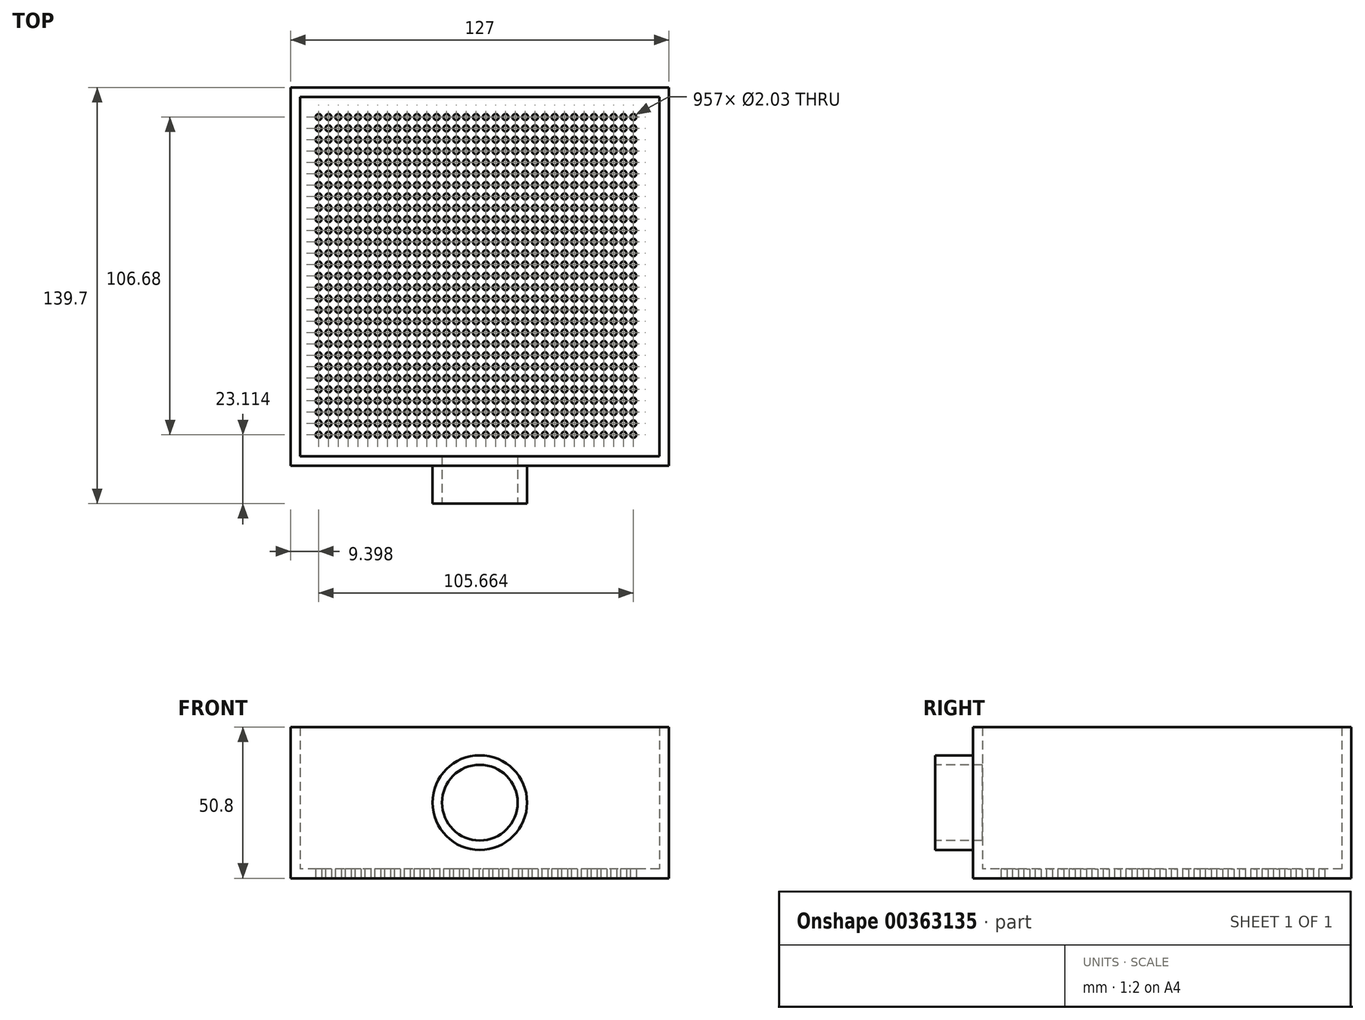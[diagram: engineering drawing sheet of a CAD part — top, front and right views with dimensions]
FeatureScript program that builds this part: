
annotation { "Feature Type Name" : "Feature", "Feature Type Description" : "" }
export const myFeature = defineFeature(function(context is Context, id is Id, definition is map)
    precondition{}
    {
        {
            var Q0;
            Q0=qCreatedBy(makeId("Top.planeOp"),FACE);
            var sketch = newSketch(context, id + "F0", { "sketchPlane" : qUnion([Q0])});
            skLineSegment(sketch, "E0.bottom", {"start": v(0, 0) * mm, "end": v(-127, 0) * mm});
            skLineSegment(sketch, "E0.top", {"start": v(0, -127) * mm, "end": v(-127, -127) * mm});
            skLineSegment(sketch, "E0.left", {"start": v(0, 0) * mm, "end": v(0, -127) * mm});
            skLineSegment(sketch, "E0.right", {"start": v(-127, 0) * mm, "end": v(-127, -127) * mm});
            skSolve(sketch);
        }
        {
            var Q0;
            Q0 = qSketchRegion(id + "F0", true);
            extrude(context, id + "F1", {"entities" : qUnion([Q0]), "depth" : 50.8 * mm});
        }
        {
            var Q0;
            Q0=makeQuery(id+"F1.opExtrude","CAP_FACE",FACE,{"disambiguationData":[OSD([sQuery(id+"F0.wireOp",EDGE,"E0.bottom"),sQuery(id+"F0.wireOp",EDGE,"E0.top"),sQuery(id+"F0.wireOp",EDGE,"E0.left"),sQuery(id+"F0.wireOp",EDGE,"E0.right")])],"isStart":false});
            shell(context, id + "F2", {"entities" : qUnion([Q0]), "thickness" : 3.17 * mm});
        }
        {
            var Q0;
            Q0=makeQuery(id+"F1.opExtrude","SWEPT_FACE",FACE,{"disambiguationData":[OSD([sQuery(id+"F0.wireOp",EDGE,"E0.top")])]});
            var sketch = newSketch(context, id + "F3", { "sketchPlane" : qUnion([Q0])});
            skCircle(sketch, "E1", {"center": v(-63.5, 25.4) * mm, "radius": 15.88 * mm});
            skSolve(sketch);
        }
        {
            var Q0;
            Q0=makeQuery(id+"F3.imprint","IMPRINT",FACE,{"disambiguationData":[TD([[makeQuery(id+"F3.imprint","IMPRINT",EDGE,{"derivedFrom":sQuery(id+"F3.wireOp",EDGE,"E1")}),1.0]])]});
            extrude(context, id + "F4", {"entities" : qUnion([Q0]), "operationType" : NewBodyOperationType.ADD, "depth" : 50.8 * mm});
        }
        {
            var Q0;
            Q0=makeQuery(id+"F4.opExtrude","CAP_FACE",FACE,{"disambiguationData":[OSD([sQuery(id+"F3.wireOp",EDGE,"E1")])],"isStart":false});
            var sketch = newSketch(context, id + "F5", { "sketchPlane" : qUnion([Q0])});
            skCircle(sketch, "E2", {"center": v(-63.5, 25.4) * mm, "radius": 12.7 * mm});
            skSolve(sketch);
        }
        {
            var Q0;
            Q0=sQuery(id+"F5.wireOp",VERTEX,"E2.center");
            var Q1;
            Q1=makeQuery(id+"F1.opExtrude","SWEPT_BODY",BODY,{"disambiguationData":[OSD([sQuery(id+"F0.wireOp",EDGE,"E0.bottom"),sQuery(id+"F0.wireOp",EDGE,"E0.top"),sQuery(id+"F0.wireOp",EDGE,"E0.left"),sQuery(id+"F0.wireOp",EDGE,"E0.right")])]});
            hole(context, id + "F6", {"style" : HoleStyle.SIMPLE, "endStyle" : HoleEndStyle.BLIND, "holeDiameter" : 25.4 * mm, "holeDepth" : 76.2 * mm, "isTappedThrough" : true, "tappedDepth" : 12.7 * mm, "tapClearance" : 3, "locations" : qUnion([Q0]), "scope" : qUnion([Q1])});
        }
        {
            var Q0;
            Q0=makeQuery(id+"F1.opExtrude","CAP_FACE",FACE,{"disambiguationData":[OSD([sQuery(id+"F0.wireOp",EDGE,"E0.bottom"),sQuery(id+"F0.wireOp",EDGE,"E0.top"),sQuery(id+"F0.wireOp",EDGE,"E0.left"),sQuery(id+"F0.wireOp",EDGE,"E0.right")])],"isStart":true});
            var sketch = newSketch(context, id + "F7", { "sketchPlane" : qUnion([Q0])});
            skLineSegment(sketch, "E3.0", {"start": v(-121.92, 5.08) * mm, "end": v(-121.92, 121.92) * mm});
            skLineSegment(sketch, "E3.1", {"start": v(-5.08, 5.08) * mm, "end": v(-121.92, 5.08) * mm});
            skLineSegment(sketch, "E3.2", {"start": v(-5.08, 5.08) * mm, "end": v(-5.08, 121.92) * mm});
            skLineSegment(sketch, "E3.3", {"start": v(-5.08, 121.92) * mm, "end": v(-121.92, 121.92) * mm});
            skCircle(sketch, "E4", {"center": v(-120.9, 6.1) * mm, "radius": 1.02 * mm});
            skCircle(sketch, "E5.0.1.0", {"center": v(-120.9, 9.9) * mm, "radius": 1.02 * mm});
            skCircle(sketch, "E5.0.2.0", {"center": v(-120.9, 13.72) * mm, "radius": 1.02 * mm});
            skCircle(sketch, "E5.0.3.0", {"center": v(-120.9, 17.53) * mm, "radius": 1.02 * mm});
            skCircle(sketch, "E5.0.4.0", {"center": v(-120.9, 21.34) * mm, "radius": 1.02 * mm});
            skCircle(sketch, "E5.0.5.0", {"center": v(-120.9, 25.15) * mm, "radius": 1.02 * mm});
            skCircle(sketch, "E5.0.6.0", {"center": v(-120.9, 28.96) * mm, "radius": 1.02 * mm});
            skCircle(sketch, "E5.0.7.0", {"center": v(-120.9, 32.77) * mm, "radius": 1.02 * mm});
            skCircle(sketch, "E5.0.8.0", {"center": v(-120.9, 36.58) * mm, "radius": 1.02 * mm});
            skCircle(sketch, "E5.0.9.0", {"center": v(-120.9, 40.39) * mm, "radius": 1.02 * mm});
            skCircle(sketch, "E5.0.10.0", {"center": v(-120.9, 44.2) * mm, "radius": 1.02 * mm});
            skCircle(sketch, "E5.0.11.0", {"center": v(-120.9, 48) * mm, "radius": 1.02 * mm});
            skCircle(sketch, "E5.0.12.0", {"center": v(-120.9, 51.82) * mm, "radius": 1.02 * mm});
            skCircle(sketch, "E5.0.13.0", {"center": v(-120.9, 55.63) * mm, "radius": 1.02 * mm});
            skCircle(sketch, "E5.0.14.0", {"center": v(-120.9, 59.44) * mm, "radius": 1.02 * mm});
            skCircle(sketch, "E5.0.15.0", {"center": v(-120.9, 63.25) * mm, "radius": 1.02 * mm});
            skCircle(sketch, "E5.0.16.0", {"center": v(-120.9, 67.06) * mm, "radius": 1.02 * mm});
            skCircle(sketch, "E5.0.17.0", {"center": v(-120.9, 70.87) * mm, "radius": 1.02 * mm});
            skCircle(sketch, "E5.0.18.0", {"center": v(-120.9, 74.68) * mm, "radius": 1.02 * mm});
            skCircle(sketch, "E5.0.19.0", {"center": v(-120.9, 78.49) * mm, "radius": 1.02 * mm});
            skCircle(sketch, "E5.0.20.0", {"center": v(-120.9, 82.3) * mm, "radius": 1.02 * mm});
            skCircle(sketch, "E5.0.21.0", {"center": v(-120.9, 86.1) * mm, "radius": 1.02 * mm});
            skCircle(sketch, "E5.0.22.0", {"center": v(-120.9, 89.92) * mm, "radius": 1.02 * mm});
            skCircle(sketch, "E5.0.23.0", {"center": v(-120.9, 93.73) * mm, "radius": 1.02 * mm});
            skCircle(sketch, "E5.0.24.0", {"center": v(-120.9, 97.54) * mm, "radius": 1.02 * mm});
            skCircle(sketch, "E5.0.25.0", {"center": v(-120.9, 101.35) * mm, "radius": 1.02 * mm});
            skCircle(sketch, "E5.0.26.0", {"center": v(-120.9, 105.16) * mm, "radius": 1.02 * mm});
            skCircle(sketch, "E5.0.27.0", {"center": v(-120.9, 108.97) * mm, "radius": 1.02 * mm});
            skCircle(sketch, "E5.0.28.0", {"center": v(-120.9, 112.78) * mm, "radius": 1.02 * mm});
            skCircle(sketch, "E5.0.29.0", {"center": v(-120.9, 116.59) * mm, "radius": 1.02 * mm});
            skCircle(sketch, "E5.0.30.0", {"center": v(-120.9, 120.4) * mm, "radius": 1.02 * mm});
            skCircle(sketch, "E5.1.0.0", {"center": v(-117.6, 6.1) * mm, "radius": 1.02 * mm});
            skCircle(sketch, "E5.1.1.0", {"center": v(-117.6, 9.9) * mm, "radius": 1.02 * mm});
            skCircle(sketch, "E5.1.2.0", {"center": v(-117.6, 13.72) * mm, "radius": 1.02 * mm});
            skCircle(sketch, "E5.1.3.0", {"center": v(-117.6, 17.53) * mm, "radius": 1.02 * mm});
            skCircle(sketch, "E5.1.4.0", {"center": v(-117.6, 21.34) * mm, "radius": 1.02 * mm});
            skCircle(sketch, "E5.1.5.0", {"center": v(-117.6, 25.15) * mm, "radius": 1.02 * mm});
            skCircle(sketch, "E5.1.6.0", {"center": v(-117.6, 28.96) * mm, "radius": 1.02 * mm});
            skCircle(sketch, "E5.1.7.0", {"center": v(-117.6, 32.77) * mm, "radius": 1.02 * mm});
            skCircle(sketch, "E5.1.8.0", {"center": v(-117.6, 36.58) * mm, "radius": 1.02 * mm});
            skCircle(sketch, "E5.1.9.0", {"center": v(-117.6, 40.39) * mm, "radius": 1.02 * mm});
            skCircle(sketch, "E5.1.10.0", {"center": v(-117.6, 44.2) * mm, "radius": 1.02 * mm});
            skCircle(sketch, "E5.1.11.0", {"center": v(-117.6, 48) * mm, "radius": 1.02 * mm});
            skCircle(sketch, "E5.1.12.0", {"center": v(-117.6, 51.82) * mm, "radius": 1.02 * mm});
            skCircle(sketch, "E5.1.13.0", {"center": v(-117.6, 55.63) * mm, "radius": 1.02 * mm});
            skCircle(sketch, "E5.1.14.0", {"center": v(-117.6, 59.44) * mm, "radius": 1.02 * mm});
            skCircle(sketch, "E5.1.15.0", {"center": v(-117.6, 63.25) * mm, "radius": 1.02 * mm});
            skCircle(sketch, "E5.1.16.0", {"center": v(-117.6, 67.06) * mm, "radius": 1.02 * mm});
            skCircle(sketch, "E5.1.17.0", {"center": v(-117.6, 70.87) * mm, "radius": 1.02 * mm});
            skCircle(sketch, "E5.1.18.0", {"center": v(-117.6, 74.68) * mm, "radius": 1.02 * mm});
            skCircle(sketch, "E5.1.19.0", {"center": v(-117.6, 78.49) * mm, "radius": 1.02 * mm});
            skCircle(sketch, "E5.1.20.0", {"center": v(-117.6, 82.3) * mm, "radius": 1.02 * mm});
            skCircle(sketch, "E5.1.21.0", {"center": v(-117.6, 86.1) * mm, "radius": 1.02 * mm});
            skCircle(sketch, "E5.1.22.0", {"center": v(-117.6, 89.92) * mm, "radius": 1.02 * mm});
            skCircle(sketch, "E5.1.23.0", {"center": v(-117.6, 93.73) * mm, "radius": 1.02 * mm});
            skCircle(sketch, "E5.1.24.0", {"center": v(-117.6, 97.54) * mm, "radius": 1.02 * mm});
            skCircle(sketch, "E5.1.25.0", {"center": v(-117.6, 101.35) * mm, "radius": 1.02 * mm});
            skCircle(sketch, "E5.1.26.0", {"center": v(-117.6, 105.16) * mm, "radius": 1.02 * mm});
            skCircle(sketch, "E5.1.27.0", {"center": v(-117.6, 108.97) * mm, "radius": 1.02 * mm});
            skCircle(sketch, "E5.1.28.0", {"center": v(-117.6, 112.78) * mm, "radius": 1.02 * mm});
            skCircle(sketch, "E5.1.29.0", {"center": v(-117.6, 116.59) * mm, "radius": 1.02 * mm});
            skCircle(sketch, "E5.1.30.0", {"center": v(-117.6, 120.4) * mm, "radius": 1.02 * mm});
            skCircle(sketch, "E5.2.0.0", {"center": v(-114.3, 6.1) * mm, "radius": 1.02 * mm});
            skCircle(sketch, "E5.2.1.0", {"center": v(-114.3, 9.9) * mm, "radius": 1.02 * mm});
            skCircle(sketch, "E5.2.2.0", {"center": v(-114.3, 13.72) * mm, "radius": 1.02 * mm});
            skCircle(sketch, "E5.2.3.0", {"center": v(-114.3, 17.53) * mm, "radius": 1.02 * mm});
            skCircle(sketch, "E5.2.4.0", {"center": v(-114.3, 21.34) * mm, "radius": 1.02 * mm});
            skCircle(sketch, "E5.2.5.0", {"center": v(-114.3, 25.15) * mm, "radius": 1.02 * mm});
            skCircle(sketch, "E5.2.6.0", {"center": v(-114.3, 28.96) * mm, "radius": 1.02 * mm});
            skCircle(sketch, "E5.2.7.0", {"center": v(-114.3, 32.77) * mm, "radius": 1.02 * mm});
            skCircle(sketch, "E5.2.8.0", {"center": v(-114.3, 36.58) * mm, "radius": 1.02 * mm});
            skCircle(sketch, "E5.2.9.0", {"center": v(-114.3, 40.39) * mm, "radius": 1.02 * mm});
            skCircle(sketch, "E5.2.10.0", {"center": v(-114.3, 44.2) * mm, "radius": 1.02 * mm});
            skCircle(sketch, "E5.2.11.0", {"center": v(-114.3, 48) * mm, "radius": 1.02 * mm});
            skCircle(sketch, "E5.2.12.0", {"center": v(-114.3, 51.82) * mm, "radius": 1.02 * mm});
            skCircle(sketch, "E5.2.13.0", {"center": v(-114.3, 55.63) * mm, "radius": 1.02 * mm});
            skCircle(sketch, "E5.2.14.0", {"center": v(-114.3, 59.44) * mm, "radius": 1.02 * mm});
            skCircle(sketch, "E5.2.15.0", {"center": v(-114.3, 63.25) * mm, "radius": 1.02 * mm});
            skCircle(sketch, "E5.2.16.0", {"center": v(-114.3, 67.06) * mm, "radius": 1.02 * mm});
            skCircle(sketch, "E5.2.17.0", {"center": v(-114.3, 70.87) * mm, "radius": 1.02 * mm});
            skCircle(sketch, "E5.2.18.0", {"center": v(-114.3, 74.68) * mm, "radius": 1.02 * mm});
            skCircle(sketch, "E5.2.19.0", {"center": v(-114.3, 78.49) * mm, "radius": 1.02 * mm});
            skCircle(sketch, "E5.2.20.0", {"center": v(-114.3, 82.3) * mm, "radius": 1.02 * mm});
            skCircle(sketch, "E5.2.21.0", {"center": v(-114.3, 86.1) * mm, "radius": 1.02 * mm});
            skCircle(sketch, "E5.2.22.0", {"center": v(-114.3, 89.92) * mm, "radius": 1.02 * mm});
            skCircle(sketch, "E5.2.23.0", {"center": v(-114.3, 93.73) * mm, "radius": 1.02 * mm});
            skCircle(sketch, "E5.2.24.0", {"center": v(-114.3, 97.54) * mm, "radius": 1.02 * mm});
            skCircle(sketch, "E5.2.25.0", {"center": v(-114.3, 101.35) * mm, "radius": 1.02 * mm});
            skCircle(sketch, "E5.2.26.0", {"center": v(-114.3, 105.16) * mm, "radius": 1.02 * mm});
            skCircle(sketch, "E5.2.27.0", {"center": v(-114.3, 108.97) * mm, "radius": 1.02 * mm});
            skCircle(sketch, "E5.2.28.0", {"center": v(-114.3, 112.78) * mm, "radius": 1.02 * mm});
            skCircle(sketch, "E5.2.29.0", {"center": v(-114.3, 116.59) * mm, "radius": 1.02 * mm});
            skCircle(sketch, "E5.2.30.0", {"center": v(-114.3, 120.4) * mm, "radius": 1.02 * mm});
            skCircle(sketch, "E5.3.0.0", {"center": v(-111, 6.1) * mm, "radius": 1.02 * mm});
            skCircle(sketch, "E5.3.1.0", {"center": v(-111, 9.9) * mm, "radius": 1.02 * mm});
            skCircle(sketch, "E5.3.2.0", {"center": v(-111, 13.72) * mm, "radius": 1.02 * mm});
            skCircle(sketch, "E5.3.3.0", {"center": v(-111, 17.53) * mm, "radius": 1.02 * mm});
            skCircle(sketch, "E5.3.4.0", {"center": v(-111, 21.34) * mm, "radius": 1.02 * mm});
            skCircle(sketch, "E5.3.5.0", {"center": v(-111, 25.15) * mm, "radius": 1.02 * mm});
            skCircle(sketch, "E5.3.6.0", {"center": v(-111, 28.96) * mm, "radius": 1.02 * mm});
            skCircle(sketch, "E5.3.7.0", {"center": v(-111, 32.77) * mm, "radius": 1.02 * mm});
            skCircle(sketch, "E5.3.8.0", {"center": v(-111, 36.58) * mm, "radius": 1.02 * mm});
            skCircle(sketch, "E5.3.9.0", {"center": v(-111, 40.39) * mm, "radius": 1.02 * mm});
            skCircle(sketch, "E5.3.10.0", {"center": v(-111, 44.2) * mm, "radius": 1.02 * mm});
            skCircle(sketch, "E5.3.11.0", {"center": v(-111, 48) * mm, "radius": 1.02 * mm});
            skCircle(sketch, "E5.3.12.0", {"center": v(-111, 51.82) * mm, "radius": 1.02 * mm});
            skCircle(sketch, "E5.3.13.0", {"center": v(-111, 55.63) * mm, "radius": 1.02 * mm});
            skCircle(sketch, "E5.3.14.0", {"center": v(-111, 59.44) * mm, "radius": 1.02 * mm});
            skCircle(sketch, "E5.3.15.0", {"center": v(-111, 63.25) * mm, "radius": 1.02 * mm});
            skCircle(sketch, "E5.3.16.0", {"center": v(-111, 67.06) * mm, "radius": 1.02 * mm});
            skCircle(sketch, "E5.3.17.0", {"center": v(-111, 70.87) * mm, "radius": 1.02 * mm});
            skCircle(sketch, "E5.3.18.0", {"center": v(-111, 74.68) * mm, "radius": 1.02 * mm});
            skCircle(sketch, "E5.3.19.0", {"center": v(-111, 78.49) * mm, "radius": 1.02 * mm});
            skCircle(sketch, "E5.3.20.0", {"center": v(-111, 82.3) * mm, "radius": 1.02 * mm});
            skCircle(sketch, "E5.3.21.0", {"center": v(-111, 86.1) * mm, "radius": 1.02 * mm});
            skCircle(sketch, "E5.3.22.0", {"center": v(-111, 89.92) * mm, "radius": 1.02 * mm});
            skCircle(sketch, "E5.3.23.0", {"center": v(-111, 93.73) * mm, "radius": 1.02 * mm});
            skCircle(sketch, "E5.3.24.0", {"center": v(-111, 97.54) * mm, "radius": 1.02 * mm});
            skCircle(sketch, "E5.3.25.0", {"center": v(-111, 101.35) * mm, "radius": 1.02 * mm});
            skCircle(sketch, "E5.3.26.0", {"center": v(-111, 105.16) * mm, "radius": 1.02 * mm});
            skCircle(sketch, "E5.3.27.0", {"center": v(-111, 108.97) * mm, "radius": 1.02 * mm});
            skCircle(sketch, "E5.3.28.0", {"center": v(-111, 112.78) * mm, "radius": 1.02 * mm});
            skCircle(sketch, "E5.3.29.0", {"center": v(-111, 116.59) * mm, "radius": 1.02 * mm});
            skCircle(sketch, "E5.3.30.0", {"center": v(-111, 120.4) * mm, "radius": 1.02 * mm});
            skCircle(sketch, "E5.4.0.0", {"center": v(-107.7, 6.1) * mm, "radius": 1.02 * mm});
            skCircle(sketch, "E5.4.1.0", {"center": v(-107.7, 9.9) * mm, "radius": 1.02 * mm});
            skCircle(sketch, "E5.4.2.0", {"center": v(-107.7, 13.72) * mm, "radius": 1.02 * mm});
            skCircle(sketch, "E5.4.3.0", {"center": v(-107.7, 17.53) * mm, "radius": 1.02 * mm});
            skCircle(sketch, "E5.4.4.0", {"center": v(-107.7, 21.34) * mm, "radius": 1.02 * mm});
            skCircle(sketch, "E5.4.5.0", {"center": v(-107.7, 25.15) * mm, "radius": 1.02 * mm});
            skCircle(sketch, "E5.4.6.0", {"center": v(-107.7, 28.96) * mm, "radius": 1.02 * mm});
            skCircle(sketch, "E5.4.7.0", {"center": v(-107.7, 32.77) * mm, "radius": 1.02 * mm});
            skCircle(sketch, "E5.4.8.0", {"center": v(-107.7, 36.58) * mm, "radius": 1.02 * mm});
            skCircle(sketch, "E5.4.9.0", {"center": v(-107.7, 40.39) * mm, "radius": 1.02 * mm});
            skCircle(sketch, "E5.4.10.0", {"center": v(-107.7, 44.2) * mm, "radius": 1.02 * mm});
            skCircle(sketch, "E5.4.11.0", {"center": v(-107.7, 48) * mm, "radius": 1.02 * mm});
            skCircle(sketch, "E5.4.12.0", {"center": v(-107.7, 51.82) * mm, "radius": 1.02 * mm});
            skCircle(sketch, "E5.4.13.0", {"center": v(-107.7, 55.63) * mm, "radius": 1.02 * mm});
            skCircle(sketch, "E5.4.14.0", {"center": v(-107.7, 59.44) * mm, "radius": 1.02 * mm});
            skCircle(sketch, "E5.4.15.0", {"center": v(-107.7, 63.25) * mm, "radius": 1.02 * mm});
            skCircle(sketch, "E5.4.16.0", {"center": v(-107.7, 67.06) * mm, "radius": 1.02 * mm});
            skCircle(sketch, "E5.4.17.0", {"center": v(-107.7, 70.87) * mm, "radius": 1.02 * mm});
            skCircle(sketch, "E5.4.18.0", {"center": v(-107.7, 74.68) * mm, "radius": 1.02 * mm});
            skCircle(sketch, "E5.4.19.0", {"center": v(-107.7, 78.49) * mm, "radius": 1.02 * mm});
            skCircle(sketch, "E5.4.20.0", {"center": v(-107.7, 82.3) * mm, "radius": 1.02 * mm});
            skCircle(sketch, "E5.4.21.0", {"center": v(-107.7, 86.1) * mm, "radius": 1.02 * mm});
            skCircle(sketch, "E5.4.22.0", {"center": v(-107.7, 89.92) * mm, "radius": 1.02 * mm});
            skCircle(sketch, "E5.4.23.0", {"center": v(-107.7, 93.73) * mm, "radius": 1.02 * mm});
            skCircle(sketch, "E5.4.24.0", {"center": v(-107.7, 97.54) * mm, "radius": 1.02 * mm});
            skCircle(sketch, "E5.4.25.0", {"center": v(-107.7, 101.35) * mm, "radius": 1.02 * mm});
            skCircle(sketch, "E5.4.26.0", {"center": v(-107.7, 105.16) * mm, "radius": 1.02 * mm});
            skCircle(sketch, "E5.4.27.0", {"center": v(-107.7, 108.97) * mm, "radius": 1.02 * mm});
            skCircle(sketch, "E5.4.28.0", {"center": v(-107.7, 112.78) * mm, "radius": 1.02 * mm});
            skCircle(sketch, "E5.4.29.0", {"center": v(-107.7, 116.59) * mm, "radius": 1.02 * mm});
            skCircle(sketch, "E5.4.30.0", {"center": v(-107.7, 120.4) * mm, "radius": 1.02 * mm});
            skCircle(sketch, "E5.5.0.0", {"center": v(-104.4, 6.1) * mm, "radius": 1.02 * mm});
            skCircle(sketch, "E5.5.1.0", {"center": v(-104.4, 9.9) * mm, "radius": 1.02 * mm});
            skCircle(sketch, "E5.5.2.0", {"center": v(-104.4, 13.72) * mm, "radius": 1.02 * mm});
            skCircle(sketch, "E5.5.3.0", {"center": v(-104.4, 17.53) * mm, "radius": 1.02 * mm});
            skCircle(sketch, "E5.5.4.0", {"center": v(-104.4, 21.34) * mm, "radius": 1.02 * mm});
            skCircle(sketch, "E5.5.5.0", {"center": v(-104.4, 25.15) * mm, "radius": 1.02 * mm});
            skCircle(sketch, "E5.5.6.0", {"center": v(-104.4, 28.96) * mm, "radius": 1.02 * mm});
            skCircle(sketch, "E5.5.7.0", {"center": v(-104.4, 32.77) * mm, "radius": 1.02 * mm});
            skCircle(sketch, "E5.5.8.0", {"center": v(-104.4, 36.58) * mm, "radius": 1.02 * mm});
            skCircle(sketch, "E5.5.9.0", {"center": v(-104.4, 40.39) * mm, "radius": 1.02 * mm});
            skCircle(sketch, "E5.5.10.0", {"center": v(-104.4, 44.2) * mm, "radius": 1.02 * mm});
            skCircle(sketch, "E5.5.11.0", {"center": v(-104.4, 48) * mm, "radius": 1.02 * mm});
            skCircle(sketch, "E5.5.12.0", {"center": v(-104.4, 51.82) * mm, "radius": 1.02 * mm});
            skCircle(sketch, "E5.5.13.0", {"center": v(-104.4, 55.63) * mm, "radius": 1.02 * mm});
            skCircle(sketch, "E5.5.14.0", {"center": v(-104.4, 59.44) * mm, "radius": 1.02 * mm});
            skCircle(sketch, "E5.5.15.0", {"center": v(-104.4, 63.25) * mm, "radius": 1.02 * mm});
            skCircle(sketch, "E5.5.16.0", {"center": v(-104.4, 67.06) * mm, "radius": 1.02 * mm});
            skCircle(sketch, "E5.5.17.0", {"center": v(-104.4, 70.87) * mm, "radius": 1.02 * mm});
            skCircle(sketch, "E5.5.18.0", {"center": v(-104.4, 74.68) * mm, "radius": 1.02 * mm});
            skCircle(sketch, "E5.5.19.0", {"center": v(-104.4, 78.49) * mm, "radius": 1.02 * mm});
            skCircle(sketch, "E5.5.20.0", {"center": v(-104.4, 82.3) * mm, "radius": 1.02 * mm});
            skCircle(sketch, "E5.5.21.0", {"center": v(-104.4, 86.1) * mm, "radius": 1.02 * mm});
            skCircle(sketch, "E5.5.22.0", {"center": v(-104.4, 89.92) * mm, "radius": 1.02 * mm});
            skCircle(sketch, "E5.5.23.0", {"center": v(-104.4, 93.73) * mm, "radius": 1.02 * mm});
            skCircle(sketch, "E5.5.24.0", {"center": v(-104.4, 97.54) * mm, "radius": 1.02 * mm});
            skCircle(sketch, "E5.5.25.0", {"center": v(-104.4, 101.35) * mm, "radius": 1.02 * mm});
            skCircle(sketch, "E5.5.26.0", {"center": v(-104.4, 105.16) * mm, "radius": 1.02 * mm});
            skCircle(sketch, "E5.5.27.0", {"center": v(-104.4, 108.97) * mm, "radius": 1.02 * mm});
            skCircle(sketch, "E5.5.28.0", {"center": v(-104.4, 112.78) * mm, "radius": 1.02 * mm});
            skCircle(sketch, "E5.5.29.0", {"center": v(-104.4, 116.59) * mm, "radius": 1.02 * mm});
            skCircle(sketch, "E5.5.30.0", {"center": v(-104.4, 120.4) * mm, "radius": 1.02 * mm});
            skCircle(sketch, "E5.6.0.0", {"center": v(-101.1, 6.1) * mm, "radius": 1.02 * mm});
            skCircle(sketch, "E5.6.1.0", {"center": v(-101.1, 9.9) * mm, "radius": 1.02 * mm});
            skCircle(sketch, "E5.6.2.0", {"center": v(-101.1, 13.72) * mm, "radius": 1.02 * mm});
            skCircle(sketch, "E5.6.3.0", {"center": v(-101.1, 17.53) * mm, "radius": 1.02 * mm});
            skCircle(sketch, "E5.6.4.0", {"center": v(-101.1, 21.34) * mm, "radius": 1.02 * mm});
            skCircle(sketch, "E5.6.5.0", {"center": v(-101.1, 25.15) * mm, "radius": 1.02 * mm});
            skCircle(sketch, "E5.6.6.0", {"center": v(-101.1, 28.96) * mm, "radius": 1.02 * mm});
            skCircle(sketch, "E5.6.7.0", {"center": v(-101.1, 32.77) * mm, "radius": 1.02 * mm});
            skCircle(sketch, "E5.6.8.0", {"center": v(-101.1, 36.58) * mm, "radius": 1.02 * mm});
            skCircle(sketch, "E5.6.9.0", {"center": v(-101.1, 40.39) * mm, "radius": 1.02 * mm});
            skCircle(sketch, "E5.6.10.0", {"center": v(-101.1, 44.2) * mm, "radius": 1.02 * mm});
            skCircle(sketch, "E5.6.11.0", {"center": v(-101.1, 48) * mm, "radius": 1.02 * mm});
            skCircle(sketch, "E5.6.12.0", {"center": v(-101.1, 51.82) * mm, "radius": 1.02 * mm});
            skCircle(sketch, "E5.6.13.0", {"center": v(-101.1, 55.63) * mm, "radius": 1.02 * mm});
            skCircle(sketch, "E5.6.14.0", {"center": v(-101.1, 59.44) * mm, "radius": 1.02 * mm});
            skCircle(sketch, "E5.6.15.0", {"center": v(-101.1, 63.25) * mm, "radius": 1.02 * mm});
            skCircle(sketch, "E5.6.16.0", {"center": v(-101.1, 67.06) * mm, "radius": 1.02 * mm});
            skCircle(sketch, "E5.6.17.0", {"center": v(-101.1, 70.87) * mm, "radius": 1.02 * mm});
            skCircle(sketch, "E5.6.18.0", {"center": v(-101.1, 74.68) * mm, "radius": 1.02 * mm});
            skCircle(sketch, "E5.6.19.0", {"center": v(-101.1, 78.49) * mm, "radius": 1.02 * mm});
            skCircle(sketch, "E5.6.20.0", {"center": v(-101.1, 82.3) * mm, "radius": 1.02 * mm});
            skCircle(sketch, "E5.6.21.0", {"center": v(-101.1, 86.1) * mm, "radius": 1.02 * mm});
            skCircle(sketch, "E5.6.22.0", {"center": v(-101.1, 89.92) * mm, "radius": 1.02 * mm});
            skCircle(sketch, "E5.6.23.0", {"center": v(-101.1, 93.73) * mm, "radius": 1.02 * mm});
            skCircle(sketch, "E5.6.24.0", {"center": v(-101.1, 97.54) * mm, "radius": 1.02 * mm});
            skCircle(sketch, "E5.6.25.0", {"center": v(-101.1, 101.35) * mm, "radius": 1.02 * mm});
            skCircle(sketch, "E5.6.26.0", {"center": v(-101.1, 105.16) * mm, "radius": 1.02 * mm});
            skCircle(sketch, "E5.6.27.0", {"center": v(-101.1, 108.97) * mm, "radius": 1.02 * mm});
            skCircle(sketch, "E5.6.28.0", {"center": v(-101.1, 112.78) * mm, "radius": 1.02 * mm});
            skCircle(sketch, "E5.6.29.0", {"center": v(-101.1, 116.59) * mm, "radius": 1.02 * mm});
            skCircle(sketch, "E5.6.30.0", {"center": v(-101.1, 120.4) * mm, "radius": 1.02 * mm});
            skCircle(sketch, "E5.7.0.0", {"center": v(-97.79, 6.1) * mm, "radius": 1.02 * mm});
            skCircle(sketch, "E5.7.1.0", {"center": v(-97.79, 9.9) * mm, "radius": 1.02 * mm});
            skCircle(sketch, "E5.7.2.0", {"center": v(-97.79, 13.72) * mm, "radius": 1.02 * mm});
            skCircle(sketch, "E5.7.3.0", {"center": v(-97.79, 17.53) * mm, "radius": 1.02 * mm});
            skCircle(sketch, "E5.7.4.0", {"center": v(-97.79, 21.34) * mm, "radius": 1.02 * mm});
            skCircle(sketch, "E5.7.5.0", {"center": v(-97.79, 25.15) * mm, "radius": 1.02 * mm});
            skCircle(sketch, "E5.7.6.0", {"center": v(-97.79, 28.96) * mm, "radius": 1.02 * mm});
            skCircle(sketch, "E5.7.7.0", {"center": v(-97.79, 32.77) * mm, "radius": 1.02 * mm});
            skCircle(sketch, "E5.7.8.0", {"center": v(-97.79, 36.58) * mm, "radius": 1.02 * mm});
            skCircle(sketch, "E5.7.9.0", {"center": v(-97.79, 40.39) * mm, "radius": 1.02 * mm});
            skCircle(sketch, "E5.7.10.0", {"center": v(-97.79, 44.2) * mm, "radius": 1.02 * mm});
            skCircle(sketch, "E5.7.11.0", {"center": v(-97.79, 48) * mm, "radius": 1.02 * mm});
            skCircle(sketch, "E5.7.12.0", {"center": v(-97.79, 51.82) * mm, "radius": 1.02 * mm});
            skCircle(sketch, "E5.7.13.0", {"center": v(-97.79, 55.63) * mm, "radius": 1.02 * mm});
            skCircle(sketch, "E5.7.14.0", {"center": v(-97.79, 59.44) * mm, "radius": 1.02 * mm});
            skCircle(sketch, "E5.7.15.0", {"center": v(-97.79, 63.25) * mm, "radius": 1.02 * mm});
            skCircle(sketch, "E5.7.16.0", {"center": v(-97.79, 67.06) * mm, "radius": 1.02 * mm});
            skCircle(sketch, "E5.7.17.0", {"center": v(-97.79, 70.87) * mm, "radius": 1.02 * mm});
            skCircle(sketch, "E5.7.18.0", {"center": v(-97.79, 74.68) * mm, "radius": 1.02 * mm});
            skCircle(sketch, "E5.7.19.0", {"center": v(-97.79, 78.49) * mm, "radius": 1.02 * mm});
            skCircle(sketch, "E5.7.20.0", {"center": v(-97.79, 82.3) * mm, "radius": 1.02 * mm});
            skCircle(sketch, "E5.7.21.0", {"center": v(-97.79, 86.1) * mm, "radius": 1.02 * mm});
            skCircle(sketch, "E5.7.22.0", {"center": v(-97.79, 89.92) * mm, "radius": 1.02 * mm});
            skCircle(sketch, "E5.7.23.0", {"center": v(-97.79, 93.73) * mm, "radius": 1.02 * mm});
            skCircle(sketch, "E5.7.24.0", {"center": v(-97.79, 97.54) * mm, "radius": 1.02 * mm});
            skCircle(sketch, "E5.7.25.0", {"center": v(-97.79, 101.35) * mm, "radius": 1.02 * mm});
            skCircle(sketch, "E5.7.26.0", {"center": v(-97.79, 105.16) * mm, "radius": 1.02 * mm});
            skCircle(sketch, "E5.7.27.0", {"center": v(-97.79, 108.97) * mm, "radius": 1.02 * mm});
            skCircle(sketch, "E5.7.28.0", {"center": v(-97.79, 112.78) * mm, "radius": 1.02 * mm});
            skCircle(sketch, "E5.7.29.0", {"center": v(-97.79, 116.59) * mm, "radius": 1.02 * mm});
            skCircle(sketch, "E5.7.30.0", {"center": v(-97.79, 120.4) * mm, "radius": 1.02 * mm});
            skCircle(sketch, "E5.8.0.0", {"center": v(-94.49, 6.1) * mm, "radius": 1.02 * mm});
            skCircle(sketch, "E5.8.1.0", {"center": v(-94.49, 9.9) * mm, "radius": 1.02 * mm});
            skCircle(sketch, "E5.8.2.0", {"center": v(-94.49, 13.72) * mm, "radius": 1.02 * mm});
            skCircle(sketch, "E5.8.3.0", {"center": v(-94.49, 17.53) * mm, "radius": 1.02 * mm});
            skCircle(sketch, "E5.8.4.0", {"center": v(-94.49, 21.34) * mm, "radius": 1.02 * mm});
            skCircle(sketch, "E5.8.5.0", {"center": v(-94.49, 25.15) * mm, "radius": 1.02 * mm});
            skCircle(sketch, "E5.8.6.0", {"center": v(-94.49, 28.96) * mm, "radius": 1.02 * mm});
            skCircle(sketch, "E5.8.7.0", {"center": v(-94.49, 32.77) * mm, "radius": 1.02 * mm});
            skCircle(sketch, "E5.8.8.0", {"center": v(-94.49, 36.58) * mm, "radius": 1.02 * mm});
            skCircle(sketch, "E5.8.9.0", {"center": v(-94.49, 40.39) * mm, "radius": 1.02 * mm});
            skCircle(sketch, "E5.8.10.0", {"center": v(-94.49, 44.2) * mm, "radius": 1.02 * mm});
            skCircle(sketch, "E5.8.11.0", {"center": v(-94.49, 48) * mm, "radius": 1.02 * mm});
            skCircle(sketch, "E5.8.12.0", {"center": v(-94.49, 51.82) * mm, "radius": 1.02 * mm});
            skCircle(sketch, "E5.8.13.0", {"center": v(-94.49, 55.63) * mm, "radius": 1.02 * mm});
            skCircle(sketch, "E5.8.14.0", {"center": v(-94.49, 59.44) * mm, "radius": 1.02 * mm});
            skCircle(sketch, "E5.8.15.0", {"center": v(-94.49, 63.25) * mm, "radius": 1.02 * mm});
            skCircle(sketch, "E5.8.16.0", {"center": v(-94.49, 67.06) * mm, "radius": 1.02 * mm});
            skCircle(sketch, "E5.8.17.0", {"center": v(-94.49, 70.87) * mm, "radius": 1.02 * mm});
            skCircle(sketch, "E5.8.18.0", {"center": v(-94.49, 74.68) * mm, "radius": 1.02 * mm});
            skCircle(sketch, "E5.8.19.0", {"center": v(-94.49, 78.49) * mm, "radius": 1.02 * mm});
            skCircle(sketch, "E5.8.20.0", {"center": v(-94.49, 82.3) * mm, "radius": 1.02 * mm});
            skCircle(sketch, "E5.8.21.0", {"center": v(-94.49, 86.1) * mm, "radius": 1.02 * mm});
            skCircle(sketch, "E5.8.22.0", {"center": v(-94.49, 89.92) * mm, "radius": 1.02 * mm});
            skCircle(sketch, "E5.8.23.0", {"center": v(-94.49, 93.73) * mm, "radius": 1.02 * mm});
            skCircle(sketch, "E5.8.24.0", {"center": v(-94.49, 97.54) * mm, "radius": 1.02 * mm});
            skCircle(sketch, "E5.8.25.0", {"center": v(-94.49, 101.35) * mm, "radius": 1.02 * mm});
            skCircle(sketch, "E5.8.26.0", {"center": v(-94.49, 105.16) * mm, "radius": 1.02 * mm});
            skCircle(sketch, "E5.8.27.0", {"center": v(-94.49, 108.97) * mm, "radius": 1.02 * mm});
            skCircle(sketch, "E5.8.28.0", {"center": v(-94.49, 112.78) * mm, "radius": 1.02 * mm});
            skCircle(sketch, "E5.8.29.0", {"center": v(-94.49, 116.59) * mm, "radius": 1.02 * mm});
            skCircle(sketch, "E5.8.30.0", {"center": v(-94.49, 120.4) * mm, "radius": 1.02 * mm});
            skCircle(sketch, "E5.9.0.0", {"center": v(-91.19, 6.1) * mm, "radius": 1.02 * mm});
            skCircle(sketch, "E5.9.1.0", {"center": v(-91.19, 9.9) * mm, "radius": 1.02 * mm});
            skCircle(sketch, "E5.9.2.0", {"center": v(-91.19, 13.72) * mm, "radius": 1.02 * mm});
            skCircle(sketch, "E5.9.3.0", {"center": v(-91.19, 17.53) * mm, "radius": 1.02 * mm});
            skCircle(sketch, "E5.9.4.0", {"center": v(-91.19, 21.34) * mm, "radius": 1.02 * mm});
            skCircle(sketch, "E5.9.5.0", {"center": v(-91.19, 25.15) * mm, "radius": 1.02 * mm});
            skCircle(sketch, "E5.9.6.0", {"center": v(-91.19, 28.96) * mm, "radius": 1.02 * mm});
            skCircle(sketch, "E5.9.7.0", {"center": v(-91.19, 32.77) * mm, "radius": 1.02 * mm});
            skCircle(sketch, "E5.9.8.0", {"center": v(-91.19, 36.58) * mm, "radius": 1.02 * mm});
            skCircle(sketch, "E5.9.9.0", {"center": v(-91.19, 40.39) * mm, "radius": 1.02 * mm});
            skCircle(sketch, "E5.9.10.0", {"center": v(-91.19, 44.2) * mm, "radius": 1.02 * mm});
            skCircle(sketch, "E5.9.11.0", {"center": v(-91.19, 48) * mm, "radius": 1.02 * mm});
            skCircle(sketch, "E5.9.12.0", {"center": v(-91.19, 51.82) * mm, "radius": 1.02 * mm});
            skCircle(sketch, "E5.9.13.0", {"center": v(-91.19, 55.63) * mm, "radius": 1.02 * mm});
            skCircle(sketch, "E5.9.14.0", {"center": v(-91.19, 59.44) * mm, "radius": 1.02 * mm});
            skCircle(sketch, "E5.9.15.0", {"center": v(-91.19, 63.25) * mm, "radius": 1.02 * mm});
            skCircle(sketch, "E5.9.16.0", {"center": v(-91.19, 67.06) * mm, "radius": 1.02 * mm});
            skCircle(sketch, "E5.9.17.0", {"center": v(-91.19, 70.87) * mm, "radius": 1.02 * mm});
            skCircle(sketch, "E5.9.18.0", {"center": v(-91.19, 74.68) * mm, "radius": 1.02 * mm});
            skCircle(sketch, "E5.9.19.0", {"center": v(-91.19, 78.49) * mm, "radius": 1.02 * mm});
            skCircle(sketch, "E5.9.20.0", {"center": v(-91.19, 82.3) * mm, "radius": 1.02 * mm});
            skCircle(sketch, "E5.9.21.0", {"center": v(-91.19, 86.1) * mm, "radius": 1.02 * mm});
            skCircle(sketch, "E5.9.22.0", {"center": v(-91.19, 89.92) * mm, "radius": 1.02 * mm});
            skCircle(sketch, "E5.9.23.0", {"center": v(-91.19, 93.73) * mm, "radius": 1.02 * mm});
            skCircle(sketch, "E5.9.24.0", {"center": v(-91.19, 97.54) * mm, "radius": 1.02 * mm});
            skCircle(sketch, "E5.9.25.0", {"center": v(-91.19, 101.35) * mm, "radius": 1.02 * mm});
            skCircle(sketch, "E5.9.26.0", {"center": v(-91.19, 105.16) * mm, "radius": 1.02 * mm});
            skCircle(sketch, "E5.9.27.0", {"center": v(-91.19, 108.97) * mm, "radius": 1.02 * mm});
            skCircle(sketch, "E5.9.28.0", {"center": v(-91.19, 112.78) * mm, "radius": 1.02 * mm});
            skCircle(sketch, "E5.9.29.0", {"center": v(-91.19, 116.59) * mm, "radius": 1.02 * mm});
            skCircle(sketch, "E5.9.30.0", {"center": v(-91.19, 120.4) * mm, "radius": 1.02 * mm});
            skCircle(sketch, "E5.10.0.0", {"center": v(-87.88, 6.1) * mm, "radius": 1.02 * mm});
            skCircle(sketch, "E5.10.1.0", {"center": v(-87.88, 9.9) * mm, "radius": 1.02 * mm});
            skCircle(sketch, "E5.10.2.0", {"center": v(-87.88, 13.72) * mm, "radius": 1.02 * mm});
            skCircle(sketch, "E5.10.3.0", {"center": v(-87.88, 17.53) * mm, "radius": 1.02 * mm});
            skCircle(sketch, "E5.10.4.0", {"center": v(-87.88, 21.34) * mm, "radius": 1.02 * mm});
            skCircle(sketch, "E5.10.5.0", {"center": v(-87.88, 25.15) * mm, "radius": 1.02 * mm});
            skCircle(sketch, "E5.10.6.0", {"center": v(-87.88, 28.96) * mm, "radius": 1.02 * mm});
            skCircle(sketch, "E5.10.7.0", {"center": v(-87.88, 32.77) * mm, "radius": 1.02 * mm});
            skCircle(sketch, "E5.10.8.0", {"center": v(-87.88, 36.58) * mm, "radius": 1.02 * mm});
            skCircle(sketch, "E5.10.9.0", {"center": v(-87.88, 40.39) * mm, "radius": 1.02 * mm});
            skCircle(sketch, "E5.10.10.0", {"center": v(-87.88, 44.2) * mm, "radius": 1.02 * mm});
            skCircle(sketch, "E5.10.11.0", {"center": v(-87.88, 48) * mm, "radius": 1.02 * mm});
            skCircle(sketch, "E5.10.12.0", {"center": v(-87.88, 51.82) * mm, "radius": 1.02 * mm});
            skCircle(sketch, "E5.10.13.0", {"center": v(-87.88, 55.63) * mm, "radius": 1.02 * mm});
            skCircle(sketch, "E5.10.14.0", {"center": v(-87.88, 59.44) * mm, "radius": 1.02 * mm});
            skCircle(sketch, "E5.10.15.0", {"center": v(-87.88, 63.25) * mm, "radius": 1.02 * mm});
            skCircle(sketch, "E5.10.16.0", {"center": v(-87.88, 67.06) * mm, "radius": 1.02 * mm});
            skCircle(sketch, "E5.10.17.0", {"center": v(-87.88, 70.87) * mm, "radius": 1.02 * mm});
            skCircle(sketch, "E5.10.18.0", {"center": v(-87.88, 74.68) * mm, "radius": 1.02 * mm});
            skCircle(sketch, "E5.10.19.0", {"center": v(-87.88, 78.49) * mm, "radius": 1.02 * mm});
            skCircle(sketch, "E5.10.20.0", {"center": v(-87.88, 82.3) * mm, "radius": 1.02 * mm});
            skCircle(sketch, "E5.10.21.0", {"center": v(-87.88, 86.1) * mm, "radius": 1.02 * mm});
            skCircle(sketch, "E5.10.22.0", {"center": v(-87.88, 89.92) * mm, "radius": 1.02 * mm});
            skCircle(sketch, "E5.10.23.0", {"center": v(-87.88, 93.73) * mm, "radius": 1.02 * mm});
            skCircle(sketch, "E5.10.24.0", {"center": v(-87.88, 97.54) * mm, "radius": 1.02 * mm});
            skCircle(sketch, "E5.10.25.0", {"center": v(-87.88, 101.35) * mm, "radius": 1.02 * mm});
            skCircle(sketch, "E5.10.26.0", {"center": v(-87.88, 105.16) * mm, "radius": 1.02 * mm});
            skCircle(sketch, "E5.10.27.0", {"center": v(-87.88, 108.97) * mm, "radius": 1.02 * mm});
            skCircle(sketch, "E5.10.28.0", {"center": v(-87.88, 112.78) * mm, "radius": 1.02 * mm});
            skCircle(sketch, "E5.10.29.0", {"center": v(-87.88, 116.59) * mm, "radius": 1.02 * mm});
            skCircle(sketch, "E5.10.30.0", {"center": v(-87.88, 120.4) * mm, "radius": 1.02 * mm});
            skCircle(sketch, "E5.11.0.0", {"center": v(-84.58, 6.1) * mm, "radius": 1.02 * mm});
            skCircle(sketch, "E5.11.1.0", {"center": v(-84.58, 9.9) * mm, "radius": 1.02 * mm});
            skCircle(sketch, "E5.11.2.0", {"center": v(-84.58, 13.72) * mm, "radius": 1.02 * mm});
            skCircle(sketch, "E5.11.3.0", {"center": v(-84.58, 17.53) * mm, "radius": 1.02 * mm});
            skCircle(sketch, "E5.11.4.0", {"center": v(-84.58, 21.34) * mm, "radius": 1.02 * mm});
            skCircle(sketch, "E5.11.5.0", {"center": v(-84.58, 25.15) * mm, "radius": 1.02 * mm});
            skCircle(sketch, "E5.11.6.0", {"center": v(-84.58, 28.96) * mm, "radius": 1.02 * mm});
            skCircle(sketch, "E5.11.7.0", {"center": v(-84.58, 32.77) * mm, "radius": 1.02 * mm});
            skCircle(sketch, "E5.11.8.0", {"center": v(-84.58, 36.58) * mm, "radius": 1.02 * mm});
            skCircle(sketch, "E5.11.9.0", {"center": v(-84.58, 40.39) * mm, "radius": 1.02 * mm});
            skCircle(sketch, "E5.11.10.0", {"center": v(-84.58, 44.2) * mm, "radius": 1.02 * mm});
            skCircle(sketch, "E5.11.11.0", {"center": v(-84.58, 48) * mm, "radius": 1.02 * mm});
            skCircle(sketch, "E5.11.12.0", {"center": v(-84.58, 51.82) * mm, "radius": 1.02 * mm});
            skCircle(sketch, "E5.11.13.0", {"center": v(-84.58, 55.63) * mm, "radius": 1.02 * mm});
            skCircle(sketch, "E5.11.14.0", {"center": v(-84.58, 59.44) * mm, "radius": 1.02 * mm});
            skCircle(sketch, "E5.11.15.0", {"center": v(-84.58, 63.25) * mm, "radius": 1.02 * mm});
            skCircle(sketch, "E5.11.16.0", {"center": v(-84.58, 67.06) * mm, "radius": 1.02 * mm});
            skCircle(sketch, "E5.11.17.0", {"center": v(-84.58, 70.87) * mm, "radius": 1.02 * mm});
            skCircle(sketch, "E5.11.18.0", {"center": v(-84.58, 74.68) * mm, "radius": 1.02 * mm});
            skCircle(sketch, "E5.11.19.0", {"center": v(-84.58, 78.49) * mm, "radius": 1.02 * mm});
            skCircle(sketch, "E5.11.20.0", {"center": v(-84.58, 82.3) * mm, "radius": 1.02 * mm});
            skCircle(sketch, "E5.11.21.0", {"center": v(-84.58, 86.1) * mm, "radius": 1.02 * mm});
            skCircle(sketch, "E5.11.22.0", {"center": v(-84.58, 89.92) * mm, "radius": 1.02 * mm});
            skCircle(sketch, "E5.11.23.0", {"center": v(-84.58, 93.73) * mm, "radius": 1.02 * mm});
            skCircle(sketch, "E5.11.24.0", {"center": v(-84.58, 97.54) * mm, "radius": 1.02 * mm});
            skCircle(sketch, "E5.11.25.0", {"center": v(-84.58, 101.35) * mm, "radius": 1.02 * mm});
            skCircle(sketch, "E5.11.26.0", {"center": v(-84.58, 105.16) * mm, "radius": 1.02 * mm});
            skCircle(sketch, "E5.11.27.0", {"center": v(-84.58, 108.97) * mm, "radius": 1.02 * mm});
            skCircle(sketch, "E5.11.28.0", {"center": v(-84.58, 112.78) * mm, "radius": 1.02 * mm});
            skCircle(sketch, "E5.11.29.0", {"center": v(-84.58, 116.59) * mm, "radius": 1.02 * mm});
            skCircle(sketch, "E5.11.30.0", {"center": v(-84.58, 120.4) * mm, "radius": 1.02 * mm});
            skCircle(sketch, "E5.12.0.0", {"center": v(-81.28, 6.1) * mm, "radius": 1.02 * mm});
            skCircle(sketch, "E5.12.1.0", {"center": v(-81.28, 9.9) * mm, "radius": 1.02 * mm});
            skCircle(sketch, "E5.12.2.0", {"center": v(-81.28, 13.72) * mm, "radius": 1.02 * mm});
            skCircle(sketch, "E5.12.3.0", {"center": v(-81.28, 17.53) * mm, "radius": 1.02 * mm});
            skCircle(sketch, "E5.12.4.0", {"center": v(-81.28, 21.34) * mm, "radius": 1.02 * mm});
            skCircle(sketch, "E5.12.5.0", {"center": v(-81.28, 25.15) * mm, "radius": 1.02 * mm});
            skCircle(sketch, "E5.12.6.0", {"center": v(-81.28, 28.96) * mm, "radius": 1.02 * mm});
            skCircle(sketch, "E5.12.7.0", {"center": v(-81.28, 32.77) * mm, "radius": 1.02 * mm});
            skCircle(sketch, "E5.12.8.0", {"center": v(-81.28, 36.58) * mm, "radius": 1.02 * mm});
            skCircle(sketch, "E5.12.9.0", {"center": v(-81.28, 40.39) * mm, "radius": 1.02 * mm});
            skCircle(sketch, "E5.12.10.0", {"center": v(-81.28, 44.2) * mm, "radius": 1.02 * mm});
            skCircle(sketch, "E5.12.11.0", {"center": v(-81.28, 48) * mm, "radius": 1.02 * mm});
            skCircle(sketch, "E5.12.12.0", {"center": v(-81.28, 51.82) * mm, "radius": 1.02 * mm});
            skCircle(sketch, "E5.12.13.0", {"center": v(-81.28, 55.63) * mm, "radius": 1.02 * mm});
            skCircle(sketch, "E5.12.14.0", {"center": v(-81.28, 59.44) * mm, "radius": 1.02 * mm});
            skCircle(sketch, "E5.12.15.0", {"center": v(-81.28, 63.25) * mm, "radius": 1.02 * mm});
            skCircle(sketch, "E5.12.16.0", {"center": v(-81.28, 67.06) * mm, "radius": 1.02 * mm});
            skCircle(sketch, "E5.12.17.0", {"center": v(-81.28, 70.87) * mm, "radius": 1.02 * mm});
            skCircle(sketch, "E5.12.18.0", {"center": v(-81.28, 74.68) * mm, "radius": 1.02 * mm});
            skCircle(sketch, "E5.12.19.0", {"center": v(-81.28, 78.49) * mm, "radius": 1.02 * mm});
            skCircle(sketch, "E5.12.20.0", {"center": v(-81.28, 82.3) * mm, "radius": 1.02 * mm});
            skCircle(sketch, "E5.12.21.0", {"center": v(-81.28, 86.1) * mm, "radius": 1.02 * mm});
            skCircle(sketch, "E5.12.22.0", {"center": v(-81.28, 89.92) * mm, "radius": 1.02 * mm});
            skCircle(sketch, "E5.12.23.0", {"center": v(-81.28, 93.73) * mm, "radius": 1.02 * mm});
            skCircle(sketch, "E5.12.24.0", {"center": v(-81.28, 97.54) * mm, "radius": 1.02 * mm});
            skCircle(sketch, "E5.12.25.0", {"center": v(-81.28, 101.35) * mm, "radius": 1.02 * mm});
            skCircle(sketch, "E5.12.26.0", {"center": v(-81.28, 105.16) * mm, "radius": 1.02 * mm});
            skCircle(sketch, "E5.12.27.0", {"center": v(-81.28, 108.97) * mm, "radius": 1.02 * mm});
            skCircle(sketch, "E5.12.28.0", {"center": v(-81.28, 112.78) * mm, "radius": 1.02 * mm});
            skCircle(sketch, "E5.12.29.0", {"center": v(-81.28, 116.59) * mm, "radius": 1.02 * mm});
            skCircle(sketch, "E5.12.30.0", {"center": v(-81.28, 120.4) * mm, "radius": 1.02 * mm});
            skCircle(sketch, "E5.13.0.0", {"center": v(-77.98, 6.1) * mm, "radius": 1.02 * mm});
            skCircle(sketch, "E5.13.1.0", {"center": v(-77.98, 9.9) * mm, "radius": 1.02 * mm});
            skCircle(sketch, "E5.13.2.0", {"center": v(-77.98, 13.72) * mm, "radius": 1.02 * mm});
            skCircle(sketch, "E5.13.3.0", {"center": v(-77.98, 17.53) * mm, "radius": 1.02 * mm});
            skCircle(sketch, "E5.13.4.0", {"center": v(-77.98, 21.34) * mm, "radius": 1.02 * mm});
            skCircle(sketch, "E5.13.5.0", {"center": v(-77.98, 25.15) * mm, "radius": 1.02 * mm});
            skCircle(sketch, "E5.13.6.0", {"center": v(-77.98, 28.96) * mm, "radius": 1.02 * mm});
            skCircle(sketch, "E5.13.7.0", {"center": v(-77.98, 32.77) * mm, "radius": 1.02 * mm});
            skCircle(sketch, "E5.13.8.0", {"center": v(-77.98, 36.58) * mm, "radius": 1.02 * mm});
            skCircle(sketch, "E5.13.9.0", {"center": v(-77.98, 40.39) * mm, "radius": 1.02 * mm});
            skCircle(sketch, "E5.13.10.0", {"center": v(-77.98, 44.2) * mm, "radius": 1.02 * mm});
            skCircle(sketch, "E5.13.11.0", {"center": v(-77.98, 48) * mm, "radius": 1.02 * mm});
            skCircle(sketch, "E5.13.12.0", {"center": v(-77.98, 51.82) * mm, "radius": 1.02 * mm});
            skCircle(sketch, "E5.13.13.0", {"center": v(-77.98, 55.63) * mm, "radius": 1.02 * mm});
            skCircle(sketch, "E5.13.14.0", {"center": v(-77.98, 59.44) * mm, "radius": 1.02 * mm});
            skCircle(sketch, "E5.13.15.0", {"center": v(-77.98, 63.25) * mm, "radius": 1.02 * mm});
            skCircle(sketch, "E5.13.16.0", {"center": v(-77.98, 67.06) * mm, "radius": 1.02 * mm});
            skCircle(sketch, "E5.13.17.0", {"center": v(-77.98, 70.87) * mm, "radius": 1.02 * mm});
            skCircle(sketch, "E5.13.18.0", {"center": v(-77.98, 74.68) * mm, "radius": 1.02 * mm});
            skCircle(sketch, "E5.13.19.0", {"center": v(-77.98, 78.49) * mm, "radius": 1.02 * mm});
            skCircle(sketch, "E5.13.20.0", {"center": v(-77.98, 82.3) * mm, "radius": 1.02 * mm});
            skCircle(sketch, "E5.13.21.0", {"center": v(-77.98, 86.1) * mm, "radius": 1.02 * mm});
            skCircle(sketch, "E5.13.22.0", {"center": v(-77.98, 89.92) * mm, "radius": 1.02 * mm});
            skCircle(sketch, "E5.13.23.0", {"center": v(-77.98, 93.73) * mm, "radius": 1.02 * mm});
            skCircle(sketch, "E5.13.24.0", {"center": v(-77.98, 97.54) * mm, "radius": 1.02 * mm});
            skCircle(sketch, "E5.13.25.0", {"center": v(-77.98, 101.35) * mm, "radius": 1.02 * mm});
            skCircle(sketch, "E5.13.26.0", {"center": v(-77.98, 105.16) * mm, "radius": 1.02 * mm});
            skCircle(sketch, "E5.13.27.0", {"center": v(-77.98, 108.97) * mm, "radius": 1.02 * mm});
            skCircle(sketch, "E5.13.28.0", {"center": v(-77.98, 112.78) * mm, "radius": 1.02 * mm});
            skCircle(sketch, "E5.13.29.0", {"center": v(-77.98, 116.59) * mm, "radius": 1.02 * mm});
            skCircle(sketch, "E5.13.30.0", {"center": v(-77.98, 120.4) * mm, "radius": 1.02 * mm});
            skCircle(sketch, "E5.14.0.0", {"center": v(-74.68, 6.1) * mm, "radius": 1.02 * mm});
            skCircle(sketch, "E5.14.1.0", {"center": v(-74.68, 9.9) * mm, "radius": 1.02 * mm});
            skCircle(sketch, "E5.14.2.0", {"center": v(-74.68, 13.72) * mm, "radius": 1.02 * mm});
            skCircle(sketch, "E5.14.3.0", {"center": v(-74.68, 17.53) * mm, "radius": 1.02 * mm});
            skCircle(sketch, "E5.14.4.0", {"center": v(-74.68, 21.34) * mm, "radius": 1.02 * mm});
            skCircle(sketch, "E5.14.5.0", {"center": v(-74.68, 25.15) * mm, "radius": 1.02 * mm});
            skCircle(sketch, "E5.14.6.0", {"center": v(-74.68, 28.96) * mm, "radius": 1.02 * mm});
            skCircle(sketch, "E5.14.7.0", {"center": v(-74.68, 32.77) * mm, "radius": 1.02 * mm});
            skCircle(sketch, "E5.14.8.0", {"center": v(-74.68, 36.58) * mm, "radius": 1.02 * mm});
            skCircle(sketch, "E5.14.9.0", {"center": v(-74.68, 40.39) * mm, "radius": 1.02 * mm});
            skCircle(sketch, "E5.14.10.0", {"center": v(-74.68, 44.2) * mm, "radius": 1.02 * mm});
            skCircle(sketch, "E5.14.11.0", {"center": v(-74.68, 48) * mm, "radius": 1.02 * mm});
            skCircle(sketch, "E5.14.12.0", {"center": v(-74.68, 51.82) * mm, "radius": 1.02 * mm});
            skCircle(sketch, "E5.14.13.0", {"center": v(-74.68, 55.63) * mm, "radius": 1.02 * mm});
            skCircle(sketch, "E5.14.14.0", {"center": v(-74.68, 59.44) * mm, "radius": 1.02 * mm});
            skCircle(sketch, "E5.14.15.0", {"center": v(-74.68, 63.25) * mm, "radius": 1.02 * mm});
            skCircle(sketch, "E5.14.16.0", {"center": v(-74.68, 67.06) * mm, "radius": 1.02 * mm});
            skCircle(sketch, "E5.14.17.0", {"center": v(-74.68, 70.87) * mm, "radius": 1.02 * mm});
            skCircle(sketch, "E5.14.18.0", {"center": v(-74.68, 74.68) * mm, "radius": 1.02 * mm});
            skCircle(sketch, "E5.14.19.0", {"center": v(-74.68, 78.49) * mm, "radius": 1.02 * mm});
            skCircle(sketch, "E5.14.20.0", {"center": v(-74.68, 82.3) * mm, "radius": 1.02 * mm});
            skCircle(sketch, "E5.14.21.0", {"center": v(-74.68, 86.1) * mm, "radius": 1.02 * mm});
            skCircle(sketch, "E5.14.22.0", {"center": v(-74.68, 89.92) * mm, "radius": 1.02 * mm});
            skCircle(sketch, "E5.14.23.0", {"center": v(-74.68, 93.73) * mm, "radius": 1.02 * mm});
            skCircle(sketch, "E5.14.24.0", {"center": v(-74.68, 97.54) * mm, "radius": 1.02 * mm});
            skCircle(sketch, "E5.14.25.0", {"center": v(-74.68, 101.35) * mm, "radius": 1.02 * mm});
            skCircle(sketch, "E5.14.26.0", {"center": v(-74.68, 105.16) * mm, "radius": 1.02 * mm});
            skCircle(sketch, "E5.14.27.0", {"center": v(-74.68, 108.97) * mm, "radius": 1.02 * mm});
            skCircle(sketch, "E5.14.28.0", {"center": v(-74.68, 112.78) * mm, "radius": 1.02 * mm});
            skCircle(sketch, "E5.14.29.0", {"center": v(-74.68, 116.59) * mm, "radius": 1.02 * mm});
            skCircle(sketch, "E5.14.30.0", {"center": v(-74.68, 120.4) * mm, "radius": 1.02 * mm});
            skCircle(sketch, "E5.15.0.0", {"center": v(-71.37, 6.1) * mm, "radius": 1.02 * mm});
            skCircle(sketch, "E5.15.1.0", {"center": v(-71.37, 9.9) * mm, "radius": 1.02 * mm});
            skCircle(sketch, "E5.15.2.0", {"center": v(-71.37, 13.72) * mm, "radius": 1.02 * mm});
            skCircle(sketch, "E5.15.3.0", {"center": v(-71.37, 17.53) * mm, "radius": 1.02 * mm});
            skCircle(sketch, "E5.15.4.0", {"center": v(-71.37, 21.34) * mm, "radius": 1.02 * mm});
            skCircle(sketch, "E5.15.5.0", {"center": v(-71.37, 25.15) * mm, "radius": 1.02 * mm});
            skCircle(sketch, "E5.15.6.0", {"center": v(-71.37, 28.96) * mm, "radius": 1.02 * mm});
            skCircle(sketch, "E5.15.7.0", {"center": v(-71.37, 32.77) * mm, "radius": 1.02 * mm});
            skCircle(sketch, "E5.15.8.0", {"center": v(-71.37, 36.58) * mm, "radius": 1.02 * mm});
            skCircle(sketch, "E5.15.9.0", {"center": v(-71.37, 40.39) * mm, "radius": 1.02 * mm});
            skCircle(sketch, "E5.15.10.0", {"center": v(-71.37, 44.2) * mm, "radius": 1.02 * mm});
            skCircle(sketch, "E5.15.11.0", {"center": v(-71.37, 48) * mm, "radius": 1.02 * mm});
            skCircle(sketch, "E5.15.12.0", {"center": v(-71.37, 51.82) * mm, "radius": 1.02 * mm});
            skCircle(sketch, "E5.15.13.0", {"center": v(-71.37, 55.63) * mm, "radius": 1.02 * mm});
            skCircle(sketch, "E5.15.14.0", {"center": v(-71.37, 59.44) * mm, "radius": 1.02 * mm});
            skCircle(sketch, "E5.15.15.0", {"center": v(-71.37, 63.25) * mm, "radius": 1.02 * mm});
            skCircle(sketch, "E5.15.16.0", {"center": v(-71.37, 67.06) * mm, "radius": 1.02 * mm});
            skCircle(sketch, "E5.15.17.0", {"center": v(-71.37, 70.87) * mm, "radius": 1.02 * mm});
            skCircle(sketch, "E5.15.18.0", {"center": v(-71.37, 74.68) * mm, "radius": 1.02 * mm});
            skCircle(sketch, "E5.15.19.0", {"center": v(-71.37, 78.49) * mm, "radius": 1.02 * mm});
            skCircle(sketch, "E5.15.20.0", {"center": v(-71.37, 82.3) * mm, "radius": 1.02 * mm});
            skCircle(sketch, "E5.15.21.0", {"center": v(-71.37, 86.1) * mm, "radius": 1.02 * mm});
            skCircle(sketch, "E5.15.22.0", {"center": v(-71.37, 89.92) * mm, "radius": 1.02 * mm});
            skCircle(sketch, "E5.15.23.0", {"center": v(-71.37, 93.73) * mm, "radius": 1.02 * mm});
            skCircle(sketch, "E5.15.24.0", {"center": v(-71.37, 97.54) * mm, "radius": 1.02 * mm});
            skCircle(sketch, "E5.15.25.0", {"center": v(-71.37, 101.35) * mm, "radius": 1.02 * mm});
            skCircle(sketch, "E5.15.26.0", {"center": v(-71.37, 105.16) * mm, "radius": 1.02 * mm});
            skCircle(sketch, "E5.15.27.0", {"center": v(-71.37, 108.97) * mm, "radius": 1.02 * mm});
            skCircle(sketch, "E5.15.28.0", {"center": v(-71.37, 112.78) * mm, "radius": 1.02 * mm});
            skCircle(sketch, "E5.15.29.0", {"center": v(-71.37, 116.59) * mm, "radius": 1.02 * mm});
            skCircle(sketch, "E5.15.30.0", {"center": v(-71.37, 120.4) * mm, "radius": 1.02 * mm});
            skCircle(sketch, "E5.16.0.0", {"center": v(-68.07, 6.1) * mm, "radius": 1.02 * mm});
            skCircle(sketch, "E5.16.1.0", {"center": v(-68.07, 9.9) * mm, "radius": 1.02 * mm});
            skCircle(sketch, "E5.16.2.0", {"center": v(-68.07, 13.72) * mm, "radius": 1.02 * mm});
            skCircle(sketch, "E5.16.3.0", {"center": v(-68.07, 17.53) * mm, "radius": 1.02 * mm});
            skCircle(sketch, "E5.16.4.0", {"center": v(-68.07, 21.34) * mm, "radius": 1.02 * mm});
            skCircle(sketch, "E5.16.5.0", {"center": v(-68.07, 25.15) * mm, "radius": 1.02 * mm});
            skCircle(sketch, "E5.16.6.0", {"center": v(-68.07, 28.96) * mm, "radius": 1.02 * mm});
            skCircle(sketch, "E5.16.7.0", {"center": v(-68.07, 32.77) * mm, "radius": 1.02 * mm});
            skCircle(sketch, "E5.16.8.0", {"center": v(-68.07, 36.58) * mm, "radius": 1.02 * mm});
            skCircle(sketch, "E5.16.9.0", {"center": v(-68.07, 40.39) * mm, "radius": 1.02 * mm});
            skCircle(sketch, "E5.16.10.0", {"center": v(-68.07, 44.2) * mm, "radius": 1.02 * mm});
            skCircle(sketch, "E5.16.11.0", {"center": v(-68.07, 48) * mm, "radius": 1.02 * mm});
            skCircle(sketch, "E5.16.12.0", {"center": v(-68.07, 51.82) * mm, "radius": 1.02 * mm});
            skCircle(sketch, "E5.16.13.0", {"center": v(-68.07, 55.63) * mm, "radius": 1.02 * mm});
            skCircle(sketch, "E5.16.14.0", {"center": v(-68.07, 59.44) * mm, "radius": 1.02 * mm});
            skCircle(sketch, "E5.16.15.0", {"center": v(-68.07, 63.25) * mm, "radius": 1.02 * mm});
            skCircle(sketch, "E5.16.16.0", {"center": v(-68.07, 67.06) * mm, "radius": 1.02 * mm});
            skCircle(sketch, "E5.16.17.0", {"center": v(-68.07, 70.87) * mm, "radius": 1.02 * mm});
            skCircle(sketch, "E5.16.18.0", {"center": v(-68.07, 74.68) * mm, "radius": 1.02 * mm});
            skCircle(sketch, "E5.16.19.0", {"center": v(-68.07, 78.49) * mm, "radius": 1.02 * mm});
            skCircle(sketch, "E5.16.20.0", {"center": v(-68.07, 82.3) * mm, "radius": 1.02 * mm});
            skCircle(sketch, "E5.16.21.0", {"center": v(-68.07, 86.1) * mm, "radius": 1.02 * mm});
            skCircle(sketch, "E5.16.22.0", {"center": v(-68.07, 89.92) * mm, "radius": 1.02 * mm});
            skCircle(sketch, "E5.16.23.0", {"center": v(-68.07, 93.73) * mm, "radius": 1.02 * mm});
            skCircle(sketch, "E5.16.24.0", {"center": v(-68.07, 97.54) * mm, "radius": 1.02 * mm});
            skCircle(sketch, "E5.16.25.0", {"center": v(-68.07, 101.35) * mm, "radius": 1.02 * mm});
            skCircle(sketch, "E5.16.26.0", {"center": v(-68.07, 105.16) * mm, "radius": 1.02 * mm});
            skCircle(sketch, "E5.16.27.0", {"center": v(-68.07, 108.97) * mm, "radius": 1.02 * mm});
            skCircle(sketch, "E5.16.28.0", {"center": v(-68.07, 112.78) * mm, "radius": 1.02 * mm});
            skCircle(sketch, "E5.16.29.0", {"center": v(-68.07, 116.59) * mm, "radius": 1.02 * mm});
            skCircle(sketch, "E5.16.30.0", {"center": v(-68.07, 120.4) * mm, "radius": 1.02 * mm});
            skCircle(sketch, "E5.17.0.0", {"center": v(-64.77, 6.1) * mm, "radius": 1.02 * mm});
            skCircle(sketch, "E5.17.1.0", {"center": v(-64.77, 9.9) * mm, "radius": 1.02 * mm});
            skCircle(sketch, "E5.17.2.0", {"center": v(-64.77, 13.72) * mm, "radius": 1.02 * mm});
            skCircle(sketch, "E5.17.3.0", {"center": v(-64.77, 17.53) * mm, "radius": 1.02 * mm});
            skCircle(sketch, "E5.17.4.0", {"center": v(-64.77, 21.34) * mm, "radius": 1.02 * mm});
            skCircle(sketch, "E5.17.5.0", {"center": v(-64.77, 25.15) * mm, "radius": 1.02 * mm});
            skCircle(sketch, "E5.17.6.0", {"center": v(-64.77, 28.96) * mm, "radius": 1.02 * mm});
            skCircle(sketch, "E5.17.7.0", {"center": v(-64.77, 32.77) * mm, "radius": 1.02 * mm});
            skCircle(sketch, "E5.17.8.0", {"center": v(-64.77, 36.58) * mm, "radius": 1.02 * mm});
            skCircle(sketch, "E5.17.9.0", {"center": v(-64.77, 40.39) * mm, "radius": 1.02 * mm});
            skCircle(sketch, "E5.17.10.0", {"center": v(-64.77, 44.2) * mm, "radius": 1.02 * mm});
            skCircle(sketch, "E5.17.11.0", {"center": v(-64.77, 48) * mm, "radius": 1.02 * mm});
            skCircle(sketch, "E5.17.12.0", {"center": v(-64.77, 51.82) * mm, "radius": 1.02 * mm});
            skCircle(sketch, "E5.17.13.0", {"center": v(-64.77, 55.63) * mm, "radius": 1.02 * mm});
            skCircle(sketch, "E5.17.14.0", {"center": v(-64.77, 59.44) * mm, "radius": 1.02 * mm});
            skCircle(sketch, "E5.17.15.0", {"center": v(-64.77, 63.25) * mm, "radius": 1.02 * mm});
            skCircle(sketch, "E5.17.16.0", {"center": v(-64.77, 67.06) * mm, "radius": 1.02 * mm});
            skCircle(sketch, "E5.17.17.0", {"center": v(-64.77, 70.87) * mm, "radius": 1.02 * mm});
            skCircle(sketch, "E5.17.18.0", {"center": v(-64.77, 74.68) * mm, "radius": 1.02 * mm});
            skCircle(sketch, "E5.17.19.0", {"center": v(-64.77, 78.49) * mm, "radius": 1.02 * mm});
            skCircle(sketch, "E5.17.20.0", {"center": v(-64.77, 82.3) * mm, "radius": 1.02 * mm});
            skCircle(sketch, "E5.17.21.0", {"center": v(-64.77, 86.1) * mm, "radius": 1.02 * mm});
            skCircle(sketch, "E5.17.22.0", {"center": v(-64.77, 89.92) * mm, "radius": 1.02 * mm});
            skCircle(sketch, "E5.17.23.0", {"center": v(-64.77, 93.73) * mm, "radius": 1.02 * mm});
            skCircle(sketch, "E5.17.24.0", {"center": v(-64.77, 97.54) * mm, "radius": 1.02 * mm});
            skCircle(sketch, "E5.17.25.0", {"center": v(-64.77, 101.35) * mm, "radius": 1.02 * mm});
            skCircle(sketch, "E5.17.26.0", {"center": v(-64.77, 105.16) * mm, "radius": 1.02 * mm});
            skCircle(sketch, "E5.17.27.0", {"center": v(-64.77, 108.97) * mm, "radius": 1.02 * mm});
            skCircle(sketch, "E5.17.28.0", {"center": v(-64.77, 112.78) * mm, "radius": 1.02 * mm});
            skCircle(sketch, "E5.17.29.0", {"center": v(-64.77, 116.59) * mm, "radius": 1.02 * mm});
            skCircle(sketch, "E5.17.30.0", {"center": v(-64.77, 120.4) * mm, "radius": 1.02 * mm});
            skCircle(sketch, "E5.18.0.0", {"center": v(-61.47, 6.1) * mm, "radius": 1.02 * mm});
            skCircle(sketch, "E5.18.1.0", {"center": v(-61.47, 9.9) * mm, "radius": 1.02 * mm});
            skCircle(sketch, "E5.18.2.0", {"center": v(-61.47, 13.72) * mm, "radius": 1.02 * mm});
            skCircle(sketch, "E5.18.3.0", {"center": v(-61.47, 17.53) * mm, "radius": 1.02 * mm});
            skCircle(sketch, "E5.18.4.0", {"center": v(-61.47, 21.34) * mm, "radius": 1.02 * mm});
            skCircle(sketch, "E5.18.5.0", {"center": v(-61.47, 25.15) * mm, "radius": 1.02 * mm});
            skCircle(sketch, "E5.18.6.0", {"center": v(-61.47, 28.96) * mm, "radius": 1.02 * mm});
            skCircle(sketch, "E5.18.7.0", {"center": v(-61.47, 32.77) * mm, "radius": 1.02 * mm});
            skCircle(sketch, "E5.18.8.0", {"center": v(-61.47, 36.58) * mm, "radius": 1.02 * mm});
            skCircle(sketch, "E5.18.9.0", {"center": v(-61.47, 40.39) * mm, "radius": 1.02 * mm});
            skCircle(sketch, "E5.18.10.0", {"center": v(-61.47, 44.2) * mm, "radius": 1.02 * mm});
            skCircle(sketch, "E5.18.11.0", {"center": v(-61.47, 48) * mm, "radius": 1.02 * mm});
            skCircle(sketch, "E5.18.12.0", {"center": v(-61.47, 51.82) * mm, "radius": 1.02 * mm});
            skCircle(sketch, "E5.18.13.0", {"center": v(-61.47, 55.63) * mm, "radius": 1.02 * mm});
            skCircle(sketch, "E5.18.14.0", {"center": v(-61.47, 59.44) * mm, "radius": 1.02 * mm});
            skCircle(sketch, "E5.18.15.0", {"center": v(-61.47, 63.25) * mm, "radius": 1.02 * mm});
            skCircle(sketch, "E5.18.16.0", {"center": v(-61.47, 67.06) * mm, "radius": 1.02 * mm});
            skCircle(sketch, "E5.18.17.0", {"center": v(-61.47, 70.87) * mm, "radius": 1.02 * mm});
            skCircle(sketch, "E5.18.18.0", {"center": v(-61.47, 74.68) * mm, "radius": 1.02 * mm});
            skCircle(sketch, "E5.18.19.0", {"center": v(-61.47, 78.49) * mm, "radius": 1.02 * mm});
            skCircle(sketch, "E5.18.20.0", {"center": v(-61.47, 82.3) * mm, "radius": 1.02 * mm});
            skCircle(sketch, "E5.18.21.0", {"center": v(-61.47, 86.1) * mm, "radius": 1.02 * mm});
            skCircle(sketch, "E5.18.22.0", {"center": v(-61.47, 89.92) * mm, "radius": 1.02 * mm});
            skCircle(sketch, "E5.18.23.0", {"center": v(-61.47, 93.73) * mm, "radius": 1.02 * mm});
            skCircle(sketch, "E5.18.24.0", {"center": v(-61.47, 97.54) * mm, "radius": 1.02 * mm});
            skCircle(sketch, "E5.18.25.0", {"center": v(-61.47, 101.35) * mm, "radius": 1.02 * mm});
            skCircle(sketch, "E5.18.26.0", {"center": v(-61.47, 105.16) * mm, "radius": 1.02 * mm});
            skCircle(sketch, "E5.18.27.0", {"center": v(-61.47, 108.97) * mm, "radius": 1.02 * mm});
            skCircle(sketch, "E5.18.28.0", {"center": v(-61.47, 112.78) * mm, "radius": 1.02 * mm});
            skCircle(sketch, "E5.18.29.0", {"center": v(-61.47, 116.59) * mm, "radius": 1.02 * mm});
            skCircle(sketch, "E5.18.30.0", {"center": v(-61.47, 120.4) * mm, "radius": 1.02 * mm});
            skCircle(sketch, "E5.19.0.0", {"center": v(-58.17, 6.1) * mm, "radius": 1.02 * mm});
            skCircle(sketch, "E5.19.1.0", {"center": v(-58.17, 9.9) * mm, "radius": 1.02 * mm});
            skCircle(sketch, "E5.19.2.0", {"center": v(-58.17, 13.72) * mm, "radius": 1.02 * mm});
            skCircle(sketch, "E5.19.3.0", {"center": v(-58.17, 17.53) * mm, "radius": 1.02 * mm});
            skCircle(sketch, "E5.19.4.0", {"center": v(-58.17, 21.34) * mm, "radius": 1.02 * mm});
            skCircle(sketch, "E5.19.5.0", {"center": v(-58.17, 25.15) * mm, "radius": 1.02 * mm});
            skCircle(sketch, "E5.19.6.0", {"center": v(-58.17, 28.96) * mm, "radius": 1.02 * mm});
            skCircle(sketch, "E5.19.7.0", {"center": v(-58.17, 32.77) * mm, "radius": 1.02 * mm});
            skCircle(sketch, "E5.19.8.0", {"center": v(-58.17, 36.58) * mm, "radius": 1.02 * mm});
            skCircle(sketch, "E5.19.9.0", {"center": v(-58.17, 40.39) * mm, "radius": 1.02 * mm});
            skCircle(sketch, "E5.19.10.0", {"center": v(-58.17, 44.2) * mm, "radius": 1.02 * mm});
            skCircle(sketch, "E5.19.11.0", {"center": v(-58.17, 48) * mm, "radius": 1.02 * mm});
            skCircle(sketch, "E5.19.12.0", {"center": v(-58.17, 51.82) * mm, "radius": 1.02 * mm});
            skCircle(sketch, "E5.19.13.0", {"center": v(-58.17, 55.63) * mm, "radius": 1.02 * mm});
            skCircle(sketch, "E5.19.14.0", {"center": v(-58.17, 59.44) * mm, "radius": 1.02 * mm});
            skCircle(sketch, "E5.19.15.0", {"center": v(-58.17, 63.25) * mm, "radius": 1.02 * mm});
            skCircle(sketch, "E5.19.16.0", {"center": v(-58.17, 67.06) * mm, "radius": 1.02 * mm});
            skCircle(sketch, "E5.19.17.0", {"center": v(-58.17, 70.87) * mm, "radius": 1.02 * mm});
            skCircle(sketch, "E5.19.18.0", {"center": v(-58.17, 74.68) * mm, "radius": 1.02 * mm});
            skCircle(sketch, "E5.19.19.0", {"center": v(-58.17, 78.49) * mm, "radius": 1.02 * mm});
            skCircle(sketch, "E5.19.20.0", {"center": v(-58.17, 82.3) * mm, "radius": 1.02 * mm});
            skCircle(sketch, "E5.19.21.0", {"center": v(-58.17, 86.1) * mm, "radius": 1.02 * mm});
            skCircle(sketch, "E5.19.22.0", {"center": v(-58.17, 89.92) * mm, "radius": 1.02 * mm});
            skCircle(sketch, "E5.19.23.0", {"center": v(-58.17, 93.73) * mm, "radius": 1.02 * mm});
            skCircle(sketch, "E5.19.24.0", {"center": v(-58.17, 97.54) * mm, "radius": 1.02 * mm});
            skCircle(sketch, "E5.19.25.0", {"center": v(-58.17, 101.35) * mm, "radius": 1.02 * mm});
            skCircle(sketch, "E5.19.26.0", {"center": v(-58.17, 105.16) * mm, "radius": 1.02 * mm});
            skCircle(sketch, "E5.19.27.0", {"center": v(-58.17, 108.97) * mm, "radius": 1.02 * mm});
            skCircle(sketch, "E5.19.28.0", {"center": v(-58.17, 112.78) * mm, "radius": 1.02 * mm});
            skCircle(sketch, "E5.19.29.0", {"center": v(-58.17, 116.59) * mm, "radius": 1.02 * mm});
            skCircle(sketch, "E5.19.30.0", {"center": v(-58.17, 120.4) * mm, "radius": 1.02 * mm});
            skCircle(sketch, "E5.20.0.0", {"center": v(-54.86, 6.1) * mm, "radius": 1.02 * mm});
            skCircle(sketch, "E5.20.1.0", {"center": v(-54.86, 9.9) * mm, "radius": 1.02 * mm});
            skCircle(sketch, "E5.20.2.0", {"center": v(-54.86, 13.72) * mm, "radius": 1.02 * mm});
            skCircle(sketch, "E5.20.3.0", {"center": v(-54.86, 17.53) * mm, "radius": 1.02 * mm});
            skCircle(sketch, "E5.20.4.0", {"center": v(-54.86, 21.34) * mm, "radius": 1.02 * mm});
            skCircle(sketch, "E5.20.5.0", {"center": v(-54.86, 25.15) * mm, "radius": 1.02 * mm});
            skCircle(sketch, "E5.20.6.0", {"center": v(-54.86, 28.96) * mm, "radius": 1.02 * mm});
            skCircle(sketch, "E5.20.7.0", {"center": v(-54.86, 32.77) * mm, "radius": 1.02 * mm});
            skCircle(sketch, "E5.20.8.0", {"center": v(-54.86, 36.58) * mm, "radius": 1.02 * mm});
            skCircle(sketch, "E5.20.9.0", {"center": v(-54.86, 40.39) * mm, "radius": 1.02 * mm});
            skCircle(sketch, "E5.20.10.0", {"center": v(-54.86, 44.2) * mm, "radius": 1.02 * mm});
            skCircle(sketch, "E5.20.11.0", {"center": v(-54.86, 48) * mm, "radius": 1.02 * mm});
            skCircle(sketch, "E5.20.12.0", {"center": v(-54.86, 51.82) * mm, "radius": 1.02 * mm});
            skCircle(sketch, "E5.20.13.0", {"center": v(-54.86, 55.63) * mm, "radius": 1.02 * mm});
            skCircle(sketch, "E5.20.14.0", {"center": v(-54.86, 59.44) * mm, "radius": 1.02 * mm});
            skCircle(sketch, "E5.20.15.0", {"center": v(-54.86, 63.25) * mm, "radius": 1.02 * mm});
            skCircle(sketch, "E5.20.16.0", {"center": v(-54.86, 67.06) * mm, "radius": 1.02 * mm});
            skCircle(sketch, "E5.20.17.0", {"center": v(-54.86, 70.87) * mm, "radius": 1.02 * mm});
            skCircle(sketch, "E5.20.18.0", {"center": v(-54.86, 74.68) * mm, "radius": 1.02 * mm});
            skCircle(sketch, "E5.20.19.0", {"center": v(-54.86, 78.49) * mm, "radius": 1.02 * mm});
            skCircle(sketch, "E5.20.20.0", {"center": v(-54.86, 82.3) * mm, "radius": 1.02 * mm});
            skCircle(sketch, "E5.20.21.0", {"center": v(-54.86, 86.1) * mm, "radius": 1.02 * mm});
            skCircle(sketch, "E5.20.22.0", {"center": v(-54.86, 89.92) * mm, "radius": 1.02 * mm});
            skCircle(sketch, "E5.20.23.0", {"center": v(-54.86, 93.73) * mm, "radius": 1.02 * mm});
            skCircle(sketch, "E5.20.24.0", {"center": v(-54.86, 97.54) * mm, "radius": 1.02 * mm});
            skCircle(sketch, "E5.20.25.0", {"center": v(-54.86, 101.35) * mm, "radius": 1.02 * mm});
            skCircle(sketch, "E5.20.26.0", {"center": v(-54.86, 105.16) * mm, "radius": 1.02 * mm});
            skCircle(sketch, "E5.20.27.0", {"center": v(-54.86, 108.97) * mm, "radius": 1.02 * mm});
            skCircle(sketch, "E5.20.28.0", {"center": v(-54.86, 112.78) * mm, "radius": 1.02 * mm});
            skCircle(sketch, "E5.20.29.0", {"center": v(-54.86, 116.59) * mm, "radius": 1.02 * mm});
            skCircle(sketch, "E5.20.30.0", {"center": v(-54.86, 120.4) * mm, "radius": 1.02 * mm});
            skCircle(sketch, "E5.21.0.0", {"center": v(-51.56, 6.1) * mm, "radius": 1.02 * mm});
            skCircle(sketch, "E5.21.1.0", {"center": v(-51.56, 9.9) * mm, "radius": 1.02 * mm});
            skCircle(sketch, "E5.21.2.0", {"center": v(-51.56, 13.72) * mm, "radius": 1.02 * mm});
            skCircle(sketch, "E5.21.3.0", {"center": v(-51.56, 17.53) * mm, "radius": 1.02 * mm});
            skCircle(sketch, "E5.21.4.0", {"center": v(-51.56, 21.34) * mm, "radius": 1.02 * mm});
            skCircle(sketch, "E5.21.5.0", {"center": v(-51.56, 25.15) * mm, "radius": 1.02 * mm});
            skCircle(sketch, "E5.21.6.0", {"center": v(-51.56, 28.96) * mm, "radius": 1.02 * mm});
            skCircle(sketch, "E5.21.7.0", {"center": v(-51.56, 32.77) * mm, "radius": 1.02 * mm});
            skCircle(sketch, "E5.21.8.0", {"center": v(-51.56, 36.58) * mm, "radius": 1.02 * mm});
            skCircle(sketch, "E5.21.9.0", {"center": v(-51.56, 40.39) * mm, "radius": 1.02 * mm});
            skCircle(sketch, "E5.21.10.0", {"center": v(-51.56, 44.2) * mm, "radius": 1.02 * mm});
            skCircle(sketch, "E5.21.11.0", {"center": v(-51.56, 48) * mm, "radius": 1.02 * mm});
            skCircle(sketch, "E5.21.12.0", {"center": v(-51.56, 51.82) * mm, "radius": 1.02 * mm});
            skCircle(sketch, "E5.21.13.0", {"center": v(-51.56, 55.63) * mm, "radius": 1.02 * mm});
            skCircle(sketch, "E5.21.14.0", {"center": v(-51.56, 59.44) * mm, "radius": 1.02 * mm});
            skCircle(sketch, "E5.21.15.0", {"center": v(-51.56, 63.25) * mm, "radius": 1.02 * mm});
            skCircle(sketch, "E5.21.16.0", {"center": v(-51.56, 67.06) * mm, "radius": 1.02 * mm});
            skCircle(sketch, "E5.21.17.0", {"center": v(-51.56, 70.87) * mm, "radius": 1.02 * mm});
            skCircle(sketch, "E5.21.18.0", {"center": v(-51.56, 74.68) * mm, "radius": 1.02 * mm});
            skCircle(sketch, "E5.21.19.0", {"center": v(-51.56, 78.49) * mm, "radius": 1.02 * mm});
            skCircle(sketch, "E5.21.20.0", {"center": v(-51.56, 82.3) * mm, "radius": 1.02 * mm});
            skCircle(sketch, "E5.21.21.0", {"center": v(-51.56, 86.1) * mm, "radius": 1.02 * mm});
            skCircle(sketch, "E5.21.22.0", {"center": v(-51.56, 89.92) * mm, "radius": 1.02 * mm});
            skCircle(sketch, "E5.21.23.0", {"center": v(-51.56, 93.73) * mm, "radius": 1.02 * mm});
            skCircle(sketch, "E5.21.24.0", {"center": v(-51.56, 97.54) * mm, "radius": 1.02 * mm});
            skCircle(sketch, "E5.21.25.0", {"center": v(-51.56, 101.35) * mm, "radius": 1.02 * mm});
            skCircle(sketch, "E5.21.26.0", {"center": v(-51.56, 105.16) * mm, "radius": 1.02 * mm});
            skCircle(sketch, "E5.21.27.0", {"center": v(-51.56, 108.97) * mm, "radius": 1.02 * mm});
            skCircle(sketch, "E5.21.28.0", {"center": v(-51.56, 112.78) * mm, "radius": 1.02 * mm});
            skCircle(sketch, "E5.21.29.0", {"center": v(-51.56, 116.59) * mm, "radius": 1.02 * mm});
            skCircle(sketch, "E5.21.30.0", {"center": v(-51.56, 120.4) * mm, "radius": 1.02 * mm});
            skCircle(sketch, "E5.22.0.0", {"center": v(-48.26, 6.1) * mm, "radius": 1.02 * mm});
            skCircle(sketch, "E5.22.1.0", {"center": v(-48.26, 9.9) * mm, "radius": 1.02 * mm});
            skCircle(sketch, "E5.22.2.0", {"center": v(-48.26, 13.72) * mm, "radius": 1.02 * mm});
            skCircle(sketch, "E5.22.3.0", {"center": v(-48.26, 17.53) * mm, "radius": 1.02 * mm});
            skCircle(sketch, "E5.22.4.0", {"center": v(-48.26, 21.34) * mm, "radius": 1.02 * mm});
            skCircle(sketch, "E5.22.5.0", {"center": v(-48.26, 25.15) * mm, "radius": 1.02 * mm});
            skCircle(sketch, "E5.22.6.0", {"center": v(-48.26, 28.96) * mm, "radius": 1.02 * mm});
            skCircle(sketch, "E5.22.7.0", {"center": v(-48.26, 32.77) * mm, "radius": 1.02 * mm});
            skCircle(sketch, "E5.22.8.0", {"center": v(-48.26, 36.58) * mm, "radius": 1.02 * mm});
            skCircle(sketch, "E5.22.9.0", {"center": v(-48.26, 40.39) * mm, "radius": 1.02 * mm});
            skCircle(sketch, "E5.22.10.0", {"center": v(-48.26, 44.2) * mm, "radius": 1.02 * mm});
            skCircle(sketch, "E5.22.11.0", {"center": v(-48.26, 48) * mm, "radius": 1.02 * mm});
            skCircle(sketch, "E5.22.12.0", {"center": v(-48.26, 51.82) * mm, "radius": 1.02 * mm});
            skCircle(sketch, "E5.22.13.0", {"center": v(-48.26, 55.63) * mm, "radius": 1.02 * mm});
            skCircle(sketch, "E5.22.14.0", {"center": v(-48.26, 59.44) * mm, "radius": 1.02 * mm});
            skCircle(sketch, "E5.22.15.0", {"center": v(-48.26, 63.25) * mm, "radius": 1.02 * mm});
            skCircle(sketch, "E5.22.16.0", {"center": v(-48.26, 67.06) * mm, "radius": 1.02 * mm});
            skCircle(sketch, "E5.22.17.0", {"center": v(-48.26, 70.87) * mm, "radius": 1.02 * mm});
            skCircle(sketch, "E5.22.18.0", {"center": v(-48.26, 74.68) * mm, "radius": 1.02 * mm});
            skCircle(sketch, "E5.22.19.0", {"center": v(-48.26, 78.49) * mm, "radius": 1.02 * mm});
            skCircle(sketch, "E5.22.20.0", {"center": v(-48.26, 82.3) * mm, "radius": 1.02 * mm});
            skCircle(sketch, "E5.22.21.0", {"center": v(-48.26, 86.1) * mm, "radius": 1.02 * mm});
            skCircle(sketch, "E5.22.22.0", {"center": v(-48.26, 89.92) * mm, "radius": 1.02 * mm});
            skCircle(sketch, "E5.22.23.0", {"center": v(-48.26, 93.73) * mm, "radius": 1.02 * mm});
            skCircle(sketch, "E5.22.24.0", {"center": v(-48.26, 97.54) * mm, "radius": 1.02 * mm});
            skCircle(sketch, "E5.22.25.0", {"center": v(-48.26, 101.35) * mm, "radius": 1.02 * mm});
            skCircle(sketch, "E5.22.26.0", {"center": v(-48.26, 105.16) * mm, "radius": 1.02 * mm});
            skCircle(sketch, "E5.22.27.0", {"center": v(-48.26, 108.97) * mm, "radius": 1.02 * mm});
            skCircle(sketch, "E5.22.28.0", {"center": v(-48.26, 112.78) * mm, "radius": 1.02 * mm});
            skCircle(sketch, "E5.22.29.0", {"center": v(-48.26, 116.59) * mm, "radius": 1.02 * mm});
            skCircle(sketch, "E5.22.30.0", {"center": v(-48.26, 120.4) * mm, "radius": 1.02 * mm});
            skCircle(sketch, "E5.23.0.0", {"center": v(-44.96, 6.1) * mm, "radius": 1.02 * mm});
            skCircle(sketch, "E5.23.1.0", {"center": v(-44.96, 9.9) * mm, "radius": 1.02 * mm});
            skCircle(sketch, "E5.23.2.0", {"center": v(-44.96, 13.72) * mm, "radius": 1.02 * mm});
            skCircle(sketch, "E5.23.3.0", {"center": v(-44.96, 17.53) * mm, "radius": 1.02 * mm});
            skCircle(sketch, "E5.23.4.0", {"center": v(-44.96, 21.34) * mm, "radius": 1.02 * mm});
            skCircle(sketch, "E5.23.5.0", {"center": v(-44.96, 25.15) * mm, "radius": 1.02 * mm});
            skCircle(sketch, "E5.23.6.0", {"center": v(-44.96, 28.96) * mm, "radius": 1.02 * mm});
            skCircle(sketch, "E5.23.7.0", {"center": v(-44.96, 32.77) * mm, "radius": 1.02 * mm});
            skCircle(sketch, "E5.23.8.0", {"center": v(-44.96, 36.58) * mm, "radius": 1.02 * mm});
            skCircle(sketch, "E5.23.9.0", {"center": v(-44.96, 40.39) * mm, "radius": 1.02 * mm});
            skCircle(sketch, "E5.23.10.0", {"center": v(-44.96, 44.2) * mm, "radius": 1.02 * mm});
            skCircle(sketch, "E5.23.11.0", {"center": v(-44.96, 48) * mm, "radius": 1.02 * mm});
            skCircle(sketch, "E5.23.12.0", {"center": v(-44.96, 51.82) * mm, "radius": 1.02 * mm});
            skCircle(sketch, "E5.23.13.0", {"center": v(-44.96, 55.63) * mm, "radius": 1.02 * mm});
            skCircle(sketch, "E5.23.14.0", {"center": v(-44.96, 59.44) * mm, "radius": 1.02 * mm});
            skCircle(sketch, "E5.23.15.0", {"center": v(-44.96, 63.25) * mm, "radius": 1.02 * mm});
            skCircle(sketch, "E5.23.16.0", {"center": v(-44.96, 67.06) * mm, "radius": 1.02 * mm});
            skCircle(sketch, "E5.23.17.0", {"center": v(-44.96, 70.87) * mm, "radius": 1.02 * mm});
            skCircle(sketch, "E5.23.18.0", {"center": v(-44.96, 74.68) * mm, "radius": 1.02 * mm});
            skCircle(sketch, "E5.23.19.0", {"center": v(-44.96, 78.49) * mm, "radius": 1.02 * mm});
            skCircle(sketch, "E5.23.20.0", {"center": v(-44.96, 82.3) * mm, "radius": 1.02 * mm});
            skCircle(sketch, "E5.23.21.0", {"center": v(-44.96, 86.1) * mm, "radius": 1.02 * mm});
            skCircle(sketch, "E5.23.22.0", {"center": v(-44.96, 89.92) * mm, "radius": 1.02 * mm});
            skCircle(sketch, "E5.23.23.0", {"center": v(-44.96, 93.73) * mm, "radius": 1.02 * mm});
            skCircle(sketch, "E5.23.24.0", {"center": v(-44.96, 97.54) * mm, "radius": 1.02 * mm});
            skCircle(sketch, "E5.23.25.0", {"center": v(-44.96, 101.35) * mm, "radius": 1.02 * mm});
            skCircle(sketch, "E5.23.26.0", {"center": v(-44.96, 105.16) * mm, "radius": 1.02 * mm});
            skCircle(sketch, "E5.23.27.0", {"center": v(-44.96, 108.97) * mm, "radius": 1.02 * mm});
            skCircle(sketch, "E5.23.28.0", {"center": v(-44.96, 112.78) * mm, "radius": 1.02 * mm});
            skCircle(sketch, "E5.23.29.0", {"center": v(-44.96, 116.59) * mm, "radius": 1.02 * mm});
            skCircle(sketch, "E5.23.30.0", {"center": v(-44.96, 120.4) * mm, "radius": 1.02 * mm});
            skCircle(sketch, "E5.24.0.0", {"center": v(-41.66, 6.1) * mm, "radius": 1.02 * mm});
            skCircle(sketch, "E5.24.1.0", {"center": v(-41.66, 9.9) * mm, "radius": 1.02 * mm});
            skCircle(sketch, "E5.24.2.0", {"center": v(-41.66, 13.72) * mm, "radius": 1.02 * mm});
            skCircle(sketch, "E5.24.3.0", {"center": v(-41.66, 17.53) * mm, "radius": 1.02 * mm});
            skCircle(sketch, "E5.24.4.0", {"center": v(-41.66, 21.34) * mm, "radius": 1.02 * mm});
            skCircle(sketch, "E5.24.5.0", {"center": v(-41.66, 25.15) * mm, "radius": 1.02 * mm});
            skCircle(sketch, "E5.24.6.0", {"center": v(-41.66, 28.96) * mm, "radius": 1.02 * mm});
            skCircle(sketch, "E5.24.7.0", {"center": v(-41.66, 32.77) * mm, "radius": 1.02 * mm});
            skCircle(sketch, "E5.24.8.0", {"center": v(-41.66, 36.58) * mm, "radius": 1.02 * mm});
            skCircle(sketch, "E5.24.9.0", {"center": v(-41.66, 40.39) * mm, "radius": 1.02 * mm});
            skCircle(sketch, "E5.24.10.0", {"center": v(-41.66, 44.2) * mm, "radius": 1.02 * mm});
            skCircle(sketch, "E5.24.11.0", {"center": v(-41.66, 48) * mm, "radius": 1.02 * mm});
            skCircle(sketch, "E5.24.12.0", {"center": v(-41.66, 51.82) * mm, "radius": 1.02 * mm});
            skCircle(sketch, "E5.24.13.0", {"center": v(-41.66, 55.63) * mm, "radius": 1.02 * mm});
            skCircle(sketch, "E5.24.14.0", {"center": v(-41.66, 59.44) * mm, "radius": 1.02 * mm});
            skCircle(sketch, "E5.24.15.0", {"center": v(-41.66, 63.25) * mm, "radius": 1.02 * mm});
            skCircle(sketch, "E5.24.16.0", {"center": v(-41.66, 67.06) * mm, "radius": 1.02 * mm});
            skCircle(sketch, "E5.24.17.0", {"center": v(-41.66, 70.87) * mm, "radius": 1.02 * mm});
            skCircle(sketch, "E5.24.18.0", {"center": v(-41.66, 74.68) * mm, "radius": 1.02 * mm});
            skCircle(sketch, "E5.24.19.0", {"center": v(-41.66, 78.49) * mm, "radius": 1.02 * mm});
            skCircle(sketch, "E5.24.20.0", {"center": v(-41.66, 82.3) * mm, "radius": 1.02 * mm});
            skCircle(sketch, "E5.24.21.0", {"center": v(-41.66, 86.1) * mm, "radius": 1.02 * mm});
            skCircle(sketch, "E5.24.22.0", {"center": v(-41.66, 89.92) * mm, "radius": 1.02 * mm});
            skCircle(sketch, "E5.24.23.0", {"center": v(-41.66, 93.73) * mm, "radius": 1.02 * mm});
            skCircle(sketch, "E5.24.24.0", {"center": v(-41.66, 97.54) * mm, "radius": 1.02 * mm});
            skCircle(sketch, "E5.24.25.0", {"center": v(-41.66, 101.35) * mm, "radius": 1.02 * mm});
            skCircle(sketch, "E5.24.26.0", {"center": v(-41.66, 105.16) * mm, "radius": 1.02 * mm});
            skCircle(sketch, "E5.24.27.0", {"center": v(-41.66, 108.97) * mm, "radius": 1.02 * mm});
            skCircle(sketch, "E5.24.28.0", {"center": v(-41.66, 112.78) * mm, "radius": 1.02 * mm});
            skCircle(sketch, "E5.24.29.0", {"center": v(-41.66, 116.59) * mm, "radius": 1.02 * mm});
            skCircle(sketch, "E5.24.30.0", {"center": v(-41.66, 120.4) * mm, "radius": 1.02 * mm});
            skCircle(sketch, "E5.25.0.0", {"center": v(-38.35, 6.1) * mm, "radius": 1.02 * mm});
            skCircle(sketch, "E5.25.1.0", {"center": v(-38.35, 9.9) * mm, "radius": 1.02 * mm});
            skCircle(sketch, "E5.25.2.0", {"center": v(-38.35, 13.72) * mm, "radius": 1.02 * mm});
            skCircle(sketch, "E5.25.3.0", {"center": v(-38.35, 17.53) * mm, "radius": 1.02 * mm});
            skCircle(sketch, "E5.25.4.0", {"center": v(-38.35, 21.34) * mm, "radius": 1.02 * mm});
            skCircle(sketch, "E5.25.5.0", {"center": v(-38.35, 25.15) * mm, "radius": 1.02 * mm});
            skCircle(sketch, "E5.25.6.0", {"center": v(-38.35, 28.96) * mm, "radius": 1.02 * mm});
            skCircle(sketch, "E5.25.7.0", {"center": v(-38.35, 32.77) * mm, "radius": 1.02 * mm});
            skCircle(sketch, "E5.25.8.0", {"center": v(-38.35, 36.58) * mm, "radius": 1.02 * mm});
            skCircle(sketch, "E5.25.9.0", {"center": v(-38.35, 40.39) * mm, "radius": 1.02 * mm});
            skCircle(sketch, "E5.25.10.0", {"center": v(-38.35, 44.2) * mm, "radius": 1.02 * mm});
            skCircle(sketch, "E5.25.11.0", {"center": v(-38.35, 48) * mm, "radius": 1.02 * mm});
            skCircle(sketch, "E5.25.12.0", {"center": v(-38.35, 51.82) * mm, "radius": 1.02 * mm});
            skCircle(sketch, "E5.25.13.0", {"center": v(-38.35, 55.63) * mm, "radius": 1.02 * mm});
            skCircle(sketch, "E5.25.14.0", {"center": v(-38.35, 59.44) * mm, "radius": 1.02 * mm});
            skCircle(sketch, "E5.25.15.0", {"center": v(-38.35, 63.25) * mm, "radius": 1.02 * mm});
            skCircle(sketch, "E5.25.16.0", {"center": v(-38.35, 67.06) * mm, "radius": 1.02 * mm});
            skCircle(sketch, "E5.25.17.0", {"center": v(-38.35, 70.87) * mm, "radius": 1.02 * mm});
            skCircle(sketch, "E5.25.18.0", {"center": v(-38.35, 74.68) * mm, "radius": 1.02 * mm});
            skCircle(sketch, "E5.25.19.0", {"center": v(-38.35, 78.49) * mm, "radius": 1.02 * mm});
            skCircle(sketch, "E5.25.20.0", {"center": v(-38.35, 82.3) * mm, "radius": 1.02 * mm});
            skCircle(sketch, "E5.25.21.0", {"center": v(-38.35, 86.1) * mm, "radius": 1.02 * mm});
            skCircle(sketch, "E5.25.22.0", {"center": v(-38.35, 89.92) * mm, "radius": 1.02 * mm});
            skCircle(sketch, "E5.25.23.0", {"center": v(-38.35, 93.73) * mm, "radius": 1.02 * mm});
            skCircle(sketch, "E5.25.24.0", {"center": v(-38.35, 97.54) * mm, "radius": 1.02 * mm});
            skCircle(sketch, "E5.25.25.0", {"center": v(-38.35, 101.35) * mm, "radius": 1.02 * mm});
            skCircle(sketch, "E5.25.26.0", {"center": v(-38.35, 105.16) * mm, "radius": 1.02 * mm});
            skCircle(sketch, "E5.25.27.0", {"center": v(-38.35, 108.97) * mm, "radius": 1.02 * mm});
            skCircle(sketch, "E5.25.28.0", {"center": v(-38.35, 112.78) * mm, "radius": 1.02 * mm});
            skCircle(sketch, "E5.25.29.0", {"center": v(-38.35, 116.59) * mm, "radius": 1.02 * mm});
            skCircle(sketch, "E5.25.30.0", {"center": v(-38.35, 120.4) * mm, "radius": 1.02 * mm});
            skCircle(sketch, "E5.26.0.0", {"center": v(-35.05, 6.1) * mm, "radius": 1.02 * mm});
            skCircle(sketch, "E5.26.1.0", {"center": v(-35.05, 9.9) * mm, "radius": 1.02 * mm});
            skCircle(sketch, "E5.26.2.0", {"center": v(-35.05, 13.72) * mm, "radius": 1.02 * mm});
            skCircle(sketch, "E5.26.3.0", {"center": v(-35.05, 17.53) * mm, "radius": 1.02 * mm});
            skCircle(sketch, "E5.26.4.0", {"center": v(-35.05, 21.34) * mm, "radius": 1.02 * mm});
            skCircle(sketch, "E5.26.5.0", {"center": v(-35.05, 25.15) * mm, "radius": 1.02 * mm});
            skCircle(sketch, "E5.26.6.0", {"center": v(-35.05, 28.96) * mm, "radius": 1.02 * mm});
            skCircle(sketch, "E5.26.7.0", {"center": v(-35.05, 32.77) * mm, "radius": 1.02 * mm});
            skCircle(sketch, "E5.26.8.0", {"center": v(-35.05, 36.58) * mm, "radius": 1.02 * mm});
            skCircle(sketch, "E5.26.9.0", {"center": v(-35.05, 40.39) * mm, "radius": 1.02 * mm});
            skCircle(sketch, "E5.26.10.0", {"center": v(-35.05, 44.2) * mm, "radius": 1.02 * mm});
            skCircle(sketch, "E5.26.11.0", {"center": v(-35.05, 48) * mm, "radius": 1.02 * mm});
            skCircle(sketch, "E5.26.12.0", {"center": v(-35.05, 51.82) * mm, "radius": 1.02 * mm});
            skCircle(sketch, "E5.26.13.0", {"center": v(-35.05, 55.63) * mm, "radius": 1.02 * mm});
            skCircle(sketch, "E5.26.14.0", {"center": v(-35.05, 59.44) * mm, "radius": 1.02 * mm});
            skCircle(sketch, "E5.26.15.0", {"center": v(-35.05, 63.25) * mm, "radius": 1.02 * mm});
            skCircle(sketch, "E5.26.16.0", {"center": v(-35.05, 67.06) * mm, "radius": 1.02 * mm});
            skCircle(sketch, "E5.26.17.0", {"center": v(-35.05, 70.87) * mm, "radius": 1.02 * mm});
            skCircle(sketch, "E5.26.18.0", {"center": v(-35.05, 74.68) * mm, "radius": 1.02 * mm});
            skCircle(sketch, "E5.26.19.0", {"center": v(-35.05, 78.49) * mm, "radius": 1.02 * mm});
            skCircle(sketch, "E5.26.20.0", {"center": v(-35.05, 82.3) * mm, "radius": 1.02 * mm});
            skCircle(sketch, "E5.26.21.0", {"center": v(-35.05, 86.1) * mm, "radius": 1.02 * mm});
            skCircle(sketch, "E5.26.22.0", {"center": v(-35.05, 89.92) * mm, "radius": 1.02 * mm});
            skCircle(sketch, "E5.26.23.0", {"center": v(-35.05, 93.73) * mm, "radius": 1.02 * mm});
            skCircle(sketch, "E5.26.24.0", {"center": v(-35.05, 97.54) * mm, "radius": 1.02 * mm});
            skCircle(sketch, "E5.26.25.0", {"center": v(-35.05, 101.35) * mm, "radius": 1.02 * mm});
            skCircle(sketch, "E5.26.26.0", {"center": v(-35.05, 105.16) * mm, "radius": 1.02 * mm});
            skCircle(sketch, "E5.26.27.0", {"center": v(-35.05, 108.97) * mm, "radius": 1.02 * mm});
            skCircle(sketch, "E5.26.28.0", {"center": v(-35.05, 112.78) * mm, "radius": 1.02 * mm});
            skCircle(sketch, "E5.26.29.0", {"center": v(-35.05, 116.59) * mm, "radius": 1.02 * mm});
            skCircle(sketch, "E5.26.30.0", {"center": v(-35.05, 120.4) * mm, "radius": 1.02 * mm});
            skCircle(sketch, "E5.27.0.0", {"center": v(-31.75, 6.1) * mm, "radius": 1.02 * mm});
            skCircle(sketch, "E5.27.1.0", {"center": v(-31.75, 9.9) * mm, "radius": 1.02 * mm});
            skCircle(sketch, "E5.27.2.0", {"center": v(-31.75, 13.72) * mm, "radius": 1.02 * mm});
            skCircle(sketch, "E5.27.3.0", {"center": v(-31.75, 17.53) * mm, "radius": 1.02 * mm});
            skCircle(sketch, "E5.27.4.0", {"center": v(-31.75, 21.34) * mm, "radius": 1.02 * mm});
            skCircle(sketch, "E5.27.5.0", {"center": v(-31.75, 25.15) * mm, "radius": 1.02 * mm});
            skCircle(sketch, "E5.27.6.0", {"center": v(-31.75, 28.96) * mm, "radius": 1.02 * mm});
            skCircle(sketch, "E5.27.7.0", {"center": v(-31.75, 32.77) * mm, "radius": 1.02 * mm});
            skCircle(sketch, "E5.27.8.0", {"center": v(-31.75, 36.58) * mm, "radius": 1.02 * mm});
            skCircle(sketch, "E5.27.9.0", {"center": v(-31.75, 40.39) * mm, "radius": 1.02 * mm});
            skCircle(sketch, "E5.27.10.0", {"center": v(-31.75, 44.2) * mm, "radius": 1.02 * mm});
            skCircle(sketch, "E5.27.11.0", {"center": v(-31.75, 48) * mm, "radius": 1.02 * mm});
            skCircle(sketch, "E5.27.12.0", {"center": v(-31.75, 51.82) * mm, "radius": 1.02 * mm});
            skCircle(sketch, "E5.27.13.0", {"center": v(-31.75, 55.63) * mm, "radius": 1.02 * mm});
            skCircle(sketch, "E5.27.14.0", {"center": v(-31.75, 59.44) * mm, "radius": 1.02 * mm});
            skCircle(sketch, "E5.27.15.0", {"center": v(-31.75, 63.25) * mm, "radius": 1.02 * mm});
            skCircle(sketch, "E5.27.16.0", {"center": v(-31.75, 67.06) * mm, "radius": 1.02 * mm});
            skCircle(sketch, "E5.27.17.0", {"center": v(-31.75, 70.87) * mm, "radius": 1.02 * mm});
            skCircle(sketch, "E5.27.18.0", {"center": v(-31.75, 74.68) * mm, "radius": 1.02 * mm});
            skCircle(sketch, "E5.27.19.0", {"center": v(-31.75, 78.49) * mm, "radius": 1.02 * mm});
            skCircle(sketch, "E5.27.20.0", {"center": v(-31.75, 82.3) * mm, "radius": 1.02 * mm});
            skCircle(sketch, "E5.27.21.0", {"center": v(-31.75, 86.1) * mm, "radius": 1.02 * mm});
            skCircle(sketch, "E5.27.22.0", {"center": v(-31.75, 89.92) * mm, "radius": 1.02 * mm});
            skCircle(sketch, "E5.27.23.0", {"center": v(-31.75, 93.73) * mm, "radius": 1.02 * mm});
            skCircle(sketch, "E5.27.24.0", {"center": v(-31.75, 97.54) * mm, "radius": 1.02 * mm});
            skCircle(sketch, "E5.27.25.0", {"center": v(-31.75, 101.35) * mm, "radius": 1.02 * mm});
            skCircle(sketch, "E5.27.26.0", {"center": v(-31.75, 105.16) * mm, "radius": 1.02 * mm});
            skCircle(sketch, "E5.27.27.0", {"center": v(-31.75, 108.97) * mm, "radius": 1.02 * mm});
            skCircle(sketch, "E5.27.28.0", {"center": v(-31.75, 112.78) * mm, "radius": 1.02 * mm});
            skCircle(sketch, "E5.27.29.0", {"center": v(-31.75, 116.59) * mm, "radius": 1.02 * mm});
            skCircle(sketch, "E5.27.30.0", {"center": v(-31.75, 120.4) * mm, "radius": 1.02 * mm});
            skCircle(sketch, "E5.28.0.0", {"center": v(-28.45, 6.1) * mm, "radius": 1.02 * mm});
            skCircle(sketch, "E5.28.1.0", {"center": v(-28.45, 9.9) * mm, "radius": 1.02 * mm});
            skCircle(sketch, "E5.28.2.0", {"center": v(-28.45, 13.72) * mm, "radius": 1.02 * mm});
            skCircle(sketch, "E5.28.3.0", {"center": v(-28.45, 17.53) * mm, "radius": 1.02 * mm});
            skCircle(sketch, "E5.28.4.0", {"center": v(-28.45, 21.34) * mm, "radius": 1.02 * mm});
            skCircle(sketch, "E5.28.5.0", {"center": v(-28.45, 25.15) * mm, "radius": 1.02 * mm});
            skCircle(sketch, "E5.28.6.0", {"center": v(-28.45, 28.96) * mm, "radius": 1.02 * mm});
            skCircle(sketch, "E5.28.7.0", {"center": v(-28.45, 32.77) * mm, "radius": 1.02 * mm});
            skCircle(sketch, "E5.28.8.0", {"center": v(-28.45, 36.58) * mm, "radius": 1.02 * mm});
            skCircle(sketch, "E5.28.9.0", {"center": v(-28.45, 40.39) * mm, "radius": 1.02 * mm});
            skCircle(sketch, "E5.28.10.0", {"center": v(-28.45, 44.2) * mm, "radius": 1.02 * mm});
            skCircle(sketch, "E5.28.11.0", {"center": v(-28.45, 48) * mm, "radius": 1.02 * mm});
            skCircle(sketch, "E5.28.12.0", {"center": v(-28.45, 51.82) * mm, "radius": 1.02 * mm});
            skCircle(sketch, "E5.28.13.0", {"center": v(-28.45, 55.63) * mm, "radius": 1.02 * mm});
            skCircle(sketch, "E5.28.14.0", {"center": v(-28.45, 59.44) * mm, "radius": 1.02 * mm});
            skCircle(sketch, "E5.28.15.0", {"center": v(-28.45, 63.25) * mm, "radius": 1.02 * mm});
            skCircle(sketch, "E5.28.16.0", {"center": v(-28.45, 67.06) * mm, "radius": 1.02 * mm});
            skCircle(sketch, "E5.28.17.0", {"center": v(-28.45, 70.87) * mm, "radius": 1.02 * mm});
            skCircle(sketch, "E5.28.18.0", {"center": v(-28.45, 74.68) * mm, "radius": 1.02 * mm});
            skCircle(sketch, "E5.28.19.0", {"center": v(-28.45, 78.49) * mm, "radius": 1.02 * mm});
            skCircle(sketch, "E5.28.20.0", {"center": v(-28.45, 82.3) * mm, "radius": 1.02 * mm});
            skCircle(sketch, "E5.28.21.0", {"center": v(-28.45, 86.1) * mm, "radius": 1.02 * mm});
            skCircle(sketch, "E5.28.22.0", {"center": v(-28.45, 89.92) * mm, "radius": 1.02 * mm});
            skCircle(sketch, "E5.28.23.0", {"center": v(-28.45, 93.73) * mm, "radius": 1.02 * mm});
            skCircle(sketch, "E5.28.24.0", {"center": v(-28.45, 97.54) * mm, "radius": 1.02 * mm});
            skCircle(sketch, "E5.28.25.0", {"center": v(-28.45, 101.35) * mm, "radius": 1.02 * mm});
            skCircle(sketch, "E5.28.26.0", {"center": v(-28.45, 105.16) * mm, "radius": 1.02 * mm});
            skCircle(sketch, "E5.28.27.0", {"center": v(-28.45, 108.97) * mm, "radius": 1.02 * mm});
            skCircle(sketch, "E5.28.28.0", {"center": v(-28.45, 112.78) * mm, "radius": 1.02 * mm});
            skCircle(sketch, "E5.28.29.0", {"center": v(-28.45, 116.59) * mm, "radius": 1.02 * mm});
            skCircle(sketch, "E5.28.30.0", {"center": v(-28.45, 120.4) * mm, "radius": 1.02 * mm});
            skCircle(sketch, "E5.29.0.0", {"center": v(-25.15, 6.1) * mm, "radius": 1.02 * mm});
            skCircle(sketch, "E5.29.1.0", {"center": v(-25.15, 9.9) * mm, "radius": 1.02 * mm});
            skCircle(sketch, "E5.29.2.0", {"center": v(-25.15, 13.72) * mm, "radius": 1.02 * mm});
            skCircle(sketch, "E5.29.3.0", {"center": v(-25.15, 17.53) * mm, "radius": 1.02 * mm});
            skCircle(sketch, "E5.29.4.0", {"center": v(-25.15, 21.34) * mm, "radius": 1.02 * mm});
            skCircle(sketch, "E5.29.5.0", {"center": v(-25.15, 25.15) * mm, "radius": 1.02 * mm});
            skCircle(sketch, "E5.29.6.0", {"center": v(-25.15, 28.96) * mm, "radius": 1.02 * mm});
            skCircle(sketch, "E5.29.7.0", {"center": v(-25.15, 32.77) * mm, "radius": 1.02 * mm});
            skCircle(sketch, "E5.29.8.0", {"center": v(-25.15, 36.58) * mm, "radius": 1.02 * mm});
            skCircle(sketch, "E5.29.9.0", {"center": v(-25.15, 40.39) * mm, "radius": 1.02 * mm});
            skCircle(sketch, "E5.29.10.0", {"center": v(-25.15, 44.2) * mm, "radius": 1.02 * mm});
            skCircle(sketch, "E5.29.11.0", {"center": v(-25.15, 48) * mm, "radius": 1.02 * mm});
            skCircle(sketch, "E5.29.12.0", {"center": v(-25.15, 51.82) * mm, "radius": 1.02 * mm});
            skCircle(sketch, "E5.29.13.0", {"center": v(-25.15, 55.63) * mm, "radius": 1.02 * mm});
            skCircle(sketch, "E5.29.14.0", {"center": v(-25.15, 59.44) * mm, "radius": 1.02 * mm});
            skCircle(sketch, "E5.29.15.0", {"center": v(-25.15, 63.25) * mm, "radius": 1.02 * mm});
            skCircle(sketch, "E5.29.16.0", {"center": v(-25.15, 67.06) * mm, "radius": 1.02 * mm});
            skCircle(sketch, "E5.29.17.0", {"center": v(-25.15, 70.87) * mm, "radius": 1.02 * mm});
            skCircle(sketch, "E5.29.18.0", {"center": v(-25.15, 74.68) * mm, "radius": 1.02 * mm});
            skCircle(sketch, "E5.29.19.0", {"center": v(-25.15, 78.49) * mm, "radius": 1.02 * mm});
            skCircle(sketch, "E5.29.20.0", {"center": v(-25.15, 82.3) * mm, "radius": 1.02 * mm});
            skCircle(sketch, "E5.29.21.0", {"center": v(-25.15, 86.1) * mm, "radius": 1.02 * mm});
            skCircle(sketch, "E5.29.22.0", {"center": v(-25.15, 89.92) * mm, "radius": 1.02 * mm});
            skCircle(sketch, "E5.29.23.0", {"center": v(-25.15, 93.73) * mm, "radius": 1.02 * mm});
            skCircle(sketch, "E5.29.24.0", {"center": v(-25.15, 97.54) * mm, "radius": 1.02 * mm});
            skCircle(sketch, "E5.29.25.0", {"center": v(-25.15, 101.35) * mm, "radius": 1.02 * mm});
            skCircle(sketch, "E5.29.26.0", {"center": v(-25.15, 105.16) * mm, "radius": 1.02 * mm});
            skCircle(sketch, "E5.29.27.0", {"center": v(-25.15, 108.97) * mm, "radius": 1.02 * mm});
            skCircle(sketch, "E5.29.28.0", {"center": v(-25.15, 112.78) * mm, "radius": 1.02 * mm});
            skCircle(sketch, "E5.29.29.0", {"center": v(-25.15, 116.59) * mm, "radius": 1.02 * mm});
            skCircle(sketch, "E5.29.30.0", {"center": v(-25.15, 120.4) * mm, "radius": 1.02 * mm});
            skCircle(sketch, "E5.30.0.0", {"center": v(-21.84, 6.1) * mm, "radius": 1.02 * mm});
            skCircle(sketch, "E5.30.1.0", {"center": v(-21.84, 9.9) * mm, "radius": 1.02 * mm});
            skCircle(sketch, "E5.30.2.0", {"center": v(-21.84, 13.72) * mm, "radius": 1.02 * mm});
            skCircle(sketch, "E5.30.3.0", {"center": v(-21.84, 17.53) * mm, "radius": 1.02 * mm});
            skCircle(sketch, "E5.30.4.0", {"center": v(-21.84, 21.34) * mm, "radius": 1.02 * mm});
            skCircle(sketch, "E5.30.5.0", {"center": v(-21.84, 25.15) * mm, "radius": 1.02 * mm});
            skCircle(sketch, "E5.30.6.0", {"center": v(-21.84, 28.96) * mm, "radius": 1.02 * mm});
            skCircle(sketch, "E5.30.7.0", {"center": v(-21.84, 32.77) * mm, "radius": 1.02 * mm});
            skCircle(sketch, "E5.30.8.0", {"center": v(-21.84, 36.58) * mm, "radius": 1.02 * mm});
            skCircle(sketch, "E5.30.9.0", {"center": v(-21.84, 40.39) * mm, "radius": 1.02 * mm});
            skCircle(sketch, "E5.30.10.0", {"center": v(-21.84, 44.2) * mm, "radius": 1.02 * mm});
            skCircle(sketch, "E5.30.11.0", {"center": v(-21.84, 48) * mm, "radius": 1.02 * mm});
            skCircle(sketch, "E5.30.12.0", {"center": v(-21.84, 51.82) * mm, "radius": 1.02 * mm});
            skCircle(sketch, "E5.30.13.0", {"center": v(-21.84, 55.63) * mm, "radius": 1.02 * mm});
            skCircle(sketch, "E5.30.14.0", {"center": v(-21.84, 59.44) * mm, "radius": 1.02 * mm});
            skCircle(sketch, "E5.30.15.0", {"center": v(-21.84, 63.25) * mm, "radius": 1.02 * mm});
            skCircle(sketch, "E5.30.16.0", {"center": v(-21.84, 67.06) * mm, "radius": 1.02 * mm});
            skCircle(sketch, "E5.30.17.0", {"center": v(-21.84, 70.87) * mm, "radius": 1.02 * mm});
            skCircle(sketch, "E5.30.18.0", {"center": v(-21.84, 74.68) * mm, "radius": 1.02 * mm});
            skCircle(sketch, "E5.30.19.0", {"center": v(-21.84, 78.49) * mm, "radius": 1.02 * mm});
            skCircle(sketch, "E5.30.20.0", {"center": v(-21.84, 82.3) * mm, "radius": 1.02 * mm});
            skCircle(sketch, "E5.30.21.0", {"center": v(-21.84, 86.1) * mm, "radius": 1.02 * mm});
            skCircle(sketch, "E5.30.22.0", {"center": v(-21.84, 89.92) * mm, "radius": 1.02 * mm});
            skCircle(sketch, "E5.30.23.0", {"center": v(-21.84, 93.73) * mm, "radius": 1.02 * mm});
            skCircle(sketch, "E5.30.24.0", {"center": v(-21.84, 97.54) * mm, "radius": 1.02 * mm});
            skCircle(sketch, "E5.30.25.0", {"center": v(-21.84, 101.35) * mm, "radius": 1.02 * mm});
            skCircle(sketch, "E5.30.26.0", {"center": v(-21.84, 105.16) * mm, "radius": 1.02 * mm});
            skCircle(sketch, "E5.30.27.0", {"center": v(-21.84, 108.97) * mm, "radius": 1.02 * mm});
            skCircle(sketch, "E5.30.28.0", {"center": v(-21.84, 112.78) * mm, "radius": 1.02 * mm});
            skCircle(sketch, "E5.30.29.0", {"center": v(-21.84, 116.59) * mm, "radius": 1.02 * mm});
            skCircle(sketch, "E5.30.30.0", {"center": v(-21.84, 120.4) * mm, "radius": 1.02 * mm});
            skCircle(sketch, "E5.31.0.0", {"center": v(-18.54, 6.1) * mm, "radius": 1.02 * mm});
            skCircle(sketch, "E5.31.1.0", {"center": v(-18.54, 9.9) * mm, "radius": 1.02 * mm});
            skCircle(sketch, "E5.31.2.0", {"center": v(-18.54, 13.72) * mm, "radius": 1.02 * mm});
            skCircle(sketch, "E5.31.3.0", {"center": v(-18.54, 17.53) * mm, "radius": 1.02 * mm});
            skCircle(sketch, "E5.31.4.0", {"center": v(-18.54, 21.34) * mm, "radius": 1.02 * mm});
            skCircle(sketch, "E5.31.5.0", {"center": v(-18.54, 25.15) * mm, "radius": 1.02 * mm});
            skCircle(sketch, "E5.31.6.0", {"center": v(-18.54, 28.96) * mm, "radius": 1.02 * mm});
            skCircle(sketch, "E5.31.7.0", {"center": v(-18.54, 32.77) * mm, "radius": 1.02 * mm});
            skCircle(sketch, "E5.31.8.0", {"center": v(-18.54, 36.58) * mm, "radius": 1.02 * mm});
            skCircle(sketch, "E5.31.9.0", {"center": v(-18.54, 40.39) * mm, "radius": 1.02 * mm});
            skCircle(sketch, "E5.31.10.0", {"center": v(-18.54, 44.2) * mm, "radius": 1.02 * mm});
            skCircle(sketch, "E5.31.11.0", {"center": v(-18.54, 48) * mm, "radius": 1.02 * mm});
            skCircle(sketch, "E5.31.12.0", {"center": v(-18.54, 51.82) * mm, "radius": 1.02 * mm});
            skCircle(sketch, "E5.31.13.0", {"center": v(-18.54, 55.63) * mm, "radius": 1.02 * mm});
            skCircle(sketch, "E5.31.14.0", {"center": v(-18.54, 59.44) * mm, "radius": 1.02 * mm});
            skCircle(sketch, "E5.31.15.0", {"center": v(-18.54, 63.25) * mm, "radius": 1.02 * mm});
            skCircle(sketch, "E5.31.16.0", {"center": v(-18.54, 67.06) * mm, "radius": 1.02 * mm});
            skCircle(sketch, "E5.31.17.0", {"center": v(-18.54, 70.87) * mm, "radius": 1.02 * mm});
            skCircle(sketch, "E5.31.18.0", {"center": v(-18.54, 74.68) * mm, "radius": 1.02 * mm});
            skCircle(sketch, "E5.31.19.0", {"center": v(-18.54, 78.49) * mm, "radius": 1.02 * mm});
            skCircle(sketch, "E5.31.20.0", {"center": v(-18.54, 82.3) * mm, "radius": 1.02 * mm});
            skCircle(sketch, "E5.31.21.0", {"center": v(-18.54, 86.1) * mm, "radius": 1.02 * mm});
            skCircle(sketch, "E5.31.22.0", {"center": v(-18.54, 89.92) * mm, "radius": 1.02 * mm});
            skCircle(sketch, "E5.31.23.0", {"center": v(-18.54, 93.73) * mm, "radius": 1.02 * mm});
            skCircle(sketch, "E5.31.24.0", {"center": v(-18.54, 97.54) * mm, "radius": 1.02 * mm});
            skCircle(sketch, "E5.31.25.0", {"center": v(-18.54, 101.35) * mm, "radius": 1.02 * mm});
            skCircle(sketch, "E5.31.26.0", {"center": v(-18.54, 105.16) * mm, "radius": 1.02 * mm});
            skCircle(sketch, "E5.31.27.0", {"center": v(-18.54, 108.97) * mm, "radius": 1.02 * mm});
            skCircle(sketch, "E5.31.28.0", {"center": v(-18.54, 112.78) * mm, "radius": 1.02 * mm});
            skCircle(sketch, "E5.31.29.0", {"center": v(-18.54, 116.59) * mm, "radius": 1.02 * mm});
            skCircle(sketch, "E5.31.30.0", {"center": v(-18.54, 120.4) * mm, "radius": 1.02 * mm});
            skCircle(sketch, "E5.32.0.0", {"center": v(-15.24, 6.1) * mm, "radius": 1.02 * mm});
            skCircle(sketch, "E5.32.1.0", {"center": v(-15.24, 9.9) * mm, "radius": 1.02 * mm});
            skCircle(sketch, "E5.32.2.0", {"center": v(-15.24, 13.72) * mm, "radius": 1.02 * mm});
            skCircle(sketch, "E5.32.3.0", {"center": v(-15.24, 17.53) * mm, "radius": 1.02 * mm});
            skCircle(sketch, "E5.32.4.0", {"center": v(-15.24, 21.34) * mm, "radius": 1.02 * mm});
            skCircle(sketch, "E5.32.5.0", {"center": v(-15.24, 25.15) * mm, "radius": 1.02 * mm});
            skCircle(sketch, "E5.32.6.0", {"center": v(-15.24, 28.96) * mm, "radius": 1.02 * mm});
            skCircle(sketch, "E5.32.7.0", {"center": v(-15.24, 32.77) * mm, "radius": 1.02 * mm});
            skCircle(sketch, "E5.32.8.0", {"center": v(-15.24, 36.58) * mm, "radius": 1.02 * mm});
            skCircle(sketch, "E5.32.9.0", {"center": v(-15.24, 40.39) * mm, "radius": 1.02 * mm});
            skCircle(sketch, "E5.32.10.0", {"center": v(-15.24, 44.2) * mm, "radius": 1.02 * mm});
            skCircle(sketch, "E5.32.11.0", {"center": v(-15.24, 48) * mm, "radius": 1.02 * mm});
            skCircle(sketch, "E5.32.12.0", {"center": v(-15.24, 51.82) * mm, "radius": 1.02 * mm});
            skCircle(sketch, "E5.32.13.0", {"center": v(-15.24, 55.63) * mm, "radius": 1.02 * mm});
            skCircle(sketch, "E5.32.14.0", {"center": v(-15.24, 59.44) * mm, "radius": 1.02 * mm});
            skCircle(sketch, "E5.32.15.0", {"center": v(-15.24, 63.25) * mm, "radius": 1.02 * mm});
            skCircle(sketch, "E5.32.16.0", {"center": v(-15.24, 67.06) * mm, "radius": 1.02 * mm});
            skCircle(sketch, "E5.32.17.0", {"center": v(-15.24, 70.87) * mm, "radius": 1.02 * mm});
            skCircle(sketch, "E5.32.18.0", {"center": v(-15.24, 74.68) * mm, "radius": 1.02 * mm});
            skCircle(sketch, "E5.32.19.0", {"center": v(-15.24, 78.49) * mm, "radius": 1.02 * mm});
            skCircle(sketch, "E5.32.20.0", {"center": v(-15.24, 82.3) * mm, "radius": 1.02 * mm});
            skCircle(sketch, "E5.32.21.0", {"center": v(-15.24, 86.1) * mm, "radius": 1.02 * mm});
            skCircle(sketch, "E5.32.22.0", {"center": v(-15.24, 89.92) * mm, "radius": 1.02 * mm});
            skCircle(sketch, "E5.32.23.0", {"center": v(-15.24, 93.73) * mm, "radius": 1.02 * mm});
            skCircle(sketch, "E5.32.24.0", {"center": v(-15.24, 97.54) * mm, "radius": 1.02 * mm});
            skCircle(sketch, "E5.32.25.0", {"center": v(-15.24, 101.35) * mm, "radius": 1.02 * mm});
            skCircle(sketch, "E5.32.26.0", {"center": v(-15.24, 105.16) * mm, "radius": 1.02 * mm});
            skCircle(sketch, "E5.32.27.0", {"center": v(-15.24, 108.97) * mm, "radius": 1.02 * mm});
            skCircle(sketch, "E5.32.28.0", {"center": v(-15.24, 112.78) * mm, "radius": 1.02 * mm});
            skCircle(sketch, "E5.32.29.0", {"center": v(-15.24, 116.59) * mm, "radius": 1.02 * mm});
            skCircle(sketch, "E5.32.30.0", {"center": v(-15.24, 120.4) * mm, "radius": 1.02 * mm});
            skCircle(sketch, "E5.33.0.0", {"center": v(-11.94, 6.1) * mm, "radius": 1.02 * mm});
            skCircle(sketch, "E5.33.1.0", {"center": v(-11.94, 9.9) * mm, "radius": 1.02 * mm});
            skCircle(sketch, "E5.33.2.0", {"center": v(-11.94, 13.72) * mm, "radius": 1.02 * mm});
            skCircle(sketch, "E5.33.3.0", {"center": v(-11.94, 17.53) * mm, "radius": 1.02 * mm});
            skCircle(sketch, "E5.33.4.0", {"center": v(-11.94, 21.34) * mm, "radius": 1.02 * mm});
            skCircle(sketch, "E5.33.5.0", {"center": v(-11.94, 25.15) * mm, "radius": 1.02 * mm});
            skCircle(sketch, "E5.33.6.0", {"center": v(-11.94, 28.96) * mm, "radius": 1.02 * mm});
            skCircle(sketch, "E5.33.7.0", {"center": v(-11.94, 32.77) * mm, "radius": 1.02 * mm});
            skCircle(sketch, "E5.33.8.0", {"center": v(-11.94, 36.58) * mm, "radius": 1.02 * mm});
            skCircle(sketch, "E5.33.9.0", {"center": v(-11.94, 40.39) * mm, "radius": 1.02 * mm});
            skCircle(sketch, "E5.33.10.0", {"center": v(-11.94, 44.2) * mm, "radius": 1.02 * mm});
            skCircle(sketch, "E5.33.11.0", {"center": v(-11.94, 48) * mm, "radius": 1.02 * mm});
            skCircle(sketch, "E5.33.12.0", {"center": v(-11.94, 51.82) * mm, "radius": 1.02 * mm});
            skCircle(sketch, "E5.33.13.0", {"center": v(-11.94, 55.63) * mm, "radius": 1.02 * mm});
            skCircle(sketch, "E5.33.14.0", {"center": v(-11.94, 59.44) * mm, "radius": 1.02 * mm});
            skCircle(sketch, "E5.33.15.0", {"center": v(-11.94, 63.25) * mm, "radius": 1.02 * mm});
            skCircle(sketch, "E5.33.16.0", {"center": v(-11.94, 67.06) * mm, "radius": 1.02 * mm});
            skCircle(sketch, "E5.33.17.0", {"center": v(-11.94, 70.87) * mm, "radius": 1.02 * mm});
            skCircle(sketch, "E5.33.18.0", {"center": v(-11.94, 74.68) * mm, "radius": 1.02 * mm});
            skCircle(sketch, "E5.33.19.0", {"center": v(-11.94, 78.49) * mm, "radius": 1.02 * mm});
            skCircle(sketch, "E5.33.20.0", {"center": v(-11.94, 82.3) * mm, "radius": 1.02 * mm});
            skCircle(sketch, "E5.33.21.0", {"center": v(-11.94, 86.1) * mm, "radius": 1.02 * mm});
            skCircle(sketch, "E5.33.22.0", {"center": v(-11.94, 89.92) * mm, "radius": 1.02 * mm});
            skCircle(sketch, "E5.33.23.0", {"center": v(-11.94, 93.73) * mm, "radius": 1.02 * mm});
            skCircle(sketch, "E5.33.24.0", {"center": v(-11.94, 97.54) * mm, "radius": 1.02 * mm});
            skCircle(sketch, "E5.33.25.0", {"center": v(-11.94, 101.35) * mm, "radius": 1.02 * mm});
            skCircle(sketch, "E5.33.26.0", {"center": v(-11.94, 105.16) * mm, "radius": 1.02 * mm});
            skCircle(sketch, "E5.33.27.0", {"center": v(-11.94, 108.97) * mm, "radius": 1.02 * mm});
            skCircle(sketch, "E5.33.28.0", {"center": v(-11.94, 112.78) * mm, "radius": 1.02 * mm});
            skCircle(sketch, "E5.33.29.0", {"center": v(-11.94, 116.59) * mm, "radius": 1.02 * mm});
            skCircle(sketch, "E5.33.30.0", {"center": v(-11.94, 120.4) * mm, "radius": 1.02 * mm});
            skCircle(sketch, "E5.34.0.0", {"center": v(-8.64, 6.1) * mm, "radius": 1.02 * mm});
            skCircle(sketch, "E5.34.1.0", {"center": v(-8.64, 9.9) * mm, "radius": 1.02 * mm});
            skCircle(sketch, "E5.34.2.0", {"center": v(-8.64, 13.72) * mm, "radius": 1.02 * mm});
            skCircle(sketch, "E5.34.3.0", {"center": v(-8.64, 17.53) * mm, "radius": 1.02 * mm});
            skCircle(sketch, "E5.34.4.0", {"center": v(-8.64, 21.34) * mm, "radius": 1.02 * mm});
            skCircle(sketch, "E5.34.5.0", {"center": v(-8.64, 25.15) * mm, "radius": 1.02 * mm});
            skCircle(sketch, "E5.34.6.0", {"center": v(-8.64, 28.96) * mm, "radius": 1.02 * mm});
            skCircle(sketch, "E5.34.7.0", {"center": v(-8.64, 32.77) * mm, "radius": 1.02 * mm});
            skCircle(sketch, "E5.34.8.0", {"center": v(-8.64, 36.58) * mm, "radius": 1.02 * mm});
            skCircle(sketch, "E5.34.9.0", {"center": v(-8.64, 40.39) * mm, "radius": 1.02 * mm});
            skCircle(sketch, "E5.34.10.0", {"center": v(-8.64, 44.2) * mm, "radius": 1.02 * mm});
            skCircle(sketch, "E5.34.11.0", {"center": v(-8.64, 48) * mm, "radius": 1.02 * mm});
            skCircle(sketch, "E5.34.12.0", {"center": v(-8.64, 51.82) * mm, "radius": 1.02 * mm});
            skCircle(sketch, "E5.34.13.0", {"center": v(-8.64, 55.63) * mm, "radius": 1.02 * mm});
            skCircle(sketch, "E5.34.14.0", {"center": v(-8.64, 59.44) * mm, "radius": 1.02 * mm});
            skCircle(sketch, "E5.34.15.0", {"center": v(-8.64, 63.25) * mm, "radius": 1.02 * mm});
            skCircle(sketch, "E5.34.16.0", {"center": v(-8.64, 67.06) * mm, "radius": 1.02 * mm});
            skCircle(sketch, "E5.34.17.0", {"center": v(-8.64, 70.87) * mm, "radius": 1.02 * mm});
            skCircle(sketch, "E5.34.18.0", {"center": v(-8.64, 74.68) * mm, "radius": 1.02 * mm});
            skCircle(sketch, "E5.34.19.0", {"center": v(-8.64, 78.49) * mm, "radius": 1.02 * mm});
            skCircle(sketch, "E5.34.20.0", {"center": v(-8.64, 82.3) * mm, "radius": 1.02 * mm});
            skCircle(sketch, "E5.34.21.0", {"center": v(-8.64, 86.1) * mm, "radius": 1.02 * mm});
            skCircle(sketch, "E5.34.22.0", {"center": v(-8.64, 89.92) * mm, "radius": 1.02 * mm});
            skCircle(sketch, "E5.34.23.0", {"center": v(-8.64, 93.73) * mm, "radius": 1.02 * mm});
            skCircle(sketch, "E5.34.24.0", {"center": v(-8.64, 97.54) * mm, "radius": 1.02 * mm});
            skCircle(sketch, "E5.34.25.0", {"center": v(-8.64, 101.35) * mm, "radius": 1.02 * mm});
            skCircle(sketch, "E5.34.26.0", {"center": v(-8.64, 105.16) * mm, "radius": 1.02 * mm});
            skCircle(sketch, "E5.34.27.0", {"center": v(-8.64, 108.97) * mm, "radius": 1.02 * mm});
            skCircle(sketch, "E5.34.28.0", {"center": v(-8.64, 112.78) * mm, "radius": 1.02 * mm});
            skCircle(sketch, "E5.34.29.0", {"center": v(-8.64, 116.59) * mm, "radius": 1.02 * mm});
            skCircle(sketch, "E5.34.30.0", {"center": v(-8.64, 120.4) * mm, "radius": 1.02 * mm});
            skLineSegment(sketch, "E5.direction1", {"start": v(-120.9, 6.1) * mm, "end": v(-117.6, 6.1) * mm, "construction": true});
            skLineSegment(sketch, "E5.direction2", {"start": v(-120.9, 6.1) * mm, "end": v(-120.9, 9.9) * mm, "construction": true});
            skSolve(sketch);
        }
        {
            var Q0;
            Q0=makeQuery(id+"F7.imprint","IMPRINT",FACE,{"disambiguationData":[TD([[makeQuery(id+"F7.imprint","IMPRINT",EDGE,{"derivedFrom":sQuery(id+"F7.wireOp",EDGE,"E5.1.15.0")}),1.0]])]});
            var Q1;
            Q1=makeQuery(id+"F7.imprint","IMPRINT",FACE,{"disambiguationData":[TD([[makeQuery(id+"F7.imprint","IMPRINT",EDGE,{"derivedFrom":sQuery(id+"F7.wireOp",EDGE,"E5.23.21.0")}),1.0]])]});
            var Q2;
            Q2=makeQuery(id+"F7.imprint","IMPRINT",FACE,{"disambiguationData":[TD([[makeQuery(id+"F7.imprint","IMPRINT",EDGE,{"derivedFrom":sQuery(id+"F7.wireOp",EDGE,"E5.18.16.0")}),1.0]])]});
            var Q3;
            Q3=makeQuery(id+"F7.imprint","IMPRINT",FACE,{"disambiguationData":[TD([[makeQuery(id+"F7.imprint","IMPRINT",EDGE,{"derivedFrom":sQuery(id+"F7.wireOp",EDGE,"E5.26.26.0")}),1.0]])]});
            var Q4;
            Q4=makeQuery(id+"F7.imprint","IMPRINT",FACE,{"disambiguationData":[TD([[makeQuery(id+"F7.imprint","IMPRINT",EDGE,{"derivedFrom":sQuery(id+"F7.wireOp",EDGE,"E5.22.6.0")}),1.0]])]});
            var Q5;
            Q5=makeQuery(id+"F7.imprint","IMPRINT",FACE,{"disambiguationData":[TD([[makeQuery(id+"F7.imprint","IMPRINT",EDGE,{"derivedFrom":sQuery(id+"F7.wireOp",EDGE,"E5.31.15.0")}),1.0]])]});
            var Q6;
            Q6=makeQuery(id+"F7.imprint","IMPRINT",FACE,{"disambiguationData":[TD([[makeQuery(id+"F7.imprint","IMPRINT",EDGE,{"derivedFrom":sQuery(id+"F7.wireOp",EDGE,"E5.27.11.0")}),1.0]])]});
            var Q7;
            Q7=makeQuery(id+"F7.imprint","IMPRINT",FACE,{"disambiguationData":[TD([[makeQuery(id+"F7.imprint","IMPRINT",EDGE,{"derivedFrom":sQuery(id+"F7.wireOp",EDGE,"E5.10.10.0")}),1.0]])]});
            var Q8;
            Q8=makeQuery(id+"F7.imprint","IMPRINT",FACE,{"disambiguationData":[TD([[makeQuery(id+"F7.imprint","IMPRINT",EDGE,{"derivedFrom":sQuery(id+"F7.wireOp",EDGE,"E5.10.26.0")}),1.0]])]});
            var Q9;
            Q9=makeQuery(id+"F7.imprint","IMPRINT",FACE,{"disambiguationData":[TD([[makeQuery(id+"F7.imprint","IMPRINT",EDGE,{"derivedFrom":sQuery(id+"F7.wireOp",EDGE,"E5.5.5.0")}),1.0]])]});
            var Q10;
            Q10=makeQuery(id+"F7.imprint","IMPRINT",FACE,{"disambiguationData":[TD([[makeQuery(id+"F7.imprint","IMPRINT",EDGE,{"derivedFrom":sQuery(id+"F7.wireOp",EDGE,"E5.5.21.0")}),1.0]])]});
            var Q11;
            Q11=makeQuery(id+"F7.imprint","IMPRINT",FACE,{"disambiguationData":[TD([[makeQuery(id+"F7.imprint","IMPRINT",EDGE,{"derivedFrom":sQuery(id+"F7.wireOp",EDGE,"E5.1.1.0")}),1.0]])]});
            var Q12;
            Q12=makeQuery(id+"F7.imprint","IMPRINT",FACE,{"disambiguationData":[TD([[makeQuery(id+"F7.imprint","IMPRINT",EDGE,{"derivedFrom":sQuery(id+"F7.wireOp",EDGE,"E5.2.16.0")}),1.0]])]});
            var Q13;
            Q13=makeQuery(id+"F7.imprint","IMPRINT",FACE,{"disambiguationData":[TD([[makeQuery(id+"F7.imprint","IMPRINT",EDGE,{"derivedFrom":sQuery(id+"F7.wireOp",EDGE,"E5.27.26.0")}),1.0]])]});
            var Q14;
            Q14=makeQuery(id+"F7.imprint","IMPRINT",FACE,{"disambiguationData":[TD([[makeQuery(id+"F7.imprint","IMPRINT",EDGE,{"derivedFrom":sQuery(id+"F7.wireOp",EDGE,"E5.1.16.0")}),1.0]])]});
            var Q15;
            Q15=makeQuery(id+"F7.imprint","IMPRINT",FACE,{"disambiguationData":[TD([[makeQuery(id+"F7.imprint","IMPRINT",EDGE,{"derivedFrom":sQuery(id+"F7.wireOp",EDGE,"E5.18.1.0")}),1.0]])]});
            var Q16;
            Q16=makeQuery(id+"F7.imprint","IMPRINT",FACE,{"disambiguationData":[TD([[makeQuery(id+"F7.imprint","IMPRINT",EDGE,{"derivedFrom":sQuery(id+"F7.wireOp",EDGE,"E5.22.21.0")}),1.0]])]});
            var Q17;
            Q17=makeQuery(id+"F7.imprint","IMPRINT",FACE,{"disambiguationData":[TD([[makeQuery(id+"F7.imprint","IMPRINT",EDGE,{"derivedFrom":sQuery(id+"F7.wireOp",EDGE,"E5.22.5.0")}),1.0]])]});
            var Q18;
            Q18=makeQuery(id+"F7.imprint","IMPRINT",FACE,{"disambiguationData":[TD([[makeQuery(id+"F7.imprint","IMPRINT",EDGE,{"derivedFrom":sQuery(id+"F7.wireOp",EDGE,"E5.6.5.0")}),1.0]])]});
            var Q19;
            Q19=makeQuery(id+"F7.imprint","IMPRINT",FACE,{"disambiguationData":[TD([[makeQuery(id+"F7.imprint","IMPRINT",EDGE,{"derivedFrom":sQuery(id+"F7.wireOp",EDGE,"E5.6.21.0")}),1.0]])]});
            var Q20;
            Q20=makeQuery(id+"F7.imprint","IMPRINT",FACE,{"disambiguationData":[TD([[makeQuery(id+"F7.imprint","IMPRINT",EDGE,{"derivedFrom":sQuery(id+"F7.wireOp",EDGE,"E5.14.15.0")}),1.0]])]});
            var Q21;
            Q21=makeQuery(id+"F7.imprint","IMPRINT",FACE,{"disambiguationData":[TD([[makeQuery(id+"F7.imprint","IMPRINT",EDGE,{"derivedFrom":sQuery(id+"F7.wireOp",EDGE,"E5.31.16.0")}),1.0]])]});
            var Q22;
            Q22=makeQuery(id+"F7.imprint","IMPRINT",FACE,{"disambiguationData":[TD([[makeQuery(id+"F7.imprint","IMPRINT",EDGE,{"derivedFrom":sQuery(id+"F7.wireOp",EDGE,"E5.10.11.0")}),1.0]])]});
            var Q23;
            Q23=makeQuery(id+"F7.imprint","IMPRINT",FACE,{"disambiguationData":[TD([[makeQuery(id+"F7.imprint","IMPRINT",EDGE,{"derivedFrom":sQuery(id+"F7.wireOp",EDGE,"E5.9.26.0")}),1.0]])]});
            var Q24;
            Q24=makeQuery(id+"F7.imprint","IMPRINT",FACE,{"disambiguationData":[TD([[makeQuery(id+"F7.imprint","IMPRINT",EDGE,{"derivedFrom":sQuery(id+"F7.wireOp",EDGE,"E5.31.1.0")}),1.0]])]});
            var Q25;
            Q25=makeQuery(id+"F7.imprint","IMPRINT",FACE,{"disambiguationData":[TD([[makeQuery(id+"F7.imprint","IMPRINT",EDGE,{"derivedFrom":sQuery(id+"F7.wireOp",EDGE,"E5.30.16.0")}),1.0]])]});
            var Q26;
            Q26=makeQuery(id+"F7.imprint","IMPRINT",FACE,{"disambiguationData":[TD([[makeQuery(id+"F7.imprint","IMPRINT",EDGE,{"derivedFrom":sQuery(id+"F7.wireOp",EDGE,"E5.26.11.0")}),1.0]])]});
            var Q27;
            Q27=makeQuery(id+"F7.imprint","IMPRINT",FACE,{"disambiguationData":[TD([[makeQuery(id+"F7.imprint","IMPRINT",EDGE,{"derivedFrom":sQuery(id+"F7.wireOp",EDGE,"E5.14.16.0")}),1.0]])]});
            var Q28;
            Q28=makeQuery(id+"F7.imprint","IMPRINT",FACE,{"disambiguationData":[TD([[makeQuery(id+"F7.imprint","IMPRINT",EDGE,{"derivedFrom":sQuery(id+"F7.wireOp",EDGE,"E5.18.20.0")}),1.0]])]});
            var Q29;
            Q29=makeQuery(id+"F7.imprint","IMPRINT",FACE,{"disambiguationData":[TD([[makeQuery(id+"F7.imprint","IMPRINT",EDGE,{"derivedFrom":sQuery(id+"F7.wireOp",EDGE,"E5.14.1.0")}),1.0]])]});
            var Q30;
            Q30=makeQuery(id+"F7.imprint","IMPRINT",FACE,{"disambiguationData":[TD([[makeQuery(id+"F7.imprint","IMPRINT",EDGE,{"derivedFrom":sQuery(id+"F7.wireOp",EDGE,"E5.18.21.0")}),1.0]])]});
            var Q31;
            Q31=makeQuery(id+"F7.imprint","IMPRINT",FACE,{"disambiguationData":[TD([[makeQuery(id+"F7.imprint","IMPRINT",EDGE,{"derivedFrom":sQuery(id+"F7.wireOp",EDGE,"E5.18.5.0")}),1.0]])]});
            var Q32;
            Q32=makeQuery(id+"F7.imprint","IMPRINT",FACE,{"disambiguationData":[TD([[makeQuery(id+"F7.imprint","IMPRINT",EDGE,{"derivedFrom":sQuery(id+"F7.wireOp",EDGE,"E5.23.26.0")}),1.0]])]});
            var Q33;
            Q33=makeQuery(id+"F7.imprint","IMPRINT",FACE,{"disambiguationData":[TD([[makeQuery(id+"F7.imprint","IMPRINT",EDGE,{"derivedFrom":sQuery(id+"F7.wireOp",EDGE,"E5.2.21.0")}),1.0]])]});
            var Q34;
            Q34=makeQuery(id+"F7.imprint","IMPRINT",FACE,{"disambiguationData":[TD([[makeQuery(id+"F7.imprint","IMPRINT",EDGE,{"derivedFrom":sQuery(id+"F7.wireOp",EDGE,"E5.18.6.0")}),1.0]])]});
            var Q35;
            Q35=makeQuery(id+"F7.imprint","IMPRINT",FACE,{"disambiguationData":[TD([[makeQuery(id+"F7.imprint","IMPRINT",EDGE,{"derivedFrom":sQuery(id+"F7.wireOp",EDGE,"E5.22.26.0")}),1.0]])]});
            var Q36;
            Q36=makeQuery(id+"F7.imprint","IMPRINT",FACE,{"disambiguationData":[TD([[makeQuery(id+"F7.imprint","IMPRINT",EDGE,{"derivedFrom":sQuery(id+"F7.wireOp",EDGE,"E5.22.10.0")}),1.0]])]});
            var Q37;
            Q37=makeQuery(id+"F7.imprint","IMPRINT",FACE,{"disambiguationData":[TD([[makeQuery(id+"F7.imprint","IMPRINT",EDGE,{"derivedFrom":sQuery(id+"F7.wireOp",EDGE,"E5.1.21.0")}),1.0]])]});
            var Q38;
            Q38=makeQuery(id+"F7.imprint","IMPRINT",FACE,{"disambiguationData":[TD([[makeQuery(id+"F7.imprint","IMPRINT",EDGE,{"derivedFrom":sQuery(id+"F7.wireOp",EDGE,"E5.1.5.0")}),1.0]])]});
            var Q39;
            Q39=makeQuery(id+"F7.imprint","IMPRINT",FACE,{"disambiguationData":[TD([[makeQuery(id+"F7.imprint","IMPRINT",EDGE,{"derivedFrom":sQuery(id+"F7.wireOp",EDGE,"E5.6.26.0")}),1.0]])]});
            var Q40;
            Q40=makeQuery(id+"F7.imprint","IMPRINT",FACE,{"disambiguationData":[TD([[makeQuery(id+"F7.imprint","IMPRINT",EDGE,{"derivedFrom":sQuery(id+"F7.wireOp",EDGE,"E5.27.16.0")}),1.0]])]});
            var Q41;
            Q41=makeQuery(id+"F7.imprint","IMPRINT",FACE,{"disambiguationData":[TD([[makeQuery(id+"F7.imprint","IMPRINT",EDGE,{"derivedFrom":sQuery(id+"F7.wireOp",EDGE,"E5.1.6.0")}),1.0]])]});
            var Q42;
            Q42=makeQuery(id+"F7.imprint","IMPRINT",FACE,{"disambiguationData":[TD([[makeQuery(id+"F7.imprint","IMPRINT",EDGE,{"derivedFrom":sQuery(id+"F7.wireOp",EDGE,"E5.22.11.0")}),1.0]])]});
            var Q43;
            Q43=makeQuery(id+"F7.imprint","IMPRINT",FACE,{"disambiguationData":[TD([[makeQuery(id+"F7.imprint","IMPRINT",EDGE,{"derivedFrom":sQuery(id+"F7.wireOp",EDGE,"E5.6.11.0")}),1.0]])]});
            var Q44;
            Q44=makeQuery(id+"F7.imprint","IMPRINT",FACE,{"disambiguationData":[TD([[makeQuery(id+"F7.imprint","IMPRINT",EDGE,{"derivedFrom":sQuery(id+"F7.wireOp",EDGE,"E5.5.26.0")}),1.0]])]});
            var Q45;
            Q45=makeQuery(id+"F7.imprint","IMPRINT",FACE,{"disambiguationData":[TD([[makeQuery(id+"F7.imprint","IMPRINT",EDGE,{"derivedFrom":sQuery(id+"F7.wireOp",EDGE,"E5.10.15.0")}),1.0]])]});
            var Q46;
            Q46=makeQuery(id+"F7.imprint","IMPRINT",FACE,{"disambiguationData":[TD([[makeQuery(id+"F7.imprint","IMPRINT",EDGE,{"derivedFrom":sQuery(id+"F7.wireOp",EDGE,"E5.31.21.0")}),1.0]])]});
            var Q47;
            Q47=makeQuery(id+"F7.imprint","IMPRINT",FACE,{"disambiguationData":[TD([[makeQuery(id+"F7.imprint","IMPRINT",EDGE,{"derivedFrom":sQuery(id+"F7.wireOp",EDGE,"E5.31.5.0")}),1.0]])]});
            var Q48;
            Q48=makeQuery(id+"F7.imprint","IMPRINT",FACE,{"disambiguationData":[TD([[makeQuery(id+"F7.imprint","IMPRINT",EDGE,{"derivedFrom":sQuery(id+"F7.wireOp",EDGE,"E5.26.16.0")}),1.0]])]});
            var Q49;
            Q49=makeQuery(id+"F7.imprint","IMPRINT",FACE,{"disambiguationData":[TD([[makeQuery(id+"F7.imprint","IMPRINT",EDGE,{"derivedFrom":sQuery(id+"F7.wireOp",EDGE,"E5.5.11.0")}),1.0]])]});
            var Q50;
            Q50=makeQuery(id+"F7.imprint","IMPRINT",FACE,{"disambiguationData":[TD([[makeQuery(id+"F7.imprint","IMPRINT",EDGE,{"derivedFrom":sQuery(id+"F7.wireOp",EDGE,"E5.10.16.0")}),1.0]])]});
            var Q51;
            Q51=makeQuery(id+"F7.imprint","IMPRINT",FACE,{"disambiguationData":[TD([[makeQuery(id+"F7.imprint","IMPRINT",EDGE,{"derivedFrom":sQuery(id+"F7.wireOp",EDGE,"E5.14.20.0")}),1.0]])]});
            var Q52;
            Q52=makeQuery(id+"F7.imprint","IMPRINT",FACE,{"disambiguationData":[TD([[makeQuery(id+"F7.imprint","IMPRINT",EDGE,{"derivedFrom":sQuery(id+"F7.wireOp",EDGE,"E5.30.21.0")}),1.0]])]});
            var Q53;
            Q53=makeQuery(id+"F7.imprint","IMPRINT",FACE,{"disambiguationData":[TD([[makeQuery(id+"F7.imprint","IMPRINT",EDGE,{"derivedFrom":sQuery(id+"F7.wireOp",EDGE,"E5.30.5.0")}),1.0]])]});
            var Q54;
            Q54=makeQuery(id+"F7.imprint","IMPRINT",FACE,{"disambiguationData":[TD([[makeQuery(id+"F7.imprint","IMPRINT",EDGE,{"derivedFrom":sQuery(id+"F7.wireOp",EDGE,"E5.31.6.0")}),1.0]])]});
            var Q55;
            Q55=makeQuery(id+"F7.imprint","IMPRINT",FACE,{"disambiguationData":[TD([[makeQuery(id+"F7.imprint","IMPRINT",EDGE,{"derivedFrom":sQuery(id+"F7.wireOp",EDGE,"E5.9.16.0")}),1.0]])]});
            var Q56;
            Q56=makeQuery(id+"F7.imprint","IMPRINT",FACE,{"disambiguationData":[TD([[makeQuery(id+"F7.imprint","IMPRINT",EDGE,{"derivedFrom":sQuery(id+"F7.wireOp",EDGE,"E5.10.1.0")}),1.0]])]});
            var Q57;
            Q57=makeQuery(id+"F7.imprint","IMPRINT",FACE,{"disambiguationData":[TD([[makeQuery(id+"F7.imprint","IMPRINT",EDGE,{"derivedFrom":sQuery(id+"F7.wireOp",EDGE,"E5.14.21.0")}),1.0]])]});
            var Q58;
            Q58=makeQuery(id+"F7.imprint","IMPRINT",FACE,{"disambiguationData":[TD([[makeQuery(id+"F7.imprint","IMPRINT",EDGE,{"derivedFrom":sQuery(id+"F7.wireOp",EDGE,"E5.14.5.0")}),1.0]])]});
            var Q59;
            Q59=makeQuery(id+"F7.imprint","IMPRINT",FACE,{"disambiguationData":[TD([[makeQuery(id+"F7.imprint","IMPRINT",EDGE,{"derivedFrom":sQuery(id+"F7.wireOp",EDGE,"E5.2.26.0")}),1.0]])]});
            var Q60;
            Q60=makeQuery(id+"F7.imprint","IMPRINT",FACE,{"disambiguationData":[TD([[makeQuery(id+"F7.imprint","IMPRINT",EDGE,{"derivedFrom":sQuery(id+"F7.wireOp",EDGE,"E5.14.6.0")}),1.0]])]});
            var Q61;
            Q61=makeQuery(id+"F7.imprint","IMPRINT",FACE,{"disambiguationData":[TD([[makeQuery(id+"F7.imprint","IMPRINT",EDGE,{"derivedFrom":sQuery(id+"F7.wireOp",EDGE,"E5.18.26.0")}),1.0]])]});
            var Q62;
            Q62=makeQuery(id+"F7.imprint","IMPRINT",FACE,{"disambiguationData":[TD([[makeQuery(id+"F7.imprint","IMPRINT",EDGE,{"derivedFrom":sQuery(id+"F7.wireOp",EDGE,"E5.18.10.0")}),1.0]])]});
            var Q63;
            Q63=makeQuery(id+"F7.imprint","IMPRINT",FACE,{"disambiguationData":[TD([[makeQuery(id+"F7.imprint","IMPRINT",EDGE,{"derivedFrom":sQuery(id+"F7.wireOp",EDGE,"E5.1.10.0")}),1.0]])]});
            var Q64;
            Q64=makeQuery(id+"F7.imprint","IMPRINT",FACE,{"disambiguationData":[TD([[makeQuery(id+"F7.imprint","IMPRINT",EDGE,{"derivedFrom":sQuery(id+"F7.wireOp",EDGE,"E5.1.26.0")}),1.0]])]});
            var Q65;
            Q65=makeQuery(id+"F7.imprint","IMPRINT",FACE,{"disambiguationData":[TD([[makeQuery(id+"F7.imprint","IMPRINT",EDGE,{"derivedFrom":sQuery(id+"F7.wireOp",EDGE,"E5.18.27.0")}),1.0]])]});
            var Q66;
            Q66=makeQuery(id+"F7.imprint","IMPRINT",FACE,{"disambiguationData":[TD([[makeQuery(id+"F7.imprint","IMPRINT",EDGE,{"derivedFrom":sQuery(id+"F7.wireOp",EDGE,"E5.18.11.0")}),1.0]])]});
            var Q67;
            Q67=makeQuery(id+"F7.imprint","IMPRINT",FACE,{"disambiguationData":[TD([[makeQuery(id+"F7.imprint","IMPRINT",EDGE,{"derivedFrom":sQuery(id+"F7.wireOp",EDGE,"E5.22.15.0")}),1.0]])]});
            var Q68;
            Q68=makeQuery(id+"F7.imprint","IMPRINT",FACE,{"disambiguationData":[TD([[makeQuery(id+"F7.imprint","IMPRINT",EDGE,{"derivedFrom":sQuery(id+"F7.wireOp",EDGE,"E5.23.16.0")}),1.0]])]});
            var Q69;
            Q69=makeQuery(id+"F7.imprint","IMPRINT",FACE,{"disambiguationData":[TD([[makeQuery(id+"F7.imprint","IMPRINT",EDGE,{"derivedFrom":sQuery(id+"F7.wireOp",EDGE,"E5.1.11.0")}),1.0]])]});
            var Q70;
            Q70=makeQuery(id+"F7.imprint","IMPRINT",FACE,{"disambiguationData":[TD([[makeQuery(id+"F7.imprint","IMPRINT",EDGE,{"derivedFrom":sQuery(id+"F7.wireOp",EDGE,"E5.6.16.0")}),1.0]])]});
            var Q71;
            Q71=makeQuery(id+"F7.imprint","IMPRINT",FACE,{"disambiguationData":[TD([[makeQuery(id+"F7.imprint","IMPRINT",EDGE,{"derivedFrom":sQuery(id+"F7.wireOp",EDGE,"E5.27.21.0")}),1.0]])]});
            var Q72;
            Q72=makeQuery(id+"F7.imprint","IMPRINT",FACE,{"disambiguationData":[TD([[makeQuery(id+"F7.imprint","IMPRINT",EDGE,{"derivedFrom":sQuery(id+"F7.wireOp",EDGE,"E5.27.5.0")}),1.0]])]});
            var Q73;
            Q73=makeQuery(id+"F7.imprint","IMPRINT",FACE,{"disambiguationData":[TD([[makeQuery(id+"F7.imprint","IMPRINT",EDGE,{"derivedFrom":sQuery(id+"F7.wireOp",EDGE,"E5.22.16.0")}),1.0]])]});
            var Q74;
            Q74=makeQuery(id+"F7.imprint","IMPRINT",FACE,{"disambiguationData":[TD([[makeQuery(id+"F7.imprint","IMPRINT",EDGE,{"derivedFrom":sQuery(id+"F7.wireOp",EDGE,"E5.5.16.0")}),1.0]])]});
            var Q75;
            Q75=makeQuery(id+"F7.imprint","IMPRINT",FACE,{"disambiguationData":[TD([[makeQuery(id+"F7.imprint","IMPRINT",EDGE,{"derivedFrom":sQuery(id+"F7.wireOp",EDGE,"E5.10.21.0")}),1.0]])]});
            var Q76;
            Q76=makeQuery(id+"F7.imprint","IMPRINT",FACE,{"disambiguationData":[TD([[makeQuery(id+"F7.imprint","IMPRINT",EDGE,{"derivedFrom":sQuery(id+"F7.wireOp",EDGE,"E5.10.5.0")}),1.0]])]});
            var Q77;
            Q77=makeQuery(id+"F7.imprint","IMPRINT",FACE,{"disambiguationData":[TD([[makeQuery(id+"F7.imprint","IMPRINT",EDGE,{"derivedFrom":sQuery(id+"F7.wireOp",EDGE,"E5.31.26.0")}),1.0]])]});
            var Q78;
            Q78=makeQuery(id+"F7.imprint","IMPRINT",FACE,{"disambiguationData":[TD([[makeQuery(id+"F7.imprint","IMPRINT",EDGE,{"derivedFrom":sQuery(id+"F7.wireOp",EDGE,"E5.31.10.0")}),1.0]])]});
            var Q79;
            Q79=makeQuery(id+"F7.imprint","IMPRINT",FACE,{"disambiguationData":[TD([[makeQuery(id+"F7.imprint","IMPRINT",EDGE,{"derivedFrom":sQuery(id+"F7.wireOp",EDGE,"E5.22.1.0")}),1.0]])]});
            var Q80;
            Q80=makeQuery(id+"F7.imprint","IMPRINT",FACE,{"disambiguationData":[TD([[makeQuery(id+"F7.imprint","IMPRINT",EDGE,{"derivedFrom":sQuery(id+"F7.wireOp",EDGE,"E5.26.21.0")}),1.0]])]});
            var Q81;
            Q81=makeQuery(id+"F7.imprint","IMPRINT",FACE,{"disambiguationData":[TD([[makeQuery(id+"F7.imprint","IMPRINT",EDGE,{"derivedFrom":sQuery(id+"F7.wireOp",EDGE,"E5.26.5.0")}),1.0]])]});
            var Q82;
            Q82=makeQuery(id+"F7.imprint","IMPRINT",FACE,{"disambiguationData":[TD([[makeQuery(id+"F7.imprint","IMPRINT",EDGE,{"derivedFrom":sQuery(id+"F7.wireOp",EDGE,"E5.9.21.0")}),1.0]])]});
            var Q83;
            Q83=makeQuery(id+"F7.imprint","IMPRINT",FACE,{"disambiguationData":[TD([[makeQuery(id+"F7.imprint","IMPRINT",EDGE,{"derivedFrom":sQuery(id+"F7.wireOp",EDGE,"E5.10.6.0")}),1.0]])]});
            var Q84;
            Q84=makeQuery(id+"F7.imprint","IMPRINT",FACE,{"disambiguationData":[TD([[makeQuery(id+"F7.imprint","IMPRINT",EDGE,{"derivedFrom":sQuery(id+"F7.wireOp",EDGE,"E5.14.26.0")}),1.0]])]});
            var Q85;
            Q85=makeQuery(id+"F7.imprint","IMPRINT",FACE,{"disambiguationData":[TD([[makeQuery(id+"F7.imprint","IMPRINT",EDGE,{"derivedFrom":sQuery(id+"F7.wireOp",EDGE,"E5.14.10.0")}),1.0]])]});
            var Q86;
            Q86=makeQuery(id+"F7.imprint","IMPRINT",FACE,{"disambiguationData":[TD([[makeQuery(id+"F7.imprint","IMPRINT",EDGE,{"derivedFrom":sQuery(id+"F7.wireOp",EDGE,"E5.30.26.0")}),1.0]])]});
            var Q87;
            Q87=makeQuery(id+"F7.imprint","IMPRINT",FACE,{"disambiguationData":[TD([[makeQuery(id+"F7.imprint","IMPRINT",EDGE,{"derivedFrom":sQuery(id+"F7.wireOp",EDGE,"E5.31.11.0")}),1.0]])]});
            var Q88;
            Q88=makeQuery(id+"F7.imprint","IMPRINT",FACE,{"disambiguationData":[TD([[makeQuery(id+"F7.imprint","IMPRINT",EDGE,{"derivedFrom":sQuery(id+"F7.wireOp",EDGE,"E5.14.27.0")}),1.0]])]});
            var Q89;
            Q89=makeQuery(id+"F7.imprint","IMPRINT",FACE,{"disambiguationData":[TD([[makeQuery(id+"F7.imprint","IMPRINT",EDGE,{"derivedFrom":sQuery(id+"F7.wireOp",EDGE,"E5.14.11.0")}),1.0]])]});
            var Q90;
            Q90=makeQuery(id+"F7.imprint","IMPRINT",FACE,{"disambiguationData":[TD([[makeQuery(id+"F7.imprint","IMPRINT",EDGE,{"derivedFrom":sQuery(id+"F7.wireOp",EDGE,"E5.18.15.0")}),1.0]])]});
            var Q91;
            Q91=makeQuery(id+"F7.imprint","IMPRINT",FACE,{"disambiguationData":[TD([[makeQuery(id+"F7.imprint","IMPRINT",EDGE,{"derivedFrom":sQuery(id+"F7.wireOp",EDGE,"E5.30.11.0")}),1.0]])]});
            var Q92;
            Q92=makeQuery(id+"F7.imprint","IMPRINT",FACE,{"disambiguationData":[TD([[makeQuery(id+"F7.imprint","IMPRINT",EDGE,{"derivedFrom":sQuery(id+"F7.wireOp",EDGE,"E5.31.13.0")}),1.0]])]});
            var Q93;
            Q93=makeQuery(id+"F7.imprint","IMPRINT",FACE,{"disambiguationData":[TD([[makeQuery(id+"F7.imprint","IMPRINT",EDGE,{"derivedFrom":sQuery(id+"F7.wireOp",EDGE,"E5.29.27.0")}),1.0]])]});
            var Q94;
            Q94=makeQuery(id+"F7.imprint","IMPRINT",FACE,{"disambiguationData":[TD([[makeQuery(id+"F7.imprint","IMPRINT",EDGE,{"derivedFrom":sQuery(id+"F7.wireOp",EDGE,"E5.15.29.0")}),1.0]])]});
            var Q95;
            Q95=makeQuery(id+"F7.imprint","IMPRINT",FACE,{"disambiguationData":[TD([[makeQuery(id+"F7.imprint","IMPRINT",EDGE,{"derivedFrom":sQuery(id+"F7.wireOp",EDGE,"E5.27.25.0")}),1.0]])]});
            var Q96;
            Q96=makeQuery(id+"F7.imprint","IMPRINT",FACE,{"disambiguationData":[TD([[makeQuery(id+"F7.imprint","IMPRINT",EDGE,{"derivedFrom":sQuery(id+"F7.wireOp",EDGE,"E5.28.10.0")}),1.0]])]});
            var Q97;
            Q97=makeQuery(id+"F7.imprint","IMPRINT",FACE,{"disambiguationData":[TD([[makeQuery(id+"F7.imprint","IMPRINT",EDGE,{"derivedFrom":sQuery(id+"F7.wireOp",EDGE,"E5.28.26.0")}),1.0]])]});
            var Q98;
            Q98=makeQuery(id+"F7.imprint","IMPRINT",FACE,{"disambiguationData":[TD([[makeQuery(id+"F7.imprint","IMPRINT",EDGE,{"derivedFrom":sQuery(id+"F7.wireOp",EDGE,"E5.30.12.0")}),1.0]])]});
            var Q99;
            Q99=makeQuery(id+"F7.imprint","IMPRINT",FACE,{"disambiguationData":[TD([[makeQuery(id+"F7.imprint","IMPRINT",EDGE,{"derivedFrom":sQuery(id+"F7.wireOp",EDGE,"E5.17.15.0")}),1.0]])]});
            var Q100;
            Q100=makeQuery(id+"F7.imprint","IMPRINT",FACE,{"disambiguationData":[TD([[makeQuery(id+"F7.imprint","IMPRINT",EDGE,{"derivedFrom":sQuery(id+"F7.wireOp",EDGE,"E5.23.5.0")}),1.0]])]});
            var Q101;
            Q101=makeQuery(id+"F7.imprint","IMPRINT",FACE,{"disambiguationData":[TD([[makeQuery(id+"F7.imprint","IMPRINT",EDGE,{"derivedFrom":sQuery(id+"F7.wireOp",EDGE,"E5.31.29.0")}),1.0]])]});
            var Q102;
            Q102=makeQuery(id+"F7.imprint","IMPRINT",FACE,{"disambiguationData":[TD([[makeQuery(id+"F7.imprint","IMPRINT",EDGE,{"derivedFrom":sQuery(id+"F7.wireOp",EDGE,"E5.19.17.0")}),1.0]])]});
            var Q103;
            Q103=makeQuery(id+"F7.imprint","IMPRINT",FACE,{"disambiguationData":[TD([[makeQuery(id+"F7.imprint","IMPRINT",EDGE,{"derivedFrom":sQuery(id+"F7.wireOp",EDGE,"E5.27.9.0")}),1.0]])]});
            var Q104;
            Q104=makeQuery(id+"F7.imprint","IMPRINT",FACE,{"disambiguationData":[TD([[makeQuery(id+"F7.imprint","IMPRINT",EDGE,{"derivedFrom":sQuery(id+"F7.wireOp",EDGE,"E5.29.11.0")}),1.0]])]});
            var Q105;
            Q105=makeQuery(id+"F7.imprint","IMPRINT",FACE,{"disambiguationData":[TD([[makeQuery(id+"F7.imprint","IMPRINT",EDGE,{"derivedFrom":sQuery(id+"F7.wireOp",EDGE,"E5.20.2.0")}),1.0]])]});
            var Q106;
            Q106=makeQuery(id+"F7.imprint","IMPRINT",FACE,{"disambiguationData":[TD([[makeQuery(id+"F7.imprint","IMPRINT",EDGE,{"derivedFrom":sQuery(id+"F7.wireOp",EDGE,"E5.30.28.0")}),1.0]])]});
            var Q107;
            Q107=makeQuery(id+"F7.imprint","IMPRINT",FACE,{"disambiguationData":[TD([[makeQuery(id+"F7.imprint","IMPRINT",EDGE,{"derivedFrom":sQuery(id+"F7.wireOp",EDGE,"E5.21.19.0")}),1.0]])]});
            var Q108;
            Q108=makeQuery(id+"F7.imprint","IMPRINT",FACE,{"disambiguationData":[TD([[makeQuery(id+"F7.imprint","IMPRINT",EDGE,{"derivedFrom":sQuery(id+"F7.wireOp",EDGE,"E5.19.1.0")}),1.0]])]});
            var Q109;
            Q109=makeQuery(id+"F7.imprint","IMPRINT",FACE,{"disambiguationData":[TD([[makeQuery(id+"F7.imprint","IMPRINT",EDGE,{"derivedFrom":sQuery(id+"F7.wireOp",EDGE,"E5.22.20.0")}),1.0]])]});
            var Q110;
            Q110=makeQuery(id+"F7.imprint","IMPRINT",FACE,{"disambiguationData":[TD([[makeQuery(id+"F7.imprint","IMPRINT",EDGE,{"derivedFrom":sQuery(id+"F7.wireOp",EDGE,"E5.21.3.0")}),1.0]])]});
            var Q111;
            Q111=makeQuery(id+"F7.imprint","IMPRINT",FACE,{"disambiguationData":[TD([[makeQuery(id+"F7.imprint","IMPRINT",EDGE,{"derivedFrom":sQuery(id+"F7.wireOp",EDGE,"E5.16.14.0")}),1.0]])]});
            var Q112;
            Q112=makeQuery(id+"F7.imprint","IMPRINT",FACE,{"disambiguationData":[TD([[makeQuery(id+"F7.imprint","IMPRINT",EDGE,{"derivedFrom":sQuery(id+"F7.wireOp",EDGE,"E5.20.18.0")}),1.0]])]});
            var Q113;
            Q113=makeQuery(id+"F7.imprint","IMPRINT",FACE,{"disambiguationData":[TD([[makeQuery(id+"F7.imprint","IMPRINT",EDGE,{"derivedFrom":sQuery(id+"F7.wireOp",EDGE,"E5.32.14.0")}),1.0]])]});
            var Q114;
            Q114=makeQuery(id+"F7.imprint","IMPRINT",FACE,{"disambiguationData":[TD([[makeQuery(id+"F7.imprint","IMPRINT",EDGE,{"derivedFrom":sQuery(id+"F7.wireOp",EDGE,"E5.24.24.0")}),1.0]])]});
            var Q115;
            Q115=makeQuery(id+"F7.imprint","IMPRINT",FACE,{"disambiguationData":[TD([[makeQuery(id+"F7.imprint","IMPRINT",EDGE,{"derivedFrom":sQuery(id+"F7.wireOp",EDGE,"E5.25.9.0")}),1.0]])]});
            var Q116;
            Q116=makeQuery(id+"F7.imprint","IMPRINT",FACE,{"disambiguationData":[TD([[makeQuery(id+"F7.imprint","IMPRINT",EDGE,{"derivedFrom":sQuery(id+"F7.wireOp",EDGE,"E5.25.25.0")}),1.0]])]});
            var Q117;
            Q117=makeQuery(id+"F7.imprint","IMPRINT",FACE,{"disambiguationData":[TD([[makeQuery(id+"F7.imprint","IMPRINT",EDGE,{"derivedFrom":sQuery(id+"F7.wireOp",EDGE,"E5.22.22.0")}),1.0]])]});
            var Q118;
            Q118=makeQuery(id+"F7.imprint","IMPRINT",FACE,{"disambiguationData":[TD([[makeQuery(id+"F7.imprint","IMPRINT",EDGE,{"derivedFrom":sQuery(id+"F7.wireOp",EDGE,"E5.26.10.0")}),1.0]])]});
            var Q119;
            Q119=makeQuery(id+"F7.imprint","IMPRINT",FACE,{"disambiguationData":[TD([[makeQuery(id+"F7.imprint","IMPRINT",EDGE,{"derivedFrom":sQuery(id+"F7.wireOp",EDGE,"E5.23.7.0")}),1.0]])]});
            var Q120;
            Q120=makeQuery(id+"F7.imprint","IMPRINT",FACE,{"disambiguationData":[TD([[makeQuery(id+"F7.imprint","IMPRINT",EDGE,{"derivedFrom":sQuery(id+"F7.wireOp",EDGE,"E5.24.8.0")}),1.0]])]});
            var Q121;
            Q121=makeQuery(id+"F7.imprint","IMPRINT",FACE,{"disambiguationData":[TD([[makeQuery(id+"F7.imprint","IMPRINT",EDGE,{"derivedFrom":sQuery(id+"F7.wireOp",EDGE,"E5.23.23.0")}),1.0]])]});
            var Q122;
            Q122=makeQuery(id+"F7.imprint","IMPRINT",FACE,{"disambiguationData":[TD([[makeQuery(id+"F7.imprint","IMPRINT",EDGE,{"derivedFrom":sQuery(id+"F7.wireOp",EDGE,"E5.20.20.0")}),1.0]])]});
            var Q123;
            Q123=makeQuery(id+"F7.imprint","IMPRINT",FACE,{"disambiguationData":[TD([[makeQuery(id+"F7.imprint","IMPRINT",EDGE,{"derivedFrom":sQuery(id+"F7.wireOp",EDGE,"E5.21.5.0")}),1.0]])]});
            var Q124;
            Q124=makeQuery(id+"F7.imprint","IMPRINT",FACE,{"disambiguationData":[TD([[makeQuery(id+"F7.imprint","IMPRINT",EDGE,{"derivedFrom":sQuery(id+"F7.wireOp",EDGE,"E5.21.21.0")}),1.0]])]});
            var Q125;
            Q125=makeQuery(id+"F7.imprint","IMPRINT",FACE,{"disambiguationData":[TD([[makeQuery(id+"F7.imprint","IMPRINT",EDGE,{"derivedFrom":sQuery(id+"F7.wireOp",EDGE,"E5.18.18.0")}),1.0]])]});
            var Q126;
            Q126=makeQuery(id+"F7.imprint","IMPRINT",FACE,{"disambiguationData":[TD([[makeQuery(id+"F7.imprint","IMPRINT",EDGE,{"derivedFrom":sQuery(id+"F7.wireOp",EDGE,"E5.19.3.0")}),1.0]])]});
            var Q127;
            Q127=makeQuery(id+"F7.imprint","IMPRINT",FACE,{"disambiguationData":[TD([[makeQuery(id+"F7.imprint","IMPRINT",EDGE,{"derivedFrom":sQuery(id+"F7.wireOp",EDGE,"E5.19.19.0")}),1.0]])]});
            var Q128;
            Q128=makeQuery(id+"F7.imprint","IMPRINT",FACE,{"disambiguationData":[TD([[makeQuery(id+"F7.imprint","IMPRINT",EDGE,{"derivedFrom":sQuery(id+"F7.wireOp",EDGE,"E5.20.4.0")}),1.0]])]});
            var Q129;
            Q129=makeQuery(id+"F7.imprint","IMPRINT",FACE,{"disambiguationData":[TD([[makeQuery(id+"F7.imprint","IMPRINT",EDGE,{"derivedFrom":sQuery(id+"F7.wireOp",EDGE,"E5.16.16.0")}),1.0]])]});
            var Q130;
            Q130=makeQuery(id+"F7.imprint","IMPRINT",FACE,{"disambiguationData":[TD([[makeQuery(id+"F7.imprint","IMPRINT",EDGE,{"derivedFrom":sQuery(id+"F7.wireOp",EDGE,"E5.17.1.0")}),1.0]])]});
            var Q131;
            Q131=makeQuery(id+"F7.imprint","IMPRINT",FACE,{"disambiguationData":[TD([[makeQuery(id+"F7.imprint","IMPRINT",EDGE,{"derivedFrom":sQuery(id+"F7.wireOp",EDGE,"E5.17.17.0")}),1.0]])]});
            var Q132;
            Q132=makeQuery(id+"F7.imprint","IMPRINT",FACE,{"disambiguationData":[TD([[makeQuery(id+"F7.imprint","IMPRINT",EDGE,{"derivedFrom":sQuery(id+"F7.wireOp",EDGE,"E5.18.2.0")}),1.0]])]});
            var Q133;
            Q133=makeQuery(id+"F7.imprint","IMPRINT",FACE,{"disambiguationData":[TD([[makeQuery(id+"F7.imprint","IMPRINT",EDGE,{"derivedFrom":sQuery(id+"F7.wireOp",EDGE,"E5.14.14.0")}),1.0]])]});
            var Q134;
            Q134=makeQuery(id+"F7.imprint","IMPRINT",FACE,{"disambiguationData":[TD([[makeQuery(id+"F7.imprint","IMPRINT",EDGE,{"derivedFrom":sQuery(id+"F7.wireOp",EDGE,"E5.15.15.0")}),1.0]])]});
            var Q135;
            Q135=makeQuery(id+"F7.imprint","IMPRINT",FACE,{"disambiguationData":[TD([[makeQuery(id+"F7.imprint","IMPRINT",EDGE,{"derivedFrom":sQuery(id+"F7.wireOp",EDGE,"E5.13.29.0")}),1.0]])]});
            var Q136;
            Q136=makeQuery(id+"F7.imprint","IMPRINT",FACE,{"disambiguationData":[TD([[makeQuery(id+"F7.imprint","IMPRINT",EDGE,{"derivedFrom":sQuery(id+"F7.wireOp",EDGE,"E5.30.14.0")}),1.0]])]});
            var Q137;
            Q137=makeQuery(id+"F7.imprint","IMPRINT",FACE,{"disambiguationData":[TD([[makeQuery(id+"F7.imprint","IMPRINT",EDGE,{"derivedFrom":sQuery(id+"F7.wireOp",EDGE,"E5.28.12.0")}),1.0]])]});
            var Q138;
            Q138=makeQuery(id+"F7.imprint","IMPRINT",FACE,{"disambiguationData":[TD([[makeQuery(id+"F7.imprint","IMPRINT",EDGE,{"derivedFrom":sQuery(id+"F7.wireOp",EDGE,"E5.28.28.0")}),1.0]])]});
            var Q139;
            Q139=makeQuery(id+"F7.imprint","IMPRINT",FACE,{"disambiguationData":[TD([[makeQuery(id+"F7.imprint","IMPRINT",EDGE,{"derivedFrom":sQuery(id+"F7.wireOp",EDGE,"E5.29.13.0")}),1.0]])]});
            var Q140;
            Q140=makeQuery(id+"F7.imprint","IMPRINT",FACE,{"disambiguationData":[TD([[makeQuery(id+"F7.imprint","IMPRINT",EDGE,{"derivedFrom":sQuery(id+"F7.wireOp",EDGE,"E5.29.29.0")}),1.0]])]});
            var Q141;
            Q141=makeQuery(id+"F7.imprint","IMPRINT",FACE,{"disambiguationData":[TD([[makeQuery(id+"F7.imprint","IMPRINT",EDGE,{"derivedFrom":sQuery(id+"F7.wireOp",EDGE,"E5.33.1.0")}),1.0]])]});
            var Q142;
            Q142=makeQuery(id+"F7.imprint","IMPRINT",FACE,{"disambiguationData":[TD([[makeQuery(id+"F7.imprint","IMPRINT",EDGE,{"derivedFrom":sQuery(id+"F7.wireOp",EDGE,"E5.27.27.0")}),1.0]])]});
            var Q143;
            Q143=makeQuery(id+"F7.imprint","IMPRINT",FACE,{"disambiguationData":[TD([[makeQuery(id+"F7.imprint","IMPRINT",EDGE,{"derivedFrom":sQuery(id+"F7.wireOp",EDGE,"E5.32.16.0")}),1.0]])]});
            var Q144;
            Q144=makeQuery(id+"F7.imprint","IMPRINT",FACE,{"disambiguationData":[TD([[makeQuery(id+"F7.imprint","IMPRINT",EDGE,{"derivedFrom":sQuery(id+"F7.wireOp",EDGE,"E5.13.13.0")}),1.0]])]});
            var Q145;
            Q145=makeQuery(id+"F7.imprint","IMPRINT",FACE,{"disambiguationData":[TD([[makeQuery(id+"F7.imprint","IMPRINT",EDGE,{"derivedFrom":sQuery(id+"F7.wireOp",EDGE,"E5.11.11.0")}),1.0]])]});
            var Q146;
            Q146=makeQuery(id+"F7.imprint","IMPRINT",FACE,{"disambiguationData":[TD([[makeQuery(id+"F7.imprint","IMPRINT",EDGE,{"derivedFrom":sQuery(id+"F7.wireOp",EDGE,"E5.11.27.0")}),1.0]])]});
            var Q147;
            Q147=makeQuery(id+"F7.imprint","IMPRINT",FACE,{"disambiguationData":[TD([[makeQuery(id+"F7.imprint","IMPRINT",EDGE,{"derivedFrom":sQuery(id+"F7.wireOp",EDGE,"E5.12.12.0")}),1.0]])]});
            var Q148;
            Q148=makeQuery(id+"F7.imprint","IMPRINT",FACE,{"disambiguationData":[TD([[makeQuery(id+"F7.imprint","IMPRINT",EDGE,{"derivedFrom":sQuery(id+"F7.wireOp",EDGE,"E5.12.28.0")}),1.0]])]});
            var Q149;
            Q149=makeQuery(id+"F7.imprint","IMPRINT",FACE,{"disambiguationData":[TD([[makeQuery(id+"F7.imprint","IMPRINT",EDGE,{"derivedFrom":sQuery(id+"F7.wireOp",EDGE,"E5.9.9.0")}),1.0]])]});
            var Q150;
            Q150=makeQuery(id+"F7.imprint","IMPRINT",FACE,{"disambiguationData":[TD([[makeQuery(id+"F7.imprint","IMPRINT",EDGE,{"derivedFrom":sQuery(id+"F7.wireOp",EDGE,"E5.9.25.0")}),1.0]])]});
            var Q151;
            Q151=makeQuery(id+"F7.imprint","IMPRINT",FACE,{"disambiguationData":[TD([[makeQuery(id+"F7.imprint","IMPRINT",EDGE,{"derivedFrom":sQuery(id+"F7.wireOp",EDGE,"E5.7.7.0")}),1.0]])]});
            var Q152;
            Q152=makeQuery(id+"F7.imprint","IMPRINT",FACE,{"disambiguationData":[TD([[makeQuery(id+"F7.imprint","IMPRINT",EDGE,{"derivedFrom":sQuery(id+"F7.wireOp",EDGE,"E5.7.23.0")}),1.0]])]});
            var Q153;
            Q153=makeQuery(id+"F7.imprint","IMPRINT",FACE,{"disambiguationData":[TD([[makeQuery(id+"F7.imprint","IMPRINT",EDGE,{"derivedFrom":sQuery(id+"F7.wireOp",EDGE,"E5.8.8.0")}),1.0]])]});
            var Q154;
            Q154=makeQuery(id+"F7.imprint","IMPRINT",FACE,{"disambiguationData":[TD([[makeQuery(id+"F7.imprint","IMPRINT",EDGE,{"derivedFrom":sQuery(id+"F7.wireOp",EDGE,"E5.8.24.0")}),1.0]])]});
            var Q155;
            Q155=makeQuery(id+"F7.imprint","IMPRINT",FACE,{"disambiguationData":[TD([[makeQuery(id+"F7.imprint","IMPRINT",EDGE,{"derivedFrom":sQuery(id+"F7.wireOp",EDGE,"E5.6.6.0")}),1.0]])]});
            var Q156;
            Q156=makeQuery(id+"F7.imprint","IMPRINT",FACE,{"disambiguationData":[TD([[makeQuery(id+"F7.imprint","IMPRINT",EDGE,{"derivedFrom":sQuery(id+"F7.wireOp",EDGE,"E5.6.22.0")}),1.0]])]});
            var Q157;
            Q157=makeQuery(id+"F7.imprint","IMPRINT",FACE,{"disambiguationData":[TD([[makeQuery(id+"F7.imprint","IMPRINT",EDGE,{"derivedFrom":sQuery(id+"F7.wireOp",EDGE,"E5.3.3.0")}),1.0]])]});
            var Q158;
            Q158=makeQuery(id+"F7.imprint","IMPRINT",FACE,{"disambiguationData":[TD([[makeQuery(id+"F7.imprint","IMPRINT",EDGE,{"derivedFrom":sQuery(id+"F7.wireOp",EDGE,"E5.3.19.0")}),1.0]])]});
            var Q159;
            Q159=makeQuery(id+"F7.imprint","IMPRINT",FACE,{"disambiguationData":[TD([[makeQuery(id+"F7.imprint","IMPRINT",EDGE,{"derivedFrom":sQuery(id+"F7.wireOp",EDGE,"E5.4.4.0")}),1.0]])]});
            var Q160;
            Q160=makeQuery(id+"F7.imprint","IMPRINT",FACE,{"disambiguationData":[TD([[makeQuery(id+"F7.imprint","IMPRINT",EDGE,{"derivedFrom":sQuery(id+"F7.wireOp",EDGE,"E5.4.20.0")}),1.0]])]});
            var Q161;
            Q161=makeQuery(id+"F7.imprint","IMPRINT",FACE,{"disambiguationData":[TD([[makeQuery(id+"F7.imprint","IMPRINT",EDGE,{"derivedFrom":sQuery(id+"F7.wireOp",EDGE,"E5.1.17.0")}),1.0]])]});
            var Q162;
            Q162=makeQuery(id+"F7.imprint","IMPRINT",FACE,{"disambiguationData":[TD([[makeQuery(id+"F7.imprint","IMPRINT",EDGE,{"derivedFrom":sQuery(id+"F7.wireOp",EDGE,"E5.2.2.0")}),1.0]])]});
            var Q163;
            Q163=makeQuery(id+"F7.imprint","IMPRINT",FACE,{"disambiguationData":[TD([[makeQuery(id+"F7.imprint","IMPRINT",EDGE,{"derivedFrom":sQuery(id+"F7.wireOp",EDGE,"E5.2.18.0")}),1.0]])]});
            var Q164;
            Q164=makeQuery(id+"F7.imprint","IMPRINT",FACE,{"disambiguationData":[TD([[makeQuery(id+"F7.imprint","IMPRINT",EDGE,{"derivedFrom":sQuery(id+"F7.wireOp",EDGE,"E5.33.17.0")}),1.0]])]});
            var Q165;
            Q165=makeQuery(id+"F7.imprint","IMPRINT",FACE,{"disambiguationData":[TD([[makeQuery(id+"F7.imprint","IMPRINT",EDGE,{"derivedFrom":sQuery(id+"F7.wireOp",EDGE,"E5.33.4.0")}),1.0]])]});
            var Q166;
            Q166=makeQuery(id+"F7.imprint","IMPRINT",FACE,{"disambiguationData":[TD([[makeQuery(id+"F7.imprint","IMPRINT",EDGE,{"derivedFrom":sQuery(id+"F7.wireOp",EDGE,"E5.33.20.0")}),1.0]])]});
            var Q167;
            Q167=makeQuery(id+"F7.imprint","IMPRINT",FACE,{"disambiguationData":[TD([[makeQuery(id+"F7.imprint","IMPRINT",EDGE,{"derivedFrom":sQuery(id+"F7.wireOp",EDGE,"E5.33.27.0")}),1.0]])]});
            var Q168;
            Q168=makeQuery(id+"F7.imprint","IMPRINT",FACE,{"disambiguationData":[TD([[makeQuery(id+"F7.imprint","IMPRINT",EDGE,{"derivedFrom":sQuery(id+"F7.wireOp",EDGE,"E5.33.11.0")}),1.0]])]});
            var Q169;
            Q169=makeQuery(id+"F7.imprint","IMPRINT",FACE,{"disambiguationData":[TD([[makeQuery(id+"F7.imprint","IMPRINT",EDGE,{"derivedFrom":sQuery(id+"F7.wireOp",EDGE,"E5.33.7.0")}),1.0]])]});
            var Q170;
            Q170=makeQuery(id+"F7.imprint","IMPRINT",FACE,{"disambiguationData":[TD([[makeQuery(id+"F7.imprint","IMPRINT",EDGE,{"derivedFrom":sQuery(id+"F7.wireOp",EDGE,"E5.33.23.0")}),1.0]])]});
            var Q171;
            Q171=makeQuery(id+"F7.imprint","IMPRINT",FACE,{"disambiguationData":[TD([[makeQuery(id+"F7.imprint","IMPRINT",EDGE,{"derivedFrom":sQuery(id+"F7.wireOp",EDGE,"E5.33.14.0")}),1.0]])]});
            var Q172;
            Q172=makeQuery(id+"F7.imprint","IMPRINT",FACE,{"disambiguationData":[TD([[makeQuery(id+"F7.imprint","IMPRINT",EDGE,{"derivedFrom":sQuery(id+"F7.wireOp",EDGE,"E5.33.19.0")}),1.0]])]});
            var Q173;
            Q173=makeQuery(id+"F7.imprint","IMPRINT",FACE,{"disambiguationData":[TD([[makeQuery(id+"F7.imprint","IMPRINT",EDGE,{"derivedFrom":sQuery(id+"F7.wireOp",EDGE,"E5.33.3.0")}),1.0]])]});
            var Q174;
            Q174=makeQuery(id+"F7.imprint","IMPRINT",FACE,{"disambiguationData":[TD([[makeQuery(id+"F7.imprint","IMPRINT",EDGE,{"derivedFrom":sQuery(id+"F7.wireOp",EDGE,"E5.33.16.0")}),1.0]])]});
            var Q175;
            Q175=makeQuery(id+"F7.imprint","IMPRINT",FACE,{"disambiguationData":[TD([[makeQuery(id+"F7.imprint","IMPRINT",EDGE,{"derivedFrom":sQuery(id+"F7.wireOp",EDGE,"E5.33.10.0")}),1.0]])]});
            var Q176;
            Q176=makeQuery(id+"F7.imprint","IMPRINT",FACE,{"disambiguationData":[TD([[makeQuery(id+"F7.imprint","IMPRINT",EDGE,{"derivedFrom":sQuery(id+"F7.wireOp",EDGE,"E5.33.26.0")}),1.0]])]});
            var Q177;
            Q177=makeQuery(id+"F7.imprint","IMPRINT",FACE,{"disambiguationData":[TD([[makeQuery(id+"F7.imprint","IMPRINT",EDGE,{"derivedFrom":sQuery(id+"F7.wireOp",EDGE,"E5.5.19.0")}),1.0]])]});
            var Q178;
            Q178=makeQuery(id+"F7.imprint","IMPRINT",FACE,{"disambiguationData":[TD([[makeQuery(id+"F7.imprint","IMPRINT",EDGE,{"derivedFrom":sQuery(id+"F7.wireOp",EDGE,"E5.3.1.0")}),1.0]])]});
            var Q179;
            Q179=makeQuery(id+"F7.imprint","IMPRINT",FACE,{"disambiguationData":[TD([[makeQuery(id+"F7.imprint","IMPRINT",EDGE,{"derivedFrom":sQuery(id+"F7.wireOp",EDGE,"E5.3.17.0")}),1.0]])]});
            var Q180;
            Q180=makeQuery(id+"F7.imprint","IMPRINT",FACE,{"disambiguationData":[TD([[makeQuery(id+"F7.imprint","IMPRINT",EDGE,{"derivedFrom":sQuery(id+"F7.wireOp",EDGE,"E5.24.22.0")}),1.0]])]});
            var Q181;
            Q181=makeQuery(id+"F7.imprint","IMPRINT",FACE,{"disambiguationData":[TD([[makeQuery(id+"F7.imprint","IMPRINT",EDGE,{"derivedFrom":sQuery(id+"F7.wireOp",EDGE,"E5.25.7.0")}),1.0]])]});
            var Q182;
            Q182=makeQuery(id+"F7.imprint","IMPRINT",FACE,{"disambiguationData":[TD([[makeQuery(id+"F7.imprint","IMPRINT",EDGE,{"derivedFrom":sQuery(id+"F7.wireOp",EDGE,"E5.25.23.0")}),1.0]])]});
            var Q183;
            Q183=makeQuery(id+"F7.imprint","IMPRINT",FACE,{"disambiguationData":[TD([[makeQuery(id+"F7.imprint","IMPRINT",EDGE,{"derivedFrom":sQuery(id+"F7.wireOp",EDGE,"E5.22.4.0")}),1.0]])]});
            var Q184;
            Q184=makeQuery(id+"F7.imprint","IMPRINT",FACE,{"disambiguationData":[TD([[makeQuery(id+"F7.imprint","IMPRINT",EDGE,{"derivedFrom":sQuery(id+"F7.wireOp",EDGE,"E5.12.10.0")}),1.0]])]});
            var Q185;
            Q185=makeQuery(id+"F7.imprint","IMPRINT",FACE,{"disambiguationData":[TD([[makeQuery(id+"F7.imprint","IMPRINT",EDGE,{"derivedFrom":sQuery(id+"F7.wireOp",EDGE,"E5.24.6.0")}),1.0]])]});
            var Q186;
            Q186=makeQuery(id+"F7.imprint","IMPRINT",FACE,{"disambiguationData":[TD([[makeQuery(id+"F7.imprint","IMPRINT",EDGE,{"derivedFrom":sQuery(id+"F7.wireOp",EDGE,"E5.11.25.0")}),1.0]])]});
            var Q187;
            Q187=makeQuery(id+"F7.imprint","IMPRINT",FACE,{"disambiguationData":[TD([[makeQuery(id+"F7.imprint","IMPRINT",EDGE,{"derivedFrom":sQuery(id+"F7.wireOp",EDGE,"E5.9.7.0")}),1.0]])]});
            var Q188;
            Q188=makeQuery(id+"F7.imprint","IMPRINT",FACE,{"disambiguationData":[TD([[makeQuery(id+"F7.imprint","IMPRINT",EDGE,{"derivedFrom":sQuery(id+"F7.wireOp",EDGE,"E5.9.23.0")}),1.0]])]});
            var Q189;
            Q189=makeQuery(id+"F7.imprint","IMPRINT",FACE,{"disambiguationData":[TD([[makeQuery(id+"F7.imprint","IMPRINT",EDGE,{"derivedFrom":sQuery(id+"F7.wireOp",EDGE,"E5.6.20.0")}),1.0]])]});
            var Q190;
            Q190=makeQuery(id+"F7.imprint","IMPRINT",FACE,{"disambiguationData":[TD([[makeQuery(id+"F7.imprint","IMPRINT",EDGE,{"derivedFrom":sQuery(id+"F7.wireOp",EDGE,"E5.10.8.0")}),1.0]])]});
            var Q191;
            Q191=makeQuery(id+"F7.imprint","IMPRINT",FACE,{"disambiguationData":[TD([[makeQuery(id+"F7.imprint","IMPRINT",EDGE,{"derivedFrom":sQuery(id+"F7.wireOp",EDGE,"E5.5.3.0")}),1.0]])]});
            var Q192;
            Q192=makeQuery(id+"F7.imprint","IMPRINT",FACE,{"disambiguationData":[TD([[makeQuery(id+"F7.imprint","IMPRINT",EDGE,{"derivedFrom":sQuery(id+"F7.wireOp",EDGE,"E5.8.6.0")}),1.0]])]});
            var Q193;
            Q193=makeQuery(id+"F7.imprint","IMPRINT",FACE,{"disambiguationData":[TD([[makeQuery(id+"F7.imprint","IMPRINT",EDGE,{"derivedFrom":sQuery(id+"F7.wireOp",EDGE,"E5.7.21.0")}),1.0]])]});
            var Q194;
            Q194=makeQuery(id+"F7.imprint","IMPRINT",FACE,{"disambiguationData":[TD([[makeQuery(id+"F7.imprint","IMPRINT",EDGE,{"derivedFrom":sQuery(id+"F7.wireOp",EDGE,"E5.26.8.0")}),1.0]])]});
            var Q195;
            Q195=makeQuery(id+"F7.imprint","IMPRINT",FACE,{"disambiguationData":[TD([[makeQuery(id+"F7.imprint","IMPRINT",EDGE,{"derivedFrom":sQuery(id+"F7.wireOp",EDGE,"E5.8.22.0")}),1.0]])]});
            var Q196;
            Q196=makeQuery(id+"F7.imprint","IMPRINT",FACE,{"disambiguationData":[TD([[makeQuery(id+"F7.imprint","IMPRINT",EDGE,{"derivedFrom":sQuery(id+"F7.wireOp",EDGE,"E5.11.9.0")}),1.0]])]});
            var Q197;
            Q197=makeQuery(id+"F7.imprint","IMPRINT",FACE,{"disambiguationData":[TD([[makeQuery(id+"F7.imprint","IMPRINT",EDGE,{"derivedFrom":sQuery(id+"F7.wireOp",EDGE,"E5.4.2.0")}),1.0]])]});
            var Q198;
            Q198=makeQuery(id+"F7.imprint","IMPRINT",FACE,{"disambiguationData":[TD([[makeQuery(id+"F7.imprint","IMPRINT",EDGE,{"derivedFrom":sQuery(id+"F7.wireOp",EDGE,"E5.6.4.0")}),1.0]])]});
            var Q199;
            Q199=makeQuery(id+"F7.imprint","IMPRINT",FACE,{"disambiguationData":[TD([[makeQuery(id+"F7.imprint","IMPRINT",EDGE,{"derivedFrom":sQuery(id+"F7.wireOp",EDGE,"E5.26.24.0")}),1.0]])]});
            var Q200;
            Q200=makeQuery(id+"F7.imprint","IMPRINT",FACE,{"disambiguationData":[TD([[makeQuery(id+"F7.imprint","IMPRINT",EDGE,{"derivedFrom":sQuery(id+"F7.wireOp",EDGE,"E5.4.18.0")}),1.0]])]});
            var Q201;
            Q201=makeQuery(id+"F7.imprint","IMPRINT",FACE,{"disambiguationData":[TD([[makeQuery(id+"F7.imprint","IMPRINT",EDGE,{"derivedFrom":sQuery(id+"F7.wireOp",EDGE,"E5.7.5.0")}),1.0]])]});
            var Q202;
            Q202=makeQuery(id+"F7.imprint","IMPRINT",FACE,{"disambiguationData":[TD([[makeQuery(id+"F7.imprint","IMPRINT",EDGE,{"derivedFrom":sQuery(id+"F7.wireOp",EDGE,"E5.10.24.0")}),1.0]])]});
            var Q203;
            Q203=makeQuery(id+"F7.imprint","IMPRINT",FACE,{"disambiguationData":[TD([[makeQuery(id+"F7.imprint","IMPRINT",EDGE,{"derivedFrom":sQuery(id+"F7.wireOp",EDGE,"E5.13.11.0")}),1.0]])]});
            var Q204;
            Q204=makeQuery(id+"F7.imprint","IMPRINT",FACE,{"disambiguationData":[TD([[makeQuery(id+"F7.imprint","IMPRINT",EDGE,{"derivedFrom":sQuery(id+"F7.wireOp",EDGE,"E5.12.26.0")}),1.0]])]});
            var Q205;
            Q205=makeQuery(id+"F7.imprint","IMPRINT",FACE,{"disambiguationData":[TD([[makeQuery(id+"F7.imprint","IMPRINT",EDGE,{"derivedFrom":sQuery(id+"F7.wireOp",EDGE,"E5.15.13.0")}),1.0]])]});
            var Q206;
            Q206=makeQuery(id+"F7.imprint","IMPRINT",FACE,{"disambiguationData":[TD([[makeQuery(id+"F7.imprint","IMPRINT",EDGE,{"derivedFrom":sQuery(id+"F7.wireOp",EDGE,"E5.14.28.0")}),1.0]])]});
            var Q207;
            Q207=makeQuery(id+"F7.imprint","IMPRINT",FACE,{"disambiguationData":[TD([[makeQuery(id+"F7.imprint","IMPRINT",EDGE,{"derivedFrom":sQuery(id+"F7.wireOp",EDGE,"E5.14.12.0")}),1.0]])]});
            var Q208;
            Q208=makeQuery(id+"F7.imprint","IMPRINT",FACE,{"disambiguationData":[TD([[makeQuery(id+"F7.imprint","IMPRINT",EDGE,{"derivedFrom":sQuery(id+"F7.wireOp",EDGE,"E5.13.27.0")}),1.0]])]});
            var Q209;
            Q209=makeQuery(id+"F7.imprint","IMPRINT",FACE,{"disambiguationData":[TD([[makeQuery(id+"F7.imprint","IMPRINT",EDGE,{"derivedFrom":sQuery(id+"F7.wireOp",EDGE,"E5.32.15.0")}),1.0]])]});
            var Q210;
            Q210=makeQuery(id+"F7.imprint","IMPRINT",FACE,{"disambiguationData":[TD([[makeQuery(id+"F7.imprint","IMPRINT",EDGE,{"derivedFrom":sQuery(id+"F7.wireOp",EDGE,"E5.27.10.0")}),1.0]])]});
            var Q211;
            Q211=makeQuery(id+"F7.imprint","IMPRINT",FACE,{"disambiguationData":[TD([[makeQuery(id+"F7.imprint","IMPRINT",EDGE,{"derivedFrom":sQuery(id+"F7.wireOp",EDGE,"E5.29.12.0")}),1.0]])]});
            var Q212;
            Q212=makeQuery(id+"F7.imprint","IMPRINT",FACE,{"disambiguationData":[TD([[makeQuery(id+"F7.imprint","IMPRINT",EDGE,{"derivedFrom":sQuery(id+"F7.wireOp",EDGE,"E5.28.27.0")}),1.0]])]});
            var Q213;
            Q213=makeQuery(id+"F7.imprint","IMPRINT",FACE,{"disambiguationData":[TD([[makeQuery(id+"F7.imprint","IMPRINT",EDGE,{"derivedFrom":sQuery(id+"F7.wireOp",EDGE,"E5.28.11.0")}),1.0]])]});
            var Q214;
            Q214=makeQuery(id+"F7.imprint","IMPRINT",FACE,{"disambiguationData":[TD([[makeQuery(id+"F7.imprint","IMPRINT",EDGE,{"derivedFrom":sQuery(id+"F7.wireOp",EDGE,"E5.31.14.0")}),1.0]])]});
            var Q215;
            Q215=makeQuery(id+"F7.imprint","IMPRINT",FACE,{"disambiguationData":[TD([[makeQuery(id+"F7.imprint","IMPRINT",EDGE,{"derivedFrom":sQuery(id+"F7.wireOp",EDGE,"E5.30.29.0")}),1.0]])]});
            var Q216;
            Q216=makeQuery(id+"F7.imprint","IMPRINT",FACE,{"disambiguationData":[TD([[makeQuery(id+"F7.imprint","IMPRINT",EDGE,{"derivedFrom":sQuery(id+"F7.wireOp",EDGE,"E5.30.13.0")}),1.0]])]});
            var Q217;
            Q217=makeQuery(id+"F7.imprint","IMPRINT",FACE,{"disambiguationData":[TD([[makeQuery(id+"F7.imprint","IMPRINT",EDGE,{"derivedFrom":sQuery(id+"F7.wireOp",EDGE,"E5.29.28.0")}),1.0]])]});
            var Q218;
            Q218=makeQuery(id+"F7.imprint","IMPRINT",FACE,{"disambiguationData":[TD([[makeQuery(id+"F7.imprint","IMPRINT",EDGE,{"derivedFrom":sQuery(id+"F7.wireOp",EDGE,"E5.2.1.0")}),1.0]])]});
            var Q219;
            Q219=makeQuery(id+"F7.imprint","IMPRINT",FACE,{"disambiguationData":[TD([[makeQuery(id+"F7.imprint","IMPRINT",EDGE,{"derivedFrom":sQuery(id+"F7.wireOp",EDGE,"E5.4.3.0")}),1.0]])]});
            var Q220;
            Q220=makeQuery(id+"F7.imprint","IMPRINT",FACE,{"disambiguationData":[TD([[makeQuery(id+"F7.imprint","IMPRINT",EDGE,{"derivedFrom":sQuery(id+"F7.wireOp",EDGE,"E5.3.18.0")}),1.0]])]});
            var Q221;
            Q221=makeQuery(id+"F7.imprint","IMPRINT",FACE,{"disambiguationData":[TD([[makeQuery(id+"F7.imprint","IMPRINT",EDGE,{"derivedFrom":sQuery(id+"F7.wireOp",EDGE,"E5.3.2.0")}),1.0]])]});
            var Q222;
            Q222=makeQuery(id+"F7.imprint","IMPRINT",FACE,{"disambiguationData":[TD([[makeQuery(id+"F7.imprint","IMPRINT",EDGE,{"derivedFrom":sQuery(id+"F7.wireOp",EDGE,"E5.2.17.0")}),1.0]])]});
            var Q223;
            Q223=makeQuery(id+"F7.imprint","IMPRINT",FACE,{"disambiguationData":[TD([[makeQuery(id+"F7.imprint","IMPRINT",EDGE,{"derivedFrom":sQuery(id+"F7.wireOp",EDGE,"E5.19.18.0")}),1.0]])]});
            var Q224;
            Q224=makeQuery(id+"F7.imprint","IMPRINT",FACE,{"disambiguationData":[TD([[makeQuery(id+"F7.imprint","IMPRINT",EDGE,{"derivedFrom":sQuery(id+"F7.wireOp",EDGE,"E5.19.2.0")}),1.0]])]});
            var Q225;
            Q225=makeQuery(id+"F7.imprint","IMPRINT",FACE,{"disambiguationData":[TD([[makeQuery(id+"F7.imprint","IMPRINT",EDGE,{"derivedFrom":sQuery(id+"F7.wireOp",EDGE,"E5.18.17.0")}),1.0]])]});
            var Q226;
            Q226=makeQuery(id+"F7.imprint","IMPRINT",FACE,{"disambiguationData":[TD([[makeQuery(id+"F7.imprint","IMPRINT",EDGE,{"derivedFrom":sQuery(id+"F7.wireOp",EDGE,"E5.21.20.0")}),1.0]])]});
            var Q227;
            Q227=makeQuery(id+"F7.imprint","IMPRINT",FACE,{"disambiguationData":[TD([[makeQuery(id+"F7.imprint","IMPRINT",EDGE,{"derivedFrom":sQuery(id+"F7.wireOp",EDGE,"E5.21.4.0")}),1.0]])]});
            var Q228;
            Q228=makeQuery(id+"F7.imprint","IMPRINT",FACE,{"disambiguationData":[TD([[makeQuery(id+"F7.imprint","IMPRINT",EDGE,{"derivedFrom":sQuery(id+"F7.wireOp",EDGE,"E5.20.19.0")}),1.0]])]});
            var Q229;
            Q229=makeQuery(id+"F7.imprint","IMPRINT",FACE,{"disambiguationData":[TD([[makeQuery(id+"F7.imprint","IMPRINT",EDGE,{"derivedFrom":sQuery(id+"F7.wireOp",EDGE,"E5.20.3.0")}),1.0]])]});
            var Q230;
            Q230=makeQuery(id+"F7.imprint","IMPRINT",FACE,{"disambiguationData":[TD([[makeQuery(id+"F7.imprint","IMPRINT",EDGE,{"derivedFrom":sQuery(id+"F7.wireOp",EDGE,"E5.23.22.0")}),1.0]])]});
            var Q231;
            Q231=makeQuery(id+"F7.imprint","IMPRINT",FACE,{"disambiguationData":[TD([[makeQuery(id+"F7.imprint","IMPRINT",EDGE,{"derivedFrom":sQuery(id+"F7.wireOp",EDGE,"E5.23.6.0")}),1.0]])]});
            var Q232;
            Q232=makeQuery(id+"F7.imprint","IMPRINT",FACE,{"disambiguationData":[TD([[makeQuery(id+"F7.imprint","IMPRINT",EDGE,{"derivedFrom":sQuery(id+"F7.wireOp",EDGE,"E5.25.24.0")}),1.0]])]});
            var Q233;
            Q233=makeQuery(id+"F7.imprint","IMPRINT",FACE,{"disambiguationData":[TD([[makeQuery(id+"F7.imprint","IMPRINT",EDGE,{"derivedFrom":sQuery(id+"F7.wireOp",EDGE,"E5.25.8.0")}),1.0]])]});
            var Q234;
            Q234=makeQuery(id+"F7.imprint","IMPRINT",FACE,{"disambiguationData":[TD([[makeQuery(id+"F7.imprint","IMPRINT",EDGE,{"derivedFrom":sQuery(id+"F7.wireOp",EDGE,"E5.24.23.0")}),1.0]])]});
            var Q235;
            Q235=makeQuery(id+"F7.imprint","IMPRINT",FACE,{"disambiguationData":[TD([[makeQuery(id+"F7.imprint","IMPRINT",EDGE,{"derivedFrom":sQuery(id+"F7.wireOp",EDGE,"E5.24.7.0")}),1.0]])]});
            var Q236;
            Q236=makeQuery(id+"F7.imprint","IMPRINT",FACE,{"disambiguationData":[TD([[makeQuery(id+"F7.imprint","IMPRINT",EDGE,{"derivedFrom":sQuery(id+"F7.wireOp",EDGE,"E5.26.25.0")}),1.0]])]});
            var Q237;
            Q237=makeQuery(id+"F7.imprint","IMPRINT",FACE,{"disambiguationData":[TD([[makeQuery(id+"F7.imprint","IMPRINT",EDGE,{"derivedFrom":sQuery(id+"F7.wireOp",EDGE,"E5.26.9.0")}),1.0]])]});
            var Q238;
            Q238=makeQuery(id+"F7.imprint","IMPRINT",FACE,{"disambiguationData":[TD([[makeQuery(id+"F7.imprint","IMPRINT",EDGE,{"derivedFrom":sQuery(id+"F7.wireOp",EDGE,"E5.5.20.0")}),1.0]])]});
            var Q239;
            Q239=makeQuery(id+"F7.imprint","IMPRINT",FACE,{"disambiguationData":[TD([[makeQuery(id+"F7.imprint","IMPRINT",EDGE,{"derivedFrom":sQuery(id+"F7.wireOp",EDGE,"E5.5.4.0")}),1.0]])]});
            var Q240;
            Q240=makeQuery(id+"F7.imprint","IMPRINT",FACE,{"disambiguationData":[TD([[makeQuery(id+"F7.imprint","IMPRINT",EDGE,{"derivedFrom":sQuery(id+"F7.wireOp",EDGE,"E5.4.19.0")}),1.0]])]});
            var Q241;
            Q241=makeQuery(id+"F7.imprint","IMPRINT",FACE,{"disambiguationData":[TD([[makeQuery(id+"F7.imprint","IMPRINT",EDGE,{"derivedFrom":sQuery(id+"F7.wireOp",EDGE,"E5.8.7.0")}),1.0]])]});
            var Q242;
            Q242=makeQuery(id+"F7.imprint","IMPRINT",FACE,{"disambiguationData":[TD([[makeQuery(id+"F7.imprint","IMPRINT",EDGE,{"derivedFrom":sQuery(id+"F7.wireOp",EDGE,"E5.7.22.0")}),1.0]])]});
            var Q243;
            Q243=makeQuery(id+"F7.imprint","IMPRINT",FACE,{"disambiguationData":[TD([[makeQuery(id+"F7.imprint","IMPRINT",EDGE,{"derivedFrom":sQuery(id+"F7.wireOp",EDGE,"E5.7.6.0")}),1.0]])]});
            var Q244;
            Q244=makeQuery(id+"F7.imprint","IMPRINT",FACE,{"disambiguationData":[TD([[makeQuery(id+"F7.imprint","IMPRINT",EDGE,{"derivedFrom":sQuery(id+"F7.wireOp",EDGE,"E5.10.9.0")}),1.0]])]});
            var Q245;
            Q245=makeQuery(id+"F7.imprint","IMPRINT",FACE,{"disambiguationData":[TD([[makeQuery(id+"F7.imprint","IMPRINT",EDGE,{"derivedFrom":sQuery(id+"F7.wireOp",EDGE,"E5.9.24.0")}),1.0]])]});
            var Q246;
            Q246=makeQuery(id+"F7.imprint","IMPRINT",FACE,{"disambiguationData":[TD([[makeQuery(id+"F7.imprint","IMPRINT",EDGE,{"derivedFrom":sQuery(id+"F7.wireOp",EDGE,"E5.9.8.0")}),1.0]])]});
            var Q247;
            Q247=makeQuery(id+"F7.imprint","IMPRINT",FACE,{"disambiguationData":[TD([[makeQuery(id+"F7.imprint","IMPRINT",EDGE,{"derivedFrom":sQuery(id+"F7.wireOp",EDGE,"E5.8.23.0")}),1.0]])]});
            var Q248;
            Q248=makeQuery(id+"F7.imprint","IMPRINT",FACE,{"disambiguationData":[TD([[makeQuery(id+"F7.imprint","IMPRINT",EDGE,{"derivedFrom":sQuery(id+"F7.wireOp",EDGE,"E5.12.11.0")}),1.0]])]});
            var Q249;
            Q249=makeQuery(id+"F7.imprint","IMPRINT",FACE,{"disambiguationData":[TD([[makeQuery(id+"F7.imprint","IMPRINT",EDGE,{"derivedFrom":sQuery(id+"F7.wireOp",EDGE,"E5.11.26.0")}),1.0]])]});
            var Q250;
            Q250=makeQuery(id+"F7.imprint","IMPRINT",FACE,{"disambiguationData":[TD([[makeQuery(id+"F7.imprint","IMPRINT",EDGE,{"derivedFrom":sQuery(id+"F7.wireOp",EDGE,"E5.11.10.0")}),1.0]])]});
            var Q251;
            Q251=makeQuery(id+"F7.imprint","IMPRINT",FACE,{"disambiguationData":[TD([[makeQuery(id+"F7.imprint","IMPRINT",EDGE,{"derivedFrom":sQuery(id+"F7.wireOp",EDGE,"E5.10.25.0")}),1.0]])]});
            var Q252;
            Q252=makeQuery(id+"F7.imprint","IMPRINT",FACE,{"disambiguationData":[TD([[makeQuery(id+"F7.imprint","IMPRINT",EDGE,{"derivedFrom":sQuery(id+"F7.wireOp",EDGE,"E5.13.12.0")}),1.0]])]});
            var Q253;
            Q253=makeQuery(id+"F7.imprint","IMPRINT",FACE,{"disambiguationData":[TD([[makeQuery(id+"F7.imprint","IMPRINT",EDGE,{"derivedFrom":sQuery(id+"F7.wireOp",EDGE,"E5.12.27.0")}),1.0]])]});
            var Q254;
            Q254=makeQuery(id+"F7.imprint","IMPRINT",FACE,{"disambiguationData":[TD([[makeQuery(id+"F7.imprint","IMPRINT",EDGE,{"derivedFrom":sQuery(id+"F7.wireOp",EDGE,"E5.15.14.0")}),1.0]])]});
            var Q255;
            Q255=makeQuery(id+"F7.imprint","IMPRINT",FACE,{"disambiguationData":[TD([[makeQuery(id+"F7.imprint","IMPRINT",EDGE,{"derivedFrom":sQuery(id+"F7.wireOp",EDGE,"E5.14.29.0")}),1.0]])]});
            var Q256;
            Q256=makeQuery(id+"F7.imprint","IMPRINT",FACE,{"disambiguationData":[TD([[makeQuery(id+"F7.imprint","IMPRINT",EDGE,{"derivedFrom":sQuery(id+"F7.wireOp",EDGE,"E5.14.13.0")}),1.0]])]});
            var Q257;
            Q257=makeQuery(id+"F7.imprint","IMPRINT",FACE,{"disambiguationData":[TD([[makeQuery(id+"F7.imprint","IMPRINT",EDGE,{"derivedFrom":sQuery(id+"F7.wireOp",EDGE,"E5.13.28.0")}),1.0]])]});
            var Q258;
            Q258=makeQuery(id+"F7.imprint","IMPRINT",FACE,{"disambiguationData":[TD([[makeQuery(id+"F7.imprint","IMPRINT",EDGE,{"derivedFrom":sQuery(id+"F7.wireOp",EDGE,"E5.17.16.0")}),1.0]])]});
            var Q259;
            Q259=makeQuery(id+"F7.imprint","IMPRINT",FACE,{"disambiguationData":[TD([[makeQuery(id+"F7.imprint","IMPRINT",EDGE,{"derivedFrom":sQuery(id+"F7.wireOp",EDGE,"E5.16.15.0")}),1.0]])]});
            var Q260;
            Q260=makeQuery(id+"F7.imprint","IMPRINT",FACE,{"disambiguationData":[TD([[makeQuery(id+"F7.imprint","IMPRINT",EDGE,{"derivedFrom":sQuery(id+"F7.wireOp",EDGE,"E5.32.1.0")}),1.0]])]});
            var Q261;
            Q261=makeQuery(id+"F7.imprint","IMPRINT",FACE,{"disambiguationData":[TD([[makeQuery(id+"F7.imprint","IMPRINT",EDGE,{"derivedFrom":sQuery(id+"F7.wireOp",EDGE,"E5.27.12.0")}),1.0]])]});
            var Q262;
            Q262=makeQuery(id+"F7.imprint","IMPRINT",FACE,{"disambiguationData":[TD([[makeQuery(id+"F7.imprint","IMPRINT",EDGE,{"derivedFrom":sQuery(id+"F7.wireOp",EDGE,"E5.26.27.0")}),1.0]])]});
            var Q263;
            Q263=makeQuery(id+"F7.imprint","IMPRINT",FACE,{"disambiguationData":[TD([[makeQuery(id+"F7.imprint","IMPRINT",EDGE,{"derivedFrom":sQuery(id+"F7.wireOp",EDGE,"E5.32.17.0")}),1.0]])]});
            var Q264;
            Q264=makeQuery(id+"F7.imprint","IMPRINT",FACE,{"disambiguationData":[TD([[makeQuery(id+"F7.imprint","IMPRINT",EDGE,{"derivedFrom":sQuery(id+"F7.wireOp",EDGE,"E5.29.14.0")}),1.0]])]});
            var Q265;
            Q265=makeQuery(id+"F7.imprint","IMPRINT",FACE,{"disambiguationData":[TD([[makeQuery(id+"F7.imprint","IMPRINT",EDGE,{"derivedFrom":sQuery(id+"F7.wireOp",EDGE,"E5.28.29.0")}),1.0]])]});
            var Q266;
            Q266=makeQuery(id+"F7.imprint","IMPRINT",FACE,{"disambiguationData":[TD([[makeQuery(id+"F7.imprint","IMPRINT",EDGE,{"derivedFrom":sQuery(id+"F7.wireOp",EDGE,"E5.28.13.0")}),1.0]])]});
            var Q267;
            Q267=makeQuery(id+"F7.imprint","IMPRINT",FACE,{"disambiguationData":[TD([[makeQuery(id+"F7.imprint","IMPRINT",EDGE,{"derivedFrom":sQuery(id+"F7.wireOp",EDGE,"E5.27.28.0")}),1.0]])]});
            var Q268;
            Q268=makeQuery(id+"F7.imprint","IMPRINT",FACE,{"disambiguationData":[TD([[makeQuery(id+"F7.imprint","IMPRINT",EDGE,{"derivedFrom":sQuery(id+"F7.wireOp",EDGE,"E5.12.13.0")}),1.0]])]});
            var Q269;
            Q269=makeQuery(id+"F7.imprint","IMPRINT",FACE,{"disambiguationData":[TD([[makeQuery(id+"F7.imprint","IMPRINT",EDGE,{"derivedFrom":sQuery(id+"F7.wireOp",EDGE,"E5.11.28.0")}),1.0]])]});
            var Q270;
            Q270=makeQuery(id+"F7.imprint","IMPRINT",FACE,{"disambiguationData":[TD([[makeQuery(id+"F7.imprint","IMPRINT",EDGE,{"derivedFrom":sQuery(id+"F7.wireOp",EDGE,"E5.11.12.0")}),1.0]])]});
            var Q271;
            Q271=makeQuery(id+"F7.imprint","IMPRINT",FACE,{"disambiguationData":[TD([[makeQuery(id+"F7.imprint","IMPRINT",EDGE,{"derivedFrom":sQuery(id+"F7.wireOp",EDGE,"E5.10.27.0")}),1.0]])]});
            var Q272;
            Q272=makeQuery(id+"F7.imprint","IMPRINT",FACE,{"disambiguationData":[TD([[makeQuery(id+"F7.imprint","IMPRINT",EDGE,{"derivedFrom":sQuery(id+"F7.wireOp",EDGE,"E5.12.29.0")}),1.0]])]});
            var Q273;
            Q273=makeQuery(id+"F7.imprint","IMPRINT",FACE,{"disambiguationData":[TD([[makeQuery(id+"F7.imprint","IMPRINT",EDGE,{"derivedFrom":sQuery(id+"F7.wireOp",EDGE,"E5.13.14.0")}),1.0]])]});
            var Q274;
            Q274=makeQuery(id+"F7.imprint","IMPRINT",FACE,{"disambiguationData":[TD([[makeQuery(id+"F7.imprint","IMPRINT",EDGE,{"derivedFrom":sQuery(id+"F7.wireOp",EDGE,"E5.15.16.0")}),1.0]])]});
            var Q275;
            Q275=makeQuery(id+"F7.imprint","IMPRINT",FACE,{"disambiguationData":[TD([[makeQuery(id+"F7.imprint","IMPRINT",EDGE,{"derivedFrom":sQuery(id+"F7.wireOp",EDGE,"E5.17.18.0")}),1.0]])]});
            var Q276;
            Q276=makeQuery(id+"F7.imprint","IMPRINT",FACE,{"disambiguationData":[TD([[makeQuery(id+"F7.imprint","IMPRINT",EDGE,{"derivedFrom":sQuery(id+"F7.wireOp",EDGE,"E5.17.2.0")}),1.0]])]});
            var Q277;
            Q277=makeQuery(id+"F7.imprint","IMPRINT",FACE,{"disambiguationData":[TD([[makeQuery(id+"F7.imprint","IMPRINT",EDGE,{"derivedFrom":sQuery(id+"F7.wireOp",EDGE,"E5.16.17.0")}),1.0]])]});
            var Q278;
            Q278=makeQuery(id+"F7.imprint","IMPRINT",FACE,{"disambiguationData":[TD([[makeQuery(id+"F7.imprint","IMPRINT",EDGE,{"derivedFrom":sQuery(id+"F7.wireOp",EDGE,"E5.16.1.0")}),1.0]])]});
            var Q279;
            Q279=makeQuery(id+"F7.imprint","IMPRINT",FACE,{"disambiguationData":[TD([[makeQuery(id+"F7.imprint","IMPRINT",EDGE,{"derivedFrom":sQuery(id+"F7.wireOp",EDGE,"E5.19.20.0")}),1.0]])]});
            var Q280;
            Q280=makeQuery(id+"F7.imprint","IMPRINT",FACE,{"disambiguationData":[TD([[makeQuery(id+"F7.imprint","IMPRINT",EDGE,{"derivedFrom":sQuery(id+"F7.wireOp",EDGE,"E5.19.4.0")}),1.0]])]});
            var Q281;
            Q281=makeQuery(id+"F7.imprint","IMPRINT",FACE,{"disambiguationData":[TD([[makeQuery(id+"F7.imprint","IMPRINT",EDGE,{"derivedFrom":sQuery(id+"F7.wireOp",EDGE,"E5.18.19.0")}),1.0]])]});
            var Q282;
            Q282=makeQuery(id+"F7.imprint","IMPRINT",FACE,{"disambiguationData":[TD([[makeQuery(id+"F7.imprint","IMPRINT",EDGE,{"derivedFrom":sQuery(id+"F7.wireOp",EDGE,"E5.18.3.0")}),1.0]])]});
            var Q283;
            Q283=makeQuery(id+"F7.imprint","IMPRINT",FACE,{"disambiguationData":[TD([[makeQuery(id+"F7.imprint","IMPRINT",EDGE,{"derivedFrom":sQuery(id+"F7.wireOp",EDGE,"E5.21.22.0")}),1.0]])]});
            var Q284;
            Q284=makeQuery(id+"F7.imprint","IMPRINT",FACE,{"disambiguationData":[TD([[makeQuery(id+"F7.imprint","IMPRINT",EDGE,{"derivedFrom":sQuery(id+"F7.wireOp",EDGE,"E5.21.6.0")}),1.0]])]});
            var Q285;
            Q285=makeQuery(id+"F7.imprint","IMPRINT",FACE,{"disambiguationData":[TD([[makeQuery(id+"F7.imprint","IMPRINT",EDGE,{"derivedFrom":sQuery(id+"F7.wireOp",EDGE,"E5.20.21.0")}),1.0]])]});
            var Q286;
            Q286=makeQuery(id+"F7.imprint","IMPRINT",FACE,{"disambiguationData":[TD([[makeQuery(id+"F7.imprint","IMPRINT",EDGE,{"derivedFrom":sQuery(id+"F7.wireOp",EDGE,"E5.20.5.0")}),1.0]])]});
            var Q287;
            Q287=makeQuery(id+"F7.imprint","IMPRINT",FACE,{"disambiguationData":[TD([[makeQuery(id+"F7.imprint","IMPRINT",EDGE,{"derivedFrom":sQuery(id+"F7.wireOp",EDGE,"E5.23.24.0")}),1.0]])]});
            var Q288;
            Q288=makeQuery(id+"F7.imprint","IMPRINT",FACE,{"disambiguationData":[TD([[makeQuery(id+"F7.imprint","IMPRINT",EDGE,{"derivedFrom":sQuery(id+"F7.wireOp",EDGE,"E5.23.8.0")}),1.0]])]});
            var Q289;
            Q289=makeQuery(id+"F7.imprint","IMPRINT",FACE,{"disambiguationData":[TD([[makeQuery(id+"F7.imprint","IMPRINT",EDGE,{"derivedFrom":sQuery(id+"F7.wireOp",EDGE,"E5.22.23.0")}),1.0]])]});
            var Q290;
            Q290=makeQuery(id+"F7.imprint","IMPRINT",FACE,{"disambiguationData":[TD([[makeQuery(id+"F7.imprint","IMPRINT",EDGE,{"derivedFrom":sQuery(id+"F7.wireOp",EDGE,"E5.22.7.0")}),1.0]])]});
            var Q291;
            Q291=makeQuery(id+"F7.imprint","IMPRINT",FACE,{"disambiguationData":[TD([[makeQuery(id+"F7.imprint","IMPRINT",EDGE,{"derivedFrom":sQuery(id+"F7.wireOp",EDGE,"E5.30.15.0")}),1.0]])]});
            var Q292;
            Q292=makeQuery(id+"F7.imprint","IMPRINT",FACE,{"disambiguationData":[TD([[makeQuery(id+"F7.imprint","IMPRINT",EDGE,{"derivedFrom":sQuery(id+"F7.wireOp",EDGE,"E5.2.3.0")}),1.0]])]});
            var Q293;
            Q293=makeQuery(id+"F7.imprint","IMPRINT",FACE,{"disambiguationData":[TD([[makeQuery(id+"F7.imprint","IMPRINT",EDGE,{"derivedFrom":sQuery(id+"F7.wireOp",EDGE,"E5.1.18.0")}),1.0]])]});
            var Q294;
            Q294=makeQuery(id+"F7.imprint","IMPRINT",FACE,{"disambiguationData":[TD([[makeQuery(id+"F7.imprint","IMPRINT",EDGE,{"derivedFrom":sQuery(id+"F7.wireOp",EDGE,"E5.1.2.0")}),1.0]])]});
            var Q295;
            Q295=makeQuery(id+"F7.imprint","IMPRINT",FACE,{"disambiguationData":[TD([[makeQuery(id+"F7.imprint","IMPRINT",EDGE,{"derivedFrom":sQuery(id+"F7.wireOp",EDGE,"E5.4.5.0")}),1.0]])]});
            var Q296;
            Q296=makeQuery(id+"F7.imprint","IMPRINT",FACE,{"disambiguationData":[TD([[makeQuery(id+"F7.imprint","IMPRINT",EDGE,{"derivedFrom":sQuery(id+"F7.wireOp",EDGE,"E5.3.20.0")}),1.0]])]});
            var Q297;
            Q297=makeQuery(id+"F7.imprint","IMPRINT",FACE,{"disambiguationData":[TD([[makeQuery(id+"F7.imprint","IMPRINT",EDGE,{"derivedFrom":sQuery(id+"F7.wireOp",EDGE,"E5.3.4.0")}),1.0]])]});
            var Q298;
            Q298=makeQuery(id+"F7.imprint","IMPRINT",FACE,{"disambiguationData":[TD([[makeQuery(id+"F7.imprint","IMPRINT",EDGE,{"derivedFrom":sQuery(id+"F7.wireOp",EDGE,"E5.2.19.0")}),1.0]])]});
            var Q299;
            Q299=makeQuery(id+"F7.imprint","IMPRINT",FACE,{"disambiguationData":[TD([[makeQuery(id+"F7.imprint","IMPRINT",EDGE,{"derivedFrom":sQuery(id+"F7.wireOp",EDGE,"E5.6.7.0")}),1.0]])]});
            var Q300;
            Q300=makeQuery(id+"F7.imprint","IMPRINT",FACE,{"disambiguationData":[TD([[makeQuery(id+"F7.imprint","IMPRINT",EDGE,{"derivedFrom":sQuery(id+"F7.wireOp",EDGE,"E5.5.22.0")}),1.0]])]});
            var Q301;
            Q301=makeQuery(id+"F7.imprint","IMPRINT",FACE,{"disambiguationData":[TD([[makeQuery(id+"F7.imprint","IMPRINT",EDGE,{"derivedFrom":sQuery(id+"F7.wireOp",EDGE,"E5.5.6.0")}),1.0]])]});
            var Q302;
            Q302=makeQuery(id+"F7.imprint","IMPRINT",FACE,{"disambiguationData":[TD([[makeQuery(id+"F7.imprint","IMPRINT",EDGE,{"derivedFrom":sQuery(id+"F7.wireOp",EDGE,"E5.4.21.0")}),1.0]])]});
            var Q303;
            Q303=makeQuery(id+"F7.imprint","IMPRINT",FACE,{"disambiguationData":[TD([[makeQuery(id+"F7.imprint","IMPRINT",EDGE,{"derivedFrom":sQuery(id+"F7.wireOp",EDGE,"E5.8.9.0")}),1.0]])]});
            var Q304;
            Q304=makeQuery(id+"F7.imprint","IMPRINT",FACE,{"disambiguationData":[TD([[makeQuery(id+"F7.imprint","IMPRINT",EDGE,{"derivedFrom":sQuery(id+"F7.wireOp",EDGE,"E5.7.24.0")}),1.0]])]});
            var Q305;
            Q305=makeQuery(id+"F7.imprint","IMPRINT",FACE,{"disambiguationData":[TD([[makeQuery(id+"F7.imprint","IMPRINT",EDGE,{"derivedFrom":sQuery(id+"F7.wireOp",EDGE,"E5.7.8.0")}),1.0]])]});
            var Q306;
            Q306=makeQuery(id+"F7.imprint","IMPRINT",FACE,{"disambiguationData":[TD([[makeQuery(id+"F7.imprint","IMPRINT",EDGE,{"derivedFrom":sQuery(id+"F7.wireOp",EDGE,"E5.6.23.0")}),1.0]])]});
            var Q307;
            Q307=makeQuery(id+"F7.imprint","IMPRINT",FACE,{"disambiguationData":[TD([[makeQuery(id+"F7.imprint","IMPRINT",EDGE,{"derivedFrom":sQuery(id+"F7.wireOp",EDGE,"E5.9.10.0")}),1.0]])]});
            var Q308;
            Q308=makeQuery(id+"F7.imprint","IMPRINT",FACE,{"disambiguationData":[TD([[makeQuery(id+"F7.imprint","IMPRINT",EDGE,{"derivedFrom":sQuery(id+"F7.wireOp",EDGE,"E5.8.25.0")}),1.0]])]});
            var Q309;
            Q309=makeQuery(id+"F7.imprint","IMPRINT",FACE,{"disambiguationData":[TD([[makeQuery(id+"F7.imprint","IMPRINT",EDGE,{"derivedFrom":sQuery(id+"F7.wireOp",EDGE,"E5.32.2.0")}),1.0]])]});
            var Q310;
            Q310=makeQuery(id+"F7.imprint","IMPRINT",FACE,{"disambiguationData":[TD([[makeQuery(id+"F7.imprint","IMPRINT",EDGE,{"derivedFrom":sQuery(id+"F7.wireOp",EDGE,"E5.27.13.0")}),1.0]])]});
            var Q311;
            Q311=makeQuery(id+"F7.imprint","IMPRINT",FACE,{"disambiguationData":[TD([[makeQuery(id+"F7.imprint","IMPRINT",EDGE,{"derivedFrom":sQuery(id+"F7.wireOp",EDGE,"E5.26.28.0")}),1.0]])]});
            var Q312;
            Q312=makeQuery(id+"F7.imprint","IMPRINT",FACE,{"disambiguationData":[TD([[makeQuery(id+"F7.imprint","IMPRINT",EDGE,{"derivedFrom":sQuery(id+"F7.wireOp",EDGE,"E5.32.18.0")}),1.0]])]});
            var Q313;
            Q313=makeQuery(id+"F7.imprint","IMPRINT",FACE,{"disambiguationData":[TD([[makeQuery(id+"F7.imprint","IMPRINT",EDGE,{"derivedFrom":sQuery(id+"F7.wireOp",EDGE,"E5.29.15.0")}),1.0]])]});
            var Q314;
            Q314=makeQuery(id+"F7.imprint","IMPRINT",FACE,{"disambiguationData":[TD([[makeQuery(id+"F7.imprint","IMPRINT",EDGE,{"derivedFrom":sQuery(id+"F7.wireOp",EDGE,"E5.28.14.0")}),1.0]])]});
            var Q315;
            Q315=makeQuery(id+"F7.imprint","IMPRINT",FACE,{"disambiguationData":[TD([[makeQuery(id+"F7.imprint","IMPRINT",EDGE,{"derivedFrom":sQuery(id+"F7.wireOp",EDGE,"E5.27.29.0")}),1.0]])]});
            var Q316;
            Q316=makeQuery(id+"F7.imprint","IMPRINT",FACE,{"disambiguationData":[TD([[makeQuery(id+"F7.imprint","IMPRINT",EDGE,{"derivedFrom":sQuery(id+"F7.wireOp",EDGE,"E5.31.17.0")}),1.0]])]});
            var Q317;
            Q317=makeQuery(id+"F7.imprint","IMPRINT",FACE,{"disambiguationData":[TD([[makeQuery(id+"F7.imprint","IMPRINT",EDGE,{"derivedFrom":sQuery(id+"F7.wireOp",EDGE,"E5.25.26.0")}),1.0]])]});
            var Q318;
            Q318=makeQuery(id+"F7.imprint","IMPRINT",FACE,{"disambiguationData":[TD([[makeQuery(id+"F7.imprint","IMPRINT",EDGE,{"derivedFrom":sQuery(id+"F7.wireOp",EDGE,"E5.25.10.0")}),1.0]])]});
            var Q319;
            Q319=makeQuery(id+"F7.imprint","IMPRINT",FACE,{"disambiguationData":[TD([[makeQuery(id+"F7.imprint","IMPRINT",EDGE,{"derivedFrom":sQuery(id+"F7.wireOp",EDGE,"E5.24.25.0")}),1.0]])]});
            var Q320;
            Q320=makeQuery(id+"F7.imprint","IMPRINT",FACE,{"disambiguationData":[TD([[makeQuery(id+"F7.imprint","IMPRINT",EDGE,{"derivedFrom":sQuery(id+"F7.wireOp",EDGE,"E5.24.9.0")}),1.0]])]});
            var Q321;
            Q321=makeQuery(id+"F7.imprint","IMPRINT",FACE,{"disambiguationData":[TD([[makeQuery(id+"F7.imprint","IMPRINT",EDGE,{"derivedFrom":sQuery(id+"F7.wireOp",EDGE,"E5.13.15.0")}),1.0]])]});
            var Q322;
            Q322=makeQuery(id+"F7.imprint","IMPRINT",FACE,{"disambiguationData":[TD([[makeQuery(id+"F7.imprint","IMPRINT",EDGE,{"derivedFrom":sQuery(id+"F7.wireOp",EDGE,"E5.15.17.0")}),1.0]])]});
            var Q323;
            Q323=makeQuery(id+"F7.imprint","IMPRINT",FACE,{"disambiguationData":[TD([[makeQuery(id+"F7.imprint","IMPRINT",EDGE,{"derivedFrom":sQuery(id+"F7.wireOp",EDGE,"E5.15.1.0")}),1.0]])]});
            var Q324;
            Q324=makeQuery(id+"F7.imprint","IMPRINT",FACE,{"disambiguationData":[TD([[makeQuery(id+"F7.imprint","IMPRINT",EDGE,{"derivedFrom":sQuery(id+"F7.wireOp",EDGE,"E5.17.19.0")}),1.0]])]});
            var Q325;
            Q325=makeQuery(id+"F7.imprint","IMPRINT",FACE,{"disambiguationData":[TD([[makeQuery(id+"F7.imprint","IMPRINT",EDGE,{"derivedFrom":sQuery(id+"F7.wireOp",EDGE,"E5.17.3.0")}),1.0]])]});
            var Q326;
            Q326=makeQuery(id+"F7.imprint","IMPRINT",FACE,{"disambiguationData":[TD([[makeQuery(id+"F7.imprint","IMPRINT",EDGE,{"derivedFrom":sQuery(id+"F7.wireOp",EDGE,"E5.33.24.0")}),1.0]])]});
            var Q327;
            Q327=makeQuery(id+"F7.imprint","IMPRINT",FACE,{"disambiguationData":[TD([[makeQuery(id+"F7.imprint","IMPRINT",EDGE,{"derivedFrom":sQuery(id+"F7.wireOp",EDGE,"E5.16.18.0")}),1.0]])]});
            var Q328;
            Q328=makeQuery(id+"F7.imprint","IMPRINT",FACE,{"disambiguationData":[TD([[makeQuery(id+"F7.imprint","IMPRINT",EDGE,{"derivedFrom":sQuery(id+"F7.wireOp",EDGE,"E5.16.2.0")}),1.0]])]});
            var Q329;
            Q329=makeQuery(id+"F7.imprint","IMPRINT",FACE,{"disambiguationData":[TD([[makeQuery(id+"F7.imprint","IMPRINT",EDGE,{"derivedFrom":sQuery(id+"F7.wireOp",EDGE,"E5.19.21.0")}),1.0]])]});
            var Q330;
            Q330=makeQuery(id+"F7.imprint","IMPRINT",FACE,{"disambiguationData":[TD([[makeQuery(id+"F7.imprint","IMPRINT",EDGE,{"derivedFrom":sQuery(id+"F7.wireOp",EDGE,"E5.19.5.0")}),1.0]])]});
            var Q331;
            Q331=makeQuery(id+"F7.imprint","IMPRINT",FACE,{"disambiguationData":[TD([[makeQuery(id+"F7.imprint","IMPRINT",EDGE,{"derivedFrom":sQuery(id+"F7.wireOp",EDGE,"E5.18.4.0")}),1.0]])]});
            var Q332;
            Q332=makeQuery(id+"F7.imprint","IMPRINT",FACE,{"disambiguationData":[TD([[makeQuery(id+"F7.imprint","IMPRINT",EDGE,{"derivedFrom":sQuery(id+"F7.wireOp",EDGE,"E5.21.23.0")}),1.0]])]});
            var Q333;
            Q333=makeQuery(id+"F7.imprint","IMPRINT",FACE,{"disambiguationData":[TD([[makeQuery(id+"F7.imprint","IMPRINT",EDGE,{"derivedFrom":sQuery(id+"F7.wireOp",EDGE,"E5.21.7.0")}),1.0]])]});
            var Q334;
            Q334=makeQuery(id+"F7.imprint","IMPRINT",FACE,{"disambiguationData":[TD([[makeQuery(id+"F7.imprint","IMPRINT",EDGE,{"derivedFrom":sQuery(id+"F7.wireOp",EDGE,"E5.20.22.0")}),1.0]])]});
            var Q335;
            Q335=makeQuery(id+"F7.imprint","IMPRINT",FACE,{"disambiguationData":[TD([[makeQuery(id+"F7.imprint","IMPRINT",EDGE,{"derivedFrom":sQuery(id+"F7.wireOp",EDGE,"E5.20.6.0")}),1.0]])]});
            var Q336;
            Q336=makeQuery(id+"F7.imprint","IMPRINT",FACE,{"disambiguationData":[TD([[makeQuery(id+"F7.imprint","IMPRINT",EDGE,{"derivedFrom":sQuery(id+"F7.wireOp",EDGE,"E5.23.25.0")}),1.0]])]});
            var Q337;
            Q337=makeQuery(id+"F7.imprint","IMPRINT",FACE,{"disambiguationData":[TD([[makeQuery(id+"F7.imprint","IMPRINT",EDGE,{"derivedFrom":sQuery(id+"F7.wireOp",EDGE,"E5.23.9.0")}),1.0]])]});
            var Q338;
            Q338=makeQuery(id+"F7.imprint","IMPRINT",FACE,{"disambiguationData":[TD([[makeQuery(id+"F7.imprint","IMPRINT",EDGE,{"derivedFrom":sQuery(id+"F7.wireOp",EDGE,"E5.22.24.0")}),1.0]])]});
            var Q339;
            Q339=makeQuery(id+"F7.imprint","IMPRINT",FACE,{"disambiguationData":[TD([[makeQuery(id+"F7.imprint","IMPRINT",EDGE,{"derivedFrom":sQuery(id+"F7.wireOp",EDGE,"E5.22.8.0")}),1.0]])]});
            var Q340;
            Q340=makeQuery(id+"F7.imprint","IMPRINT",FACE,{"disambiguationData":[TD([[makeQuery(id+"F7.imprint","IMPRINT",EDGE,{"derivedFrom":sQuery(id+"F7.wireOp",EDGE,"E5.25.27.0")}),1.0]])]});
            var Q341;
            Q341=makeQuery(id+"F7.imprint","IMPRINT",FACE,{"disambiguationData":[TD([[makeQuery(id+"F7.imprint","IMPRINT",EDGE,{"derivedFrom":sQuery(id+"F7.wireOp",EDGE,"E5.25.11.0")}),1.0]])]});
            var Q342;
            Q342=makeQuery(id+"F7.imprint","IMPRINT",FACE,{"disambiguationData":[TD([[makeQuery(id+"F7.imprint","IMPRINT",EDGE,{"derivedFrom":sQuery(id+"F7.wireOp",EDGE,"E5.24.26.0")}),1.0]])]});
            var Q343;
            Q343=makeQuery(id+"F7.imprint","IMPRINT",FACE,{"disambiguationData":[TD([[makeQuery(id+"F7.imprint","IMPRINT",EDGE,{"derivedFrom":sQuery(id+"F7.wireOp",EDGE,"E5.24.10.0")}),1.0]])]});
            var Q344;
            Q344=makeQuery(id+"F7.imprint","IMPRINT",FACE,{"disambiguationData":[TD([[makeQuery(id+"F7.imprint","IMPRINT",EDGE,{"derivedFrom":sQuery(id+"F7.wireOp",EDGE,"E5.2.4.0")}),1.0]])]});
            var Q345;
            Q345=makeQuery(id+"F7.imprint","IMPRINT",FACE,{"disambiguationData":[TD([[makeQuery(id+"F7.imprint","IMPRINT",EDGE,{"derivedFrom":sQuery(id+"F7.wireOp",EDGE,"E5.1.19.0")}),1.0]])]});
            var Q346;
            Q346=makeQuery(id+"F7.imprint","IMPRINT",FACE,{"disambiguationData":[TD([[makeQuery(id+"F7.imprint","IMPRINT",EDGE,{"derivedFrom":sQuery(id+"F7.wireOp",EDGE,"E5.1.3.0")}),1.0]])]});
            var Q347;
            Q347=makeQuery(id+"F7.imprint","IMPRINT",FACE,{"disambiguationData":[TD([[makeQuery(id+"F7.imprint","IMPRINT",EDGE,{"derivedFrom":sQuery(id+"F7.wireOp",EDGE,"E5.4.6.0")}),1.0]])]});
            var Q348;
            Q348=makeQuery(id+"F7.imprint","IMPRINT",FACE,{"disambiguationData":[TD([[makeQuery(id+"F7.imprint","IMPRINT",EDGE,{"derivedFrom":sQuery(id+"F7.wireOp",EDGE,"E5.3.21.0")}),1.0]])]});
            var Q349;
            Q349=makeQuery(id+"F7.imprint","IMPRINT",FACE,{"disambiguationData":[TD([[makeQuery(id+"F7.imprint","IMPRINT",EDGE,{"derivedFrom":sQuery(id+"F7.wireOp",EDGE,"E5.3.5.0")}),1.0]])]});
            var Q350;
            Q350=makeQuery(id+"F7.imprint","IMPRINT",FACE,{"disambiguationData":[TD([[makeQuery(id+"F7.imprint","IMPRINT",EDGE,{"derivedFrom":sQuery(id+"F7.wireOp",EDGE,"E5.2.20.0")}),1.0]])]});
            var Q351;
            Q351=makeQuery(id+"F7.imprint","IMPRINT",FACE,{"disambiguationData":[TD([[makeQuery(id+"F7.imprint","IMPRINT",EDGE,{"derivedFrom":sQuery(id+"F7.wireOp",EDGE,"E5.6.8.0")}),1.0]])]});
            var Q352;
            Q352=makeQuery(id+"F7.imprint","IMPRINT",FACE,{"disambiguationData":[TD([[makeQuery(id+"F7.imprint","IMPRINT",EDGE,{"derivedFrom":sQuery(id+"F7.wireOp",EDGE,"E5.5.23.0")}),1.0]])]});
            var Q353;
            Q353=makeQuery(id+"F7.imprint","IMPRINT",FACE,{"disambiguationData":[TD([[makeQuery(id+"F7.imprint","IMPRINT",EDGE,{"derivedFrom":sQuery(id+"F7.wireOp",EDGE,"E5.5.7.0")}),1.0]])]});
            var Q354;
            Q354=makeQuery(id+"F7.imprint","IMPRINT",FACE,{"disambiguationData":[TD([[makeQuery(id+"F7.imprint","IMPRINT",EDGE,{"derivedFrom":sQuery(id+"F7.wireOp",EDGE,"E5.4.22.0")}),1.0]])]});
            var Q355;
            Q355=makeQuery(id+"F7.imprint","IMPRINT",FACE,{"disambiguationData":[TD([[makeQuery(id+"F7.imprint","IMPRINT",EDGE,{"derivedFrom":sQuery(id+"F7.wireOp",EDGE,"E5.8.10.0")}),1.0]])]});
            var Q356;
            Q356=makeQuery(id+"F7.imprint","IMPRINT",FACE,{"disambiguationData":[TD([[makeQuery(id+"F7.imprint","IMPRINT",EDGE,{"derivedFrom":sQuery(id+"F7.wireOp",EDGE,"E5.7.25.0")}),1.0]])]});
            var Q357;
            Q357=makeQuery(id+"F7.imprint","IMPRINT",FACE,{"disambiguationData":[TD([[makeQuery(id+"F7.imprint","IMPRINT",EDGE,{"derivedFrom":sQuery(id+"F7.wireOp",EDGE,"E5.7.9.0")}),1.0]])]});
            var Q358;
            Q358=makeQuery(id+"F7.imprint","IMPRINT",FACE,{"disambiguationData":[TD([[makeQuery(id+"F7.imprint","IMPRINT",EDGE,{"derivedFrom":sQuery(id+"F7.wireOp",EDGE,"E5.6.24.0")}),1.0]])]});
            var Q359;
            Q359=makeQuery(id+"F7.imprint","IMPRINT",FACE,{"disambiguationData":[TD([[makeQuery(id+"F7.imprint","IMPRINT",EDGE,{"derivedFrom":sQuery(id+"F7.wireOp",EDGE,"E5.10.12.0")}),1.0]])]});
            var Q360;
            Q360=makeQuery(id+"F7.imprint","IMPRINT",FACE,{"disambiguationData":[TD([[makeQuery(id+"F7.imprint","IMPRINT",EDGE,{"derivedFrom":sQuery(id+"F7.wireOp",EDGE,"E5.9.27.0")}),1.0]])]});
            var Q361;
            Q361=makeQuery(id+"F7.imprint","IMPRINT",FACE,{"disambiguationData":[TD([[makeQuery(id+"F7.imprint","IMPRINT",EDGE,{"derivedFrom":sQuery(id+"F7.wireOp",EDGE,"E5.9.11.0")}),1.0]])]});
            var Q362;
            Q362=makeQuery(id+"F7.imprint","IMPRINT",FACE,{"disambiguationData":[TD([[makeQuery(id+"F7.imprint","IMPRINT",EDGE,{"derivedFrom":sQuery(id+"F7.wireOp",EDGE,"E5.8.26.0")}),1.0]])]});
            var Q363;
            Q363=makeQuery(id+"F7.imprint","IMPRINT",FACE,{"disambiguationData":[TD([[makeQuery(id+"F7.imprint","IMPRINT",EDGE,{"derivedFrom":sQuery(id+"F7.wireOp",EDGE,"E5.12.14.0")}),1.0]])]});
            var Q364;
            Q364=makeQuery(id+"F7.imprint","IMPRINT",FACE,{"disambiguationData":[TD([[makeQuery(id+"F7.imprint","IMPRINT",EDGE,{"derivedFrom":sQuery(id+"F7.wireOp",EDGE,"E5.11.29.0")}),1.0]])]});
            var Q365;
            Q365=makeQuery(id+"F7.imprint","IMPRINT",FACE,{"disambiguationData":[TD([[makeQuery(id+"F7.imprint","IMPRINT",EDGE,{"derivedFrom":sQuery(id+"F7.wireOp",EDGE,"E5.11.13.0")}),1.0]])]});
            var Q366;
            Q366=makeQuery(id+"F7.imprint","IMPRINT",FACE,{"disambiguationData":[TD([[makeQuery(id+"F7.imprint","IMPRINT",EDGE,{"derivedFrom":sQuery(id+"F7.wireOp",EDGE,"E5.10.28.0")}),1.0]])]});
            var Q367;
            Q367=makeQuery(id+"F7.imprint","IMPRINT",FACE,{"disambiguationData":[TD([[makeQuery(id+"F7.imprint","IMPRINT",EDGE,{"derivedFrom":sQuery(id+"F7.wireOp",EDGE,"E5.32.3.0")}),1.0]])]});
            var Q368;
            Q368=makeQuery(id+"F7.imprint","IMPRINT",FACE,{"disambiguationData":[TD([[makeQuery(id+"F7.imprint","IMPRINT",EDGE,{"derivedFrom":sQuery(id+"F7.wireOp",EDGE,"E5.27.14.0")}),1.0]])]});
            var Q369;
            Q369=makeQuery(id+"F7.imprint","IMPRINT",FACE,{"disambiguationData":[TD([[makeQuery(id+"F7.imprint","IMPRINT",EDGE,{"derivedFrom":sQuery(id+"F7.wireOp",EDGE,"E5.26.29.0")}),1.0]])]});
            var Q370;
            Q370=makeQuery(id+"F7.imprint","IMPRINT",FACE,{"disambiguationData":[TD([[makeQuery(id+"F7.imprint","IMPRINT",EDGE,{"derivedFrom":sQuery(id+"F7.wireOp",EDGE,"E5.32.19.0")}),1.0]])]});
            var Q371;
            Q371=makeQuery(id+"F7.imprint","IMPRINT",FACE,{"disambiguationData":[TD([[makeQuery(id+"F7.imprint","IMPRINT",EDGE,{"derivedFrom":sQuery(id+"F7.wireOp",EDGE,"E5.29.16.0")}),1.0]])]});
            var Q372;
            Q372=makeQuery(id+"F7.imprint","IMPRINT",FACE,{"disambiguationData":[TD([[makeQuery(id+"F7.imprint","IMPRINT",EDGE,{"derivedFrom":sQuery(id+"F7.wireOp",EDGE,"E5.28.15.0")}),1.0]])]});
            var Q373;
            Q373=makeQuery(id+"F7.imprint","IMPRINT",FACE,{"disambiguationData":[TD([[makeQuery(id+"F7.imprint","IMPRINT",EDGE,{"derivedFrom":sQuery(id+"F7.wireOp",EDGE,"E5.31.18.0")}),1.0]])]});
            var Q374;
            Q374=makeQuery(id+"F7.imprint","IMPRINT",FACE,{"disambiguationData":[TD([[makeQuery(id+"F7.imprint","IMPRINT",EDGE,{"derivedFrom":sQuery(id+"F7.wireOp",EDGE,"E5.31.2.0")}),1.0]])]});
            var Q375;
            Q375=makeQuery(id+"F7.imprint","IMPRINT",FACE,{"disambiguationData":[TD([[makeQuery(id+"F7.imprint","IMPRINT",EDGE,{"derivedFrom":sQuery(id+"F7.wireOp",EDGE,"E5.30.17.0")}),1.0]])]});
            var Q376;
            Q376=makeQuery(id+"F7.imprint","IMPRINT",FACE,{"disambiguationData":[TD([[makeQuery(id+"F7.imprint","IMPRINT",EDGE,{"derivedFrom":sQuery(id+"F7.wireOp",EDGE,"E5.30.1.0")}),1.0]])]});
            var Q377;
            Q377=makeQuery(id+"F7.imprint","IMPRINT",FACE,{"disambiguationData":[TD([[makeQuery(id+"F7.imprint","IMPRINT",EDGE,{"derivedFrom":sQuery(id+"F7.wireOp",EDGE,"E5.26.12.0")}),1.0]])]});
            var Q378;
            Q378=makeQuery(id+"F7.imprint","IMPRINT",FACE,{"disambiguationData":[TD([[makeQuery(id+"F7.imprint","IMPRINT",EDGE,{"derivedFrom":sQuery(id+"F7.wireOp",EDGE,"E5.33.8.0")}),1.0]])]});
            var Q379;
            Q379=makeQuery(id+"F7.imprint","IMPRINT",FACE,{"disambiguationData":[TD([[makeQuery(id+"F7.imprint","IMPRINT",EDGE,{"derivedFrom":sQuery(id+"F7.wireOp",EDGE,"E5.13.16.0")}),1.0]])]});
            var Q380;
            Q380=makeQuery(id+"F7.imprint","IMPRINT",FACE,{"disambiguationData":[TD([[makeQuery(id+"F7.imprint","IMPRINT",EDGE,{"derivedFrom":sQuery(id+"F7.wireOp",EDGE,"E5.15.18.0")}),1.0]])]});
            var Q381;
            Q381=makeQuery(id+"F7.imprint","IMPRINT",FACE,{"disambiguationData":[TD([[makeQuery(id+"F7.imprint","IMPRINT",EDGE,{"derivedFrom":sQuery(id+"F7.wireOp",EDGE,"E5.15.2.0")}),1.0]])]});
            var Q382;
            Q382=makeQuery(id+"F7.imprint","IMPRINT",FACE,{"disambiguationData":[TD([[makeQuery(id+"F7.imprint","IMPRINT",EDGE,{"derivedFrom":sQuery(id+"F7.wireOp",EDGE,"E5.14.17.0")}),1.0]])]});
            var Q383;
            Q383=makeQuery(id+"F7.imprint","IMPRINT",FACE,{"disambiguationData":[TD([[makeQuery(id+"F7.imprint","IMPRINT",EDGE,{"derivedFrom":sQuery(id+"F7.wireOp",EDGE,"E5.17.20.0")}),1.0]])]});
            var Q384;
            Q384=makeQuery(id+"F7.imprint","IMPRINT",FACE,{"disambiguationData":[TD([[makeQuery(id+"F7.imprint","IMPRINT",EDGE,{"derivedFrom":sQuery(id+"F7.wireOp",EDGE,"E5.17.4.0")}),1.0]])]});
            var Q385;
            Q385=makeQuery(id+"F7.imprint","IMPRINT",FACE,{"disambiguationData":[TD([[makeQuery(id+"F7.imprint","IMPRINT",EDGE,{"derivedFrom":sQuery(id+"F7.wireOp",EDGE,"E5.16.19.0")}),1.0]])]});
            var Q386;
            Q386=makeQuery(id+"F7.imprint","IMPRINT",FACE,{"disambiguationData":[TD([[makeQuery(id+"F7.imprint","IMPRINT",EDGE,{"derivedFrom":sQuery(id+"F7.wireOp",EDGE,"E5.16.3.0")}),1.0]])]});
            var Q387;
            Q387=makeQuery(id+"F7.imprint","IMPRINT",FACE,{"disambiguationData":[TD([[makeQuery(id+"F7.imprint","IMPRINT",EDGE,{"derivedFrom":sQuery(id+"F7.wireOp",EDGE,"E5.19.22.0")}),1.0]])]});
            var Q388;
            Q388=makeQuery(id+"F7.imprint","IMPRINT",FACE,{"disambiguationData":[TD([[makeQuery(id+"F7.imprint","IMPRINT",EDGE,{"derivedFrom":sQuery(id+"F7.wireOp",EDGE,"E5.19.6.0")}),1.0]])]});
            var Q389;
            Q389=makeQuery(id+"F7.imprint","IMPRINT",FACE,{"disambiguationData":[TD([[makeQuery(id+"F7.imprint","IMPRINT",EDGE,{"derivedFrom":sQuery(id+"F7.wireOp",EDGE,"E5.21.24.0")}),1.0]])]});
            var Q390;
            Q390=makeQuery(id+"F7.imprint","IMPRINT",FACE,{"disambiguationData":[TD([[makeQuery(id+"F7.imprint","IMPRINT",EDGE,{"derivedFrom":sQuery(id+"F7.wireOp",EDGE,"E5.21.8.0")}),1.0]])]});
            var Q391;
            Q391=makeQuery(id+"F7.imprint","IMPRINT",FACE,{"disambiguationData":[TD([[makeQuery(id+"F7.imprint","IMPRINT",EDGE,{"derivedFrom":sQuery(id+"F7.wireOp",EDGE,"E5.20.23.0")}),1.0]])]});
            var Q392;
            Q392=makeQuery(id+"F7.imprint","IMPRINT",FACE,{"disambiguationData":[TD([[makeQuery(id+"F7.imprint","IMPRINT",EDGE,{"derivedFrom":sQuery(id+"F7.wireOp",EDGE,"E5.20.7.0")}),1.0]])]});
            var Q393;
            Q393=makeQuery(id+"F7.imprint","IMPRINT",FACE,{"disambiguationData":[TD([[makeQuery(id+"F7.imprint","IMPRINT",EDGE,{"derivedFrom":sQuery(id+"F7.wireOp",EDGE,"E5.23.10.0")}),1.0]])]});
            var Q394;
            Q394=makeQuery(id+"F7.imprint","IMPRINT",FACE,{"disambiguationData":[TD([[makeQuery(id+"F7.imprint","IMPRINT",EDGE,{"derivedFrom":sQuery(id+"F7.wireOp",EDGE,"E5.22.25.0")}),1.0]])]});
            var Q395;
            Q395=makeQuery(id+"F7.imprint","IMPRINT",FACE,{"disambiguationData":[TD([[makeQuery(id+"F7.imprint","IMPRINT",EDGE,{"derivedFrom":sQuery(id+"F7.wireOp",EDGE,"E5.22.9.0")}),1.0]])]});
            var Q396;
            Q396=makeQuery(id+"F7.imprint","IMPRINT",FACE,{"disambiguationData":[TD([[makeQuery(id+"F7.imprint","IMPRINT",EDGE,{"derivedFrom":sQuery(id+"F7.wireOp",EDGE,"E5.25.28.0")}),1.0]])]});
            var Q397;
            Q397=makeQuery(id+"F7.imprint","IMPRINT",FACE,{"disambiguationData":[TD([[makeQuery(id+"F7.imprint","IMPRINT",EDGE,{"derivedFrom":sQuery(id+"F7.wireOp",EDGE,"E5.25.12.0")}),1.0]])]});
            var Q398;
            Q398=makeQuery(id+"F7.imprint","IMPRINT",FACE,{"disambiguationData":[TD([[makeQuery(id+"F7.imprint","IMPRINT",EDGE,{"derivedFrom":sQuery(id+"F7.wireOp",EDGE,"E5.24.27.0")}),1.0]])]});
            var Q399;
            Q399=makeQuery(id+"F7.imprint","IMPRINT",FACE,{"disambiguationData":[TD([[makeQuery(id+"F7.imprint","IMPRINT",EDGE,{"derivedFrom":sQuery(id+"F7.wireOp",EDGE,"E5.24.11.0")}),1.0]])]});
            var Q400;
            Q400=makeQuery(id+"F7.imprint","IMPRINT",FACE,{"disambiguationData":[TD([[makeQuery(id+"F7.imprint","IMPRINT",EDGE,{"derivedFrom":sQuery(id+"F7.wireOp",EDGE,"E5.26.13.0")}),1.0]])]});
            var Q401;
            Q401=makeQuery(id+"F7.imprint","IMPRINT",FACE,{"disambiguationData":[TD([[makeQuery(id+"F7.imprint","IMPRINT",EDGE,{"derivedFrom":sQuery(id+"F7.wireOp",EDGE,"E5.2.5.0")}),1.0]])]});
            var Q402;
            Q402=makeQuery(id+"F7.imprint","IMPRINT",FACE,{"disambiguationData":[TD([[makeQuery(id+"F7.imprint","IMPRINT",EDGE,{"derivedFrom":sQuery(id+"F7.wireOp",EDGE,"E5.1.20.0")}),1.0]])]});
            var Q403;
            Q403=makeQuery(id+"F7.imprint","IMPRINT",FACE,{"disambiguationData":[TD([[makeQuery(id+"F7.imprint","IMPRINT",EDGE,{"derivedFrom":sQuery(id+"F7.wireOp",EDGE,"E5.1.4.0")}),1.0]])]});
            var Q404;
            Q404=makeQuery(id+"F7.imprint","IMPRINT",FACE,{"disambiguationData":[TD([[makeQuery(id+"F7.imprint","IMPRINT",EDGE,{"derivedFrom":sQuery(id+"F7.wireOp",EDGE,"E5.4.7.0")}),1.0]])]});
            var Q405;
            Q405=makeQuery(id+"F7.imprint","IMPRINT",FACE,{"disambiguationData":[TD([[makeQuery(id+"F7.imprint","IMPRINT",EDGE,{"derivedFrom":sQuery(id+"F7.wireOp",EDGE,"E5.3.22.0")}),1.0]])]});
            var Q406;
            Q406=makeQuery(id+"F7.imprint","IMPRINT",FACE,{"disambiguationData":[TD([[makeQuery(id+"F7.imprint","IMPRINT",EDGE,{"derivedFrom":sQuery(id+"F7.wireOp",EDGE,"E5.3.6.0")}),1.0]])]});
            var Q407;
            Q407=makeQuery(id+"F7.imprint","IMPRINT",FACE,{"disambiguationData":[TD([[makeQuery(id+"F7.imprint","IMPRINT",EDGE,{"derivedFrom":sQuery(id+"F7.wireOp",EDGE,"E5.6.9.0")}),1.0]])]});
            var Q408;
            Q408=makeQuery(id+"F7.imprint","IMPRINT",FACE,{"disambiguationData":[TD([[makeQuery(id+"F7.imprint","IMPRINT",EDGE,{"derivedFrom":sQuery(id+"F7.wireOp",EDGE,"E5.5.24.0")}),1.0]])]});
            var Q409;
            Q409=makeQuery(id+"F7.imprint","IMPRINT",FACE,{"disambiguationData":[TD([[makeQuery(id+"F7.imprint","IMPRINT",EDGE,{"derivedFrom":sQuery(id+"F7.wireOp",EDGE,"E5.5.8.0")}),1.0]])]});
            var Q410;
            Q410=makeQuery(id+"F7.imprint","IMPRINT",FACE,{"disambiguationData":[TD([[makeQuery(id+"F7.imprint","IMPRINT",EDGE,{"derivedFrom":sQuery(id+"F7.wireOp",EDGE,"E5.4.23.0")}),1.0]])]});
            var Q411;
            Q411=makeQuery(id+"F7.imprint","IMPRINT",FACE,{"disambiguationData":[TD([[makeQuery(id+"F7.imprint","IMPRINT",EDGE,{"derivedFrom":sQuery(id+"F7.wireOp",EDGE,"E5.8.11.0")}),1.0]])]});
            var Q412;
            Q412=makeQuery(id+"F7.imprint","IMPRINT",FACE,{"disambiguationData":[TD([[makeQuery(id+"F7.imprint","IMPRINT",EDGE,{"derivedFrom":sQuery(id+"F7.wireOp",EDGE,"E5.7.26.0")}),1.0]])]});
            var Q413;
            Q413=makeQuery(id+"F7.imprint","IMPRINT",FACE,{"disambiguationData":[TD([[makeQuery(id+"F7.imprint","IMPRINT",EDGE,{"derivedFrom":sQuery(id+"F7.wireOp",EDGE,"E5.7.10.0")}),1.0]])]});
            var Q414;
            Q414=makeQuery(id+"F7.imprint","IMPRINT",FACE,{"disambiguationData":[TD([[makeQuery(id+"F7.imprint","IMPRINT",EDGE,{"derivedFrom":sQuery(id+"F7.wireOp",EDGE,"E5.6.25.0")}),1.0]])]});
            var Q415;
            Q415=makeQuery(id+"F7.imprint","IMPRINT",FACE,{"disambiguationData":[TD([[makeQuery(id+"F7.imprint","IMPRINT",EDGE,{"derivedFrom":sQuery(id+"F7.wireOp",EDGE,"E5.10.13.0")}),1.0]])]});
            var Q416;
            Q416=makeQuery(id+"F7.imprint","IMPRINT",FACE,{"disambiguationData":[TD([[makeQuery(id+"F7.imprint","IMPRINT",EDGE,{"derivedFrom":sQuery(id+"F7.wireOp",EDGE,"E5.9.28.0")}),1.0]])]});
            var Q417;
            Q417=makeQuery(id+"F7.imprint","IMPRINT",FACE,{"disambiguationData":[TD([[makeQuery(id+"F7.imprint","IMPRINT",EDGE,{"derivedFrom":sQuery(id+"F7.wireOp",EDGE,"E5.9.12.0")}),1.0]])]});
            var Q418;
            Q418=makeQuery(id+"F7.imprint","IMPRINT",FACE,{"disambiguationData":[TD([[makeQuery(id+"F7.imprint","IMPRINT",EDGE,{"derivedFrom":sQuery(id+"F7.wireOp",EDGE,"E5.8.27.0")}),1.0]])]});
            var Q419;
            Q419=makeQuery(id+"F7.imprint","IMPRINT",FACE,{"disambiguationData":[TD([[makeQuery(id+"F7.imprint","IMPRINT",EDGE,{"derivedFrom":sQuery(id+"F7.wireOp",EDGE,"E5.12.15.0")}),1.0]])]});
            var Q420;
            Q420=makeQuery(id+"F7.imprint","IMPRINT",FACE,{"disambiguationData":[TD([[makeQuery(id+"F7.imprint","IMPRINT",EDGE,{"derivedFrom":sQuery(id+"F7.wireOp",EDGE,"E5.11.14.0")}),1.0]])]});
            var Q421;
            Q421=makeQuery(id+"F7.imprint","IMPRINT",FACE,{"disambiguationData":[TD([[makeQuery(id+"F7.imprint","IMPRINT",EDGE,{"derivedFrom":sQuery(id+"F7.wireOp",EDGE,"E5.10.29.0")}),1.0]])]});
            var Q422;
            Q422=makeQuery(id+"F7.imprint","IMPRINT",FACE,{"disambiguationData":[TD([[makeQuery(id+"F7.imprint","IMPRINT",EDGE,{"derivedFrom":sQuery(id+"F7.wireOp",EDGE,"E5.32.4.0")}),1.0]])]});
            var Q423;
            Q423=makeQuery(id+"F7.imprint","IMPRINT",FACE,{"disambiguationData":[TD([[makeQuery(id+"F7.imprint","IMPRINT",EDGE,{"derivedFrom":sQuery(id+"F7.wireOp",EDGE,"E5.27.15.0")}),1.0]])]});
            var Q424;
            Q424=makeQuery(id+"F7.imprint","IMPRINT",FACE,{"disambiguationData":[TD([[makeQuery(id+"F7.imprint","IMPRINT",EDGE,{"derivedFrom":sQuery(id+"F7.wireOp",EDGE,"E5.32.20.0")}),1.0]])]});
            var Q425;
            Q425=makeQuery(id+"F7.imprint","IMPRINT",FACE,{"disambiguationData":[TD([[makeQuery(id+"F7.imprint","IMPRINT",EDGE,{"derivedFrom":sQuery(id+"F7.wireOp",EDGE,"E5.29.17.0")}),1.0]])]});
            var Q426;
            Q426=makeQuery(id+"F7.imprint","IMPRINT",FACE,{"disambiguationData":[TD([[makeQuery(id+"F7.imprint","IMPRINT",EDGE,{"derivedFrom":sQuery(id+"F7.wireOp",EDGE,"E5.29.1.0")}),1.0]])]});
            var Q427;
            Q427=makeQuery(id+"F7.imprint","IMPRINT",FACE,{"disambiguationData":[TD([[makeQuery(id+"F7.imprint","IMPRINT",EDGE,{"derivedFrom":sQuery(id+"F7.wireOp",EDGE,"E5.28.16.0")}),1.0]])]});
            var Q428;
            Q428=makeQuery(id+"F7.imprint","IMPRINT",FACE,{"disambiguationData":[TD([[makeQuery(id+"F7.imprint","IMPRINT",EDGE,{"derivedFrom":sQuery(id+"F7.wireOp",EDGE,"E5.31.19.0")}),1.0]])]});
            var Q429;
            Q429=makeQuery(id+"F7.imprint","IMPRINT",FACE,{"disambiguationData":[TD([[makeQuery(id+"F7.imprint","IMPRINT",EDGE,{"derivedFrom":sQuery(id+"F7.wireOp",EDGE,"E5.31.3.0")}),1.0]])]});
            var Q430;
            Q430=makeQuery(id+"F7.imprint","IMPRINT",FACE,{"disambiguationData":[TD([[makeQuery(id+"F7.imprint","IMPRINT",EDGE,{"derivedFrom":sQuery(id+"F7.wireOp",EDGE,"E5.30.18.0")}),1.0]])]});
            var Q431;
            Q431=makeQuery(id+"F7.imprint","IMPRINT",FACE,{"disambiguationData":[TD([[makeQuery(id+"F7.imprint","IMPRINT",EDGE,{"derivedFrom":sQuery(id+"F7.wireOp",EDGE,"E5.30.2.0")}),1.0]])]});
            var Q432;
            Q432=makeQuery(id+"F7.imprint","IMPRINT",FACE,{"disambiguationData":[TD([[makeQuery(id+"F7.imprint","IMPRINT",EDGE,{"derivedFrom":sQuery(id+"F7.wireOp",EDGE,"E5.15.19.0")}),1.0]])]});
            var Q433;
            Q433=makeQuery(id+"F7.imprint","IMPRINT",FACE,{"disambiguationData":[TD([[makeQuery(id+"F7.imprint","IMPRINT",EDGE,{"derivedFrom":sQuery(id+"F7.wireOp",EDGE,"E5.15.3.0")}),1.0]])]});
            var Q434;
            Q434=makeQuery(id+"F7.imprint","IMPRINT",FACE,{"disambiguationData":[TD([[makeQuery(id+"F7.imprint","IMPRINT",EDGE,{"derivedFrom":sQuery(id+"F7.wireOp",EDGE,"E5.14.18.0")}),1.0]])]});
            var Q435;
            Q435=makeQuery(id+"F7.imprint","IMPRINT",FACE,{"disambiguationData":[TD([[makeQuery(id+"F7.imprint","IMPRINT",EDGE,{"derivedFrom":sQuery(id+"F7.wireOp",EDGE,"E5.14.2.0")}),1.0]])]});
            var Q436;
            Q436=makeQuery(id+"F7.imprint","IMPRINT",FACE,{"disambiguationData":[TD([[makeQuery(id+"F7.imprint","IMPRINT",EDGE,{"derivedFrom":sQuery(id+"F7.wireOp",EDGE,"E5.17.21.0")}),1.0]])]});
            var Q437;
            Q437=makeQuery(id+"F7.imprint","IMPRINT",FACE,{"disambiguationData":[TD([[makeQuery(id+"F7.imprint","IMPRINT",EDGE,{"derivedFrom":sQuery(id+"F7.wireOp",EDGE,"E5.17.5.0")}),1.0]])]});
            var Q438;
            Q438=makeQuery(id+"F7.imprint","IMPRINT",FACE,{"disambiguationData":[TD([[makeQuery(id+"F7.imprint","IMPRINT",EDGE,{"derivedFrom":sQuery(id+"F7.wireOp",EDGE,"E5.16.20.0")}),1.0]])]});
            var Q439;
            Q439=makeQuery(id+"F7.imprint","IMPRINT",FACE,{"disambiguationData":[TD([[makeQuery(id+"F7.imprint","IMPRINT",EDGE,{"derivedFrom":sQuery(id+"F7.wireOp",EDGE,"E5.16.4.0")}),1.0]])]});
            var Q440;
            Q440=makeQuery(id+"F7.imprint","IMPRINT",FACE,{"disambiguationData":[TD([[makeQuery(id+"F7.imprint","IMPRINT",EDGE,{"derivedFrom":sQuery(id+"F7.wireOp",EDGE,"E5.19.23.0")}),1.0]])]});
            var Q441;
            Q441=makeQuery(id+"F7.imprint","IMPRINT",FACE,{"disambiguationData":[TD([[makeQuery(id+"F7.imprint","IMPRINT",EDGE,{"derivedFrom":sQuery(id+"F7.wireOp",EDGE,"E5.19.7.0")}),1.0]])]});
            var Q442;
            Q442=makeQuery(id+"F7.imprint","IMPRINT",FACE,{"disambiguationData":[TD([[makeQuery(id+"F7.imprint","IMPRINT",EDGE,{"derivedFrom":sQuery(id+"F7.wireOp",EDGE,"E5.18.22.0")}),1.0]])]});
            var Q443;
            Q443=makeQuery(id+"F7.imprint","IMPRINT",FACE,{"disambiguationData":[TD([[makeQuery(id+"F7.imprint","IMPRINT",EDGE,{"derivedFrom":sQuery(id+"F7.wireOp",EDGE,"E5.21.25.0")}),1.0]])]});
            var Q444;
            Q444=makeQuery(id+"F7.imprint","IMPRINT",FACE,{"disambiguationData":[TD([[makeQuery(id+"F7.imprint","IMPRINT",EDGE,{"derivedFrom":sQuery(id+"F7.wireOp",EDGE,"E5.21.9.0")}),1.0]])]});
            var Q445;
            Q445=makeQuery(id+"F7.imprint","IMPRINT",FACE,{"disambiguationData":[TD([[makeQuery(id+"F7.imprint","IMPRINT",EDGE,{"derivedFrom":sQuery(id+"F7.wireOp",EDGE,"E5.20.24.0")}),1.0]])]});
            var Q446;
            Q446=makeQuery(id+"F7.imprint","IMPRINT",FACE,{"disambiguationData":[TD([[makeQuery(id+"F7.imprint","IMPRINT",EDGE,{"derivedFrom":sQuery(id+"F7.wireOp",EDGE,"E5.20.8.0")}),1.0]])]});
            var Q447;
            Q447=makeQuery(id+"F7.imprint","IMPRINT",FACE,{"disambiguationData":[TD([[makeQuery(id+"F7.imprint","IMPRINT",EDGE,{"derivedFrom":sQuery(id+"F7.wireOp",EDGE,"E5.23.27.0")}),1.0]])]});
            var Q448;
            Q448=makeQuery(id+"F7.imprint","IMPRINT",FACE,{"disambiguationData":[TD([[makeQuery(id+"F7.imprint","IMPRINT",EDGE,{"derivedFrom":sQuery(id+"F7.wireOp",EDGE,"E5.23.11.0")}),1.0]])]});
            var Q449;
            Q449=makeQuery(id+"F7.imprint","IMPRINT",FACE,{"disambiguationData":[TD([[makeQuery(id+"F7.imprint","IMPRINT",EDGE,{"derivedFrom":sQuery(id+"F7.wireOp",EDGE,"E5.25.29.0")}),1.0]])]});
            var Q450;
            Q450=makeQuery(id+"F7.imprint","IMPRINT",FACE,{"disambiguationData":[TD([[makeQuery(id+"F7.imprint","IMPRINT",EDGE,{"derivedFrom":sQuery(id+"F7.wireOp",EDGE,"E5.25.13.0")}),1.0]])]});
            var Q451;
            Q451=makeQuery(id+"F7.imprint","IMPRINT",FACE,{"disambiguationData":[TD([[makeQuery(id+"F7.imprint","IMPRINT",EDGE,{"derivedFrom":sQuery(id+"F7.wireOp",EDGE,"E5.24.28.0")}),1.0]])]});
            var Q452;
            Q452=makeQuery(id+"F7.imprint","IMPRINT",FACE,{"disambiguationData":[TD([[makeQuery(id+"F7.imprint","IMPRINT",EDGE,{"derivedFrom":sQuery(id+"F7.wireOp",EDGE,"E5.24.12.0")}),1.0]])]});
            var Q453;
            Q453=makeQuery(id+"F7.imprint","IMPRINT",FACE,{"disambiguationData":[TD([[makeQuery(id+"F7.imprint","IMPRINT",EDGE,{"derivedFrom":sQuery(id+"F7.wireOp",EDGE,"E5.26.14.0")}),1.0]])]});
            var Q454;
            Q454=makeQuery(id+"F7.imprint","IMPRINT",FACE,{"disambiguationData":[TD([[makeQuery(id+"F7.imprint","IMPRINT",EDGE,{"derivedFrom":sQuery(id+"F7.wireOp",EDGE,"E5.2.6.0")}),1.0]])]});
            var Q455;
            Q455=makeQuery(id+"F7.imprint","IMPRINT",FACE,{"disambiguationData":[TD([[makeQuery(id+"F7.imprint","IMPRINT",EDGE,{"derivedFrom":sQuery(id+"F7.wireOp",EDGE,"E5.4.8.0")}),1.0]])]});
            var Q456;
            Q456=makeQuery(id+"F7.imprint","IMPRINT",FACE,{"disambiguationData":[TD([[makeQuery(id+"F7.imprint","IMPRINT",EDGE,{"derivedFrom":sQuery(id+"F7.wireOp",EDGE,"E5.3.23.0")}),1.0]])]});
            var Q457;
            Q457=makeQuery(id+"F7.imprint","IMPRINT",FACE,{"disambiguationData":[TD([[makeQuery(id+"F7.imprint","IMPRINT",EDGE,{"derivedFrom":sQuery(id+"F7.wireOp",EDGE,"E5.3.7.0")}),1.0]])]});
            var Q458;
            Q458=makeQuery(id+"F7.imprint","IMPRINT",FACE,{"disambiguationData":[TD([[makeQuery(id+"F7.imprint","IMPRINT",EDGE,{"derivedFrom":sQuery(id+"F7.wireOp",EDGE,"E5.2.22.0")}),1.0]])]});
            var Q459;
            Q459=makeQuery(id+"F7.imprint","IMPRINT",FACE,{"disambiguationData":[TD([[makeQuery(id+"F7.imprint","IMPRINT",EDGE,{"derivedFrom":sQuery(id+"F7.wireOp",EDGE,"E5.6.10.0")}),1.0]])]});
            var Q460;
            Q460=makeQuery(id+"F7.imprint","IMPRINT",FACE,{"disambiguationData":[TD([[makeQuery(id+"F7.imprint","IMPRINT",EDGE,{"derivedFrom":sQuery(id+"F7.wireOp",EDGE,"E5.5.25.0")}),1.0]])]});
            var Q461;
            Q461=makeQuery(id+"F7.imprint","IMPRINT",FACE,{"disambiguationData":[TD([[makeQuery(id+"F7.imprint","IMPRINT",EDGE,{"derivedFrom":sQuery(id+"F7.wireOp",EDGE,"E5.5.9.0")}),1.0]])]});
            var Q462;
            Q462=makeQuery(id+"F7.imprint","IMPRINT",FACE,{"disambiguationData":[TD([[makeQuery(id+"F7.imprint","IMPRINT",EDGE,{"derivedFrom":sQuery(id+"F7.wireOp",EDGE,"E5.4.24.0")}),1.0]])]});
            var Q463;
            Q463=makeQuery(id+"F7.imprint","IMPRINT",FACE,{"disambiguationData":[TD([[makeQuery(id+"F7.imprint","IMPRINT",EDGE,{"derivedFrom":sQuery(id+"F7.wireOp",EDGE,"E5.8.12.0")}),1.0]])]});
            var Q464;
            Q464=makeQuery(id+"F7.imprint","IMPRINT",FACE,{"disambiguationData":[TD([[makeQuery(id+"F7.imprint","IMPRINT",EDGE,{"derivedFrom":sQuery(id+"F7.wireOp",EDGE,"E5.7.27.0")}),1.0]])]});
            var Q465;
            Q465=makeQuery(id+"F7.imprint","IMPRINT",FACE,{"disambiguationData":[TD([[makeQuery(id+"F7.imprint","IMPRINT",EDGE,{"derivedFrom":sQuery(id+"F7.wireOp",EDGE,"E5.7.11.0")}),1.0]])]});
            var Q466;
            Q466=makeQuery(id+"F7.imprint","IMPRINT",FACE,{"disambiguationData":[TD([[makeQuery(id+"F7.imprint","IMPRINT",EDGE,{"derivedFrom":sQuery(id+"F7.wireOp",EDGE,"E5.10.14.0")}),1.0]])]});
            var Q467;
            Q467=makeQuery(id+"F7.imprint","IMPRINT",FACE,{"disambiguationData":[TD([[makeQuery(id+"F7.imprint","IMPRINT",EDGE,{"derivedFrom":sQuery(id+"F7.wireOp",EDGE,"E5.9.29.0")}),1.0]])]});
            var Q468;
            Q468=makeQuery(id+"F7.imprint","IMPRINT",FACE,{"disambiguationData":[TD([[makeQuery(id+"F7.imprint","IMPRINT",EDGE,{"derivedFrom":sQuery(id+"F7.wireOp",EDGE,"E5.9.13.0")}),1.0]])]});
            var Q469;
            Q469=makeQuery(id+"F7.imprint","IMPRINT",FACE,{"disambiguationData":[TD([[makeQuery(id+"F7.imprint","IMPRINT",EDGE,{"derivedFrom":sQuery(id+"F7.wireOp",EDGE,"E5.8.28.0")}),1.0]])]});
            var Q470;
            Q470=makeQuery(id+"F7.imprint","IMPRINT",FACE,{"disambiguationData":[TD([[makeQuery(id+"F7.imprint","IMPRINT",EDGE,{"derivedFrom":sQuery(id+"F7.wireOp",EDGE,"E5.12.16.0")}),1.0]])]});
            var Q471;
            Q471=makeQuery(id+"F7.imprint","IMPRINT",FACE,{"disambiguationData":[TD([[makeQuery(id+"F7.imprint","IMPRINT",EDGE,{"derivedFrom":sQuery(id+"F7.wireOp",EDGE,"E5.11.15.0")}),1.0]])]});
            var Q472;
            Q472=makeQuery(id+"F7.imprint","IMPRINT",FACE,{"disambiguationData":[TD([[makeQuery(id+"F7.imprint","IMPRINT",EDGE,{"derivedFrom":sQuery(id+"F7.wireOp",EDGE,"E5.13.1.0")}),1.0]])]});
            var Q473;
            Q473=makeQuery(id+"F7.imprint","IMPRINT",FACE,{"disambiguationData":[TD([[makeQuery(id+"F7.imprint","IMPRINT",EDGE,{"derivedFrom":sQuery(id+"F7.wireOp",EDGE,"E5.13.17.0")}),1.0]])]});
            var Q474;
            Q474=makeQuery(id+"F7.imprint","IMPRINT",FACE,{"disambiguationData":[TD([[makeQuery(id+"F7.imprint","IMPRINT",EDGE,{"derivedFrom":sQuery(id+"F7.wireOp",EDGE,"E5.32.5.0")}),1.0]])]});
            var Q475;
            Q475=makeQuery(id+"F7.imprint","IMPRINT",FACE,{"disambiguationData":[TD([[makeQuery(id+"F7.imprint","IMPRINT",EDGE,{"derivedFrom":sQuery(id+"F7.wireOp",EDGE,"E5.32.21.0")}),1.0]])]});
            var Q476;
            Q476=makeQuery(id+"F7.imprint","IMPRINT",FACE,{"disambiguationData":[TD([[makeQuery(id+"F7.imprint","IMPRINT",EDGE,{"derivedFrom":sQuery(id+"F7.wireOp",EDGE,"E5.29.18.0")}),1.0]])]});
            var Q477;
            Q477=makeQuery(id+"F7.imprint","IMPRINT",FACE,{"disambiguationData":[TD([[makeQuery(id+"F7.imprint","IMPRINT",EDGE,{"derivedFrom":sQuery(id+"F7.wireOp",EDGE,"E5.29.2.0")}),1.0]])]});
            var Q478;
            Q478=makeQuery(id+"F7.imprint","IMPRINT",FACE,{"disambiguationData":[TD([[makeQuery(id+"F7.imprint","IMPRINT",EDGE,{"derivedFrom":sQuery(id+"F7.wireOp",EDGE,"E5.28.17.0")}),1.0]])]});
            var Q479;
            Q479=makeQuery(id+"F7.imprint","IMPRINT",FACE,{"disambiguationData":[TD([[makeQuery(id+"F7.imprint","IMPRINT",EDGE,{"derivedFrom":sQuery(id+"F7.wireOp",EDGE,"E5.28.1.0")}),1.0]])]});
            var Q480;
            Q480=makeQuery(id+"F7.imprint","IMPRINT",FACE,{"disambiguationData":[TD([[makeQuery(id+"F7.imprint","IMPRINT",EDGE,{"derivedFrom":sQuery(id+"F7.wireOp",EDGE,"E5.31.20.0")}),1.0]])]});
            var Q481;
            Q481=makeQuery(id+"F7.imprint","IMPRINT",FACE,{"disambiguationData":[TD([[makeQuery(id+"F7.imprint","IMPRINT",EDGE,{"derivedFrom":sQuery(id+"F7.wireOp",EDGE,"E5.31.4.0")}),1.0]])]});
            var Q482;
            Q482=makeQuery(id+"F7.imprint","IMPRINT",FACE,{"disambiguationData":[TD([[makeQuery(id+"F7.imprint","IMPRINT",EDGE,{"derivedFrom":sQuery(id+"F7.wireOp",EDGE,"E5.30.19.0")}),1.0]])]});
            var Q483;
            Q483=makeQuery(id+"F7.imprint","IMPRINT",FACE,{"disambiguationData":[TD([[makeQuery(id+"F7.imprint","IMPRINT",EDGE,{"derivedFrom":sQuery(id+"F7.wireOp",EDGE,"E5.30.3.0")}),1.0]])]});
            var Q484;
            Q484=makeQuery(id+"F7.imprint","IMPRINT",FACE,{"disambiguationData":[TD([[makeQuery(id+"F7.imprint","IMPRINT",EDGE,{"derivedFrom":sQuery(id+"F7.wireOp",EDGE,"E5.2.7.0")}),1.0]])]});
            var Q485;
            Q485=makeQuery(id+"F7.imprint","IMPRINT",FACE,{"disambiguationData":[TD([[makeQuery(id+"F7.imprint","IMPRINT",EDGE,{"derivedFrom":sQuery(id+"F7.wireOp",EDGE,"E5.1.22.0")}),1.0]])]});
            var Q486;
            Q486=makeQuery(id+"F7.imprint","IMPRINT",FACE,{"disambiguationData":[TD([[makeQuery(id+"F7.imprint","IMPRINT",EDGE,{"derivedFrom":sQuery(id+"F7.wireOp",EDGE,"E5.17.22.0")}),1.0]])]});
            var Q487;
            Q487=makeQuery(id+"F7.imprint","IMPRINT",FACE,{"disambiguationData":[TD([[makeQuery(id+"F7.imprint","IMPRINT",EDGE,{"derivedFrom":sQuery(id+"F7.wireOp",EDGE,"E5.17.6.0")}),1.0]])]});
            var Q488;
            Q488=makeQuery(id+"F7.imprint","IMPRINT",FACE,{"disambiguationData":[TD([[makeQuery(id+"F7.imprint","IMPRINT",EDGE,{"derivedFrom":sQuery(id+"F7.wireOp",EDGE,"E5.16.21.0")}),1.0]])]});
            var Q489;
            Q489=makeQuery(id+"F7.imprint","IMPRINT",FACE,{"disambiguationData":[TD([[makeQuery(id+"F7.imprint","IMPRINT",EDGE,{"derivedFrom":sQuery(id+"F7.wireOp",EDGE,"E5.16.5.0")}),1.0]])]});
            var Q490;
            Q490=makeQuery(id+"F7.imprint","IMPRINT",FACE,{"disambiguationData":[TD([[makeQuery(id+"F7.imprint","IMPRINT",EDGE,{"derivedFrom":sQuery(id+"F7.wireOp",EDGE,"E5.19.24.0")}),1.0]])]});
            var Q491;
            Q491=makeQuery(id+"F7.imprint","IMPRINT",FACE,{"disambiguationData":[TD([[makeQuery(id+"F7.imprint","IMPRINT",EDGE,{"derivedFrom":sQuery(id+"F7.wireOp",EDGE,"E5.19.8.0")}),1.0]])]});
            var Q492;
            Q492=makeQuery(id+"F7.imprint","IMPRINT",FACE,{"disambiguationData":[TD([[makeQuery(id+"F7.imprint","IMPRINT",EDGE,{"derivedFrom":sQuery(id+"F7.wireOp",EDGE,"E5.18.23.0")}),1.0]])]});
            var Q493;
            Q493=makeQuery(id+"F7.imprint","IMPRINT",FACE,{"disambiguationData":[TD([[makeQuery(id+"F7.imprint","IMPRINT",EDGE,{"derivedFrom":sQuery(id+"F7.wireOp",EDGE,"E5.18.7.0")}),1.0]])]});
            var Q494;
            Q494=makeQuery(id+"F7.imprint","IMPRINT",FACE,{"disambiguationData":[TD([[makeQuery(id+"F7.imprint","IMPRINT",EDGE,{"derivedFrom":sQuery(id+"F7.wireOp",EDGE,"E5.21.26.0")}),1.0]])]});
            var Q495;
            Q495=makeQuery(id+"F7.imprint","IMPRINT",FACE,{"disambiguationData":[TD([[makeQuery(id+"F7.imprint","IMPRINT",EDGE,{"derivedFrom":sQuery(id+"F7.wireOp",EDGE,"E5.21.10.0")}),1.0]])]});
            var Q496;
            Q496=makeQuery(id+"F7.imprint","IMPRINT",FACE,{"disambiguationData":[TD([[makeQuery(id+"F7.imprint","IMPRINT",EDGE,{"derivedFrom":sQuery(id+"F7.wireOp",EDGE,"E5.20.25.0")}),1.0]])]});
            var Q497;
            Q497=makeQuery(id+"F7.imprint","IMPRINT",FACE,{"disambiguationData":[TD([[makeQuery(id+"F7.imprint","IMPRINT",EDGE,{"derivedFrom":sQuery(id+"F7.wireOp",EDGE,"E5.20.9.0")}),1.0]])]});
            var Q498;
            Q498=makeQuery(id+"F7.imprint","IMPRINT",FACE,{"disambiguationData":[TD([[makeQuery(id+"F7.imprint","IMPRINT",EDGE,{"derivedFrom":sQuery(id+"F7.wireOp",EDGE,"E5.23.28.0")}),1.0]])]});
            var Q499;
            Q499=makeQuery(id+"F7.imprint","IMPRINT",FACE,{"disambiguationData":[TD([[makeQuery(id+"F7.imprint","IMPRINT",EDGE,{"derivedFrom":sQuery(id+"F7.wireOp",EDGE,"E5.23.12.0")}),1.0]])]});
            var Q500;
            Q500=makeQuery(id+"F7.imprint","IMPRINT",FACE,{"disambiguationData":[TD([[makeQuery(id+"F7.imprint","IMPRINT",EDGE,{"derivedFrom":sQuery(id+"F7.wireOp",EDGE,"E5.22.27.0")}),1.0]])]});
            var Q501;
            Q501=makeQuery(id+"F7.imprint","IMPRINT",FACE,{"disambiguationData":[TD([[makeQuery(id+"F7.imprint","IMPRINT",EDGE,{"derivedFrom":sQuery(id+"F7.wireOp",EDGE,"E5.25.14.0")}),1.0]])]});
            var Q502;
            Q502=makeQuery(id+"F7.imprint","IMPRINT",FACE,{"disambiguationData":[TD([[makeQuery(id+"F7.imprint","IMPRINT",EDGE,{"derivedFrom":sQuery(id+"F7.wireOp",EDGE,"E5.24.29.0")}),1.0]])]});
            var Q503;
            Q503=makeQuery(id+"F7.imprint","IMPRINT",FACE,{"disambiguationData":[TD([[makeQuery(id+"F7.imprint","IMPRINT",EDGE,{"derivedFrom":sQuery(id+"F7.wireOp",EDGE,"E5.24.13.0")}),1.0]])]});
            var Q504;
            Q504=makeQuery(id+"F7.imprint","IMPRINT",FACE,{"disambiguationData":[TD([[makeQuery(id+"F7.imprint","IMPRINT",EDGE,{"derivedFrom":sQuery(id+"F7.wireOp",EDGE,"E5.26.15.0")}),1.0]])]});
            var Q505;
            Q505=makeQuery(id+"F7.imprint","IMPRINT",FACE,{"disambiguationData":[TD([[makeQuery(id+"F7.imprint","IMPRINT",EDGE,{"derivedFrom":sQuery(id+"F7.wireOp",EDGE,"E5.4.9.0")}),1.0]])]});
            var Q506;
            Q506=makeQuery(id+"F7.imprint","IMPRINT",FACE,{"disambiguationData":[TD([[makeQuery(id+"F7.imprint","IMPRINT",EDGE,{"derivedFrom":sQuery(id+"F7.wireOp",EDGE,"E5.3.24.0")}),1.0]])]});
            var Q507;
            Q507=makeQuery(id+"F7.imprint","IMPRINT",FACE,{"disambiguationData":[TD([[makeQuery(id+"F7.imprint","IMPRINT",EDGE,{"derivedFrom":sQuery(id+"F7.wireOp",EDGE,"E5.3.8.0")}),1.0]])]});
            var Q508;
            Q508=makeQuery(id+"F7.imprint","IMPRINT",FACE,{"disambiguationData":[TD([[makeQuery(id+"F7.imprint","IMPRINT",EDGE,{"derivedFrom":sQuery(id+"F7.wireOp",EDGE,"E5.2.23.0")}),1.0]])]});
            var Q509;
            Q509=makeQuery(id+"F7.imprint","IMPRINT",FACE,{"disambiguationData":[TD([[makeQuery(id+"F7.imprint","IMPRINT",EDGE,{"derivedFrom":sQuery(id+"F7.wireOp",EDGE,"E5.5.10.0")}),1.0]])]});
            var Q510;
            Q510=makeQuery(id+"F7.imprint","IMPRINT",FACE,{"disambiguationData":[TD([[makeQuery(id+"F7.imprint","IMPRINT",EDGE,{"derivedFrom":sQuery(id+"F7.wireOp",EDGE,"E5.4.25.0")}),1.0]])]});
            var Q511;
            Q511=makeQuery(id+"F7.imprint","IMPRINT",FACE,{"disambiguationData":[TD([[makeQuery(id+"F7.imprint","IMPRINT",EDGE,{"derivedFrom":sQuery(id+"F7.wireOp",EDGE,"E5.8.13.0")}),1.0]])]});
            var Q512;
            Q512=makeQuery(id+"F7.imprint","IMPRINT",FACE,{"disambiguationData":[TD([[makeQuery(id+"F7.imprint","IMPRINT",EDGE,{"derivedFrom":sQuery(id+"F7.wireOp",EDGE,"E5.7.28.0")}),1.0]])]});
            var Q513;
            Q513=makeQuery(id+"F7.imprint","IMPRINT",FACE,{"disambiguationData":[TD([[makeQuery(id+"F7.imprint","IMPRINT",EDGE,{"derivedFrom":sQuery(id+"F7.wireOp",EDGE,"E5.7.12.0")}),1.0]])]});
            var Q514;
            Q514=makeQuery(id+"F7.imprint","IMPRINT",FACE,{"disambiguationData":[TD([[makeQuery(id+"F7.imprint","IMPRINT",EDGE,{"derivedFrom":sQuery(id+"F7.wireOp",EDGE,"E5.6.27.0")}),1.0]])]});
            var Q515;
            Q515=makeQuery(id+"F7.imprint","IMPRINT",FACE,{"disambiguationData":[TD([[makeQuery(id+"F7.imprint","IMPRINT",EDGE,{"derivedFrom":sQuery(id+"F7.wireOp",EDGE,"E5.9.14.0")}),1.0]])]});
            var Q516;
            Q516=makeQuery(id+"F7.imprint","IMPRINT",FACE,{"disambiguationData":[TD([[makeQuery(id+"F7.imprint","IMPRINT",EDGE,{"derivedFrom":sQuery(id+"F7.wireOp",EDGE,"E5.8.29.0")}),1.0]])]});
            var Q517;
            Q517=makeQuery(id+"F7.imprint","IMPRINT",FACE,{"disambiguationData":[TD([[makeQuery(id+"F7.imprint","IMPRINT",EDGE,{"derivedFrom":sQuery(id+"F7.wireOp",EDGE,"E5.12.17.0")}),1.0]])]});
            var Q518;
            Q518=makeQuery(id+"F7.imprint","IMPRINT",FACE,{"disambiguationData":[TD([[makeQuery(id+"F7.imprint","IMPRINT",EDGE,{"derivedFrom":sQuery(id+"F7.wireOp",EDGE,"E5.12.1.0")}),1.0]])]});
            var Q519;
            Q519=makeQuery(id+"F7.imprint","IMPRINT",FACE,{"disambiguationData":[TD([[makeQuery(id+"F7.imprint","IMPRINT",EDGE,{"derivedFrom":sQuery(id+"F7.wireOp",EDGE,"E5.11.16.0")}),1.0]])]});
            var Q520;
            Q520=makeQuery(id+"F7.imprint","IMPRINT",FACE,{"disambiguationData":[TD([[makeQuery(id+"F7.imprint","IMPRINT",EDGE,{"derivedFrom":sQuery(id+"F7.wireOp",EDGE,"E5.13.2.0")}),1.0]])]});
            var Q521;
            Q521=makeQuery(id+"F7.imprint","IMPRINT",FACE,{"disambiguationData":[TD([[makeQuery(id+"F7.imprint","IMPRINT",EDGE,{"derivedFrom":sQuery(id+"F7.wireOp",EDGE,"E5.13.18.0")}),1.0]])]});
            var Q522;
            Q522=makeQuery(id+"F7.imprint","IMPRINT",FACE,{"disambiguationData":[TD([[makeQuery(id+"F7.imprint","IMPRINT",EDGE,{"derivedFrom":sQuery(id+"F7.wireOp",EDGE,"E5.15.20.0")}),1.0]])]});
            var Q523;
            Q523=makeQuery(id+"F7.imprint","IMPRINT",FACE,{"disambiguationData":[TD([[makeQuery(id+"F7.imprint","IMPRINT",EDGE,{"derivedFrom":sQuery(id+"F7.wireOp",EDGE,"E5.15.4.0")}),1.0]])]});
            var Q524;
            Q524=makeQuery(id+"F7.imprint","IMPRINT",FACE,{"disambiguationData":[TD([[makeQuery(id+"F7.imprint","IMPRINT",EDGE,{"derivedFrom":sQuery(id+"F7.wireOp",EDGE,"E5.14.19.0")}),1.0]])]});
            var Q525;
            Q525=makeQuery(id+"F7.imprint","IMPRINT",FACE,{"disambiguationData":[TD([[makeQuery(id+"F7.imprint","IMPRINT",EDGE,{"derivedFrom":sQuery(id+"F7.wireOp",EDGE,"E5.14.3.0")}),1.0]])]});
            var Q526;
            Q526=makeQuery(id+"F7.imprint","IMPRINT",FACE,{"disambiguationData":[TD([[makeQuery(id+"F7.imprint","IMPRINT",EDGE,{"derivedFrom":sQuery(id+"F7.wireOp",EDGE,"E5.32.6.0")}),1.0]])]});
            var Q527;
            Q527=makeQuery(id+"F7.imprint","IMPRINT",FACE,{"disambiguationData":[TD([[makeQuery(id+"F7.imprint","IMPRINT",EDGE,{"derivedFrom":sQuery(id+"F7.wireOp",EDGE,"E5.27.17.0")}),1.0]])]});
            var Q528;
            Q528=makeQuery(id+"F7.imprint","IMPRINT",FACE,{"disambiguationData":[TD([[makeQuery(id+"F7.imprint","IMPRINT",EDGE,{"derivedFrom":sQuery(id+"F7.wireOp",EDGE,"E5.27.1.0")}),1.0]])]});
            var Q529;
            Q529=makeQuery(id+"F7.imprint","IMPRINT",FACE,{"disambiguationData":[TD([[makeQuery(id+"F7.imprint","IMPRINT",EDGE,{"derivedFrom":sQuery(id+"F7.wireOp",EDGE,"E5.32.22.0")}),1.0]])]});
            var Q530;
            Q530=makeQuery(id+"F7.imprint","IMPRINT",FACE,{"disambiguationData":[TD([[makeQuery(id+"F7.imprint","IMPRINT",EDGE,{"derivedFrom":sQuery(id+"F7.wireOp",EDGE,"E5.29.19.0")}),1.0]])]});
            var Q531;
            Q531=makeQuery(id+"F7.imprint","IMPRINT",FACE,{"disambiguationData":[TD([[makeQuery(id+"F7.imprint","IMPRINT",EDGE,{"derivedFrom":sQuery(id+"F7.wireOp",EDGE,"E5.29.3.0")}),1.0]])]});
            var Q532;
            Q532=makeQuery(id+"F7.imprint","IMPRINT",FACE,{"disambiguationData":[TD([[makeQuery(id+"F7.imprint","IMPRINT",EDGE,{"derivedFrom":sQuery(id+"F7.wireOp",EDGE,"E5.28.18.0")}),1.0]])]});
            var Q533;
            Q533=makeQuery(id+"F7.imprint","IMPRINT",FACE,{"disambiguationData":[TD([[makeQuery(id+"F7.imprint","IMPRINT",EDGE,{"derivedFrom":sQuery(id+"F7.wireOp",EDGE,"E5.28.2.0")}),1.0]])]});
            var Q534;
            Q534=makeQuery(id+"F7.imprint","IMPRINT",FACE,{"disambiguationData":[TD([[makeQuery(id+"F7.imprint","IMPRINT",EDGE,{"derivedFrom":sQuery(id+"F7.wireOp",EDGE,"E5.30.20.0")}),1.0]])]});
            var Q535;
            Q535=makeQuery(id+"F7.imprint","IMPRINT",FACE,{"disambiguationData":[TD([[makeQuery(id+"F7.imprint","IMPRINT",EDGE,{"derivedFrom":sQuery(id+"F7.wireOp",EDGE,"E5.30.4.0")}),1.0]])]});
            var Q536;
            Q536=makeQuery(id+"F7.imprint","IMPRINT",FACE,{"disambiguationData":[TD([[makeQuery(id+"F7.imprint","IMPRINT",EDGE,{"derivedFrom":sQuery(id+"F7.wireOp",EDGE,"E5.2.8.0")}),1.0]])]});
            var Q537;
            Q537=makeQuery(id+"F7.imprint","IMPRINT",FACE,{"disambiguationData":[TD([[makeQuery(id+"F7.imprint","IMPRINT",EDGE,{"derivedFrom":sQuery(id+"F7.wireOp",EDGE,"E5.1.23.0")}),1.0]])]});
            var Q538;
            Q538=makeQuery(id+"F7.imprint","IMPRINT",FACE,{"disambiguationData":[TD([[makeQuery(id+"F7.imprint","IMPRINT",EDGE,{"derivedFrom":sQuery(id+"F7.wireOp",EDGE,"E5.1.7.0")}),1.0]])]});
            var Q539;
            Q539=makeQuery(id+"F7.imprint","IMPRINT",FACE,{"disambiguationData":[TD([[makeQuery(id+"F7.imprint","IMPRINT",EDGE,{"derivedFrom":sQuery(id+"F7.wireOp",EDGE,"E5.4.10.0")}),1.0]])]});
            var Q540;
            Q540=makeQuery(id+"F7.imprint","IMPRINT",FACE,{"disambiguationData":[TD([[makeQuery(id+"F7.imprint","IMPRINT",EDGE,{"derivedFrom":sQuery(id+"F7.wireOp",EDGE,"E5.3.25.0")}),1.0]])]});
            var Q541;
            Q541=makeQuery(id+"F7.imprint","IMPRINT",FACE,{"disambiguationData":[TD([[makeQuery(id+"F7.imprint","IMPRINT",EDGE,{"derivedFrom":sQuery(id+"F7.wireOp",EDGE,"E5.3.9.0")}),1.0]])]});
            var Q542;
            Q542=makeQuery(id+"F7.imprint","IMPRINT",FACE,{"disambiguationData":[TD([[makeQuery(id+"F7.imprint","IMPRINT",EDGE,{"derivedFrom":sQuery(id+"F7.wireOp",EDGE,"E5.2.24.0")}),1.0]])]});
            var Q543;
            Q543=makeQuery(id+"F7.imprint","IMPRINT",FACE,{"disambiguationData":[TD([[makeQuery(id+"F7.imprint","IMPRINT",EDGE,{"derivedFrom":sQuery(id+"F7.wireOp",EDGE,"E5.19.25.0")}),1.0]])]});
            var Q544;
            Q544=makeQuery(id+"F7.imprint","IMPRINT",FACE,{"disambiguationData":[TD([[makeQuery(id+"F7.imprint","IMPRINT",EDGE,{"derivedFrom":sQuery(id+"F7.wireOp",EDGE,"E5.19.9.0")}),1.0]])]});
            var Q545;
            Q545=makeQuery(id+"F7.imprint","IMPRINT",FACE,{"disambiguationData":[TD([[makeQuery(id+"F7.imprint","IMPRINT",EDGE,{"derivedFrom":sQuery(id+"F7.wireOp",EDGE,"E5.18.24.0")}),1.0]])]});
            var Q546;
            Q546=makeQuery(id+"F7.imprint","IMPRINT",FACE,{"disambiguationData":[TD([[makeQuery(id+"F7.imprint","IMPRINT",EDGE,{"derivedFrom":sQuery(id+"F7.wireOp",EDGE,"E5.18.8.0")}),1.0]])]});
            var Q547;
            Q547=makeQuery(id+"F7.imprint","IMPRINT",FACE,{"disambiguationData":[TD([[makeQuery(id+"F7.imprint","IMPRINT",EDGE,{"derivedFrom":sQuery(id+"F7.wireOp",EDGE,"E5.21.27.0")}),1.0]])]});
            var Q548;
            Q548=makeQuery(id+"F7.imprint","IMPRINT",FACE,{"disambiguationData":[TD([[makeQuery(id+"F7.imprint","IMPRINT",EDGE,{"derivedFrom":sQuery(id+"F7.wireOp",EDGE,"E5.21.11.0")}),1.0]])]});
            var Q549;
            Q549=makeQuery(id+"F7.imprint","IMPRINT",FACE,{"disambiguationData":[TD([[makeQuery(id+"F7.imprint","IMPRINT",EDGE,{"derivedFrom":sQuery(id+"F7.wireOp",EDGE,"E5.20.26.0")}),1.0]])]});
            var Q550;
            Q550=makeQuery(id+"F7.imprint","IMPRINT",FACE,{"disambiguationData":[TD([[makeQuery(id+"F7.imprint","IMPRINT",EDGE,{"derivedFrom":sQuery(id+"F7.wireOp",EDGE,"E5.20.10.0")}),1.0]])]});
            var Q551;
            Q551=makeQuery(id+"F7.imprint","IMPRINT",FACE,{"disambiguationData":[TD([[makeQuery(id+"F7.imprint","IMPRINT",EDGE,{"derivedFrom":sQuery(id+"F7.wireOp",EDGE,"E5.23.29.0")}),1.0]])]});
            var Q552;
            Q552=makeQuery(id+"F7.imprint","IMPRINT",FACE,{"disambiguationData":[TD([[makeQuery(id+"F7.imprint","IMPRINT",EDGE,{"derivedFrom":sQuery(id+"F7.wireOp",EDGE,"E5.23.13.0")}),1.0]])]});
            var Q553;
            Q553=makeQuery(id+"F7.imprint","IMPRINT",FACE,{"disambiguationData":[TD([[makeQuery(id+"F7.imprint","IMPRINT",EDGE,{"derivedFrom":sQuery(id+"F7.wireOp",EDGE,"E5.22.28.0")}),1.0]])]});
            var Q554;
            Q554=makeQuery(id+"F7.imprint","IMPRINT",FACE,{"disambiguationData":[TD([[makeQuery(id+"F7.imprint","IMPRINT",EDGE,{"derivedFrom":sQuery(id+"F7.wireOp",EDGE,"E5.22.12.0")}),1.0]])]});
            var Q555;
            Q555=makeQuery(id+"F7.imprint","IMPRINT",FACE,{"disambiguationData":[TD([[makeQuery(id+"F7.imprint","IMPRINT",EDGE,{"derivedFrom":sQuery(id+"F7.wireOp",EDGE,"E5.25.15.0")}),1.0]])]});
            var Q556;
            Q556=makeQuery(id+"F7.imprint","IMPRINT",FACE,{"disambiguationData":[TD([[makeQuery(id+"F7.imprint","IMPRINT",EDGE,{"derivedFrom":sQuery(id+"F7.wireOp",EDGE,"E5.24.14.0")}),1.0]])]});
            var Q557;
            Q557=makeQuery(id+"F7.imprint","IMPRINT",FACE,{"disambiguationData":[TD([[makeQuery(id+"F7.imprint","IMPRINT",EDGE,{"derivedFrom":sQuery(id+"F7.wireOp",EDGE,"E5.6.12.0")}),1.0]])]});
            var Q558;
            Q558=makeQuery(id+"F7.imprint","IMPRINT",FACE,{"disambiguationData":[TD([[makeQuery(id+"F7.imprint","IMPRINT",EDGE,{"derivedFrom":sQuery(id+"F7.wireOp",EDGE,"E5.5.27.0")}),1.0]])]});
            var Q559;
            Q559=makeQuery(id+"F7.imprint","IMPRINT",FACE,{"disambiguationData":[TD([[makeQuery(id+"F7.imprint","IMPRINT",EDGE,{"derivedFrom":sQuery(id+"F7.wireOp",EDGE,"E5.4.26.0")}),1.0]])]});
            var Q560;
            Q560=makeQuery(id+"F7.imprint","IMPRINT",FACE,{"disambiguationData":[TD([[makeQuery(id+"F7.imprint","IMPRINT",EDGE,{"derivedFrom":sQuery(id+"F7.wireOp",EDGE,"E5.8.14.0")}),1.0]])]});
            var Q561;
            Q561=makeQuery(id+"F7.imprint","IMPRINT",FACE,{"disambiguationData":[TD([[makeQuery(id+"F7.imprint","IMPRINT",EDGE,{"derivedFrom":sQuery(id+"F7.wireOp",EDGE,"E5.7.29.0")}),1.0]])]});
            var Q562;
            Q562=makeQuery(id+"F7.imprint","IMPRINT",FACE,{"disambiguationData":[TD([[makeQuery(id+"F7.imprint","IMPRINT",EDGE,{"derivedFrom":sQuery(id+"F7.wireOp",EDGE,"E5.7.13.0")}),1.0]])]});
            var Q563;
            Q563=makeQuery(id+"F7.imprint","IMPRINT",FACE,{"disambiguationData":[TD([[makeQuery(id+"F7.imprint","IMPRINT",EDGE,{"derivedFrom":sQuery(id+"F7.wireOp",EDGE,"E5.6.28.0")}),1.0]])]});
            var Q564;
            Q564=makeQuery(id+"F7.imprint","IMPRINT",FACE,{"disambiguationData":[TD([[makeQuery(id+"F7.imprint","IMPRINT",EDGE,{"derivedFrom":sQuery(id+"F7.wireOp",EDGE,"E5.9.15.0")}),1.0]])]});
            var Q565;
            Q565=makeQuery(id+"F7.imprint","IMPRINT",FACE,{"disambiguationData":[TD([[makeQuery(id+"F7.imprint","IMPRINT",EDGE,{"derivedFrom":sQuery(id+"F7.wireOp",EDGE,"E5.12.18.0")}),1.0]])]});
            var Q566;
            Q566=makeQuery(id+"F7.imprint","IMPRINT",FACE,{"disambiguationData":[TD([[makeQuery(id+"F7.imprint","IMPRINT",EDGE,{"derivedFrom":sQuery(id+"F7.wireOp",EDGE,"E5.12.2.0")}),1.0]])]});
            var Q567;
            Q567=makeQuery(id+"F7.imprint","IMPRINT",FACE,{"disambiguationData":[TD([[makeQuery(id+"F7.imprint","IMPRINT",EDGE,{"derivedFrom":sQuery(id+"F7.wireOp",EDGE,"E5.11.17.0")}),1.0]])]});
            var Q568;
            Q568=makeQuery(id+"F7.imprint","IMPRINT",FACE,{"disambiguationData":[TD([[makeQuery(id+"F7.imprint","IMPRINT",EDGE,{"derivedFrom":sQuery(id+"F7.wireOp",EDGE,"E5.11.1.0")}),1.0]])]});
            var Q569;
            Q569=makeQuery(id+"F7.imprint","IMPRINT",FACE,{"disambiguationData":[TD([[makeQuery(id+"F7.imprint","IMPRINT",EDGE,{"derivedFrom":sQuery(id+"F7.wireOp",EDGE,"E5.13.3.0")}),1.0]])]});
            var Q570;
            Q570=makeQuery(id+"F7.imprint","IMPRINT",FACE,{"disambiguationData":[TD([[makeQuery(id+"F7.imprint","IMPRINT",EDGE,{"derivedFrom":sQuery(id+"F7.wireOp",EDGE,"E5.13.19.0")}),1.0]])]});
            var Q571;
            Q571=makeQuery(id+"F7.imprint","IMPRINT",FACE,{"disambiguationData":[TD([[makeQuery(id+"F7.imprint","IMPRINT",EDGE,{"derivedFrom":sQuery(id+"F7.wireOp",EDGE,"E5.15.21.0")}),1.0]])]});
            var Q572;
            Q572=makeQuery(id+"F7.imprint","IMPRINT",FACE,{"disambiguationData":[TD([[makeQuery(id+"F7.imprint","IMPRINT",EDGE,{"derivedFrom":sQuery(id+"F7.wireOp",EDGE,"E5.15.5.0")}),1.0]])]});
            var Q573;
            Q573=makeQuery(id+"F7.imprint","IMPRINT",FACE,{"disambiguationData":[TD([[makeQuery(id+"F7.imprint","IMPRINT",EDGE,{"derivedFrom":sQuery(id+"F7.wireOp",EDGE,"E5.14.4.0")}),1.0]])]});
            var Q574;
            Q574=makeQuery(id+"F7.imprint","IMPRINT",FACE,{"disambiguationData":[TD([[makeQuery(id+"F7.imprint","IMPRINT",EDGE,{"derivedFrom":sQuery(id+"F7.wireOp",EDGE,"E5.17.23.0")}),1.0]])]});
            var Q575;
            Q575=makeQuery(id+"F7.imprint","IMPRINT",FACE,{"disambiguationData":[TD([[makeQuery(id+"F7.imprint","IMPRINT",EDGE,{"derivedFrom":sQuery(id+"F7.wireOp",EDGE,"E5.17.7.0")}),1.0]])]});
            var Q576;
            Q576=makeQuery(id+"F7.imprint","IMPRINT",FACE,{"disambiguationData":[TD([[makeQuery(id+"F7.imprint","IMPRINT",EDGE,{"derivedFrom":sQuery(id+"F7.wireOp",EDGE,"E5.16.22.0")}),1.0]])]});
            var Q577;
            Q577=makeQuery(id+"F7.imprint","IMPRINT",FACE,{"disambiguationData":[TD([[makeQuery(id+"F7.imprint","IMPRINT",EDGE,{"derivedFrom":sQuery(id+"F7.wireOp",EDGE,"E5.16.6.0")}),1.0]])]});
            var Q578;
            Q578=makeQuery(id+"F7.imprint","IMPRINT",FACE,{"disambiguationData":[TD([[makeQuery(id+"F7.imprint","IMPRINT",EDGE,{"derivedFrom":sQuery(id+"F7.wireOp",EDGE,"E5.29.20.0")}),1.0]])]});
            var Q579;
            Q579=makeQuery(id+"F7.imprint","IMPRINT",FACE,{"disambiguationData":[TD([[makeQuery(id+"F7.imprint","IMPRINT",EDGE,{"derivedFrom":sQuery(id+"F7.wireOp",EDGE,"E5.29.4.0")}),1.0]])]});
            var Q580;
            Q580=makeQuery(id+"F7.imprint","IMPRINT",FACE,{"disambiguationData":[TD([[makeQuery(id+"F7.imprint","IMPRINT",EDGE,{"derivedFrom":sQuery(id+"F7.wireOp",EDGE,"E5.31.22.0")}),1.0]])]});
            var Q581;
            Q581=makeQuery(id+"F7.imprint","IMPRINT",FACE,{"disambiguationData":[TD([[makeQuery(id+"F7.imprint","IMPRINT",EDGE,{"derivedFrom":sQuery(id+"F7.wireOp",EDGE,"E5.1.8.0")}),1.0]])]});
            var Q582;
            Q582=makeQuery(id+"F7.imprint","IMPRINT",FACE,{"disambiguationData":[TD([[makeQuery(id+"F7.imprint","IMPRINT",EDGE,{"derivedFrom":sQuery(id+"F7.wireOp",EDGE,"E5.3.10.0")}),1.0]])]});
            var Q583;
            Q583=makeQuery(id+"F7.imprint","IMPRINT",FACE,{"disambiguationData":[TD([[makeQuery(id+"F7.imprint","IMPRINT",EDGE,{"derivedFrom":sQuery(id+"F7.wireOp",EDGE,"E5.2.25.0")}),1.0]])]});
            var Q584;
            Q584=makeQuery(id+"F7.imprint","IMPRINT",FACE,{"disambiguationData":[TD([[makeQuery(id+"F7.imprint","IMPRINT",EDGE,{"derivedFrom":sQuery(id+"F7.wireOp",EDGE,"E5.2.9.0")}),1.0]])]});
            var Q585;
            Q585=makeQuery(id+"F7.imprint","IMPRINT",FACE,{"disambiguationData":[TD([[makeQuery(id+"F7.imprint","IMPRINT",EDGE,{"derivedFrom":sQuery(id+"F7.wireOp",EDGE,"E5.1.24.0")}),1.0]])]});
            var Q586;
            Q586=makeQuery(id+"F7.imprint","IMPRINT",FACE,{"disambiguationData":[TD([[makeQuery(id+"F7.imprint","IMPRINT",EDGE,{"derivedFrom":sQuery(id+"F7.wireOp",EDGE,"E5.5.12.0")}),1.0]])]});
            var Q587;
            Q587=makeQuery(id+"F7.imprint","IMPRINT",FACE,{"disambiguationData":[TD([[makeQuery(id+"F7.imprint","IMPRINT",EDGE,{"derivedFrom":sQuery(id+"F7.wireOp",EDGE,"E5.4.27.0")}),1.0]])]});
            var Q588;
            Q588=makeQuery(id+"F7.imprint","IMPRINT",FACE,{"disambiguationData":[TD([[makeQuery(id+"F7.imprint","IMPRINT",EDGE,{"derivedFrom":sQuery(id+"F7.wireOp",EDGE,"E5.4.11.0")}),1.0]])]});
            var Q589;
            Q589=makeQuery(id+"F7.imprint","IMPRINT",FACE,{"disambiguationData":[TD([[makeQuery(id+"F7.imprint","IMPRINT",EDGE,{"derivedFrom":sQuery(id+"F7.wireOp",EDGE,"E5.3.26.0")}),1.0]])]});
            var Q590;
            Q590=makeQuery(id+"F7.imprint","IMPRINT",FACE,{"disambiguationData":[TD([[makeQuery(id+"F7.imprint","IMPRINT",EDGE,{"derivedFrom":sQuery(id+"F7.wireOp",EDGE,"E5.7.14.0")}),1.0]])]});
            var Q591;
            Q591=makeQuery(id+"F7.imprint","IMPRINT",FACE,{"disambiguationData":[TD([[makeQuery(id+"F7.imprint","IMPRINT",EDGE,{"derivedFrom":sQuery(id+"F7.wireOp",EDGE,"E5.6.29.0")}),1.0]])]});
            var Q592;
            Q592=makeQuery(id+"F7.imprint","IMPRINT",FACE,{"disambiguationData":[TD([[makeQuery(id+"F7.imprint","IMPRINT",EDGE,{"derivedFrom":sQuery(id+"F7.wireOp",EDGE,"E5.6.13.0")}),1.0]])]});
            var Q593;
            Q593=makeQuery(id+"F7.imprint","IMPRINT",FACE,{"disambiguationData":[TD([[makeQuery(id+"F7.imprint","IMPRINT",EDGE,{"derivedFrom":sQuery(id+"F7.wireOp",EDGE,"E5.5.28.0")}),1.0]])]});
            var Q594;
            Q594=makeQuery(id+"F7.imprint","IMPRINT",FACE,{"disambiguationData":[TD([[makeQuery(id+"F7.imprint","IMPRINT",EDGE,{"derivedFrom":sQuery(id+"F7.wireOp",EDGE,"E5.8.15.0")}),1.0]])]});
            var Q595;
            Q595=makeQuery(id+"F7.imprint","IMPRINT",FACE,{"disambiguationData":[TD([[makeQuery(id+"F7.imprint","IMPRINT",EDGE,{"derivedFrom":sQuery(id+"F7.wireOp",EDGE,"E5.32.7.0")}),1.0]])]});
            var Q596;
            Q596=makeQuery(id+"F7.imprint","IMPRINT",FACE,{"disambiguationData":[TD([[makeQuery(id+"F7.imprint","IMPRINT",EDGE,{"derivedFrom":sQuery(id+"F7.wireOp",EDGE,"E5.32.23.0")}),1.0]])]});
            var Q597;
            Q597=makeQuery(id+"F7.imprint","IMPRINT",FACE,{"disambiguationData":[TD([[makeQuery(id+"F7.imprint","IMPRINT",EDGE,{"derivedFrom":sQuery(id+"F7.wireOp",EDGE,"E5.28.19.0")}),1.0]])]});
            var Q598;
            Q598=makeQuery(id+"F7.imprint","IMPRINT",FACE,{"disambiguationData":[TD([[makeQuery(id+"F7.imprint","IMPRINT",EDGE,{"derivedFrom":sQuery(id+"F7.wireOp",EDGE,"E5.28.3.0")}),1.0]])]});
            var Q599;
            Q599=makeQuery(id+"F7.imprint","IMPRINT",FACE,{"disambiguationData":[TD([[makeQuery(id+"F7.imprint","IMPRINT",EDGE,{"derivedFrom":sQuery(id+"F7.wireOp",EDGE,"E5.27.18.0")}),1.0]])]});
            var Q600;
            Q600=makeQuery(id+"F7.imprint","IMPRINT",FACE,{"disambiguationData":[TD([[makeQuery(id+"F7.imprint","IMPRINT",EDGE,{"derivedFrom":sQuery(id+"F7.wireOp",EDGE,"E5.27.2.0")}),1.0]])]});
            var Q601;
            Q601=makeQuery(id+"F7.imprint","IMPRINT",FACE,{"disambiguationData":[TD([[makeQuery(id+"F7.imprint","IMPRINT",EDGE,{"derivedFrom":sQuery(id+"F7.wireOp",EDGE,"E5.24.15.0")}),1.0]])]});
            var Q602;
            Q602=makeQuery(id+"F7.imprint","IMPRINT",FACE,{"disambiguationData":[TD([[makeQuery(id+"F7.imprint","IMPRINT",EDGE,{"derivedFrom":sQuery(id+"F7.wireOp",EDGE,"E5.23.14.0")}),1.0]])]});
            var Q603;
            Q603=makeQuery(id+"F7.imprint","IMPRINT",FACE,{"disambiguationData":[TD([[makeQuery(id+"F7.imprint","IMPRINT",EDGE,{"derivedFrom":sQuery(id+"F7.wireOp",EDGE,"E5.26.17.0")}),1.0]])]});
            var Q604;
            Q604=makeQuery(id+"F7.imprint","IMPRINT",FACE,{"disambiguationData":[TD([[makeQuery(id+"F7.imprint","IMPRINT",EDGE,{"derivedFrom":sQuery(id+"F7.wireOp",EDGE,"E5.26.1.0")}),1.0]])]});
            var Q605;
            Q605=makeQuery(id+"F7.imprint","IMPRINT",FACE,{"disambiguationData":[TD([[makeQuery(id+"F7.imprint","IMPRINT",EDGE,{"derivedFrom":sQuery(id+"F7.wireOp",EDGE,"E5.25.16.0")}),1.0]])]});
            var Q606;
            Q606=makeQuery(id+"F7.imprint","IMPRINT",FACE,{"disambiguationData":[TD([[makeQuery(id+"F7.imprint","IMPRINT",EDGE,{"derivedFrom":sQuery(id+"F7.wireOp",EDGE,"E5.11.18.0")}),1.0]])]});
            var Q607;
            Q607=makeQuery(id+"F7.imprint","IMPRINT",FACE,{"disambiguationData":[TD([[makeQuery(id+"F7.imprint","IMPRINT",EDGE,{"derivedFrom":sQuery(id+"F7.wireOp",EDGE,"E5.11.2.0")}),1.0]])]});
            var Q608;
            Q608=makeQuery(id+"F7.imprint","IMPRINT",FACE,{"disambiguationData":[TD([[makeQuery(id+"F7.imprint","IMPRINT",EDGE,{"derivedFrom":sQuery(id+"F7.wireOp",EDGE,"E5.10.17.0")}),1.0]])]});
            var Q609;
            Q609=makeQuery(id+"F7.imprint","IMPRINT",FACE,{"disambiguationData":[TD([[makeQuery(id+"F7.imprint","IMPRINT",EDGE,{"derivedFrom":sQuery(id+"F7.wireOp",EDGE,"E5.13.4.0")}),1.0]])]});
            var Q610;
            Q610=makeQuery(id+"F7.imprint","IMPRINT",FACE,{"disambiguationData":[TD([[makeQuery(id+"F7.imprint","IMPRINT",EDGE,{"derivedFrom":sQuery(id+"F7.wireOp",EDGE,"E5.12.19.0")}),1.0]])]});
            var Q611;
            Q611=makeQuery(id+"F7.imprint","IMPRINT",FACE,{"disambiguationData":[TD([[makeQuery(id+"F7.imprint","IMPRINT",EDGE,{"derivedFrom":sQuery(id+"F7.wireOp",EDGE,"E5.12.3.0")}),1.0]])]});
            var Q612;
            Q612=makeQuery(id+"F7.imprint","IMPRINT",FACE,{"disambiguationData":[TD([[makeQuery(id+"F7.imprint","IMPRINT",EDGE,{"derivedFrom":sQuery(id+"F7.wireOp",EDGE,"E5.13.20.0")}),1.0]])]});
            var Q613;
            Q613=makeQuery(id+"F7.imprint","IMPRINT",FACE,{"disambiguationData":[TD([[makeQuery(id+"F7.imprint","IMPRINT",EDGE,{"derivedFrom":sQuery(id+"F7.wireOp",EDGE,"E5.16.23.0")}),1.0]])]});
            var Q614;
            Q614=makeQuery(id+"F7.imprint","IMPRINT",FACE,{"disambiguationData":[TD([[makeQuery(id+"F7.imprint","IMPRINT",EDGE,{"derivedFrom":sQuery(id+"F7.wireOp",EDGE,"E5.16.7.0")}),1.0]])]});
            var Q615;
            Q615=makeQuery(id+"F7.imprint","IMPRINT",FACE,{"disambiguationData":[TD([[makeQuery(id+"F7.imprint","IMPRINT",EDGE,{"derivedFrom":sQuery(id+"F7.wireOp",EDGE,"E5.15.22.0")}),1.0]])]});
            var Q616;
            Q616=makeQuery(id+"F7.imprint","IMPRINT",FACE,{"disambiguationData":[TD([[makeQuery(id+"F7.imprint","IMPRINT",EDGE,{"derivedFrom":sQuery(id+"F7.wireOp",EDGE,"E5.15.6.0")}),1.0]])]});
            var Q617;
            Q617=makeQuery(id+"F7.imprint","IMPRINT",FACE,{"disambiguationData":[TD([[makeQuery(id+"F7.imprint","IMPRINT",EDGE,{"derivedFrom":sQuery(id+"F7.wireOp",EDGE,"E5.18.25.0")}),1.0]])]});
            var Q618;
            Q618=makeQuery(id+"F7.imprint","IMPRINT",FACE,{"disambiguationData":[TD([[makeQuery(id+"F7.imprint","IMPRINT",EDGE,{"derivedFrom":sQuery(id+"F7.wireOp",EDGE,"E5.18.9.0")}),1.0]])]});
            var Q619;
            Q619=makeQuery(id+"F7.imprint","IMPRINT",FACE,{"disambiguationData":[TD([[makeQuery(id+"F7.imprint","IMPRINT",EDGE,{"derivedFrom":sQuery(id+"F7.wireOp",EDGE,"E5.17.24.0")}),1.0]])]});
            var Q620;
            Q620=makeQuery(id+"F7.imprint","IMPRINT",FACE,{"disambiguationData":[TD([[makeQuery(id+"F7.imprint","IMPRINT",EDGE,{"derivedFrom":sQuery(id+"F7.wireOp",EDGE,"E5.17.8.0")}),1.0]])]});
            var Q621;
            Q621=makeQuery(id+"F7.imprint","IMPRINT",FACE,{"disambiguationData":[TD([[makeQuery(id+"F7.imprint","IMPRINT",EDGE,{"derivedFrom":sQuery(id+"F7.wireOp",EDGE,"E5.20.27.0")}),1.0]])]});
            var Q622;
            Q622=makeQuery(id+"F7.imprint","IMPRINT",FACE,{"disambiguationData":[TD([[makeQuery(id+"F7.imprint","IMPRINT",EDGE,{"derivedFrom":sQuery(id+"F7.wireOp",EDGE,"E5.20.11.0")}),1.0]])]});
            var Q623;
            Q623=makeQuery(id+"F7.imprint","IMPRINT",FACE,{"disambiguationData":[TD([[makeQuery(id+"F7.imprint","IMPRINT",EDGE,{"derivedFrom":sQuery(id+"F7.wireOp",EDGE,"E5.19.26.0")}),1.0]])]});
            var Q624;
            Q624=makeQuery(id+"F7.imprint","IMPRINT",FACE,{"disambiguationData":[TD([[makeQuery(id+"F7.imprint","IMPRINT",EDGE,{"derivedFrom":sQuery(id+"F7.wireOp",EDGE,"E5.19.10.0")}),1.0]])]});
            var Q625;
            Q625=makeQuery(id+"F7.imprint","IMPRINT",FACE,{"disambiguationData":[TD([[makeQuery(id+"F7.imprint","IMPRINT",EDGE,{"derivedFrom":sQuery(id+"F7.wireOp",EDGE,"E5.22.29.0")}),1.0]])]});
            var Q626;
            Q626=makeQuery(id+"F7.imprint","IMPRINT",FACE,{"disambiguationData":[TD([[makeQuery(id+"F7.imprint","IMPRINT",EDGE,{"derivedFrom":sQuery(id+"F7.wireOp",EDGE,"E5.22.13.0")}),1.0]])]});
            var Q627;
            Q627=makeQuery(id+"F7.imprint","IMPRINT",FACE,{"disambiguationData":[TD([[makeQuery(id+"F7.imprint","IMPRINT",EDGE,{"derivedFrom":sQuery(id+"F7.wireOp",EDGE,"E5.21.28.0")}),1.0]])]});
            var Q628;
            Q628=makeQuery(id+"F7.imprint","IMPRINT",FACE,{"disambiguationData":[TD([[makeQuery(id+"F7.imprint","IMPRINT",EDGE,{"derivedFrom":sQuery(id+"F7.wireOp",EDGE,"E5.21.12.0")}),1.0]])]});
            var Q629;
            Q629=makeQuery(id+"F7.imprint","IMPRINT",FACE,{"disambiguationData":[TD([[makeQuery(id+"F7.imprint","IMPRINT",EDGE,{"derivedFrom":sQuery(id+"F7.wireOp",EDGE,"E5.31.23.0")}),1.0]])]});
            var Q630;
            Q630=makeQuery(id+"F7.imprint","IMPRINT",FACE,{"disambiguationData":[TD([[makeQuery(id+"F7.imprint","IMPRINT",EDGE,{"derivedFrom":sQuery(id+"F7.wireOp",EDGE,"E5.31.7.0")}),1.0]])]});
            var Q631;
            Q631=makeQuery(id+"F7.imprint","IMPRINT",FACE,{"disambiguationData":[TD([[makeQuery(id+"F7.imprint","IMPRINT",EDGE,{"derivedFrom":sQuery(id+"F7.wireOp",EDGE,"E5.1.9.0")}),1.0]])]});
            var Q632;
            Q632=makeQuery(id+"F7.imprint","IMPRINT",FACE,{"disambiguationData":[TD([[makeQuery(id+"F7.imprint","IMPRINT",EDGE,{"derivedFrom":sQuery(id+"F7.wireOp",EDGE,"E5.3.11.0")}),1.0]])]});
            var Q633;
            Q633=makeQuery(id+"F7.imprint","IMPRINT",FACE,{"disambiguationData":[TD([[makeQuery(id+"F7.imprint","IMPRINT",EDGE,{"derivedFrom":sQuery(id+"F7.wireOp",EDGE,"E5.2.10.0")}),1.0]])]});
            var Q634;
            Q634=makeQuery(id+"F7.imprint","IMPRINT",FACE,{"disambiguationData":[TD([[makeQuery(id+"F7.imprint","IMPRINT",EDGE,{"derivedFrom":sQuery(id+"F7.wireOp",EDGE,"E5.1.25.0")}),1.0]])]});
            var Q635;
            Q635=makeQuery(id+"F7.imprint","IMPRINT",FACE,{"disambiguationData":[TD([[makeQuery(id+"F7.imprint","IMPRINT",EDGE,{"derivedFrom":sQuery(id+"F7.wireOp",EDGE,"E5.5.13.0")}),1.0]])]});
            var Q636;
            Q636=makeQuery(id+"F7.imprint","IMPRINT",FACE,{"disambiguationData":[TD([[makeQuery(id+"F7.imprint","IMPRINT",EDGE,{"derivedFrom":sQuery(id+"F7.wireOp",EDGE,"E5.4.28.0")}),1.0]])]});
            var Q637;
            Q637=makeQuery(id+"F7.imprint","IMPRINT",FACE,{"disambiguationData":[TD([[makeQuery(id+"F7.imprint","IMPRINT",EDGE,{"derivedFrom":sQuery(id+"F7.wireOp",EDGE,"E5.4.12.0")}),1.0]])]});
            var Q638;
            Q638=makeQuery(id+"F7.imprint","IMPRINT",FACE,{"disambiguationData":[TD([[makeQuery(id+"F7.imprint","IMPRINT",EDGE,{"derivedFrom":sQuery(id+"F7.wireOp",EDGE,"E5.3.27.0")}),1.0]])]});
            var Q639;
            Q639=makeQuery(id+"F7.imprint","IMPRINT",FACE,{"disambiguationData":[TD([[makeQuery(id+"F7.imprint","IMPRINT",EDGE,{"derivedFrom":sQuery(id+"F7.wireOp",EDGE,"E5.7.15.0")}),1.0]])]});
            var Q640;
            Q640=makeQuery(id+"F7.imprint","IMPRINT",FACE,{"disambiguationData":[TD([[makeQuery(id+"F7.imprint","IMPRINT",EDGE,{"derivedFrom":sQuery(id+"F7.wireOp",EDGE,"E5.6.14.0")}),1.0]])]});
            var Q641;
            Q641=makeQuery(id+"F7.imprint","IMPRINT",FACE,{"disambiguationData":[TD([[makeQuery(id+"F7.imprint","IMPRINT",EDGE,{"derivedFrom":sQuery(id+"F7.wireOp",EDGE,"E5.5.29.0")}),1.0]])]});
            var Q642;
            Q642=makeQuery(id+"F7.imprint","IMPRINT",FACE,{"disambiguationData":[TD([[makeQuery(id+"F7.imprint","IMPRINT",EDGE,{"derivedFrom":sQuery(id+"F7.wireOp",EDGE,"E5.9.17.0")}),1.0]])]});
            var Q643;
            Q643=makeQuery(id+"F7.imprint","IMPRINT",FACE,{"disambiguationData":[TD([[makeQuery(id+"F7.imprint","IMPRINT",EDGE,{"derivedFrom":sQuery(id+"F7.wireOp",EDGE,"E5.9.1.0")}),1.0]])]});
            var Q644;
            Q644=makeQuery(id+"F7.imprint","IMPRINT",FACE,{"disambiguationData":[TD([[makeQuery(id+"F7.imprint","IMPRINT",EDGE,{"derivedFrom":sQuery(id+"F7.wireOp",EDGE,"E5.8.16.0")}),1.0]])]});
            var Q645;
            Q645=makeQuery(id+"F7.imprint","IMPRINT",FACE,{"disambiguationData":[TD([[makeQuery(id+"F7.imprint","IMPRINT",EDGE,{"derivedFrom":sQuery(id+"F7.wireOp",EDGE,"E5.11.19.0")}),1.0]])]});
            var Q646;
            Q646=makeQuery(id+"F7.imprint","IMPRINT",FACE,{"disambiguationData":[TD([[makeQuery(id+"F7.imprint","IMPRINT",EDGE,{"derivedFrom":sQuery(id+"F7.wireOp",EDGE,"E5.11.3.0")}),1.0]])]});
            var Q647;
            Q647=makeQuery(id+"F7.imprint","IMPRINT",FACE,{"disambiguationData":[TD([[makeQuery(id+"F7.imprint","IMPRINT",EDGE,{"derivedFrom":sQuery(id+"F7.wireOp",EDGE,"E5.10.18.0")}),1.0]])]});
            var Q648;
            Q648=makeQuery(id+"F7.imprint","IMPRINT",FACE,{"disambiguationData":[TD([[makeQuery(id+"F7.imprint","IMPRINT",EDGE,{"derivedFrom":sQuery(id+"F7.wireOp",EDGE,"E5.10.2.0")}),1.0]])]});
            var Q649;
            Q649=makeQuery(id+"F7.imprint","IMPRINT",FACE,{"disambiguationData":[TD([[makeQuery(id+"F7.imprint","IMPRINT",EDGE,{"derivedFrom":sQuery(id+"F7.wireOp",EDGE,"E5.32.8.0")}),1.0]])]});
            var Q650;
            Q650=makeQuery(id+"F7.imprint","IMPRINT",FACE,{"disambiguationData":[TD([[makeQuery(id+"F7.imprint","IMPRINT",EDGE,{"derivedFrom":sQuery(id+"F7.wireOp",EDGE,"E5.32.24.0")}),1.0]])]});
            var Q651;
            Q651=makeQuery(id+"F7.imprint","IMPRINT",FACE,{"disambiguationData":[TD([[makeQuery(id+"F7.imprint","IMPRINT",EDGE,{"derivedFrom":sQuery(id+"F7.wireOp",EDGE,"E5.28.20.0")}),1.0]])]});
            var Q652;
            Q652=makeQuery(id+"F7.imprint","IMPRINT",FACE,{"disambiguationData":[TD([[makeQuery(id+"F7.imprint","IMPRINT",EDGE,{"derivedFrom":sQuery(id+"F7.wireOp",EDGE,"E5.28.4.0")}),1.0]])]});
            var Q653;
            Q653=makeQuery(id+"F7.imprint","IMPRINT",FACE,{"disambiguationData":[TD([[makeQuery(id+"F7.imprint","IMPRINT",EDGE,{"derivedFrom":sQuery(id+"F7.wireOp",EDGE,"E5.27.19.0")}),1.0]])]});
            var Q654;
            Q654=makeQuery(id+"F7.imprint","IMPRINT",FACE,{"disambiguationData":[TD([[makeQuery(id+"F7.imprint","IMPRINT",EDGE,{"derivedFrom":sQuery(id+"F7.wireOp",EDGE,"E5.27.3.0")}),1.0]])]});
            var Q655;
            Q655=makeQuery(id+"F7.imprint","IMPRINT",FACE,{"disambiguationData":[TD([[makeQuery(id+"F7.imprint","IMPRINT",EDGE,{"derivedFrom":sQuery(id+"F7.wireOp",EDGE,"E5.30.22.0")}),1.0]])]});
            var Q656;
            Q656=makeQuery(id+"F7.imprint","IMPRINT",FACE,{"disambiguationData":[TD([[makeQuery(id+"F7.imprint","IMPRINT",EDGE,{"derivedFrom":sQuery(id+"F7.wireOp",EDGE,"E5.30.6.0")}),1.0]])]});
            var Q657;
            Q657=makeQuery(id+"F7.imprint","IMPRINT",FACE,{"disambiguationData":[TD([[makeQuery(id+"F7.imprint","IMPRINT",EDGE,{"derivedFrom":sQuery(id+"F7.wireOp",EDGE,"E5.29.21.0")}),1.0]])]});
            var Q658;
            Q658=makeQuery(id+"F7.imprint","IMPRINT",FACE,{"disambiguationData":[TD([[makeQuery(id+"F7.imprint","IMPRINT",EDGE,{"derivedFrom":sQuery(id+"F7.wireOp",EDGE,"E5.29.5.0")}),1.0]])]});
            var Q659;
            Q659=makeQuery(id+"F7.imprint","IMPRINT",FACE,{"disambiguationData":[TD([[makeQuery(id+"F7.imprint","IMPRINT",EDGE,{"derivedFrom":sQuery(id+"F7.wireOp",EDGE,"E5.26.18.0")}),1.0]])]});
            var Q660;
            Q660=makeQuery(id+"F7.imprint","IMPRINT",FACE,{"disambiguationData":[TD([[makeQuery(id+"F7.imprint","IMPRINT",EDGE,{"derivedFrom":sQuery(id+"F7.wireOp",EDGE,"E5.26.2.0")}),1.0]])]});
            var Q661;
            Q661=makeQuery(id+"F7.imprint","IMPRINT",FACE,{"disambiguationData":[TD([[makeQuery(id+"F7.imprint","IMPRINT",EDGE,{"derivedFrom":sQuery(id+"F7.wireOp",EDGE,"E5.25.17.0")}),1.0]])]});
            var Q662;
            Q662=makeQuery(id+"F7.imprint","IMPRINT",FACE,{"disambiguationData":[TD([[makeQuery(id+"F7.imprint","IMPRINT",EDGE,{"derivedFrom":sQuery(id+"F7.wireOp",EDGE,"E5.13.5.0")}),1.0]])]});
            var Q663;
            Q663=makeQuery(id+"F7.imprint","IMPRINT",FACE,{"disambiguationData":[TD([[makeQuery(id+"F7.imprint","IMPRINT",EDGE,{"derivedFrom":sQuery(id+"F7.wireOp",EDGE,"E5.12.20.0")}),1.0]])]});
            var Q664;
            Q664=makeQuery(id+"F7.imprint","IMPRINT",FACE,{"disambiguationData":[TD([[makeQuery(id+"F7.imprint","IMPRINT",EDGE,{"derivedFrom":sQuery(id+"F7.wireOp",EDGE,"E5.12.4.0")}),1.0]])]});
            var Q665;
            Q665=makeQuery(id+"F7.imprint","IMPRINT",FACE,{"disambiguationData":[TD([[makeQuery(id+"F7.imprint","IMPRINT",EDGE,{"derivedFrom":sQuery(id+"F7.wireOp",EDGE,"E5.14.22.0")}),1.0]])]});
            var Q666;
            Q666=makeQuery(id+"F7.imprint","IMPRINT",FACE,{"disambiguationData":[TD([[makeQuery(id+"F7.imprint","IMPRINT",EDGE,{"derivedFrom":sQuery(id+"F7.wireOp",EDGE,"E5.13.21.0")}),1.0]])]});
            var Q667;
            Q667=makeQuery(id+"F7.imprint","IMPRINT",FACE,{"disambiguationData":[TD([[makeQuery(id+"F7.imprint","IMPRINT",EDGE,{"derivedFrom":sQuery(id+"F7.wireOp",EDGE,"E5.16.24.0")}),1.0]])]});
            var Q668;
            Q668=makeQuery(id+"F7.imprint","IMPRINT",FACE,{"disambiguationData":[TD([[makeQuery(id+"F7.imprint","IMPRINT",EDGE,{"derivedFrom":sQuery(id+"F7.wireOp",EDGE,"E5.16.8.0")}),1.0]])]});
            var Q669;
            Q669=makeQuery(id+"F7.imprint","IMPRINT",FACE,{"disambiguationData":[TD([[makeQuery(id+"F7.imprint","IMPRINT",EDGE,{"derivedFrom":sQuery(id+"F7.wireOp",EDGE,"E5.15.23.0")}),1.0]])]});
            var Q670;
            Q670=makeQuery(id+"F7.imprint","IMPRINT",FACE,{"disambiguationData":[TD([[makeQuery(id+"F7.imprint","IMPRINT",EDGE,{"derivedFrom":sQuery(id+"F7.wireOp",EDGE,"E5.15.7.0")}),1.0]])]});
            var Q671;
            Q671=makeQuery(id+"F7.imprint","IMPRINT",FACE,{"disambiguationData":[TD([[makeQuery(id+"F7.imprint","IMPRINT",EDGE,{"derivedFrom":sQuery(id+"F7.wireOp",EDGE,"E5.17.25.0")}),1.0]])]});
            var Q672;
            Q672=makeQuery(id+"F7.imprint","IMPRINT",FACE,{"disambiguationData":[TD([[makeQuery(id+"F7.imprint","IMPRINT",EDGE,{"derivedFrom":sQuery(id+"F7.wireOp",EDGE,"E5.17.9.0")}),1.0]])]});
            var Q673;
            Q673=makeQuery(id+"F7.imprint","IMPRINT",FACE,{"disambiguationData":[TD([[makeQuery(id+"F7.imprint","IMPRINT",EDGE,{"derivedFrom":sQuery(id+"F7.wireOp",EDGE,"E5.20.28.0")}),1.0]])]});
            var Q674;
            Q674=makeQuery(id+"F7.imprint","IMPRINT",FACE,{"disambiguationData":[TD([[makeQuery(id+"F7.imprint","IMPRINT",EDGE,{"derivedFrom":sQuery(id+"F7.wireOp",EDGE,"E5.20.12.0")}),1.0]])]});
            var Q675;
            Q675=makeQuery(id+"F7.imprint","IMPRINT",FACE,{"disambiguationData":[TD([[makeQuery(id+"F7.imprint","IMPRINT",EDGE,{"derivedFrom":sQuery(id+"F7.wireOp",EDGE,"E5.19.27.0")}),1.0]])]});
            var Q676;
            Q676=makeQuery(id+"F7.imprint","IMPRINT",FACE,{"disambiguationData":[TD([[makeQuery(id+"F7.imprint","IMPRINT",EDGE,{"derivedFrom":sQuery(id+"F7.wireOp",EDGE,"E5.19.11.0")}),1.0]])]});
            var Q677;
            Q677=makeQuery(id+"F7.imprint","IMPRINT",FACE,{"disambiguationData":[TD([[makeQuery(id+"F7.imprint","IMPRINT",EDGE,{"derivedFrom":sQuery(id+"F7.wireOp",EDGE,"E5.22.14.0")}),1.0]])]});
            var Q678;
            Q678=makeQuery(id+"F7.imprint","IMPRINT",FACE,{"disambiguationData":[TD([[makeQuery(id+"F7.imprint","IMPRINT",EDGE,{"derivedFrom":sQuery(id+"F7.wireOp",EDGE,"E5.21.29.0")}),1.0]])]});
            var Q679;
            Q679=makeQuery(id+"F7.imprint","IMPRINT",FACE,{"disambiguationData":[TD([[makeQuery(id+"F7.imprint","IMPRINT",EDGE,{"derivedFrom":sQuery(id+"F7.wireOp",EDGE,"E5.21.13.0")}),1.0]])]});
            var Q680;
            Q680=makeQuery(id+"F7.imprint","IMPRINT",FACE,{"disambiguationData":[TD([[makeQuery(id+"F7.imprint","IMPRINT",EDGE,{"derivedFrom":sQuery(id+"F7.wireOp",EDGE,"E5.25.1.0")}),1.0]])]});
            var Q681;
            Q681=makeQuery(id+"F7.imprint","IMPRINT",FACE,{"disambiguationData":[TD([[makeQuery(id+"F7.imprint","IMPRINT",EDGE,{"derivedFrom":sQuery(id+"F7.wireOp",EDGE,"E5.24.16.0")}),1.0]])]});
            var Q682;
            Q682=makeQuery(id+"F7.imprint","IMPRINT",FACE,{"disambiguationData":[TD([[makeQuery(id+"F7.imprint","IMPRINT",EDGE,{"derivedFrom":sQuery(id+"F7.wireOp",EDGE,"E5.23.15.0")}),1.0]])]});
            var Q683;
            Q683=makeQuery(id+"F7.imprint","IMPRINT",FACE,{"disambiguationData":[TD([[makeQuery(id+"F7.imprint","IMPRINT",EDGE,{"derivedFrom":sQuery(id+"F7.wireOp",EDGE,"E5.3.12.0")}),1.0]])]});
            var Q684;
            Q684=makeQuery(id+"F7.imprint","IMPRINT",FACE,{"disambiguationData":[TD([[makeQuery(id+"F7.imprint","IMPRINT",EDGE,{"derivedFrom":sQuery(id+"F7.wireOp",EDGE,"E5.2.27.0")}),1.0]])]});
            var Q685;
            Q685=makeQuery(id+"F7.imprint","IMPRINT",FACE,{"disambiguationData":[TD([[makeQuery(id+"F7.imprint","IMPRINT",EDGE,{"derivedFrom":sQuery(id+"F7.wireOp",EDGE,"E5.2.11.0")}),1.0]])]});
            var Q686;
            Q686=makeQuery(id+"F7.imprint","IMPRINT",FACE,{"disambiguationData":[TD([[makeQuery(id+"F7.imprint","IMPRINT",EDGE,{"derivedFrom":sQuery(id+"F7.wireOp",EDGE,"E5.5.14.0")}),1.0]])]});
            var Q687;
            Q687=makeQuery(id+"F7.imprint","IMPRINT",FACE,{"disambiguationData":[TD([[makeQuery(id+"F7.imprint","IMPRINT",EDGE,{"derivedFrom":sQuery(id+"F7.wireOp",EDGE,"E5.4.29.0")}),1.0]])]});
            var Q688;
            Q688=makeQuery(id+"F7.imprint","IMPRINT",FACE,{"disambiguationData":[TD([[makeQuery(id+"F7.imprint","IMPRINT",EDGE,{"derivedFrom":sQuery(id+"F7.wireOp",EDGE,"E5.4.13.0")}),1.0]])]});
            var Q689;
            Q689=makeQuery(id+"F7.imprint","IMPRINT",FACE,{"disambiguationData":[TD([[makeQuery(id+"F7.imprint","IMPRINT",EDGE,{"derivedFrom":sQuery(id+"F7.wireOp",EDGE,"E5.3.28.0")}),1.0]])]});
            var Q690;
            Q690=makeQuery(id+"F7.imprint","IMPRINT",FACE,{"disambiguationData":[TD([[makeQuery(id+"F7.imprint","IMPRINT",EDGE,{"derivedFrom":sQuery(id+"F7.wireOp",EDGE,"E5.7.16.0")}),1.0]])]});
            var Q691;
            Q691=makeQuery(id+"F7.imprint","IMPRINT",FACE,{"disambiguationData":[TD([[makeQuery(id+"F7.imprint","IMPRINT",EDGE,{"derivedFrom":sQuery(id+"F7.wireOp",EDGE,"E5.6.15.0")}),1.0]])]});
            var Q692;
            Q692=makeQuery(id+"F7.imprint","IMPRINT",FACE,{"disambiguationData":[TD([[makeQuery(id+"F7.imprint","IMPRINT",EDGE,{"derivedFrom":sQuery(id+"F7.wireOp",EDGE,"E5.9.18.0")}),1.0]])]});
            var Q693;
            Q693=makeQuery(id+"F7.imprint","IMPRINT",FACE,{"disambiguationData":[TD([[makeQuery(id+"F7.imprint","IMPRINT",EDGE,{"derivedFrom":sQuery(id+"F7.wireOp",EDGE,"E5.9.2.0")}),1.0]])]});
            var Q694;
            Q694=makeQuery(id+"F7.imprint","IMPRINT",FACE,{"disambiguationData":[TD([[makeQuery(id+"F7.imprint","IMPRINT",EDGE,{"derivedFrom":sQuery(id+"F7.wireOp",EDGE,"E5.8.17.0")}),1.0]])]});
            var Q695;
            Q695=makeQuery(id+"F7.imprint","IMPRINT",FACE,{"disambiguationData":[TD([[makeQuery(id+"F7.imprint","IMPRINT",EDGE,{"derivedFrom":sQuery(id+"F7.wireOp",EDGE,"E5.8.1.0")}),1.0]])]});
            var Q696;
            Q696=makeQuery(id+"F7.imprint","IMPRINT",FACE,{"disambiguationData":[TD([[makeQuery(id+"F7.imprint","IMPRINT",EDGE,{"derivedFrom":sQuery(id+"F7.wireOp",EDGE,"E5.11.20.0")}),1.0]])]});
            var Q697;
            Q697=makeQuery(id+"F7.imprint","IMPRINT",FACE,{"disambiguationData":[TD([[makeQuery(id+"F7.imprint","IMPRINT",EDGE,{"derivedFrom":sQuery(id+"F7.wireOp",EDGE,"E5.11.4.0")}),1.0]])]});
            var Q698;
            Q698=makeQuery(id+"F7.imprint","IMPRINT",FACE,{"disambiguationData":[TD([[makeQuery(id+"F7.imprint","IMPRINT",EDGE,{"derivedFrom":sQuery(id+"F7.wireOp",EDGE,"E5.10.19.0")}),1.0]])]});
            var Q699;
            Q699=makeQuery(id+"F7.imprint","IMPRINT",FACE,{"disambiguationData":[TD([[makeQuery(id+"F7.imprint","IMPRINT",EDGE,{"derivedFrom":sQuery(id+"F7.wireOp",EDGE,"E5.10.3.0")}),1.0]])]});
            var Q700;
            Q700=makeQuery(id+"F7.imprint","IMPRINT",FACE,{"disambiguationData":[TD([[makeQuery(id+"F7.imprint","IMPRINT",EDGE,{"derivedFrom":sQuery(id+"F7.wireOp",EDGE,"E5.13.6.0")}),1.0]])]});
            var Q701;
            Q701=makeQuery(id+"F7.imprint","IMPRINT",FACE,{"disambiguationData":[TD([[makeQuery(id+"F7.imprint","IMPRINT",EDGE,{"derivedFrom":sQuery(id+"F7.wireOp",EDGE,"E5.33.12.0")}),1.0]])]});
            var Q702;
            Q702=makeQuery(id+"F7.imprint","IMPRINT",FACE,{"disambiguationData":[TD([[makeQuery(id+"F7.imprint","IMPRINT",EDGE,{"derivedFrom":sQuery(id+"F7.wireOp",EDGE,"E5.12.21.0")}),1.0]])]});
            var Q703;
            Q703=makeQuery(id+"F7.imprint","IMPRINT",FACE,{"disambiguationData":[TD([[makeQuery(id+"F7.imprint","IMPRINT",EDGE,{"derivedFrom":sQuery(id+"F7.wireOp",EDGE,"E5.12.5.0")}),1.0]])]});
            var Q704;
            Q704=makeQuery(id+"F7.imprint","IMPRINT",FACE,{"disambiguationData":[TD([[makeQuery(id+"F7.imprint","IMPRINT",EDGE,{"derivedFrom":sQuery(id+"F7.wireOp",EDGE,"E5.32.9.0")}),1.0]])]});
            var Q705;
            Q705=makeQuery(id+"F7.imprint","IMPRINT",FACE,{"disambiguationData":[TD([[makeQuery(id+"F7.imprint","IMPRINT",EDGE,{"derivedFrom":sQuery(id+"F7.wireOp",EDGE,"E5.32.25.0")}),1.0]])]});
            var Q706;
            Q706=makeQuery(id+"F7.imprint","IMPRINT",FACE,{"disambiguationData":[TD([[makeQuery(id+"F7.imprint","IMPRINT",EDGE,{"derivedFrom":sQuery(id+"F7.wireOp",EDGE,"E5.28.21.0")}),1.0]])]});
            var Q707;
            Q707=makeQuery(id+"F7.imprint","IMPRINT",FACE,{"disambiguationData":[TD([[makeQuery(id+"F7.imprint","IMPRINT",EDGE,{"derivedFrom":sQuery(id+"F7.wireOp",EDGE,"E5.28.5.0")}),1.0]])]});
            var Q708;
            Q708=makeQuery(id+"F7.imprint","IMPRINT",FACE,{"disambiguationData":[TD([[makeQuery(id+"F7.imprint","IMPRINT",EDGE,{"derivedFrom":sQuery(id+"F7.wireOp",EDGE,"E5.27.20.0")}),1.0]])]});
            var Q709;
            Q709=makeQuery(id+"F7.imprint","IMPRINT",FACE,{"disambiguationData":[TD([[makeQuery(id+"F7.imprint","IMPRINT",EDGE,{"derivedFrom":sQuery(id+"F7.wireOp",EDGE,"E5.27.4.0")}),1.0]])]});
            var Q710;
            Q710=makeQuery(id+"F7.imprint","IMPRINT",FACE,{"disambiguationData":[TD([[makeQuery(id+"F7.imprint","IMPRINT",EDGE,{"derivedFrom":sQuery(id+"F7.wireOp",EDGE,"E5.30.23.0")}),1.0]])]});
            var Q711;
            Q711=makeQuery(id+"F7.imprint","IMPRINT",FACE,{"disambiguationData":[TD([[makeQuery(id+"F7.imprint","IMPRINT",EDGE,{"derivedFrom":sQuery(id+"F7.wireOp",EDGE,"E5.30.7.0")}),1.0]])]});
            var Q712;
            Q712=makeQuery(id+"F7.imprint","IMPRINT",FACE,{"disambiguationData":[TD([[makeQuery(id+"F7.imprint","IMPRINT",EDGE,{"derivedFrom":sQuery(id+"F7.wireOp",EDGE,"E5.29.22.0")}),1.0]])]});
            var Q713;
            Q713=makeQuery(id+"F7.imprint","IMPRINT",FACE,{"disambiguationData":[TD([[makeQuery(id+"F7.imprint","IMPRINT",EDGE,{"derivedFrom":sQuery(id+"F7.wireOp",EDGE,"E5.29.6.0")}),1.0]])]});
            var Q714;
            Q714=makeQuery(id+"F7.imprint","IMPRINT",FACE,{"disambiguationData":[TD([[makeQuery(id+"F7.imprint","IMPRINT",EDGE,{"derivedFrom":sQuery(id+"F7.wireOp",EDGE,"E5.33.28.0")}),1.0]])]});
            var Q715;
            Q715=makeQuery(id+"F7.imprint","IMPRINT",FACE,{"disambiguationData":[TD([[makeQuery(id+"F7.imprint","IMPRINT",EDGE,{"derivedFrom":sQuery(id+"F7.wireOp",EDGE,"E5.31.24.0")}),1.0]])]});
            var Q716;
            Q716=makeQuery(id+"F7.imprint","IMPRINT",FACE,{"disambiguationData":[TD([[makeQuery(id+"F7.imprint","IMPRINT",EDGE,{"derivedFrom":sQuery(id+"F7.wireOp",EDGE,"E5.31.8.0")}),1.0]])]});
            var Q717;
            Q717=makeQuery(id+"F7.imprint","IMPRINT",FACE,{"disambiguationData":[TD([[makeQuery(id+"F7.imprint","IMPRINT",EDGE,{"derivedFrom":sQuery(id+"F7.wireOp",EDGE,"E5.14.23.0")}),1.0]])]});
            var Q718;
            Q718=makeQuery(id+"F7.imprint","IMPRINT",FACE,{"disambiguationData":[TD([[makeQuery(id+"F7.imprint","IMPRINT",EDGE,{"derivedFrom":sQuery(id+"F7.wireOp",EDGE,"E5.14.7.0")}),1.0]])]});
            var Q719;
            Q719=makeQuery(id+"F7.imprint","IMPRINT",FACE,{"disambiguationData":[TD([[makeQuery(id+"F7.imprint","IMPRINT",EDGE,{"derivedFrom":sQuery(id+"F7.wireOp",EDGE,"E5.13.22.0")}),1.0]])]});
            var Q720;
            Q720=makeQuery(id+"F7.imprint","IMPRINT",FACE,{"disambiguationData":[TD([[makeQuery(id+"F7.imprint","IMPRINT",EDGE,{"derivedFrom":sQuery(id+"F7.wireOp",EDGE,"E5.16.25.0")}),1.0]])]});
            var Q721;
            Q721=makeQuery(id+"F7.imprint","IMPRINT",FACE,{"disambiguationData":[TD([[makeQuery(id+"F7.imprint","IMPRINT",EDGE,{"derivedFrom":sQuery(id+"F7.wireOp",EDGE,"E5.16.9.0")}),1.0]])]});
            var Q722;
            Q722=makeQuery(id+"F7.imprint","IMPRINT",FACE,{"disambiguationData":[TD([[makeQuery(id+"F7.imprint","IMPRINT",EDGE,{"derivedFrom":sQuery(id+"F7.wireOp",EDGE,"E5.15.24.0")}),1.0]])]});
            var Q723;
            Q723=makeQuery(id+"F7.imprint","IMPRINT",FACE,{"disambiguationData":[TD([[makeQuery(id+"F7.imprint","IMPRINT",EDGE,{"derivedFrom":sQuery(id+"F7.wireOp",EDGE,"E5.15.8.0")}),1.0]])]});
            var Q724;
            Q724=makeQuery(id+"F7.imprint","IMPRINT",FACE,{"disambiguationData":[TD([[makeQuery(id+"F7.imprint","IMPRINT",EDGE,{"derivedFrom":sQuery(id+"F7.wireOp",EDGE,"E5.17.26.0")}),1.0]])]});
            var Q725;
            Q725=makeQuery(id+"F7.imprint","IMPRINT",FACE,{"disambiguationData":[TD([[makeQuery(id+"F7.imprint","IMPRINT",EDGE,{"derivedFrom":sQuery(id+"F7.wireOp",EDGE,"E5.17.10.0")}),1.0]])]});
            var Q726;
            Q726=makeQuery(id+"F7.imprint","IMPRINT",FACE,{"disambiguationData":[TD([[makeQuery(id+"F7.imprint","IMPRINT",EDGE,{"derivedFrom":sQuery(id+"F7.wireOp",EDGE,"E5.20.29.0")}),1.0]])]});
            var Q727;
            Q727=makeQuery(id+"F7.imprint","IMPRINT",FACE,{"disambiguationData":[TD([[makeQuery(id+"F7.imprint","IMPRINT",EDGE,{"derivedFrom":sQuery(id+"F7.wireOp",EDGE,"E5.20.13.0")}),1.0]])]});
            var Q728;
            Q728=makeQuery(id+"F7.imprint","IMPRINT",FACE,{"disambiguationData":[TD([[makeQuery(id+"F7.imprint","IMPRINT",EDGE,{"derivedFrom":sQuery(id+"F7.wireOp",EDGE,"E5.19.28.0")}),1.0]])]});
            var Q729;
            Q729=makeQuery(id+"F7.imprint","IMPRINT",FACE,{"disambiguationData":[TD([[makeQuery(id+"F7.imprint","IMPRINT",EDGE,{"derivedFrom":sQuery(id+"F7.wireOp",EDGE,"E5.19.12.0")}),1.0]])]});
            var Q730;
            Q730=makeQuery(id+"F7.imprint","IMPRINT",FACE,{"disambiguationData":[TD([[makeQuery(id+"F7.imprint","IMPRINT",EDGE,{"derivedFrom":sQuery(id+"F7.wireOp",EDGE,"E5.21.14.0")}),1.0]])]});
            var Q731;
            Q731=makeQuery(id+"F7.imprint","IMPRINT",FACE,{"disambiguationData":[TD([[makeQuery(id+"F7.imprint","IMPRINT",EDGE,{"derivedFrom":sQuery(id+"F7.wireOp",EDGE,"E5.25.2.0")}),1.0]])]});
            var Q732;
            Q732=makeQuery(id+"F7.imprint","IMPRINT",FACE,{"disambiguationData":[TD([[makeQuery(id+"F7.imprint","IMPRINT",EDGE,{"derivedFrom":sQuery(id+"F7.wireOp",EDGE,"E5.24.17.0")}),1.0]])]});
            var Q733;
            Q733=makeQuery(id+"F7.imprint","IMPRINT",FACE,{"disambiguationData":[TD([[makeQuery(id+"F7.imprint","IMPRINT",EDGE,{"derivedFrom":sQuery(id+"F7.wireOp",EDGE,"E5.24.1.0")}),1.0]])]});
            var Q734;
            Q734=makeQuery(id+"F7.imprint","IMPRINT",FACE,{"disambiguationData":[TD([[makeQuery(id+"F7.imprint","IMPRINT",EDGE,{"derivedFrom":sQuery(id+"F7.wireOp",EDGE,"E5.26.19.0")}),1.0]])]});
            var Q735;
            Q735=makeQuery(id+"F7.imprint","IMPRINT",FACE,{"disambiguationData":[TD([[makeQuery(id+"F7.imprint","IMPRINT",EDGE,{"derivedFrom":sQuery(id+"F7.wireOp",EDGE,"E5.26.3.0")}),1.0]])]});
            var Q736;
            Q736=makeQuery(id+"F7.imprint","IMPRINT",FACE,{"disambiguationData":[TD([[makeQuery(id+"F7.imprint","IMPRINT",EDGE,{"derivedFrom":sQuery(id+"F7.wireOp",EDGE,"E5.25.18.0")}),1.0]])]});
            var Q737;
            Q737=makeQuery(id+"F7.imprint","IMPRINT",FACE,{"disambiguationData":[TD([[makeQuery(id+"F7.imprint","IMPRINT",EDGE,{"derivedFrom":sQuery(id+"F7.wireOp",EDGE,"E5.3.13.0")}),1.0]])]});
            var Q738;
            Q738=makeQuery(id+"F7.imprint","IMPRINT",FACE,{"disambiguationData":[TD([[makeQuery(id+"F7.imprint","IMPRINT",EDGE,{"derivedFrom":sQuery(id+"F7.wireOp",EDGE,"E5.2.28.0")}),1.0]])]});
            var Q739;
            Q739=makeQuery(id+"F7.imprint","IMPRINT",FACE,{"disambiguationData":[TD([[makeQuery(id+"F7.imprint","IMPRINT",EDGE,{"derivedFrom":sQuery(id+"F7.wireOp",EDGE,"E5.2.12.0")}),1.0]])]});
            var Q740;
            Q740=makeQuery(id+"F7.imprint","IMPRINT",FACE,{"disambiguationData":[TD([[makeQuery(id+"F7.imprint","IMPRINT",EDGE,{"derivedFrom":sQuery(id+"F7.wireOp",EDGE,"E5.1.27.0")}),1.0]])]});
            var Q741;
            Q741=makeQuery(id+"F7.imprint","IMPRINT",FACE,{"disambiguationData":[TD([[makeQuery(id+"F7.imprint","IMPRINT",EDGE,{"derivedFrom":sQuery(id+"F7.wireOp",EDGE,"E5.5.15.0")}),1.0]])]});
            var Q742;
            Q742=makeQuery(id+"F7.imprint","IMPRINT",FACE,{"disambiguationData":[TD([[makeQuery(id+"F7.imprint","IMPRINT",EDGE,{"derivedFrom":sQuery(id+"F7.wireOp",EDGE,"E5.4.14.0")}),1.0]])]});
            var Q743;
            Q743=makeQuery(id+"F7.imprint","IMPRINT",FACE,{"disambiguationData":[TD([[makeQuery(id+"F7.imprint","IMPRINT",EDGE,{"derivedFrom":sQuery(id+"F7.wireOp",EDGE,"E5.3.29.0")}),1.0]])]});
            var Q744;
            Q744=makeQuery(id+"F7.imprint","IMPRINT",FACE,{"disambiguationData":[TD([[makeQuery(id+"F7.imprint","IMPRINT",EDGE,{"derivedFrom":sQuery(id+"F7.wireOp",EDGE,"E5.7.17.0")}),1.0]])]});
            var Q745;
            Q745=makeQuery(id+"F7.imprint","IMPRINT",FACE,{"disambiguationData":[TD([[makeQuery(id+"F7.imprint","IMPRINT",EDGE,{"derivedFrom":sQuery(id+"F7.wireOp",EDGE,"E5.7.1.0")}),1.0]])]});
            var Q746;
            Q746=makeQuery(id+"F7.imprint","IMPRINT",FACE,{"disambiguationData":[TD([[makeQuery(id+"F7.imprint","IMPRINT",EDGE,{"derivedFrom":sQuery(id+"F7.wireOp",EDGE,"E5.9.19.0")}),1.0]])]});
            var Q747;
            Q747=makeQuery(id+"F7.imprint","IMPRINT",FACE,{"disambiguationData":[TD([[makeQuery(id+"F7.imprint","IMPRINT",EDGE,{"derivedFrom":sQuery(id+"F7.wireOp",EDGE,"E5.9.3.0")}),1.0]])]});
            var Q748;
            Q748=makeQuery(id+"F7.imprint","IMPRINT",FACE,{"disambiguationData":[TD([[makeQuery(id+"F7.imprint","IMPRINT",EDGE,{"derivedFrom":sQuery(id+"F7.wireOp",EDGE,"E5.8.18.0")}),1.0]])]});
            var Q749;
            Q749=makeQuery(id+"F7.imprint","IMPRINT",FACE,{"disambiguationData":[TD([[makeQuery(id+"F7.imprint","IMPRINT",EDGE,{"derivedFrom":sQuery(id+"F7.wireOp",EDGE,"E5.8.2.0")}),1.0]])]});
            var Q750;
            Q750=makeQuery(id+"F7.imprint","IMPRINT",FACE,{"disambiguationData":[TD([[makeQuery(id+"F7.imprint","IMPRINT",EDGE,{"derivedFrom":sQuery(id+"F7.wireOp",EDGE,"E5.11.21.0")}),1.0]])]});
            var Q751;
            Q751=makeQuery(id+"F7.imprint","IMPRINT",FACE,{"disambiguationData":[TD([[makeQuery(id+"F7.imprint","IMPRINT",EDGE,{"derivedFrom":sQuery(id+"F7.wireOp",EDGE,"E5.11.5.0")}),1.0]])]});
            var Q752;
            Q752=makeQuery(id+"F7.imprint","IMPRINT",FACE,{"disambiguationData":[TD([[makeQuery(id+"F7.imprint","IMPRINT",EDGE,{"derivedFrom":sQuery(id+"F7.wireOp",EDGE,"E5.10.20.0")}),1.0]])]});
            var Q753;
            Q753=makeQuery(id+"F7.imprint","IMPRINT",FACE,{"disambiguationData":[TD([[makeQuery(id+"F7.imprint","IMPRINT",EDGE,{"derivedFrom":sQuery(id+"F7.wireOp",EDGE,"E5.10.4.0")}),1.0]])]});
            var Q754;
            Q754=makeQuery(id+"F7.imprint","IMPRINT",FACE,{"disambiguationData":[TD([[makeQuery(id+"F7.imprint","IMPRINT",EDGE,{"derivedFrom":sQuery(id+"F7.wireOp",EDGE,"E5.13.7.0")}),1.0]])]});
            var Q755;
            Q755=makeQuery(id+"F7.imprint","IMPRINT",FACE,{"disambiguationData":[TD([[makeQuery(id+"F7.imprint","IMPRINT",EDGE,{"derivedFrom":sQuery(id+"F7.wireOp",EDGE,"E5.12.22.0")}),1.0]])]});
            var Q756;
            Q756=makeQuery(id+"F7.imprint","IMPRINT",FACE,{"disambiguationData":[TD([[makeQuery(id+"F7.imprint","IMPRINT",EDGE,{"derivedFrom":sQuery(id+"F7.wireOp",EDGE,"E5.12.6.0")}),1.0]])]});
            var Q757;
            Q757=makeQuery(id+"F7.imprint","IMPRINT",FACE,{"disambiguationData":[TD([[makeQuery(id+"F7.imprint","IMPRINT",EDGE,{"derivedFrom":sQuery(id+"F7.wireOp",EDGE,"E5.33.21.0")}),1.0]])]});
            var Q758;
            Q758=makeQuery(id+"F7.imprint","IMPRINT",FACE,{"disambiguationData":[TD([[makeQuery(id+"F7.imprint","IMPRINT",EDGE,{"derivedFrom":sQuery(id+"F7.wireOp",EDGE,"E5.32.10.0")}),1.0]])]});
            var Q759;
            Q759=makeQuery(id+"F7.imprint","IMPRINT",FACE,{"disambiguationData":[TD([[makeQuery(id+"F7.imprint","IMPRINT",EDGE,{"derivedFrom":sQuery(id+"F7.wireOp",EDGE,"E5.32.26.0")}),1.0]])]});
            var Q760;
            Q760=makeQuery(id+"F7.imprint","IMPRINT",FACE,{"disambiguationData":[TD([[makeQuery(id+"F7.imprint","IMPRINT",EDGE,{"derivedFrom":sQuery(id+"F7.wireOp",EDGE,"E5.28.22.0")}),1.0]])]});
            var Q761;
            Q761=makeQuery(id+"F7.imprint","IMPRINT",FACE,{"disambiguationData":[TD([[makeQuery(id+"F7.imprint","IMPRINT",EDGE,{"derivedFrom":sQuery(id+"F7.wireOp",EDGE,"E5.28.6.0")}),1.0]])]});
            var Q762;
            Q762=makeQuery(id+"F7.imprint","IMPRINT",FACE,{"disambiguationData":[TD([[makeQuery(id+"F7.imprint","IMPRINT",EDGE,{"derivedFrom":sQuery(id+"F7.wireOp",EDGE,"E5.30.24.0")}),1.0]])]});
            var Q763;
            Q763=makeQuery(id+"F7.imprint","IMPRINT",FACE,{"disambiguationData":[TD([[makeQuery(id+"F7.imprint","IMPRINT",EDGE,{"derivedFrom":sQuery(id+"F7.wireOp",EDGE,"E5.30.8.0")}),1.0]])]});
            var Q764;
            Q764=makeQuery(id+"F7.imprint","IMPRINT",FACE,{"disambiguationData":[TD([[makeQuery(id+"F7.imprint","IMPRINT",EDGE,{"derivedFrom":sQuery(id+"F7.wireOp",EDGE,"E5.29.23.0")}),1.0]])]});
            var Q765;
            Q765=makeQuery(id+"F7.imprint","IMPRINT",FACE,{"disambiguationData":[TD([[makeQuery(id+"F7.imprint","IMPRINT",EDGE,{"derivedFrom":sQuery(id+"F7.wireOp",EDGE,"E5.29.7.0")}),1.0]])]});
            var Q766;
            Q766=makeQuery(id+"F7.imprint","IMPRINT",FACE,{"disambiguationData":[TD([[makeQuery(id+"F7.imprint","IMPRINT",EDGE,{"derivedFrom":sQuery(id+"F7.wireOp",EDGE,"E5.31.25.0")}),1.0]])]});
            var Q767;
            Q767=makeQuery(id+"F7.imprint","IMPRINT",FACE,{"disambiguationData":[TD([[makeQuery(id+"F7.imprint","IMPRINT",EDGE,{"derivedFrom":sQuery(id+"F7.wireOp",EDGE,"E5.31.9.0")}),1.0]])]});
            var Q768;
            Q768=makeQuery(id+"F7.imprint","IMPRINT",FACE,{"disambiguationData":[TD([[makeQuery(id+"F7.imprint","IMPRINT",EDGE,{"derivedFrom":sQuery(id+"F7.wireOp",EDGE,"E5.14.24.0")}),1.0]])]});
            var Q769;
            Q769=makeQuery(id+"F7.imprint","IMPRINT",FACE,{"disambiguationData":[TD([[makeQuery(id+"F7.imprint","IMPRINT",EDGE,{"derivedFrom":sQuery(id+"F7.wireOp",EDGE,"E5.14.8.0")}),1.0]])]});
            var Q770;
            Q770=makeQuery(id+"F7.imprint","IMPRINT",FACE,{"disambiguationData":[TD([[makeQuery(id+"F7.imprint","IMPRINT",EDGE,{"derivedFrom":sQuery(id+"F7.wireOp",EDGE,"E5.13.23.0")}),1.0]])]});
            var Q771;
            Q771=makeQuery(id+"F7.imprint","IMPRINT",FACE,{"disambiguationData":[TD([[makeQuery(id+"F7.imprint","IMPRINT",EDGE,{"derivedFrom":sQuery(id+"F7.wireOp",EDGE,"E5.16.26.0")}),1.0]])]});
            var Q772;
            Q772=makeQuery(id+"F7.imprint","IMPRINT",FACE,{"disambiguationData":[TD([[makeQuery(id+"F7.imprint","IMPRINT",EDGE,{"derivedFrom":sQuery(id+"F7.wireOp",EDGE,"E5.16.10.0")}),1.0]])]});
            var Q773;
            Q773=makeQuery(id+"F7.imprint","IMPRINT",FACE,{"disambiguationData":[TD([[makeQuery(id+"F7.imprint","IMPRINT",EDGE,{"derivedFrom":sQuery(id+"F7.wireOp",EDGE,"E5.15.25.0")}),1.0]])]});
            var Q774;
            Q774=makeQuery(id+"F7.imprint","IMPRINT",FACE,{"disambiguationData":[TD([[makeQuery(id+"F7.imprint","IMPRINT",EDGE,{"derivedFrom":sQuery(id+"F7.wireOp",EDGE,"E5.15.9.0")}),1.0]])]});
            var Q775;
            Q775=makeQuery(id+"F7.imprint","IMPRINT",FACE,{"disambiguationData":[TD([[makeQuery(id+"F7.imprint","IMPRINT",EDGE,{"derivedFrom":sQuery(id+"F7.wireOp",EDGE,"E5.18.28.0")}),1.0]])]});
            var Q776;
            Q776=makeQuery(id+"F7.imprint","IMPRINT",FACE,{"disambiguationData":[TD([[makeQuery(id+"F7.imprint","IMPRINT",EDGE,{"derivedFrom":sQuery(id+"F7.wireOp",EDGE,"E5.18.12.0")}),1.0]])]});
            var Q777;
            Q777=makeQuery(id+"F7.imprint","IMPRINT",FACE,{"disambiguationData":[TD([[makeQuery(id+"F7.imprint","IMPRINT",EDGE,{"derivedFrom":sQuery(id+"F7.wireOp",EDGE,"E5.17.27.0")}),1.0]])]});
            var Q778;
            Q778=makeQuery(id+"F7.imprint","IMPRINT",FACE,{"disambiguationData":[TD([[makeQuery(id+"F7.imprint","IMPRINT",EDGE,{"derivedFrom":sQuery(id+"F7.wireOp",EDGE,"E5.17.11.0")}),1.0]])]});
            var Q779;
            Q779=makeQuery(id+"F7.imprint","IMPRINT",FACE,{"disambiguationData":[TD([[makeQuery(id+"F7.imprint","IMPRINT",EDGE,{"derivedFrom":sQuery(id+"F7.wireOp",EDGE,"E5.20.14.0")}),1.0]])]});
            var Q780;
            Q780=makeQuery(id+"F7.imprint","IMPRINT",FACE,{"disambiguationData":[TD([[makeQuery(id+"F7.imprint","IMPRINT",EDGE,{"derivedFrom":sQuery(id+"F7.wireOp",EDGE,"E5.19.29.0")}),1.0]])]});
            var Q781;
            Q781=makeQuery(id+"F7.imprint","IMPRINT",FACE,{"disambiguationData":[TD([[makeQuery(id+"F7.imprint","IMPRINT",EDGE,{"derivedFrom":sQuery(id+"F7.wireOp",EDGE,"E5.19.13.0")}),1.0]])]});
            var Q782;
            Q782=makeQuery(id+"F7.imprint","IMPRINT",FACE,{"disambiguationData":[TD([[makeQuery(id+"F7.imprint","IMPRINT",EDGE,{"derivedFrom":sQuery(id+"F7.wireOp",EDGE,"E5.23.1.0")}),1.0]])]});
            var Q783;
            Q783=makeQuery(id+"F7.imprint","IMPRINT",FACE,{"disambiguationData":[TD([[makeQuery(id+"F7.imprint","IMPRINT",EDGE,{"derivedFrom":sQuery(id+"F7.wireOp",EDGE,"E5.21.15.0")}),1.0]])]});
            var Q784;
            Q784=makeQuery(id+"F7.imprint","IMPRINT",FACE,{"disambiguationData":[TD([[makeQuery(id+"F7.imprint","IMPRINT",EDGE,{"derivedFrom":sQuery(id+"F7.wireOp",EDGE,"E5.25.3.0")}),1.0]])]});
            var Q785;
            Q785=makeQuery(id+"F7.imprint","IMPRINT",FACE,{"disambiguationData":[TD([[makeQuery(id+"F7.imprint","IMPRINT",EDGE,{"derivedFrom":sQuery(id+"F7.wireOp",EDGE,"E5.24.18.0")}),1.0]])]});
            var Q786;
            Q786=makeQuery(id+"F7.imprint","IMPRINT",FACE,{"disambiguationData":[TD([[makeQuery(id+"F7.imprint","IMPRINT",EDGE,{"derivedFrom":sQuery(id+"F7.wireOp",EDGE,"E5.24.2.0")}),1.0]])]});
            var Q787;
            Q787=makeQuery(id+"F7.imprint","IMPRINT",FACE,{"disambiguationData":[TD([[makeQuery(id+"F7.imprint","IMPRINT",EDGE,{"derivedFrom":sQuery(id+"F7.wireOp",EDGE,"E5.23.17.0")}),1.0]])]});
            var Q788;
            Q788=makeQuery(id+"F7.imprint","IMPRINT",FACE,{"disambiguationData":[TD([[makeQuery(id+"F7.imprint","IMPRINT",EDGE,{"derivedFrom":sQuery(id+"F7.wireOp",EDGE,"E5.26.20.0")}),1.0]])]});
            var Q789;
            Q789=makeQuery(id+"F7.imprint","IMPRINT",FACE,{"disambiguationData":[TD([[makeQuery(id+"F7.imprint","IMPRINT",EDGE,{"derivedFrom":sQuery(id+"F7.wireOp",EDGE,"E5.26.4.0")}),1.0]])]});
            var Q790;
            Q790=makeQuery(id+"F7.imprint","IMPRINT",FACE,{"disambiguationData":[TD([[makeQuery(id+"F7.imprint","IMPRINT",EDGE,{"derivedFrom":sQuery(id+"F7.wireOp",EDGE,"E5.25.19.0")}),1.0]])]});
            var Q791;
            Q791=makeQuery(id+"F7.imprint","IMPRINT",FACE,{"disambiguationData":[TD([[makeQuery(id+"F7.imprint","IMPRINT",EDGE,{"derivedFrom":sQuery(id+"F7.wireOp",EDGE,"E5.33.5.0")}),1.0]])]});
            var Q792;
            Q792=makeQuery(id+"F7.imprint","IMPRINT",FACE,{"disambiguationData":[TD([[makeQuery(id+"F7.imprint","IMPRINT",EDGE,{"derivedFrom":sQuery(id+"F7.wireOp",EDGE,"E5.3.14.0")}),1.0]])]});
            var Q793;
            Q793=makeQuery(id+"F7.imprint","IMPRINT",FACE,{"disambiguationData":[TD([[makeQuery(id+"F7.imprint","IMPRINT",EDGE,{"derivedFrom":sQuery(id+"F7.wireOp",EDGE,"E5.2.29.0")}),1.0]])]});
            var Q794;
            Q794=makeQuery(id+"F7.imprint","IMPRINT",FACE,{"disambiguationData":[TD([[makeQuery(id+"F7.imprint","IMPRINT",EDGE,{"derivedFrom":sQuery(id+"F7.wireOp",EDGE,"E5.2.13.0")}),1.0]])]});
            var Q795;
            Q795=makeQuery(id+"F7.imprint","IMPRINT",FACE,{"disambiguationData":[TD([[makeQuery(id+"F7.imprint","IMPRINT",EDGE,{"derivedFrom":sQuery(id+"F7.wireOp",EDGE,"E5.1.28.0")}),1.0]])]});
            var Q796;
            Q796=makeQuery(id+"F7.imprint","IMPRINT",FACE,{"disambiguationData":[TD([[makeQuery(id+"F7.imprint","IMPRINT",EDGE,{"derivedFrom":sQuery(id+"F7.wireOp",EDGE,"E5.4.15.0")}),1.0]])]});
            var Q797;
            Q797=makeQuery(id+"F7.imprint","IMPRINT",FACE,{"disambiguationData":[TD([[makeQuery(id+"F7.imprint","IMPRINT",EDGE,{"derivedFrom":sQuery(id+"F7.wireOp",EDGE,"E5.7.18.0")}),1.0]])]});
            var Q798;
            Q798=makeQuery(id+"F7.imprint","IMPRINT",FACE,{"disambiguationData":[TD([[makeQuery(id+"F7.imprint","IMPRINT",EDGE,{"derivedFrom":sQuery(id+"F7.wireOp",EDGE,"E5.7.2.0")}),1.0]])]});
            var Q799;
            Q799=makeQuery(id+"F7.imprint","IMPRINT",FACE,{"disambiguationData":[TD([[makeQuery(id+"F7.imprint","IMPRINT",EDGE,{"derivedFrom":sQuery(id+"F7.wireOp",EDGE,"E5.6.17.0")}),1.0]])]});
            var Q800;
            Q800=makeQuery(id+"F7.imprint","IMPRINT",FACE,{"disambiguationData":[TD([[makeQuery(id+"F7.imprint","IMPRINT",EDGE,{"derivedFrom":sQuery(id+"F7.wireOp",EDGE,"E5.6.1.0")}),1.0]])]});
            var Q801;
            Q801=makeQuery(id+"F7.imprint","IMPRINT",FACE,{"disambiguationData":[TD([[makeQuery(id+"F7.imprint","IMPRINT",EDGE,{"derivedFrom":sQuery(id+"F7.wireOp",EDGE,"E5.9.20.0")}),1.0]])]});
            var Q802;
            Q802=makeQuery(id+"F7.imprint","IMPRINT",FACE,{"disambiguationData":[TD([[makeQuery(id+"F7.imprint","IMPRINT",EDGE,{"derivedFrom":sQuery(id+"F7.wireOp",EDGE,"E5.9.4.0")}),1.0]])]});
            var Q803;
            Q803=makeQuery(id+"F7.imprint","IMPRINT",FACE,{"disambiguationData":[TD([[makeQuery(id+"F7.imprint","IMPRINT",EDGE,{"derivedFrom":sQuery(id+"F7.wireOp",EDGE,"E5.8.19.0")}),1.0]])]});
            var Q804;
            Q804=makeQuery(id+"F7.imprint","IMPRINT",FACE,{"disambiguationData":[TD([[makeQuery(id+"F7.imprint","IMPRINT",EDGE,{"derivedFrom":sQuery(id+"F7.wireOp",EDGE,"E5.8.3.0")}),1.0]])]});
            var Q805;
            Q805=makeQuery(id+"F7.imprint","IMPRINT",FACE,{"disambiguationData":[TD([[makeQuery(id+"F7.imprint","IMPRINT",EDGE,{"derivedFrom":sQuery(id+"F7.wireOp",EDGE,"E5.11.22.0")}),1.0]])]});
            var Q806;
            Q806=makeQuery(id+"F7.imprint","IMPRINT",FACE,{"disambiguationData":[TD([[makeQuery(id+"F7.imprint","IMPRINT",EDGE,{"derivedFrom":sQuery(id+"F7.wireOp",EDGE,"E5.11.6.0")}),1.0]])]});
            var Q807;
            Q807=makeQuery(id+"F7.imprint","IMPRINT",FACE,{"disambiguationData":[TD([[makeQuery(id+"F7.imprint","IMPRINT",EDGE,{"derivedFrom":sQuery(id+"F7.wireOp",EDGE,"E5.13.8.0")}),1.0]])]});
            var Q808;
            Q808=makeQuery(id+"F7.imprint","IMPRINT",FACE,{"disambiguationData":[TD([[makeQuery(id+"F7.imprint","IMPRINT",EDGE,{"derivedFrom":sQuery(id+"F7.wireOp",EDGE,"E5.12.23.0")}),1.0]])]});
            var Q809;
            Q809=makeQuery(id+"F7.imprint","IMPRINT",FACE,{"disambiguationData":[TD([[makeQuery(id+"F7.imprint","IMPRINT",EDGE,{"derivedFrom":sQuery(id+"F7.wireOp",EDGE,"E5.12.7.0")}),1.0]])]});
            var Q810;
            Q810=makeQuery(id+"F7.imprint","IMPRINT",FACE,{"disambiguationData":[TD([[makeQuery(id+"F7.imprint","IMPRINT",EDGE,{"derivedFrom":sQuery(id+"F7.wireOp",EDGE,"E5.14.25.0")}),1.0]])]});
            var Q811;
            Q811=makeQuery(id+"F7.imprint","IMPRINT",FACE,{"disambiguationData":[TD([[makeQuery(id+"F7.imprint","IMPRINT",EDGE,{"derivedFrom":sQuery(id+"F7.wireOp",EDGE,"E5.14.9.0")}),1.0]])]});
            var Q812;
            Q812=makeQuery(id+"F7.imprint","IMPRINT",FACE,{"disambiguationData":[TD([[makeQuery(id+"F7.imprint","IMPRINT",EDGE,{"derivedFrom":sQuery(id+"F7.wireOp",EDGE,"E5.13.24.0")}),1.0]])]});
            var Q813;
            Q813=makeQuery(id+"F7.imprint","IMPRINT",FACE,{"disambiguationData":[TD([[makeQuery(id+"F7.imprint","IMPRINT",EDGE,{"derivedFrom":sQuery(id+"F7.wireOp",EDGE,"E5.32.11.0")}),1.0]])]});
            var Q814;
            Q814=makeQuery(id+"F7.imprint","IMPRINT",FACE,{"disambiguationData":[TD([[makeQuery(id+"F7.imprint","IMPRINT",EDGE,{"derivedFrom":sQuery(id+"F7.wireOp",EDGE,"E5.32.27.0")}),1.0]])]});
            var Q815;
            Q815=makeQuery(id+"F7.imprint","IMPRINT",FACE,{"disambiguationData":[TD([[makeQuery(id+"F7.imprint","IMPRINT",EDGE,{"derivedFrom":sQuery(id+"F7.wireOp",EDGE,"E5.28.23.0")}),1.0]])]});
            var Q816;
            Q816=makeQuery(id+"F7.imprint","IMPRINT",FACE,{"disambiguationData":[TD([[makeQuery(id+"F7.imprint","IMPRINT",EDGE,{"derivedFrom":sQuery(id+"F7.wireOp",EDGE,"E5.28.7.0")}),1.0]])]});
            var Q817;
            Q817=makeQuery(id+"F7.imprint","IMPRINT",FACE,{"disambiguationData":[TD([[makeQuery(id+"F7.imprint","IMPRINT",EDGE,{"derivedFrom":sQuery(id+"F7.wireOp",EDGE,"E5.27.22.0")}),1.0]])]});
            var Q818;
            Q818=makeQuery(id+"F7.imprint","IMPRINT",FACE,{"disambiguationData":[TD([[makeQuery(id+"F7.imprint","IMPRINT",EDGE,{"derivedFrom":sQuery(id+"F7.wireOp",EDGE,"E5.27.6.0")}),1.0]])]});
            var Q819;
            Q819=makeQuery(id+"F7.imprint","IMPRINT",FACE,{"disambiguationData":[TD([[makeQuery(id+"F7.imprint","IMPRINT",EDGE,{"derivedFrom":sQuery(id+"F7.wireOp",EDGE,"E5.30.25.0")}),1.0]])]});
            var Q820;
            Q820=makeQuery(id+"F7.imprint","IMPRINT",FACE,{"disambiguationData":[TD([[makeQuery(id+"F7.imprint","IMPRINT",EDGE,{"derivedFrom":sQuery(id+"F7.wireOp",EDGE,"E5.30.9.0")}),1.0]])]});
            var Q821;
            Q821=makeQuery(id+"F7.imprint","IMPRINT",FACE,{"disambiguationData":[TD([[makeQuery(id+"F7.imprint","IMPRINT",EDGE,{"derivedFrom":sQuery(id+"F7.wireOp",EDGE,"E5.29.24.0")}),1.0]])]});
            var Q822;
            Q822=makeQuery(id+"F7.imprint","IMPRINT",FACE,{"disambiguationData":[TD([[makeQuery(id+"F7.imprint","IMPRINT",EDGE,{"derivedFrom":sQuery(id+"F7.wireOp",EDGE,"E5.29.8.0")}),1.0]])]});
            var Q823;
            Q823=makeQuery(id+"F7.imprint","IMPRINT",FACE,{"disambiguationData":[TD([[makeQuery(id+"F7.imprint","IMPRINT",EDGE,{"derivedFrom":sQuery(id+"F7.wireOp",EDGE,"E5.1.12.0")}),1.0]])]});
            var Q824;
            Q824=makeQuery(id+"F7.imprint","IMPRINT",FACE,{"disambiguationData":[TD([[makeQuery(id+"F7.imprint","IMPRINT",EDGE,{"derivedFrom":sQuery(id+"F7.wireOp",EDGE,"E5.16.27.0")}),1.0]])]});
            var Q825;
            Q825=makeQuery(id+"F7.imprint","IMPRINT",FACE,{"disambiguationData":[TD([[makeQuery(id+"F7.imprint","IMPRINT",EDGE,{"derivedFrom":sQuery(id+"F7.wireOp",EDGE,"E5.16.11.0")}),1.0]])]});
            var Q826;
            Q826=makeQuery(id+"F7.imprint","IMPRINT",FACE,{"disambiguationData":[TD([[makeQuery(id+"F7.imprint","IMPRINT",EDGE,{"derivedFrom":sQuery(id+"F7.wireOp",EDGE,"E5.15.26.0")}),1.0]])]});
            var Q827;
            Q827=makeQuery(id+"F7.imprint","IMPRINT",FACE,{"disambiguationData":[TD([[makeQuery(id+"F7.imprint","IMPRINT",EDGE,{"derivedFrom":sQuery(id+"F7.wireOp",EDGE,"E5.15.10.0")}),1.0]])]});
            var Q828;
            Q828=makeQuery(id+"F7.imprint","IMPRINT",FACE,{"disambiguationData":[TD([[makeQuery(id+"F7.imprint","IMPRINT",EDGE,{"derivedFrom":sQuery(id+"F7.wireOp",EDGE,"E5.18.29.0")}),1.0]])]});
            var Q829;
            Q829=makeQuery(id+"F7.imprint","IMPRINT",FACE,{"disambiguationData":[TD([[makeQuery(id+"F7.imprint","IMPRINT",EDGE,{"derivedFrom":sQuery(id+"F7.wireOp",EDGE,"E5.18.13.0")}),1.0]])]});
            var Q830;
            Q830=makeQuery(id+"F7.imprint","IMPRINT",FACE,{"disambiguationData":[TD([[makeQuery(id+"F7.imprint","IMPRINT",EDGE,{"derivedFrom":sQuery(id+"F7.wireOp",EDGE,"E5.17.28.0")}),1.0]])]});
            var Q831;
            Q831=makeQuery(id+"F7.imprint","IMPRINT",FACE,{"disambiguationData":[TD([[makeQuery(id+"F7.imprint","IMPRINT",EDGE,{"derivedFrom":sQuery(id+"F7.wireOp",EDGE,"E5.17.12.0")}),1.0]])]});
            var Q832;
            Q832=makeQuery(id+"F7.imprint","IMPRINT",FACE,{"disambiguationData":[TD([[makeQuery(id+"F7.imprint","IMPRINT",EDGE,{"derivedFrom":sQuery(id+"F7.wireOp",EDGE,"E5.20.15.0")}),1.0]])]});
            var Q833;
            Q833=makeQuery(id+"F7.imprint","IMPRINT",FACE,{"disambiguationData":[TD([[makeQuery(id+"F7.imprint","IMPRINT",EDGE,{"derivedFrom":sQuery(id+"F7.wireOp",EDGE,"E5.19.14.0")}),1.0]])]});
            var Q834;
            Q834=makeQuery(id+"F7.imprint","IMPRINT",FACE,{"disambiguationData":[TD([[makeQuery(id+"F7.imprint","IMPRINT",EDGE,{"derivedFrom":sQuery(id+"F7.wireOp",EDGE,"E5.23.2.0")}),1.0]])]});
            var Q835;
            Q835=makeQuery(id+"F7.imprint","IMPRINT",FACE,{"disambiguationData":[TD([[makeQuery(id+"F7.imprint","IMPRINT",EDGE,{"derivedFrom":sQuery(id+"F7.wireOp",EDGE,"E5.22.17.0")}),1.0]])]});
            var Q836;
            Q836=makeQuery(id+"F7.imprint","IMPRINT",FACE,{"disambiguationData":[TD([[makeQuery(id+"F7.imprint","IMPRINT",EDGE,{"derivedFrom":sQuery(id+"F7.wireOp",EDGE,"E5.21.16.0")}),1.0]])]});
            var Q837;
            Q837=makeQuery(id+"F7.imprint","IMPRINT",FACE,{"disambiguationData":[TD([[makeQuery(id+"F7.imprint","IMPRINT",EDGE,{"derivedFrom":sQuery(id+"F7.wireOp",EDGE,"E5.25.4.0")}),1.0]])]});
            var Q838;
            Q838=makeQuery(id+"F7.imprint","IMPRINT",FACE,{"disambiguationData":[TD([[makeQuery(id+"F7.imprint","IMPRINT",EDGE,{"derivedFrom":sQuery(id+"F7.wireOp",EDGE,"E5.24.19.0")}),1.0]])]});
            var Q839;
            Q839=makeQuery(id+"F7.imprint","IMPRINT",FACE,{"disambiguationData":[TD([[makeQuery(id+"F7.imprint","IMPRINT",EDGE,{"derivedFrom":sQuery(id+"F7.wireOp",EDGE,"E5.24.3.0")}),1.0]])]});
            var Q840;
            Q840=makeQuery(id+"F7.imprint","IMPRINT",FACE,{"disambiguationData":[TD([[makeQuery(id+"F7.imprint","IMPRINT",EDGE,{"derivedFrom":sQuery(id+"F7.wireOp",EDGE,"E5.23.18.0")}),1.0]])]});
            var Q841;
            Q841=makeQuery(id+"F7.imprint","IMPRINT",FACE,{"disambiguationData":[TD([[makeQuery(id+"F7.imprint","IMPRINT",EDGE,{"derivedFrom":sQuery(id+"F7.wireOp",EDGE,"E5.25.20.0")}),1.0]])]});
            var Q842;
            Q842=makeQuery(id+"F7.imprint","IMPRINT",FACE,{"disambiguationData":[TD([[makeQuery(id+"F7.imprint","IMPRINT",EDGE,{"derivedFrom":sQuery(id+"F7.wireOp",EDGE,"E5.5.17.0")}),1.0]])]});
            var Q843;
            Q843=makeQuery(id+"F7.imprint","IMPRINT",FACE,{"disambiguationData":[TD([[makeQuery(id+"F7.imprint","IMPRINT",EDGE,{"derivedFrom":sQuery(id+"F7.wireOp",EDGE,"E5.5.1.0")}),1.0]])]});
            var Q844;
            Q844=makeQuery(id+"F7.imprint","IMPRINT",FACE,{"disambiguationData":[TD([[makeQuery(id+"F7.imprint","IMPRINT",EDGE,{"derivedFrom":sQuery(id+"F7.wireOp",EDGE,"E5.4.16.0")}),1.0]])]});
            var Q845;
            Q845=makeQuery(id+"F7.imprint","IMPRINT",FACE,{"disambiguationData":[TD([[makeQuery(id+"F7.imprint","IMPRINT",EDGE,{"derivedFrom":sQuery(id+"F7.wireOp",EDGE,"E5.7.19.0")}),1.0]])]});
            var Q846;
            Q846=makeQuery(id+"F7.imprint","IMPRINT",FACE,{"disambiguationData":[TD([[makeQuery(id+"F7.imprint","IMPRINT",EDGE,{"derivedFrom":sQuery(id+"F7.wireOp",EDGE,"E5.7.3.0")}),1.0]])]});
            var Q847;
            Q847=makeQuery(id+"F7.imprint","IMPRINT",FACE,{"disambiguationData":[TD([[makeQuery(id+"F7.imprint","IMPRINT",EDGE,{"derivedFrom":sQuery(id+"F7.wireOp",EDGE,"E5.6.18.0")}),1.0]])]});
            var Q848;
            Q848=makeQuery(id+"F7.imprint","IMPRINT",FACE,{"disambiguationData":[TD([[makeQuery(id+"F7.imprint","IMPRINT",EDGE,{"derivedFrom":sQuery(id+"F7.wireOp",EDGE,"E5.6.2.0")}),1.0]])]});
            var Q849;
            Q849=makeQuery(id+"F7.imprint","IMPRINT",FACE,{"disambiguationData":[TD([[makeQuery(id+"F7.imprint","IMPRINT",EDGE,{"derivedFrom":sQuery(id+"F7.wireOp",EDGE,"E5.9.5.0")}),1.0]])]});
            var Q850;
            Q850=makeQuery(id+"F7.imprint","IMPRINT",FACE,{"disambiguationData":[TD([[makeQuery(id+"F7.imprint","IMPRINT",EDGE,{"derivedFrom":sQuery(id+"F7.wireOp",EDGE,"E5.8.20.0")}),1.0]])]});
            var Q851;
            Q851=makeQuery(id+"F7.imprint","IMPRINT",FACE,{"disambiguationData":[TD([[makeQuery(id+"F7.imprint","IMPRINT",EDGE,{"derivedFrom":sQuery(id+"F7.wireOp",EDGE,"E5.8.4.0")}),1.0]])]});
            var Q852;
            Q852=makeQuery(id+"F7.imprint","IMPRINT",FACE,{"disambiguationData":[TD([[makeQuery(id+"F7.imprint","IMPRINT",EDGE,{"derivedFrom":sQuery(id+"F7.wireOp",EDGE,"E5.11.23.0")}),1.0]])]});
            var Q853;
            Q853=makeQuery(id+"F7.imprint","IMPRINT",FACE,{"disambiguationData":[TD([[makeQuery(id+"F7.imprint","IMPRINT",EDGE,{"derivedFrom":sQuery(id+"F7.wireOp",EDGE,"E5.11.7.0")}),1.0]])]});
            var Q854;
            Q854=makeQuery(id+"F7.imprint","IMPRINT",FACE,{"disambiguationData":[TD([[makeQuery(id+"F7.imprint","IMPRINT",EDGE,{"derivedFrom":sQuery(id+"F7.wireOp",EDGE,"E5.10.22.0")}),1.0]])]});
            var Q855;
            Q855=makeQuery(id+"F7.imprint","IMPRINT",FACE,{"disambiguationData":[TD([[makeQuery(id+"F7.imprint","IMPRINT",EDGE,{"derivedFrom":sQuery(id+"F7.wireOp",EDGE,"E5.13.9.0")}),1.0]])]});
            var Q856;
            Q856=makeQuery(id+"F7.imprint","IMPRINT",FACE,{"disambiguationData":[TD([[makeQuery(id+"F7.imprint","IMPRINT",EDGE,{"derivedFrom":sQuery(id+"F7.wireOp",EDGE,"E5.12.24.0")}),1.0]])]});
            var Q857;
            Q857=makeQuery(id+"F7.imprint","IMPRINT",FACE,{"disambiguationData":[TD([[makeQuery(id+"F7.imprint","IMPRINT",EDGE,{"derivedFrom":sQuery(id+"F7.wireOp",EDGE,"E5.12.8.0")}),1.0]])]});
            var Q858;
            Q858=makeQuery(id+"F7.imprint","IMPRINT",FACE,{"disambiguationData":[TD([[makeQuery(id+"F7.imprint","IMPRINT",EDGE,{"derivedFrom":sQuery(id+"F7.wireOp",EDGE,"E5.13.25.0")}),1.0]])]});
            var Q859;
            Q859=makeQuery(id+"F7.imprint","IMPRINT",FACE,{"disambiguationData":[TD([[makeQuery(id+"F7.imprint","IMPRINT",EDGE,{"derivedFrom":sQuery(id+"F7.wireOp",EDGE,"E5.16.28.0")}),1.0]])]});
            var Q860;
            Q860=makeQuery(id+"F7.imprint","IMPRINT",FACE,{"disambiguationData":[TD([[makeQuery(id+"F7.imprint","IMPRINT",EDGE,{"derivedFrom":sQuery(id+"F7.wireOp",EDGE,"E5.16.12.0")}),1.0]])]});
            var Q861;
            Q861=makeQuery(id+"F7.imprint","IMPRINT",FACE,{"disambiguationData":[TD([[makeQuery(id+"F7.imprint","IMPRINT",EDGE,{"derivedFrom":sQuery(id+"F7.wireOp",EDGE,"E5.15.27.0")}),1.0]])]});
            var Q862;
            Q862=makeQuery(id+"F7.imprint","IMPRINT",FACE,{"disambiguationData":[TD([[makeQuery(id+"F7.imprint","IMPRINT",EDGE,{"derivedFrom":sQuery(id+"F7.wireOp",EDGE,"E5.15.11.0")}),1.0]])]});
            var Q863;
            Q863=makeQuery(id+"F7.imprint","IMPRINT",FACE,{"disambiguationData":[TD([[makeQuery(id+"F7.imprint","IMPRINT",EDGE,{"derivedFrom":sQuery(id+"F7.wireOp",EDGE,"E5.32.12.0")}),1.0]])]});
            var Q864;
            Q864=makeQuery(id+"F7.imprint","IMPRINT",FACE,{"disambiguationData":[TD([[makeQuery(id+"F7.imprint","IMPRINT",EDGE,{"derivedFrom":sQuery(id+"F7.wireOp",EDGE,"E5.32.28.0")}),1.0]])]});
            var Q865;
            Q865=makeQuery(id+"F7.imprint","IMPRINT",FACE,{"disambiguationData":[TD([[makeQuery(id+"F7.imprint","IMPRINT",EDGE,{"derivedFrom":sQuery(id+"F7.wireOp",EDGE,"E5.28.24.0")}),1.0]])]});
            var Q866;
            Q866=makeQuery(id+"F7.imprint","IMPRINT",FACE,{"disambiguationData":[TD([[makeQuery(id+"F7.imprint","IMPRINT",EDGE,{"derivedFrom":sQuery(id+"F7.wireOp",EDGE,"E5.28.8.0")}),1.0]])]});
            var Q867;
            Q867=makeQuery(id+"F7.imprint","IMPRINT",FACE,{"disambiguationData":[TD([[makeQuery(id+"F7.imprint","IMPRINT",EDGE,{"derivedFrom":sQuery(id+"F7.wireOp",EDGE,"E5.27.23.0")}),1.0]])]});
            var Q868;
            Q868=makeQuery(id+"F7.imprint","IMPRINT",FACE,{"disambiguationData":[TD([[makeQuery(id+"F7.imprint","IMPRINT",EDGE,{"derivedFrom":sQuery(id+"F7.wireOp",EDGE,"E5.27.7.0")}),1.0]])]});
            var Q869;
            Q869=makeQuery(id+"F7.imprint","IMPRINT",FACE,{"disambiguationData":[TD([[makeQuery(id+"F7.imprint","IMPRINT",EDGE,{"derivedFrom":sQuery(id+"F7.wireOp",EDGE,"E5.30.10.0")}),1.0]])]});
            var Q870;
            Q870=makeQuery(id+"F7.imprint","IMPRINT",FACE,{"disambiguationData":[TD([[makeQuery(id+"F7.imprint","IMPRINT",EDGE,{"derivedFrom":sQuery(id+"F7.wireOp",EDGE,"E5.29.25.0")}),1.0]])]});
            var Q871;
            Q871=makeQuery(id+"F7.imprint","IMPRINT",FACE,{"disambiguationData":[TD([[makeQuery(id+"F7.imprint","IMPRINT",EDGE,{"derivedFrom":sQuery(id+"F7.wireOp",EDGE,"E5.29.9.0")}),1.0]])]});
            var Q872;
            Q872=makeQuery(id+"F7.imprint","IMPRINT",FACE,{"disambiguationData":[TD([[makeQuery(id+"F7.imprint","IMPRINT",EDGE,{"derivedFrom":sQuery(id+"F7.wireOp",EDGE,"E5.31.27.0")}),1.0]])]});
            var Q873;
            Q873=makeQuery(id+"F7.imprint","IMPRINT",FACE,{"disambiguationData":[TD([[makeQuery(id+"F7.imprint","IMPRINT",EDGE,{"derivedFrom":sQuery(id+"F7.wireOp",EDGE,"E5.1.13.0")}),1.0]])]});
            var Q874;
            Q874=makeQuery(id+"F7.imprint","IMPRINT",FACE,{"disambiguationData":[TD([[makeQuery(id+"F7.imprint","IMPRINT",EDGE,{"derivedFrom":sQuery(id+"F7.wireOp",EDGE,"E5.3.15.0")}),1.0]])]});
            var Q875;
            Q875=makeQuery(id+"F7.imprint","IMPRINT",FACE,{"disambiguationData":[TD([[makeQuery(id+"F7.imprint","IMPRINT",EDGE,{"derivedFrom":sQuery(id+"F7.wireOp",EDGE,"E5.2.14.0")}),1.0]])]});
            var Q876;
            Q876=makeQuery(id+"F7.imprint","IMPRINT",FACE,{"disambiguationData":[TD([[makeQuery(id+"F7.imprint","IMPRINT",EDGE,{"derivedFrom":sQuery(id+"F7.wireOp",EDGE,"E5.1.29.0")}),1.0]])]});
            var Q877;
            Q877=makeQuery(id+"F7.imprint","IMPRINT",FACE,{"disambiguationData":[TD([[makeQuery(id+"F7.imprint","IMPRINT",EDGE,{"derivedFrom":sQuery(id+"F7.wireOp",EDGE,"E5.32.13.0")}),1.0]])]});
            var Q878;
            Q878=makeQuery(id+"F7.imprint","IMPRINT",FACE,{"disambiguationData":[TD([[makeQuery(id+"F7.imprint","IMPRINT",EDGE,{"derivedFrom":sQuery(id+"F7.wireOp",EDGE,"E5.18.14.0")}),1.0]])]});
            var Q879;
            Q879=makeQuery(id+"F7.imprint","IMPRINT",FACE,{"disambiguationData":[TD([[makeQuery(id+"F7.imprint","IMPRINT",EDGE,{"derivedFrom":sQuery(id+"F7.wireOp",EDGE,"E5.17.29.0")}),1.0]])]});
            var Q880;
            Q880=makeQuery(id+"F7.imprint","IMPRINT",FACE,{"disambiguationData":[TD([[makeQuery(id+"F7.imprint","IMPRINT",EDGE,{"derivedFrom":sQuery(id+"F7.wireOp",EDGE,"E5.17.13.0")}),1.0]])]});
            var Q881;
            Q881=makeQuery(id+"F7.imprint","IMPRINT",FACE,{"disambiguationData":[TD([[makeQuery(id+"F7.imprint","IMPRINT",EDGE,{"derivedFrom":sQuery(id+"F7.wireOp",EDGE,"E5.21.1.0")}),1.0]])]});
            var Q882;
            Q882=makeQuery(id+"F7.imprint","IMPRINT",FACE,{"disambiguationData":[TD([[makeQuery(id+"F7.imprint","IMPRINT",EDGE,{"derivedFrom":sQuery(id+"F7.wireOp",EDGE,"E5.20.16.0")}),1.0]])]});
            var Q883;
            Q883=makeQuery(id+"F7.imprint","IMPRINT",FACE,{"disambiguationData":[TD([[makeQuery(id+"F7.imprint","IMPRINT",EDGE,{"derivedFrom":sQuery(id+"F7.wireOp",EDGE,"E5.19.15.0")}),1.0]])]});
            var Q884;
            Q884=makeQuery(id+"F7.imprint","IMPRINT",FACE,{"disambiguationData":[TD([[makeQuery(id+"F7.imprint","IMPRINT",EDGE,{"derivedFrom":sQuery(id+"F7.wireOp",EDGE,"E5.23.3.0")}),1.0]])]});
            var Q885;
            Q885=makeQuery(id+"F7.imprint","IMPRINT",FACE,{"disambiguationData":[TD([[makeQuery(id+"F7.imprint","IMPRINT",EDGE,{"derivedFrom":sQuery(id+"F7.wireOp",EDGE,"E5.22.18.0")}),1.0]])]});
            var Q886;
            Q886=makeQuery(id+"F7.imprint","IMPRINT",FACE,{"disambiguationData":[TD([[makeQuery(id+"F7.imprint","IMPRINT",EDGE,{"derivedFrom":sQuery(id+"F7.wireOp",EDGE,"E5.22.2.0")}),1.0]])]});
            var Q887;
            Q887=makeQuery(id+"F7.imprint","IMPRINT",FACE,{"disambiguationData":[TD([[makeQuery(id+"F7.imprint","IMPRINT",EDGE,{"derivedFrom":sQuery(id+"F7.wireOp",EDGE,"E5.21.17.0")}),1.0]])]});
            var Q888;
            Q888=makeQuery(id+"F7.imprint","IMPRINT",FACE,{"disambiguationData":[TD([[makeQuery(id+"F7.imprint","IMPRINT",EDGE,{"derivedFrom":sQuery(id+"F7.wireOp",EDGE,"E5.25.5.0")}),1.0]])]});
            var Q889;
            Q889=makeQuery(id+"F7.imprint","IMPRINT",FACE,{"disambiguationData":[TD([[makeQuery(id+"F7.imprint","IMPRINT",EDGE,{"derivedFrom":sQuery(id+"F7.wireOp",EDGE,"E5.24.20.0")}),1.0]])]});
            var Q890;
            Q890=makeQuery(id+"F7.imprint","IMPRINT",FACE,{"disambiguationData":[TD([[makeQuery(id+"F7.imprint","IMPRINT",EDGE,{"derivedFrom":sQuery(id+"F7.wireOp",EDGE,"E5.24.4.0")}),1.0]])]});
            var Q891;
            Q891=makeQuery(id+"F7.imprint","IMPRINT",FACE,{"disambiguationData":[TD([[makeQuery(id+"F7.imprint","IMPRINT",EDGE,{"derivedFrom":sQuery(id+"F7.wireOp",EDGE,"E5.23.19.0")}),1.0]])]});
            var Q892;
            Q892=makeQuery(id+"F7.imprint","IMPRINT",FACE,{"disambiguationData":[TD([[makeQuery(id+"F7.imprint","IMPRINT",EDGE,{"derivedFrom":sQuery(id+"F7.wireOp",EDGE,"E5.26.22.0")}),1.0]])]});
            var Q893;
            Q893=makeQuery(id+"F7.imprint","IMPRINT",FACE,{"disambiguationData":[TD([[makeQuery(id+"F7.imprint","IMPRINT",EDGE,{"derivedFrom":sQuery(id+"F7.wireOp",EDGE,"E5.26.6.0")}),1.0]])]});
            var Q894;
            Q894=makeQuery(id+"F7.imprint","IMPRINT",FACE,{"disambiguationData":[TD([[makeQuery(id+"F7.imprint","IMPRINT",EDGE,{"derivedFrom":sQuery(id+"F7.wireOp",EDGE,"E5.25.21.0")}),1.0]])]});
            var Q895;
            Q895=makeQuery(id+"F7.imprint","IMPRINT",FACE,{"disambiguationData":[TD([[makeQuery(id+"F7.imprint","IMPRINT",EDGE,{"derivedFrom":sQuery(id+"F7.wireOp",EDGE,"E5.7.20.0")}),1.0]])]});
            var Q896;
            Q896=makeQuery(id+"F7.imprint","IMPRINT",FACE,{"disambiguationData":[TD([[makeQuery(id+"F7.imprint","IMPRINT",EDGE,{"derivedFrom":sQuery(id+"F7.wireOp",EDGE,"E5.7.4.0")}),1.0]])]});
            var Q897;
            Q897=makeQuery(id+"F7.imprint","IMPRINT",FACE,{"disambiguationData":[TD([[makeQuery(id+"F7.imprint","IMPRINT",EDGE,{"derivedFrom":sQuery(id+"F7.wireOp",EDGE,"E5.6.19.0")}),1.0]])]});
            var Q898;
            Q898=makeQuery(id+"F7.imprint","IMPRINT",FACE,{"disambiguationData":[TD([[makeQuery(id+"F7.imprint","IMPRINT",EDGE,{"derivedFrom":sQuery(id+"F7.wireOp",EDGE,"E5.6.3.0")}),1.0]])]});
            var Q899;
            Q899=makeQuery(id+"F7.imprint","IMPRINT",FACE,{"disambiguationData":[TD([[makeQuery(id+"F7.imprint","IMPRINT",EDGE,{"derivedFrom":sQuery(id+"F7.wireOp",EDGE,"E5.9.22.0")}),1.0]])]});
            var Q900;
            Q900=makeQuery(id+"F7.imprint","IMPRINT",FACE,{"disambiguationData":[TD([[makeQuery(id+"F7.imprint","IMPRINT",EDGE,{"derivedFrom":sQuery(id+"F7.wireOp",EDGE,"E5.9.6.0")}),1.0]])]});
            var Q901;
            Q901=makeQuery(id+"F7.imprint","IMPRINT",FACE,{"disambiguationData":[TD([[makeQuery(id+"F7.imprint","IMPRINT",EDGE,{"derivedFrom":sQuery(id+"F7.wireOp",EDGE,"E5.8.21.0")}),1.0]])]});
            var Q902;
            Q902=makeQuery(id+"F7.imprint","IMPRINT",FACE,{"disambiguationData":[TD([[makeQuery(id+"F7.imprint","IMPRINT",EDGE,{"derivedFrom":sQuery(id+"F7.wireOp",EDGE,"E5.8.5.0")}),1.0]])]});
            var Q903;
            Q903=makeQuery(id+"F7.imprint","IMPRINT",FACE,{"disambiguationData":[TD([[makeQuery(id+"F7.imprint","IMPRINT",EDGE,{"derivedFrom":sQuery(id+"F7.wireOp",EDGE,"E5.11.24.0")}),1.0]])]});
            var Q904;
            Q904=makeQuery(id+"F7.imprint","IMPRINT",FACE,{"disambiguationData":[TD([[makeQuery(id+"F7.imprint","IMPRINT",EDGE,{"derivedFrom":sQuery(id+"F7.wireOp",EDGE,"E5.11.8.0")}),1.0]])]});
            var Q905;
            Q905=makeQuery(id+"F7.imprint","IMPRINT",FACE,{"disambiguationData":[TD([[makeQuery(id+"F7.imprint","IMPRINT",EDGE,{"derivedFrom":sQuery(id+"F7.wireOp",EDGE,"E5.10.23.0")}),1.0]])]});
            var Q906;
            Q906=makeQuery(id+"F7.imprint","IMPRINT",FACE,{"disambiguationData":[TD([[makeQuery(id+"F7.imprint","IMPRINT",EDGE,{"derivedFrom":sQuery(id+"F7.wireOp",EDGE,"E5.10.7.0")}),1.0]])]});
            var Q907;
            Q907=makeQuery(id+"F7.imprint","IMPRINT",FACE,{"disambiguationData":[TD([[makeQuery(id+"F7.imprint","IMPRINT",EDGE,{"derivedFrom":sQuery(id+"F7.wireOp",EDGE,"E5.13.10.0")}),1.0]])]});
            var Q908;
            Q908=makeQuery(id+"F7.imprint","IMPRINT",FACE,{"disambiguationData":[TD([[makeQuery(id+"F7.imprint","IMPRINT",EDGE,{"derivedFrom":sQuery(id+"F7.wireOp",EDGE,"E5.12.25.0")}),1.0]])]});
            var Q909;
            Q909=makeQuery(id+"F7.imprint","IMPRINT",FACE,{"disambiguationData":[TD([[makeQuery(id+"F7.imprint","IMPRINT",EDGE,{"derivedFrom":sQuery(id+"F7.wireOp",EDGE,"E5.12.9.0")}),1.0]])]});
            var Q910;
            Q910=makeQuery(id+"F7.imprint","IMPRINT",FACE,{"disambiguationData":[TD([[makeQuery(id+"F7.imprint","IMPRINT",EDGE,{"derivedFrom":sQuery(id+"F7.wireOp",EDGE,"E5.13.26.0")}),1.0]])]});
            var Q911;
            Q911=makeQuery(id+"F7.imprint","IMPRINT",FACE,{"disambiguationData":[TD([[makeQuery(id+"F7.imprint","IMPRINT",EDGE,{"derivedFrom":sQuery(id+"F7.wireOp",EDGE,"E5.16.29.0")}),1.0]])]});
            var Q912;
            Q912=makeQuery(id+"F7.imprint","IMPRINT",FACE,{"disambiguationData":[TD([[makeQuery(id+"F7.imprint","IMPRINT",EDGE,{"derivedFrom":sQuery(id+"F7.wireOp",EDGE,"E5.16.13.0")}),1.0]])]});
            var Q913;
            Q913=makeQuery(id+"F7.imprint","IMPRINT",FACE,{"disambiguationData":[TD([[makeQuery(id+"F7.imprint","IMPRINT",EDGE,{"derivedFrom":sQuery(id+"F7.wireOp",EDGE,"E5.15.28.0")}),1.0]])]});
            var Q914;
            Q914=makeQuery(id+"F7.imprint","IMPRINT",FACE,{"disambiguationData":[TD([[makeQuery(id+"F7.imprint","IMPRINT",EDGE,{"derivedFrom":sQuery(id+"F7.wireOp",EDGE,"E5.15.12.0")}),1.0]])]});
            var Q915;
            Q915=makeQuery(id+"F7.imprint","IMPRINT",FACE,{"disambiguationData":[TD([[makeQuery(id+"F7.imprint","IMPRINT",EDGE,{"derivedFrom":sQuery(id+"F7.wireOp",EDGE,"E5.17.14.0")}),1.0]])]});
            var Q916;
            Q916=makeQuery(id+"F7.imprint","IMPRINT",FACE,{"disambiguationData":[TD([[makeQuery(id+"F7.imprint","IMPRINT",EDGE,{"derivedFrom":sQuery(id+"F7.wireOp",EDGE,"E5.32.29.0")}),1.0]])]});
            var Q917;
            Q917=makeQuery(id+"F7.imprint","IMPRINT",FACE,{"disambiguationData":[TD([[makeQuery(id+"F7.imprint","IMPRINT",EDGE,{"derivedFrom":sQuery(id+"F7.wireOp",EDGE,"E5.28.25.0")}),1.0]])]});
            var Q918;
            Q918=makeQuery(id+"F7.imprint","IMPRINT",FACE,{"disambiguationData":[TD([[makeQuery(id+"F7.imprint","IMPRINT",EDGE,{"derivedFrom":sQuery(id+"F7.wireOp",EDGE,"E5.28.9.0")}),1.0]])]});
            var Q919;
            Q919=makeQuery(id+"F7.imprint","IMPRINT",FACE,{"disambiguationData":[TD([[makeQuery(id+"F7.imprint","IMPRINT",EDGE,{"derivedFrom":sQuery(id+"F7.wireOp",EDGE,"E5.27.24.0")}),1.0]])]});
            var Q920;
            Q920=makeQuery(id+"F7.imprint","IMPRINT",FACE,{"disambiguationData":[TD([[makeQuery(id+"F7.imprint","IMPRINT",EDGE,{"derivedFrom":sQuery(id+"F7.wireOp",EDGE,"E5.27.8.0")}),1.0]])]});
            var Q921;
            Q921=makeQuery(id+"F7.imprint","IMPRINT",FACE,{"disambiguationData":[TD([[makeQuery(id+"F7.imprint","IMPRINT",EDGE,{"derivedFrom":sQuery(id+"F7.wireOp",EDGE,"E5.30.27.0")}),1.0]])]});
            var Q922;
            Q922=makeQuery(id+"F7.imprint","IMPRINT",FACE,{"disambiguationData":[TD([[makeQuery(id+"F7.imprint","IMPRINT",EDGE,{"derivedFrom":sQuery(id+"F7.wireOp",EDGE,"E5.29.26.0")}),1.0]])]});
            var Q923;
            Q923=makeQuery(id+"F7.imprint","IMPRINT",FACE,{"disambiguationData":[TD([[makeQuery(id+"F7.imprint","IMPRINT",EDGE,{"derivedFrom":sQuery(id+"F7.wireOp",EDGE,"E5.29.10.0")}),1.0]])]});
            var Q924;
            Q924=makeQuery(id+"F7.imprint","IMPRINT",FACE,{"disambiguationData":[TD([[makeQuery(id+"F7.imprint","IMPRINT",EDGE,{"derivedFrom":sQuery(id+"F7.wireOp",EDGE,"E5.31.28.0")}),1.0]])]});
            var Q925;
            Q925=makeQuery(id+"F7.imprint","IMPRINT",FACE,{"disambiguationData":[TD([[makeQuery(id+"F7.imprint","IMPRINT",EDGE,{"derivedFrom":sQuery(id+"F7.wireOp",EDGE,"E5.31.12.0")}),1.0]])]});
            var Q926;
            Q926=makeQuery(id+"F7.imprint","IMPRINT",FACE,{"disambiguationData":[TD([[makeQuery(id+"F7.imprint","IMPRINT",EDGE,{"derivedFrom":sQuery(id+"F7.wireOp",EDGE,"E5.1.14.0")}),1.0]])]});
            var Q927;
            Q927=makeQuery(id+"F7.imprint","IMPRINT",FACE,{"disambiguationData":[TD([[makeQuery(id+"F7.imprint","IMPRINT",EDGE,{"derivedFrom":sQuery(id+"F7.wireOp",EDGE,"E5.3.16.0")}),1.0]])]});
            var Q928;
            Q928=makeQuery(id+"F7.imprint","IMPRINT",FACE,{"disambiguationData":[TD([[makeQuery(id+"F7.imprint","IMPRINT",EDGE,{"derivedFrom":sQuery(id+"F7.wireOp",EDGE,"E5.2.15.0")}),1.0]])]});
            var Q929;
            Q929=makeQuery(id+"F7.imprint","IMPRINT",FACE,{"disambiguationData":[TD([[makeQuery(id+"F7.imprint","IMPRINT",EDGE,{"derivedFrom":sQuery(id+"F7.wireOp",EDGE,"E5.5.18.0")}),1.0]])]});
            var Q930;
            Q930=makeQuery(id+"F7.imprint","IMPRINT",FACE,{"disambiguationData":[TD([[makeQuery(id+"F7.imprint","IMPRINT",EDGE,{"derivedFrom":sQuery(id+"F7.wireOp",EDGE,"E5.5.2.0")}),1.0]])]});
            var Q931;
            Q931=makeQuery(id+"F7.imprint","IMPRINT",FACE,{"disambiguationData":[TD([[makeQuery(id+"F7.imprint","IMPRINT",EDGE,{"derivedFrom":sQuery(id+"F7.wireOp",EDGE,"E5.4.17.0")}),1.0]])]});
            var Q932;
            Q932=makeQuery(id+"F7.imprint","IMPRINT",FACE,{"disambiguationData":[TD([[makeQuery(id+"F7.imprint","IMPRINT",EDGE,{"derivedFrom":sQuery(id+"F7.wireOp",EDGE,"E5.4.1.0")}),1.0]])]});
            var Q933;
            Q933=makeQuery(id+"F7.imprint","IMPRINT",FACE,{"disambiguationData":[TD([[makeQuery(id+"F7.imprint","IMPRINT",EDGE,{"derivedFrom":sQuery(id+"F7.wireOp",EDGE,"E5.21.2.0")}),1.0]])]});
            var Q934;
            Q934=makeQuery(id+"F7.imprint","IMPRINT",FACE,{"disambiguationData":[TD([[makeQuery(id+"F7.imprint","IMPRINT",EDGE,{"derivedFrom":sQuery(id+"F7.wireOp",EDGE,"E5.20.17.0")}),1.0]])]});
            var Q935;
            Q935=makeQuery(id+"F7.imprint","IMPRINT",FACE,{"disambiguationData":[TD([[makeQuery(id+"F7.imprint","IMPRINT",EDGE,{"derivedFrom":sQuery(id+"F7.wireOp",EDGE,"E5.20.1.0")}),1.0]])]});
            var Q936;
            Q936=makeQuery(id+"F7.imprint","IMPRINT",FACE,{"disambiguationData":[TD([[makeQuery(id+"F7.imprint","IMPRINT",EDGE,{"derivedFrom":sQuery(id+"F7.wireOp",EDGE,"E5.19.16.0")}),1.0]])]});
            var Q937;
            Q937=makeQuery(id+"F7.imprint","IMPRINT",FACE,{"disambiguationData":[TD([[makeQuery(id+"F7.imprint","IMPRINT",EDGE,{"derivedFrom":sQuery(id+"F7.wireOp",EDGE,"E5.23.4.0")}),1.0]])]});
            var Q938;
            Q938=makeQuery(id+"F7.imprint","IMPRINT",FACE,{"disambiguationData":[TD([[makeQuery(id+"F7.imprint","IMPRINT",EDGE,{"derivedFrom":sQuery(id+"F7.wireOp",EDGE,"E5.22.19.0")}),1.0]])]});
            var Q939;
            Q939=makeQuery(id+"F7.imprint","IMPRINT",FACE,{"disambiguationData":[TD([[makeQuery(id+"F7.imprint","IMPRINT",EDGE,{"derivedFrom":sQuery(id+"F7.wireOp",EDGE,"E5.22.3.0")}),1.0]])]});
            var Q940;
            Q940=makeQuery(id+"F7.imprint","IMPRINT",FACE,{"disambiguationData":[TD([[makeQuery(id+"F7.imprint","IMPRINT",EDGE,{"derivedFrom":sQuery(id+"F7.wireOp",EDGE,"E5.21.18.0")}),1.0]])]});
            var Q941;
            Q941=makeQuery(id+"F7.imprint","IMPRINT",FACE,{"disambiguationData":[TD([[makeQuery(id+"F7.imprint","IMPRINT",EDGE,{"derivedFrom":sQuery(id+"F7.wireOp",EDGE,"E5.25.6.0")}),1.0]])]});
            var Q942;
            Q942=makeQuery(id+"F7.imprint","IMPRINT",FACE,{"disambiguationData":[TD([[makeQuery(id+"F7.imprint","IMPRINT",EDGE,{"derivedFrom":sQuery(id+"F7.wireOp",EDGE,"E5.24.21.0")}),1.0]])]});
            var Q943;
            Q943=makeQuery(id+"F7.imprint","IMPRINT",FACE,{"disambiguationData":[TD([[makeQuery(id+"F7.imprint","IMPRINT",EDGE,{"derivedFrom":sQuery(id+"F7.wireOp",EDGE,"E5.24.5.0")}),1.0]])]});
            var Q944;
            Q944=makeQuery(id+"F7.imprint","IMPRINT",FACE,{"disambiguationData":[TD([[makeQuery(id+"F7.imprint","IMPRINT",EDGE,{"derivedFrom":sQuery(id+"F7.wireOp",EDGE,"E5.23.20.0")}),1.0]])]});
            var Q945;
            Q945=makeQuery(id+"F7.imprint","IMPRINT",FACE,{"disambiguationData":[TD([[makeQuery(id+"F7.imprint","IMPRINT",EDGE,{"derivedFrom":sQuery(id+"F7.wireOp",EDGE,"E5.26.23.0")}),1.0]])]});
            var Q946;
            Q946=makeQuery(id+"F7.imprint","IMPRINT",FACE,{"disambiguationData":[TD([[makeQuery(id+"F7.imprint","IMPRINT",EDGE,{"derivedFrom":sQuery(id+"F7.wireOp",EDGE,"E5.26.7.0")}),1.0]])]});
            var Q947;
            Q947=makeQuery(id+"F7.imprint","IMPRINT",FACE,{"disambiguationData":[TD([[makeQuery(id+"F7.imprint","IMPRINT",EDGE,{"derivedFrom":sQuery(id+"F7.wireOp",EDGE,"E5.25.22.0")}),1.0]])]});
            var Q948;
            Q948=makeQuery(id+"F7.imprint","IMPRINT",FACE,{"disambiguationData":[TD([[makeQuery(id+"F7.imprint","IMPRINT",EDGE,{"derivedFrom":sQuery(id+"F7.wireOp",EDGE,"E5.33.25.0")}),1.0]])]});
            var Q949;
            Q949=makeQuery(id+"F7.imprint","IMPRINT",FACE,{"disambiguationData":[TD([[makeQuery(id+"F7.imprint","IMPRINT",EDGE,{"derivedFrom":sQuery(id+"F7.wireOp",EDGE,"E5.33.9.0")}),1.0]])]});
            var Q950;
            Q950=makeQuery(id+"F7.imprint","IMPRINT",FACE,{"disambiguationData":[TD([[makeQuery(id+"F7.imprint","IMPRINT",EDGE,{"derivedFrom":sQuery(id+"F7.wireOp",EDGE,"E5.33.15.0")}),1.0]])]});
            var Q951;
            Q951=makeQuery(id+"F7.imprint","IMPRINT",FACE,{"disambiguationData":[TD([[makeQuery(id+"F7.imprint","IMPRINT",EDGE,{"derivedFrom":sQuery(id+"F7.wireOp",EDGE,"E5.33.2.0")}),1.0]])]});
            var Q952;
            Q952=makeQuery(id+"F7.imprint","IMPRINT",FACE,{"disambiguationData":[TD([[makeQuery(id+"F7.imprint","IMPRINT",EDGE,{"derivedFrom":sQuery(id+"F7.wireOp",EDGE,"E5.33.18.0")}),1.0]])]});
            var Q953;
            Q953=makeQuery(id+"F7.imprint","IMPRINT",FACE,{"disambiguationData":[TD([[makeQuery(id+"F7.imprint","IMPRINT",EDGE,{"derivedFrom":sQuery(id+"F7.wireOp",EDGE,"E5.33.13.0")}),1.0]])]});
            var Q954;
            Q954=makeQuery(id+"F7.imprint","IMPRINT",FACE,{"disambiguationData":[TD([[makeQuery(id+"F7.imprint","IMPRINT",EDGE,{"derivedFrom":sQuery(id+"F7.wireOp",EDGE,"E5.33.29.0")}),1.0]])]});
            var Q955;
            Q955=makeQuery(id+"F7.imprint","IMPRINT",FACE,{"disambiguationData":[TD([[makeQuery(id+"F7.imprint","IMPRINT",EDGE,{"derivedFrom":sQuery(id+"F7.wireOp",EDGE,"E5.33.22.0")}),1.0]])]});
            var Q956;
            Q956=makeQuery(id+"F7.imprint","IMPRINT",FACE,{"disambiguationData":[TD([[makeQuery(id+"F7.imprint","IMPRINT",EDGE,{"derivedFrom":sQuery(id+"F7.wireOp",EDGE,"E5.33.6.0")}),1.0]])]});
            extrude(context, id + "F8", {"entities" : qUnion([Q0, Q1, Q2, Q3, Q4, Q5, Q6, Q7, Q8, Q9, Q10, Q11, Q12, Q13, Q14, Q15, Q16, Q17, Q18, Q19, Q20, Q21, Q22, Q23, Q24, Q25, Q26, Q27, Q28, Q29, Q30, Q31, Q32, Q33, Q34, Q35, Q36, Q37, Q38, Q39, Q40, Q41, Q42, Q43, Q44, Q45, Q46, Q47, Q48, Q49, Q50, Q51, Q52, Q53, Q54, Q55, Q56, Q57, Q58, Q59, Q60, Q61, Q62, Q63, Q64, Q65, Q66, Q67, Q68, Q69, Q70, Q71, Q72, Q73, Q74, Q75, Q76, Q77, Q78, Q79, Q80, Q81, Q82, Q83, Q84, Q85, Q86, Q87, Q88, Q89, Q90, Q91, Q92, Q93, Q94, Q95, Q96, Q97, Q98, Q99, Q100, Q101, Q102, Q103, Q104, Q105, Q106, Q107, Q108, Q109, Q110, Q111, Q112, Q113, Q114, Q115, Q116, Q117, Q118, Q119, Q120, Q121, Q122, Q123, Q124, Q125, Q126, Q127, Q128, Q129, Q130, Q131, Q132, Q133, Q134, Q135, Q136, Q137, Q138, Q139, Q140, Q141, Q142, Q143, Q144, Q145, Q146, Q147, Q148, Q149, Q150, Q151, Q152, Q153, Q154, Q155, Q156, Q157, Q158, Q159, Q160, Q161, Q162, Q163, Q164, Q165, Q166, Q167, Q168, Q169, Q170, Q171, Q172, Q173, Q174, Q175, Q176, Q177, Q178, Q179, Q180, Q181, Q182, Q183, Q184, Q185, Q186, Q187, Q188, Q189, Q190, Q191, Q192, Q193, Q194, Q195, Q196, Q197, Q198, Q199, Q200, Q201, Q202, Q203, Q204, Q205, Q206, Q207, Q208, Q209, Q210, Q211, Q212, Q213, Q214, Q215, Q216, Q217, Q218, Q219, Q220, Q221, Q222, Q223, Q224, Q225, Q226, Q227, Q228, Q229, Q230, Q231, Q232, Q233, Q234, Q235, Q236, Q237, Q238, Q239, Q240, Q241, Q242, Q243, Q244, Q245, Q246, Q247, Q248, Q249, Q250, Q251, Q252, Q253, Q254, Q255, Q256, Q257, Q258, Q259, Q260, Q261, Q262, Q263, Q264, Q265, Q266, Q267, Q268, Q269, Q270, Q271, Q272, Q273, Q274, Q275, Q276, Q277, Q278, Q279, Q280, Q281, Q282, Q283, Q284, Q285, Q286, Q287, Q288, Q289, Q290, Q291, Q292, Q293, Q294, Q295, Q296, Q297, Q298, Q299, Q300, Q301, Q302, Q303, Q304, Q305, Q306, Q307, Q308, Q309, Q310, Q311, Q312, Q313, Q314, Q315, Q316, Q317, Q318, Q319, Q320, Q321, Q322, Q323, Q324, Q325, Q326, Q327, Q328, Q329, Q330, Q331, Q332, Q333, Q334, Q335, Q336, Q337, Q338, Q339, Q340, Q341, Q342, Q343, Q344, Q345, Q346, Q347, Q348, Q349, Q350, Q351, Q352, Q353, Q354, Q355, Q356, Q357, Q358, Q359, Q360, Q361, Q362, Q363, Q364, Q365, Q366, Q367, Q368, Q369, Q370, Q371, Q372, Q373, Q374, Q375, Q376, Q377, Q378, Q379, Q380, Q381, Q382, Q383, Q384, Q385, Q386, Q387, Q388, Q389, Q390, Q391, Q392, Q393, Q394, Q395, Q396, Q397, Q398, Q399, Q400, Q401, Q402, Q403, Q404, Q405, Q406, Q407, Q408, Q409, Q410, Q411, Q412, Q413, Q414, Q415, Q416, Q417, Q418, Q419, Q420, Q421, Q422, Q423, Q424, Q425, Q426, Q427, Q428, Q429, Q430, Q431, Q432, Q433, Q434, Q435, Q436, Q437, Q438, Q439, Q440, Q441, Q442, Q443, Q444, Q445, Q446, Q447, Q448, Q449, Q450, Q451, Q452, Q453, Q454, Q455, Q456, Q457, Q458, Q459, Q460, Q461, Q462, Q463, Q464, Q465, Q466, Q467, Q468, Q469, Q470, Q471, Q472, Q473, Q474, Q475, Q476, Q477, Q478, Q479, Q480, Q481, Q482, Q483, Q484, Q485, Q486, Q487, Q488, Q489, Q490, Q491, Q492, Q493, Q494, Q495, Q496, Q497, Q498, Q499, Q500, Q501, Q502, Q503, Q504, Q505, Q506, Q507, Q508, Q509, Q510, Q511, Q512, Q513, Q514, Q515, Q516, Q517, Q518, Q519, Q520, Q521, Q522, Q523, Q524, Q525, Q526, Q527, Q528, Q529, Q530, Q531, Q532, Q533, Q534, Q535, Q536, Q537, Q538, Q539, Q540, Q541, Q542, Q543, Q544, Q545, Q546, Q547, Q548, Q549, Q550, Q551, Q552, Q553, Q554, Q555, Q556, Q557, Q558, Q559, Q560, Q561, Q562, Q563, Q564, Q565, Q566, Q567, Q568, Q569, Q570, Q571, Q572, Q573, Q574, Q575, Q576, Q577, Q578, Q579, Q580, Q581, Q582, Q583, Q584, Q585, Q586, Q587, Q588, Q589, Q590, Q591, Q592, Q593, Q594, Q595, Q596, Q597, Q598, Q599, Q600, Q601, Q602, Q603, Q604, Q605, Q606, Q607, Q608, Q609, Q610, Q611, Q612, Q613, Q614, Q615, Q616, Q617, Q618, Q619, Q620, Q621, Q622, Q623, Q624, Q625, Q626, Q627, Q628, Q629, Q630, Q631, Q632, Q633, Q634, Q635, Q636, Q637, Q638, Q639, Q640, Q641, Q642, Q643, Q644, Q645, Q646, Q647, Q648, Q649, Q650, Q651, Q652, Q653, Q654, Q655, Q656, Q657, Q658, Q659, Q660, Q661, Q662, Q663, Q664, Q665, Q666, Q667, Q668, Q669, Q670, Q671, Q672, Q673, Q674, Q675, Q676, Q677, Q678, Q679, Q680, Q681, Q682, Q683, Q684, Q685, Q686, Q687, Q688, Q689, Q690, Q691, Q692, Q693, Q694, Q695, Q696, Q697, Q698, Q699, Q700, Q701, Q702, Q703, Q704, Q705, Q706, Q707, Q708, Q709, Q710, Q711, Q712, Q713, Q714, Q715, Q716, Q717, Q718, Q719, Q720, Q721, Q722, Q723, Q724, Q725, Q726, Q727, Q728, Q729, Q730, Q731, Q732, Q733, Q734, Q735, Q736, Q737, Q738, Q739, Q740, Q741, Q742, Q743, Q744, Q745, Q746, Q747, Q748, Q749, Q750, Q751, Q752, Q753, Q754, Q755, Q756, Q757, Q758, Q759, Q760, Q761, Q762, Q763, Q764, Q765, Q766, Q767, Q768, Q769, Q770, Q771, Q772, Q773, Q774, Q775, Q776, Q777, Q778, Q779, Q780, Q781, Q782, Q783, Q784, Q785, Q786, Q787, Q788, Q789, Q790, Q791, Q792, Q793, Q794, Q795, Q796, Q797, Q798, Q799, Q800, Q801, Q802, Q803, Q804, Q805, Q806, Q807, Q808, Q809, Q810, Q811, Q812, Q813, Q814, Q815, Q816, Q817, Q818, Q819, Q820, Q821, Q822, Q823, Q824, Q825, Q826, Q827, Q828, Q829, Q830, Q831, Q832, Q833, Q834, Q835, Q836, Q837, Q838, Q839, Q840, Q841, Q842, Q843, Q844, Q845, Q846, Q847, Q848, Q849, Q850, Q851, Q852, Q853, Q854, Q855, Q856, Q857, Q858, Q859, Q860, Q861, Q862, Q863, Q864, Q865, Q866, Q867, Q868, Q869, Q870, Q871, Q872, Q873, Q874, Q875, Q876, Q877, Q878, Q879, Q880, Q881, Q882, Q883, Q884, Q885, Q886, Q887, Q888, Q889, Q890, Q891, Q892, Q893, Q894, Q895, Q896, Q897, Q898, Q899, Q900, Q901, Q902, Q903, Q904, Q905, Q906, Q907, Q908, Q909, Q910, Q911, Q912, Q913, Q914, Q915, Q916, Q917, Q918, Q919, Q920, Q921, Q922, Q923, Q924, Q925, Q926, Q927, Q928, Q929, Q930, Q931, Q932, Q933, Q934, Q935, Q936, Q937, Q938, Q939, Q940, Q941, Q942, Q943, Q944, Q945, Q946, Q947, Q948, Q949, Q950, Q951, Q952, Q953, Q954, Q955, Q956]), "operationType" : NewBodyOperationType.REMOVE, "oppositeDirection" : true, "depth" : 25.4 * mm});
        }
        {
            var Q0;
            Q0=makeQuery(id+"F4.opExtrude","CAP_FACE",FACE,{"disambiguationData":[OSD([sQuery(id+"F3.wireOp",EDGE,"E1")])],"isStart":false});
            extrude(context, id + "F9", {"entities" : qUnion([Q0]), "operationType" : NewBodyOperationType.REMOVE, "oppositeDirection" : true, "depth" : 38.1 * mm});
        }
    });
